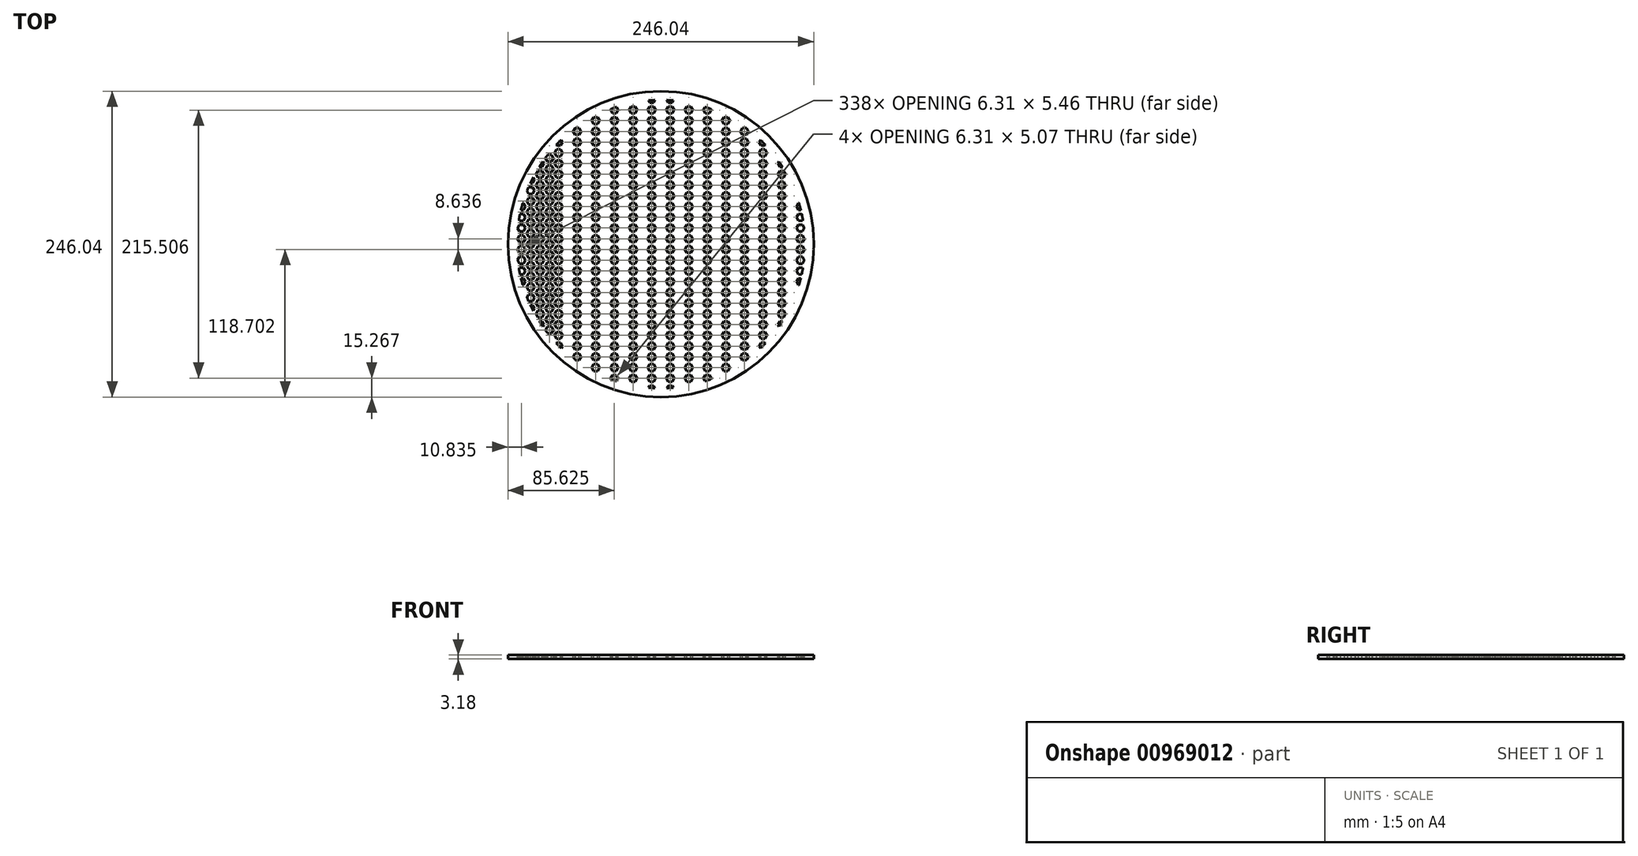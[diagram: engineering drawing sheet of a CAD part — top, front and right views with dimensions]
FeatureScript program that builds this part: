
annotation { "Feature Type Name" : "Feature", "Feature Type Description" : "" }
export const myFeature = defineFeature(function(context is Context, id is Id, definition is map)
    precondition{}
    {
        {
            var Q0;
            Q0=qCreatedBy(makeId("Top.planeOp"),FACE);
            var sketch = newSketch(context, id + "F0", { "sketchPlane" : qUnion([Q0])});
            skCircle(sketch, "E0", {"center": v(0, 0) * mm, "radius": 123.02 * mm});
            skSolve(sketch);
        }
        {
            var Q0;
            Q0=qSketchRegion(id+"F0",true);
            extrude(context, id + "F1", {"entities" : qUnion([Q0]), "depth" : 3.17 * mm, "offsetDistance" : 25.4 * mm});
        }
        {
            var Q0;
            Q0=makeQuery(id+"F1.opExtrude","CAP_FACE",FACE,{"disambiguationData":[OSD([sQuery(id+"F0.wireOp",EDGE,"E0")])],"isStart":false});
            var sketch = newSketch(context, id + "F2", { "sketchPlane" : qUnion([Q0])});
            skPoint(sketch, "E1.0.midPoint", {"position": v(-127.14, -131.13) * mm});
            skCircle(sketch, "E2.cCircle", {"center": v(-119.66, -129.54) * mm, "radius": 2.73 * mm, "construction": true});
            skLineSegment(sketch, "E2.0", {"start": v(-121.24, -126.8) * mm, "end": v(-118.09, -126.8) * mm});
            skLineSegment(sketch, "E2.1", {"start": v(-118.09, -126.8) * mm, "end": v(-116.51, -129.54) * mm});
            skLineSegment(sketch, "E2.2", {"start": v(-116.51, -129.54) * mm, "end": v(-118.09, -132.27) * mm});
            skLineSegment(sketch, "E2.3", {"start": v(-118.09, -132.27) * mm, "end": v(-121.24, -132.27) * mm});
            skLineSegment(sketch, "E2.4", {"start": v(-121.24, -132.27) * mm, "end": v(-122.82, -129.54) * mm});
            skLineSegment(sketch, "E2.5", {"start": v(-122.82, -129.54) * mm, "end": v(-121.24, -126.8) * mm});
            skPoint(sketch, "E2.0.midPoint", {"position": v(-119.66, -126.8) * mm});
            skLineSegment(sketch, "E3.0.2.0", {"start": v(-128.72, -113.86) * mm, "end": v(-125.57, -113.86) * mm});
            skLineSegment(sketch, "E3.0.2.1", {"start": v(-125.57, -113.86) * mm, "end": v(-124, -116.59) * mm});
            skLineSegment(sketch, "E3.0.2.2", {"start": v(-124, -116.59) * mm, "end": v(-125.57, -119.32) * mm});
            skCircle(sketch, "E3.0.2.3", {"center": v(-127.14, -116.59) * mm, "radius": 2.73 * mm, "construction": true});
            skLineSegment(sketch, "E3.0.2.4", {"start": v(-125.57, -119.32) * mm, "end": v(-128.72, -119.32) * mm});
            skLineSegment(sketch, "E3.0.2.5", {"start": v(-128.72, -119.32) * mm, "end": v(-130.3, -116.59) * mm});
            skLineSegment(sketch, "E3.0.2.6", {"start": v(-130.3, -116.59) * mm, "end": v(-128.72, -113.86) * mm});
            skLineSegment(sketch, "E3.1.0.0", {"start": v(-113.76, -131.13) * mm, "end": v(-110.6, -131.13) * mm});
            skLineSegment(sketch, "E3.1.0.1", {"start": v(-110.6, -131.13) * mm, "end": v(-109.03, -133.86) * mm});
            skLineSegment(sketch, "E3.1.0.2", {"start": v(-109.03, -133.86) * mm, "end": v(-110.6, -136.59) * mm});
            skCircle(sketch, "E3.1.0.3", {"center": v(-112.19, -133.86) * mm, "radius": 2.73 * mm, "construction": true});
            skLineSegment(sketch, "E3.1.0.4", {"start": v(-110.6, -136.59) * mm, "end": v(-113.76, -136.59) * mm});
            skLineSegment(sketch, "E3.1.0.5", {"start": v(-113.76, -136.59) * mm, "end": v(-115.34, -133.86) * mm});
            skLineSegment(sketch, "E3.1.0.6", {"start": v(-115.34, -133.86) * mm, "end": v(-113.76, -131.13) * mm});
            skLineSegment(sketch, "E3.1.1.0", {"start": v(-113.76, -122.5) * mm, "end": v(-110.6, -122.5) * mm});
            skLineSegment(sketch, "E3.1.1.1", {"start": v(-110.6, -122.5) * mm, "end": v(-109.03, -125.22) * mm});
            skLineSegment(sketch, "E3.1.1.2", {"start": v(-109.03, -125.22) * mm, "end": v(-110.6, -127.95) * mm});
            skCircle(sketch, "E3.1.1.3", {"center": v(-112.19, -125.22) * mm, "radius": 2.73 * mm, "construction": true});
            skLineSegment(sketch, "E3.1.1.4", {"start": v(-110.6, -127.95) * mm, "end": v(-113.76, -127.95) * mm});
            skLineSegment(sketch, "E3.1.1.5", {"start": v(-113.76, -127.95) * mm, "end": v(-115.34, -125.22) * mm});
            skLineSegment(sketch, "E3.1.1.6", {"start": v(-115.34, -125.22) * mm, "end": v(-113.76, -122.5) * mm});
            skLineSegment(sketch, "E3.1.2.0", {"start": v(-113.76, -113.86) * mm, "end": v(-110.6, -113.86) * mm});
            skLineSegment(sketch, "E3.1.2.1", {"start": v(-110.6, -113.86) * mm, "end": v(-109.03, -116.59) * mm});
            skLineSegment(sketch, "E3.1.2.2", {"start": v(-109.03, -116.59) * mm, "end": v(-110.6, -119.32) * mm});
            skCircle(sketch, "E3.1.2.3", {"center": v(-112.19, -116.59) * mm, "radius": 2.73 * mm, "construction": true});
            skLineSegment(sketch, "E3.1.2.4", {"start": v(-110.6, -119.32) * mm, "end": v(-113.76, -119.32) * mm});
            skLineSegment(sketch, "E3.1.2.5", {"start": v(-113.76, -119.32) * mm, "end": v(-115.34, -116.59) * mm});
            skLineSegment(sketch, "E3.1.2.6", {"start": v(-115.34, -116.59) * mm, "end": v(-113.76, -113.86) * mm});
            skLineSegment(sketch, "E3.2.0.0", {"start": v(-98.8, -131.13) * mm, "end": v(-95.65, -131.13) * mm});
            skLineSegment(sketch, "E3.2.0.1", {"start": v(-95.65, -131.13) * mm, "end": v(-94.07, -133.86) * mm});
            skLineSegment(sketch, "E3.2.0.2", {"start": v(-94.07, -133.86) * mm, "end": v(-95.65, -136.59) * mm});
            skCircle(sketch, "E3.2.0.3", {"center": v(-97.23, -133.86) * mm, "radius": 2.73 * mm, "construction": true});
            skLineSegment(sketch, "E3.2.0.4", {"start": v(-95.65, -136.59) * mm, "end": v(-98.8, -136.59) * mm});
            skLineSegment(sketch, "E3.2.0.5", {"start": v(-98.8, -136.59) * mm, "end": v(-100.38, -133.86) * mm});
            skLineSegment(sketch, "E3.2.0.6", {"start": v(-100.38, -133.86) * mm, "end": v(-98.8, -131.13) * mm});
            skLineSegment(sketch, "E3.2.1.0", {"start": v(-98.8, -122.5) * mm, "end": v(-95.65, -122.5) * mm});
            skLineSegment(sketch, "E3.2.1.1", {"start": v(-95.65, -122.5) * mm, "end": v(-94.07, -125.22) * mm});
            skLineSegment(sketch, "E3.2.1.2", {"start": v(-94.07, -125.22) * mm, "end": v(-95.65, -127.95) * mm});
            skCircle(sketch, "E3.2.1.3", {"center": v(-97.23, -125.22) * mm, "radius": 2.73 * mm, "construction": true});
            skLineSegment(sketch, "E3.2.1.4", {"start": v(-95.65, -127.95) * mm, "end": v(-98.8, -127.95) * mm});
            skLineSegment(sketch, "E3.2.1.5", {"start": v(-98.8, -127.95) * mm, "end": v(-100.38, -125.22) * mm});
            skLineSegment(sketch, "E3.2.1.6", {"start": v(-100.38, -125.22) * mm, "end": v(-98.8, -122.5) * mm});
            skLineSegment(sketch, "E3.2.2.0", {"start": v(-98.8, -113.86) * mm, "end": v(-95.65, -113.86) * mm});
            skLineSegment(sketch, "E3.2.2.1", {"start": v(-95.65, -113.86) * mm, "end": v(-94.07, -116.59) * mm});
            skLineSegment(sketch, "E3.2.2.2", {"start": v(-94.07, -116.59) * mm, "end": v(-95.65, -119.32) * mm});
            skCircle(sketch, "E3.2.2.3", {"center": v(-97.23, -116.59) * mm, "radius": 2.73 * mm, "construction": true});
            skLineSegment(sketch, "E3.2.2.4", {"start": v(-95.65, -119.32) * mm, "end": v(-98.8, -119.32) * mm});
            skLineSegment(sketch, "E3.2.2.5", {"start": v(-98.8, -119.32) * mm, "end": v(-100.38, -116.59) * mm});
            skLineSegment(sketch, "E3.2.2.6", {"start": v(-100.38, -116.59) * mm, "end": v(-98.8, -113.86) * mm});
            skLineSegment(sketch, "E4.0.0.3", {"start": v(-128.72, -105.22) * mm, "end": v(-125.57, -105.22) * mm});
            skLineSegment(sketch, "E4.3.0.3", {"start": v(-125.57, -105.22) * mm, "end": v(-124, -107.95) * mm});
            skLineSegment(sketch, "E4.6.0.3", {"start": v(-124, -107.95) * mm, "end": v(-125.57, -110.68) * mm});
            skCircle(sketch, "E4.9.0.3", {"center": v(-127.14, -107.95) * mm, "radius": 2.73 * mm, "construction": true});
            skLineSegment(sketch, "E4.11.0.3", {"start": v(-125.57, -110.68) * mm, "end": v(-128.72, -110.68) * mm});
            skLineSegment(sketch, "E4.14.0.3", {"start": v(-128.72, -110.68) * mm, "end": v(-130.3, -107.95) * mm});
            skLineSegment(sketch, "E4.17.0.3", {"start": v(-130.3, -107.95) * mm, "end": v(-128.72, -105.22) * mm});
            skLineSegment(sketch, "E4.0.1.3", {"start": v(-113.76, -105.22) * mm, "end": v(-110.6, -105.22) * mm});
            skLineSegment(sketch, "E4.3.1.3", {"start": v(-110.6, -105.22) * mm, "end": v(-109.03, -107.95) * mm});
            skLineSegment(sketch, "E4.6.1.3", {"start": v(-109.03, -107.95) * mm, "end": v(-110.6, -110.68) * mm});
            skCircle(sketch, "E4.9.1.3", {"center": v(-112.19, -107.95) * mm, "radius": 2.73 * mm, "construction": true});
            skLineSegment(sketch, "E4.11.1.3", {"start": v(-110.6, -110.68) * mm, "end": v(-113.76, -110.68) * mm});
            skLineSegment(sketch, "E4.14.1.3", {"start": v(-113.76, -110.68) * mm, "end": v(-115.34, -107.95) * mm});
            skLineSegment(sketch, "E4.17.1.3", {"start": v(-115.34, -107.95) * mm, "end": v(-113.76, -105.22) * mm});
            skLineSegment(sketch, "E4.0.2.3", {"start": v(-98.8, -105.22) * mm, "end": v(-95.65, -105.22) * mm});
            skLineSegment(sketch, "E4.3.2.3", {"start": v(-95.65, -105.22) * mm, "end": v(-94.07, -107.95) * mm});
            skLineSegment(sketch, "E4.6.2.3", {"start": v(-94.07, -107.95) * mm, "end": v(-95.65, -110.68) * mm});
            skCircle(sketch, "E4.9.2.3", {"center": v(-97.23, -107.95) * mm, "radius": 2.73 * mm, "construction": true});
            skLineSegment(sketch, "E4.11.2.3", {"start": v(-95.65, -110.68) * mm, "end": v(-98.8, -110.68) * mm});
            skLineSegment(sketch, "E4.14.2.3", {"start": v(-98.8, -110.68) * mm, "end": v(-100.38, -107.95) * mm});
            skLineSegment(sketch, "E4.17.2.3", {"start": v(-100.38, -107.95) * mm, "end": v(-98.8, -105.22) * mm});
            skCircle(sketch, "E5.0.1.0", {"center": v(-119.66, -120.9) * mm, "radius": 2.73 * mm, "construction": true});
            skLineSegment(sketch, "E5.0.1.1", {"start": v(-122.82, -120.9) * mm, "end": v(-121.24, -118.17) * mm});
            skLineSegment(sketch, "E5.0.1.2", {"start": v(-121.24, -118.17) * mm, "end": v(-118.09, -118.17) * mm});
            skLineSegment(sketch, "E5.0.1.3", {"start": v(-118.09, -118.17) * mm, "end": v(-116.51, -120.9) * mm});
            skLineSegment(sketch, "E5.0.1.4", {"start": v(-116.51, -120.9) * mm, "end": v(-118.09, -123.63) * mm});
            skLineSegment(sketch, "E5.0.1.5", {"start": v(-118.09, -123.63) * mm, "end": v(-121.24, -123.63) * mm});
            skLineSegment(sketch, "E5.0.1.6", {"start": v(-121.24, -123.63) * mm, "end": v(-122.82, -120.9) * mm});
            skCircle(sketch, "E5.0.2.0", {"center": v(-119.66, -112.27) * mm, "radius": 2.73 * mm, "construction": true});
            skLineSegment(sketch, "E5.0.2.1", {"start": v(-122.82, -112.27) * mm, "end": v(-121.24, -109.54) * mm});
            skLineSegment(sketch, "E5.0.2.2", {"start": v(-121.24, -109.54) * mm, "end": v(-118.09, -109.54) * mm});
            skLineSegment(sketch, "E5.0.2.3", {"start": v(-118.09, -109.54) * mm, "end": v(-116.51, -112.27) * mm});
            skLineSegment(sketch, "E5.0.2.4", {"start": v(-116.51, -112.27) * mm, "end": v(-118.09, -115) * mm});
            skLineSegment(sketch, "E5.0.2.5", {"start": v(-118.09, -115) * mm, "end": v(-121.24, -115) * mm});
            skLineSegment(sketch, "E5.0.2.6", {"start": v(-121.24, -115) * mm, "end": v(-122.82, -112.27) * mm});
            skCircle(sketch, "E5.0.3.0", {"center": v(-119.66, -103.63) * mm, "radius": 2.73 * mm, "construction": true});
            skLineSegment(sketch, "E5.0.3.1", {"start": v(-122.82, -103.63) * mm, "end": v(-121.24, -100.9) * mm});
            skLineSegment(sketch, "E5.0.3.2", {"start": v(-121.24, -100.9) * mm, "end": v(-118.09, -100.9) * mm});
            skLineSegment(sketch, "E5.0.3.3", {"start": v(-118.09, -100.9) * mm, "end": v(-116.51, -103.63) * mm});
            skLineSegment(sketch, "E5.0.3.4", {"start": v(-116.51, -103.63) * mm, "end": v(-118.09, -106.36) * mm});
            skLineSegment(sketch, "E5.0.3.5", {"start": v(-118.09, -106.36) * mm, "end": v(-121.24, -106.36) * mm});
            skLineSegment(sketch, "E5.0.3.6", {"start": v(-121.24, -106.36) * mm, "end": v(-122.82, -103.63) * mm});
            skCircle(sketch, "E5.1.0.0", {"center": v(-104.7, -129.54) * mm, "radius": 2.73 * mm, "construction": true});
            skLineSegment(sketch, "E5.1.0.1", {"start": v(-107.86, -129.54) * mm, "end": v(-106.28, -126.8) * mm});
            skLineSegment(sketch, "E5.1.0.2", {"start": v(-106.28, -126.8) * mm, "end": v(-103.13, -126.8) * mm});
            skLineSegment(sketch, "E5.1.0.3", {"start": v(-103.13, -126.8) * mm, "end": v(-101.55, -129.54) * mm});
            skLineSegment(sketch, "E5.1.0.4", {"start": v(-101.55, -129.54) * mm, "end": v(-103.13, -132.27) * mm});
            skLineSegment(sketch, "E5.1.0.5", {"start": v(-103.13, -132.27) * mm, "end": v(-106.28, -132.27) * mm});
            skLineSegment(sketch, "E5.1.0.6", {"start": v(-106.28, -132.27) * mm, "end": v(-107.86, -129.54) * mm});
            skCircle(sketch, "E5.1.1.0", {"center": v(-104.7, -120.9) * mm, "radius": 2.73 * mm, "construction": true});
            skLineSegment(sketch, "E5.1.1.1", {"start": v(-107.86, -120.9) * mm, "end": v(-106.28, -118.17) * mm});
            skLineSegment(sketch, "E5.1.1.2", {"start": v(-106.28, -118.17) * mm, "end": v(-103.13, -118.17) * mm});
            skLineSegment(sketch, "E5.1.1.3", {"start": v(-103.13, -118.17) * mm, "end": v(-101.55, -120.9) * mm});
            skLineSegment(sketch, "E5.1.1.4", {"start": v(-101.55, -120.9) * mm, "end": v(-103.13, -123.63) * mm});
            skLineSegment(sketch, "E5.1.1.5", {"start": v(-103.13, -123.63) * mm, "end": v(-106.28, -123.63) * mm});
            skLineSegment(sketch, "E5.1.1.6", {"start": v(-106.28, -123.63) * mm, "end": v(-107.86, -120.9) * mm});
            skCircle(sketch, "E5.1.2.0", {"center": v(-104.7, -112.27) * mm, "radius": 2.73 * mm, "construction": true});
            skLineSegment(sketch, "E5.1.2.1", {"start": v(-107.86, -112.27) * mm, "end": v(-106.28, -109.54) * mm});
            skLineSegment(sketch, "E5.1.2.2", {"start": v(-106.28, -109.54) * mm, "end": v(-103.13, -109.54) * mm});
            skLineSegment(sketch, "E5.1.2.3", {"start": v(-103.13, -109.54) * mm, "end": v(-101.55, -112.27) * mm});
            skLineSegment(sketch, "E5.1.2.4", {"start": v(-101.55, -112.27) * mm, "end": v(-103.13, -115) * mm});
            skLineSegment(sketch, "E5.1.2.5", {"start": v(-103.13, -115) * mm, "end": v(-106.28, -115) * mm});
            skLineSegment(sketch, "E5.1.2.6", {"start": v(-106.28, -115) * mm, "end": v(-107.86, -112.27) * mm});
            skCircle(sketch, "E5.1.3.0", {"center": v(-104.7, -103.63) * mm, "radius": 2.73 * mm, "construction": true});
            skLineSegment(sketch, "E5.1.3.1", {"start": v(-107.86, -103.63) * mm, "end": v(-106.28, -100.9) * mm});
            skLineSegment(sketch, "E5.1.3.2", {"start": v(-106.28, -100.9) * mm, "end": v(-103.13, -100.9) * mm});
            skLineSegment(sketch, "E5.1.3.3", {"start": v(-103.13, -100.9) * mm, "end": v(-101.55, -103.63) * mm});
            skLineSegment(sketch, "E5.1.3.4", {"start": v(-101.55, -103.63) * mm, "end": v(-103.13, -106.36) * mm});
            skLineSegment(sketch, "E5.1.3.5", {"start": v(-103.13, -106.36) * mm, "end": v(-106.28, -106.36) * mm});
            skLineSegment(sketch, "E5.1.3.6", {"start": v(-106.28, -106.36) * mm, "end": v(-107.86, -103.63) * mm});
            skLineSegment(sketch, "E5.direction1", {"start": v(-121.24, -132.27) * mm, "end": v(-106.28, -132.27) * mm, "construction": true});
            skLineSegment(sketch, "E5.direction2", {"start": v(-121.24, -132.27) * mm, "end": v(-121.24, -123.63) * mm, "construction": true});
            skLineSegment(sketch, "E6.0.3.0", {"start": v(-83.85, -131.13) * mm, "end": v(-80.7, -131.13) * mm});
            skLineSegment(sketch, "E6.3.3.0", {"start": v(-80.7, -131.13) * mm, "end": v(-79.12, -133.86) * mm});
            skLineSegment(sketch, "E6.6.3.0", {"start": v(-79.12, -133.86) * mm, "end": v(-80.7, -136.59) * mm});
            skCircle(sketch, "E6.9.3.0", {"center": v(-82.27, -133.86) * mm, "radius": 2.73 * mm, "construction": true});
            skLineSegment(sketch, "E6.11.3.0", {"start": v(-80.7, -136.59) * mm, "end": v(-83.85, -136.59) * mm});
            skLineSegment(sketch, "E6.14.3.0", {"start": v(-83.85, -136.59) * mm, "end": v(-85.42, -133.86) * mm});
            skLineSegment(sketch, "E6.17.3.0", {"start": v(-85.42, -133.86) * mm, "end": v(-83.85, -131.13) * mm});
            skLineSegment(sketch, "E6.0.3.1", {"start": v(-83.85, -122.5) * mm, "end": v(-80.7, -122.5) * mm});
            skLineSegment(sketch, "E6.3.3.1", {"start": v(-80.7, -122.5) * mm, "end": v(-79.12, -125.22) * mm});
            skLineSegment(sketch, "E6.6.3.1", {"start": v(-79.12, -125.22) * mm, "end": v(-80.7, -127.95) * mm});
            skCircle(sketch, "E6.9.3.1", {"center": v(-82.27, -125.22) * mm, "radius": 2.73 * mm, "construction": true});
            skLineSegment(sketch, "E6.11.3.1", {"start": v(-80.7, -127.95) * mm, "end": v(-83.85, -127.95) * mm});
            skLineSegment(sketch, "E6.14.3.1", {"start": v(-83.85, -127.95) * mm, "end": v(-85.42, -125.22) * mm});
            skLineSegment(sketch, "E6.17.3.1", {"start": v(-85.42, -125.22) * mm, "end": v(-83.85, -122.5) * mm});
            skLineSegment(sketch, "E6.0.3.2", {"start": v(-83.85, -113.86) * mm, "end": v(-80.7, -113.86) * mm});
            skLineSegment(sketch, "E6.3.3.2", {"start": v(-80.7, -113.86) * mm, "end": v(-79.12, -116.59) * mm});
            skLineSegment(sketch, "E6.6.3.2", {"start": v(-79.12, -116.59) * mm, "end": v(-80.7, -119.32) * mm});
            skCircle(sketch, "E6.9.3.2", {"center": v(-82.27, -116.59) * mm, "radius": 2.73 * mm, "construction": true});
            skLineSegment(sketch, "E6.11.3.2", {"start": v(-80.7, -119.32) * mm, "end": v(-83.85, -119.32) * mm});
            skLineSegment(sketch, "E6.14.3.2", {"start": v(-83.85, -119.32) * mm, "end": v(-85.42, -116.59) * mm});
            skLineSegment(sketch, "E6.17.3.2", {"start": v(-85.42, -116.59) * mm, "end": v(-83.85, -113.86) * mm});
            skLineSegment(sketch, "E6.0.3.3", {"start": v(-83.85, -105.22) * mm, "end": v(-80.7, -105.22) * mm});
            skLineSegment(sketch, "E6.3.3.3", {"start": v(-80.7, -105.22) * mm, "end": v(-79.12, -107.95) * mm});
            skLineSegment(sketch, "E6.6.3.3", {"start": v(-79.12, -107.95) * mm, "end": v(-80.7, -110.68) * mm});
            skCircle(sketch, "E6.9.3.3", {"center": v(-82.27, -107.95) * mm, "radius": 2.73 * mm, "construction": true});
            skLineSegment(sketch, "E6.11.3.3", {"start": v(-80.7, -110.68) * mm, "end": v(-83.85, -110.68) * mm});
            skLineSegment(sketch, "E6.14.3.3", {"start": v(-83.85, -110.68) * mm, "end": v(-85.42, -107.95) * mm});
            skLineSegment(sketch, "E6.17.3.3", {"start": v(-85.42, -107.95) * mm, "end": v(-83.85, -105.22) * mm});
            skLineSegment(sketch, "E6.0.4.0", {"start": v(-68.89, -131.13) * mm, "end": v(-65.73, -131.13) * mm});
            skLineSegment(sketch, "E6.3.4.0", {"start": v(-65.73, -131.13) * mm, "end": v(-64.16, -133.86) * mm});
            skLineSegment(sketch, "E6.6.4.0", {"start": v(-64.16, -133.86) * mm, "end": v(-65.73, -136.59) * mm});
            skCircle(sketch, "E6.9.4.0", {"center": v(-67.31, -133.86) * mm, "radius": 2.73 * mm, "construction": true});
            skLineSegment(sketch, "E6.11.4.0", {"start": v(-65.73, -136.59) * mm, "end": v(-68.89, -136.59) * mm});
            skLineSegment(sketch, "E6.14.4.0", {"start": v(-68.89, -136.59) * mm, "end": v(-70.46, -133.86) * mm});
            skLineSegment(sketch, "E6.17.4.0", {"start": v(-70.46, -133.86) * mm, "end": v(-68.89, -131.13) * mm});
            skLineSegment(sketch, "E6.0.4.1", {"start": v(-68.89, -122.5) * mm, "end": v(-65.73, -122.5) * mm});
            skLineSegment(sketch, "E6.3.4.1", {"start": v(-65.73, -122.5) * mm, "end": v(-64.16, -125.22) * mm});
            skLineSegment(sketch, "E6.6.4.1", {"start": v(-64.16, -125.22) * mm, "end": v(-65.73, -127.95) * mm});
            skCircle(sketch, "E6.9.4.1", {"center": v(-67.31, -125.22) * mm, "radius": 2.73 * mm, "construction": true});
            skLineSegment(sketch, "E6.11.4.1", {"start": v(-65.73, -127.95) * mm, "end": v(-68.89, -127.95) * mm});
            skLineSegment(sketch, "E6.14.4.1", {"start": v(-68.89, -127.95) * mm, "end": v(-70.46, -125.22) * mm});
            skLineSegment(sketch, "E6.17.4.1", {"start": v(-70.46, -125.22) * mm, "end": v(-68.89, -122.5) * mm});
            skLineSegment(sketch, "E6.0.4.2", {"start": v(-68.89, -113.86) * mm, "end": v(-65.73, -113.86) * mm});
            skLineSegment(sketch, "E6.3.4.2", {"start": v(-65.73, -113.86) * mm, "end": v(-64.16, -116.59) * mm});
            skLineSegment(sketch, "E6.6.4.2", {"start": v(-64.16, -116.59) * mm, "end": v(-65.73, -119.32) * mm});
            skCircle(sketch, "E6.9.4.2", {"center": v(-67.31, -116.59) * mm, "radius": 2.73 * mm, "construction": true});
            skLineSegment(sketch, "E6.11.4.2", {"start": v(-65.73, -119.32) * mm, "end": v(-68.89, -119.32) * mm});
            skLineSegment(sketch, "E6.14.4.2", {"start": v(-68.89, -119.32) * mm, "end": v(-70.46, -116.59) * mm});
            skLineSegment(sketch, "E6.17.4.2", {"start": v(-70.46, -116.59) * mm, "end": v(-68.89, -113.86) * mm});
            skLineSegment(sketch, "E6.0.4.3", {"start": v(-68.89, -105.22) * mm, "end": v(-65.73, -105.22) * mm});
            skLineSegment(sketch, "E6.3.4.3", {"start": v(-65.73, -105.22) * mm, "end": v(-64.16, -107.95) * mm});
            skLineSegment(sketch, "E6.6.4.3", {"start": v(-64.16, -107.95) * mm, "end": v(-65.73, -110.68) * mm});
            skCircle(sketch, "E6.9.4.3", {"center": v(-67.31, -107.95) * mm, "radius": 2.73 * mm, "construction": true});
            skLineSegment(sketch, "E6.11.4.3", {"start": v(-65.73, -110.68) * mm, "end": v(-68.89, -110.68) * mm});
            skLineSegment(sketch, "E6.14.4.3", {"start": v(-68.89, -110.68) * mm, "end": v(-70.46, -107.95) * mm});
            skLineSegment(sketch, "E6.17.4.3", {"start": v(-70.46, -107.95) * mm, "end": v(-68.89, -105.22) * mm});
            skLineSegment(sketch, "E6.0.5.0", {"start": v(-53.93, -131.13) * mm, "end": v(-50.78, -131.13) * mm});
            skLineSegment(sketch, "E6.3.5.0", {"start": v(-50.78, -131.13) * mm, "end": v(-49.2, -133.86) * mm});
            skLineSegment(sketch, "E6.6.5.0", {"start": v(-49.2, -133.86) * mm, "end": v(-50.78, -136.59) * mm});
            skCircle(sketch, "E6.9.5.0", {"center": v(-52.35, -133.86) * mm, "radius": 2.73 * mm, "construction": true});
            skLineSegment(sketch, "E6.11.5.0", {"start": v(-50.78, -136.59) * mm, "end": v(-53.93, -136.59) * mm});
            skLineSegment(sketch, "E6.14.5.0", {"start": v(-53.93, -136.59) * mm, "end": v(-55.5, -133.86) * mm});
            skLineSegment(sketch, "E6.17.5.0", {"start": v(-55.5, -133.86) * mm, "end": v(-53.93, -131.13) * mm});
            skLineSegment(sketch, "E6.0.5.1", {"start": v(-53.93, -122.5) * mm, "end": v(-50.78, -122.5) * mm});
            skLineSegment(sketch, "E6.3.5.1", {"start": v(-50.78, -122.5) * mm, "end": v(-49.2, -125.22) * mm});
            skLineSegment(sketch, "E6.6.5.1", {"start": v(-49.2, -125.22) * mm, "end": v(-50.78, -127.95) * mm});
            skCircle(sketch, "E6.9.5.1", {"center": v(-52.35, -125.22) * mm, "radius": 2.73 * mm, "construction": true});
            skLineSegment(sketch, "E6.11.5.1", {"start": v(-50.78, -127.95) * mm, "end": v(-53.93, -127.95) * mm});
            skLineSegment(sketch, "E6.14.5.1", {"start": v(-53.93, -127.95) * mm, "end": v(-55.5, -125.22) * mm});
            skLineSegment(sketch, "E6.17.5.1", {"start": v(-55.5, -125.22) * mm, "end": v(-53.93, -122.5) * mm});
            skLineSegment(sketch, "E6.0.5.2", {"start": v(-53.93, -113.86) * mm, "end": v(-50.78, -113.86) * mm});
            skLineSegment(sketch, "E6.3.5.2", {"start": v(-50.78, -113.86) * mm, "end": v(-49.2, -116.59) * mm});
            skLineSegment(sketch, "E6.6.5.2", {"start": v(-49.2, -116.59) * mm, "end": v(-50.78, -119.32) * mm});
            skCircle(sketch, "E6.9.5.2", {"center": v(-52.35, -116.59) * mm, "radius": 2.73 * mm, "construction": true});
            skLineSegment(sketch, "E6.11.5.2", {"start": v(-50.78, -119.32) * mm, "end": v(-53.93, -119.32) * mm});
            skLineSegment(sketch, "E6.14.5.2", {"start": v(-53.93, -119.32) * mm, "end": v(-55.5, -116.59) * mm});
            skLineSegment(sketch, "E6.17.5.2", {"start": v(-55.5, -116.59) * mm, "end": v(-53.93, -113.86) * mm});
            skLineSegment(sketch, "E6.0.5.3", {"start": v(-53.93, -105.22) * mm, "end": v(-50.78, -105.22) * mm});
            skLineSegment(sketch, "E6.3.5.3", {"start": v(-50.78, -105.22) * mm, "end": v(-49.2, -107.95) * mm});
            skLineSegment(sketch, "E6.6.5.3", {"start": v(-49.2, -107.95) * mm, "end": v(-50.78, -110.68) * mm});
            skCircle(sketch, "E6.9.5.3", {"center": v(-52.35, -107.95) * mm, "radius": 2.73 * mm, "construction": true});
            skLineSegment(sketch, "E6.11.5.3", {"start": v(-50.78, -110.68) * mm, "end": v(-53.93, -110.68) * mm});
            skLineSegment(sketch, "E6.14.5.3", {"start": v(-53.93, -110.68) * mm, "end": v(-55.5, -107.95) * mm});
            skLineSegment(sketch, "E6.17.5.3", {"start": v(-55.5, -107.95) * mm, "end": v(-53.93, -105.22) * mm});
            skCircle(sketch, "E7.0.2.0", {"center": v(-89.75, -129.54) * mm, "radius": 2.73 * mm, "construction": true});
            skLineSegment(sketch, "E7.2.2.0", {"start": v(-92.9, -129.54) * mm, "end": v(-91.32, -126.8) * mm});
            skLineSegment(sketch, "E7.5.2.0", {"start": v(-91.32, -126.8) * mm, "end": v(-88.17, -126.8) * mm});
            skLineSegment(sketch, "E7.8.2.0", {"start": v(-88.17, -126.8) * mm, "end": v(-86.6, -129.54) * mm});
            skLineSegment(sketch, "E7.11.2.0", {"start": v(-86.6, -129.54) * mm, "end": v(-88.17, -132.27) * mm});
            skLineSegment(sketch, "E7.14.2.0", {"start": v(-88.17, -132.27) * mm, "end": v(-91.32, -132.27) * mm});
            skLineSegment(sketch, "E7.17.2.0", {"start": v(-91.32, -132.27) * mm, "end": v(-92.9, -129.54) * mm});
            skCircle(sketch, "E7.0.2.1", {"center": v(-89.75, -120.9) * mm, "radius": 2.73 * mm, "construction": true});
            skLineSegment(sketch, "E7.2.2.1", {"start": v(-92.9, -120.9) * mm, "end": v(-91.32, -118.17) * mm});
            skLineSegment(sketch, "E7.5.2.1", {"start": v(-91.32, -118.17) * mm, "end": v(-88.17, -118.17) * mm});
            skLineSegment(sketch, "E7.8.2.1", {"start": v(-88.17, -118.17) * mm, "end": v(-86.6, -120.9) * mm});
            skLineSegment(sketch, "E7.11.2.1", {"start": v(-86.6, -120.9) * mm, "end": v(-88.17, -123.63) * mm});
            skLineSegment(sketch, "E7.14.2.1", {"start": v(-88.17, -123.63) * mm, "end": v(-91.32, -123.63) * mm});
            skLineSegment(sketch, "E7.17.2.1", {"start": v(-91.32, -123.63) * mm, "end": v(-92.9, -120.9) * mm});
            skCircle(sketch, "E7.0.2.2", {"center": v(-89.75, -112.27) * mm, "radius": 2.73 * mm, "construction": true});
            skLineSegment(sketch, "E7.2.2.2", {"start": v(-92.9, -112.27) * mm, "end": v(-91.32, -109.54) * mm});
            skLineSegment(sketch, "E7.5.2.2", {"start": v(-91.32, -109.54) * mm, "end": v(-88.17, -109.54) * mm});
            skLineSegment(sketch, "E7.8.2.2", {"start": v(-88.17, -109.54) * mm, "end": v(-86.6, -112.27) * mm});
            skLineSegment(sketch, "E7.11.2.2", {"start": v(-86.6, -112.27) * mm, "end": v(-88.17, -115) * mm});
            skLineSegment(sketch, "E7.14.2.2", {"start": v(-88.17, -115) * mm, "end": v(-91.32, -115) * mm});
            skLineSegment(sketch, "E7.17.2.2", {"start": v(-91.32, -115) * mm, "end": v(-92.9, -112.27) * mm});
            skCircle(sketch, "E7.0.2.3", {"center": v(-89.75, -103.63) * mm, "radius": 2.73 * mm, "construction": true});
            skLineSegment(sketch, "E7.2.2.3", {"start": v(-92.9, -103.63) * mm, "end": v(-91.32, -100.9) * mm});
            skLineSegment(sketch, "E7.5.2.3", {"start": v(-91.32, -100.9) * mm, "end": v(-88.17, -100.9) * mm});
            skLineSegment(sketch, "E7.8.2.3", {"start": v(-88.17, -100.9) * mm, "end": v(-86.6, -103.63) * mm});
            skLineSegment(sketch, "E7.11.2.3", {"start": v(-86.6, -103.63) * mm, "end": v(-88.17, -106.36) * mm});
            skLineSegment(sketch, "E7.14.2.3", {"start": v(-88.17, -106.36) * mm, "end": v(-91.32, -106.36) * mm});
            skLineSegment(sketch, "E7.17.2.3", {"start": v(-91.32, -106.36) * mm, "end": v(-92.9, -103.63) * mm});
            skLineSegment(sketch, "E8.0.0.4", {"start": v(-128.72, -96.58) * mm, "end": v(-125.57, -96.58) * mm});
            skLineSegment(sketch, "E8.3.0.4", {"start": v(-125.57, -96.58) * mm, "end": v(-124, -99.31) * mm});
            skLineSegment(sketch, "E8.6.0.4", {"start": v(-124, -99.31) * mm, "end": v(-125.57, -102.04) * mm});
            skCircle(sketch, "E8.9.0.4", {"center": v(-127.14, -99.31) * mm, "radius": 2.73 * mm, "construction": true});
            skLineSegment(sketch, "E8.11.0.4", {"start": v(-125.57, -102.04) * mm, "end": v(-128.72, -102.04) * mm});
            skLineSegment(sketch, "E8.14.0.4", {"start": v(-128.72, -102.04) * mm, "end": v(-130.3, -99.31) * mm});
            skLineSegment(sketch, "E8.17.0.4", {"start": v(-130.3, -99.31) * mm, "end": v(-128.72, -96.58) * mm});
            skLineSegment(sketch, "E8.0.0.5", {"start": v(-128.72, -87.95) * mm, "end": v(-125.57, -87.95) * mm});
            skLineSegment(sketch, "E8.3.0.5", {"start": v(-125.57, -87.95) * mm, "end": v(-124, -90.68) * mm});
            skLineSegment(sketch, "E8.6.0.5", {"start": v(-124, -90.68) * mm, "end": v(-125.57, -93.4) * mm});
            skCircle(sketch, "E8.9.0.5", {"center": v(-127.14, -90.68) * mm, "radius": 2.73 * mm, "construction": true});
            skLineSegment(sketch, "E8.11.0.5", {"start": v(-125.57, -93.4) * mm, "end": v(-128.72, -93.4) * mm});
            skLineSegment(sketch, "E8.14.0.5", {"start": v(-128.72, -93.4) * mm, "end": v(-130.3, -90.68) * mm});
            skLineSegment(sketch, "E8.17.0.5", {"start": v(-130.3, -90.68) * mm, "end": v(-128.72, -87.95) * mm});
            skLineSegment(sketch, "E8.0.0.6", {"start": v(-128.72, -79.31) * mm, "end": v(-125.57, -79.31) * mm});
            skLineSegment(sketch, "E8.3.0.6", {"start": v(-125.57, -79.31) * mm, "end": v(-124, -82.04) * mm});
            skLineSegment(sketch, "E8.6.0.6", {"start": v(-124, -82.04) * mm, "end": v(-125.57, -84.77) * mm});
            skCircle(sketch, "E8.9.0.6", {"center": v(-127.14, -82.04) * mm, "radius": 2.73 * mm, "construction": true});
            skLineSegment(sketch, "E8.11.0.6", {"start": v(-125.57, -84.77) * mm, "end": v(-128.72, -84.77) * mm});
            skLineSegment(sketch, "E8.14.0.6", {"start": v(-128.72, -84.77) * mm, "end": v(-130.3, -82.04) * mm});
            skLineSegment(sketch, "E8.17.0.6", {"start": v(-130.3, -82.04) * mm, "end": v(-128.72, -79.31) * mm});
            skLineSegment(sketch, "E8.0.0.7", {"start": v(-128.72, -70.68) * mm, "end": v(-125.57, -70.68) * mm});
            skLineSegment(sketch, "E8.3.0.7", {"start": v(-125.57, -70.68) * mm, "end": v(-124, -73.4) * mm});
            skLineSegment(sketch, "E8.6.0.7", {"start": v(-124, -73.4) * mm, "end": v(-125.57, -76.14) * mm});
            skCircle(sketch, "E8.9.0.7", {"center": v(-127.14, -73.4) * mm, "radius": 2.73 * mm, "construction": true});
            skLineSegment(sketch, "E8.11.0.7", {"start": v(-125.57, -76.14) * mm, "end": v(-128.72, -76.14) * mm});
            skLineSegment(sketch, "E8.14.0.7", {"start": v(-128.72, -76.14) * mm, "end": v(-130.3, -73.4) * mm});
            skLineSegment(sketch, "E8.17.0.7", {"start": v(-130.3, -73.4) * mm, "end": v(-128.72, -70.68) * mm});
            skLineSegment(sketch, "E8.0.1.4", {"start": v(-113.76, -96.58) * mm, "end": v(-110.6, -96.58) * mm});
            skLineSegment(sketch, "E8.3.1.4", {"start": v(-110.6, -96.58) * mm, "end": v(-109.03, -99.31) * mm});
            skLineSegment(sketch, "E8.6.1.4", {"start": v(-109.03, -99.31) * mm, "end": v(-110.6, -102.04) * mm});
            skCircle(sketch, "E8.9.1.4", {"center": v(-112.19, -99.31) * mm, "radius": 2.73 * mm, "construction": true});
            skLineSegment(sketch, "E8.11.1.4", {"start": v(-110.6, -102.04) * mm, "end": v(-113.76, -102.04) * mm});
            skLineSegment(sketch, "E8.14.1.4", {"start": v(-113.76, -102.04) * mm, "end": v(-115.34, -99.31) * mm});
            skLineSegment(sketch, "E8.17.1.4", {"start": v(-115.34, -99.31) * mm, "end": v(-113.76, -96.58) * mm});
            skLineSegment(sketch, "E8.0.1.5", {"start": v(-113.76, -87.95) * mm, "end": v(-110.6, -87.95) * mm});
            skLineSegment(sketch, "E8.3.1.5", {"start": v(-110.6, -87.95) * mm, "end": v(-109.03, -90.68) * mm});
            skLineSegment(sketch, "E8.6.1.5", {"start": v(-109.03, -90.68) * mm, "end": v(-110.6, -93.4) * mm});
            skCircle(sketch, "E8.9.1.5", {"center": v(-112.19, -90.68) * mm, "radius": 2.73 * mm, "construction": true});
            skLineSegment(sketch, "E8.11.1.5", {"start": v(-110.6, -93.4) * mm, "end": v(-113.76, -93.4) * mm});
            skLineSegment(sketch, "E8.14.1.5", {"start": v(-113.76, -93.4) * mm, "end": v(-115.34, -90.68) * mm});
            skLineSegment(sketch, "E8.17.1.5", {"start": v(-115.34, -90.68) * mm, "end": v(-113.76, -87.95) * mm});
            skLineSegment(sketch, "E8.0.1.6", {"start": v(-113.76, -79.31) * mm, "end": v(-110.6, -79.31) * mm});
            skLineSegment(sketch, "E8.3.1.6", {"start": v(-110.6, -79.31) * mm, "end": v(-109.03, -82.04) * mm});
            skLineSegment(sketch, "E8.6.1.6", {"start": v(-109.03, -82.04) * mm, "end": v(-110.6, -84.77) * mm});
            skCircle(sketch, "E8.9.1.6", {"center": v(-112.19, -82.04) * mm, "radius": 2.73 * mm, "construction": true});
            skLineSegment(sketch, "E8.11.1.6", {"start": v(-110.6, -84.77) * mm, "end": v(-113.76, -84.77) * mm});
            skLineSegment(sketch, "E8.14.1.6", {"start": v(-113.76, -84.77) * mm, "end": v(-115.34, -82.04) * mm});
            skLineSegment(sketch, "E8.17.1.6", {"start": v(-115.34, -82.04) * mm, "end": v(-113.76, -79.31) * mm});
            skLineSegment(sketch, "E8.0.1.7", {"start": v(-113.76, -70.68) * mm, "end": v(-110.6, -70.68) * mm});
            skLineSegment(sketch, "E8.3.1.7", {"start": v(-110.6, -70.68) * mm, "end": v(-109.03, -73.4) * mm});
            skLineSegment(sketch, "E8.6.1.7", {"start": v(-109.03, -73.4) * mm, "end": v(-110.6, -76.14) * mm});
            skCircle(sketch, "E8.9.1.7", {"center": v(-112.19, -73.4) * mm, "radius": 2.73 * mm, "construction": true});
            skLineSegment(sketch, "E8.11.1.7", {"start": v(-110.6, -76.14) * mm, "end": v(-113.76, -76.14) * mm});
            skLineSegment(sketch, "E8.14.1.7", {"start": v(-113.76, -76.14) * mm, "end": v(-115.34, -73.4) * mm});
            skLineSegment(sketch, "E8.17.1.7", {"start": v(-115.34, -73.4) * mm, "end": v(-113.76, -70.68) * mm});
            skLineSegment(sketch, "E8.0.2.4", {"start": v(-98.8, -96.58) * mm, "end": v(-95.65, -96.58) * mm});
            skLineSegment(sketch, "E8.3.2.4", {"start": v(-95.65, -96.58) * mm, "end": v(-94.07, -99.31) * mm});
            skLineSegment(sketch, "E8.6.2.4", {"start": v(-94.07, -99.31) * mm, "end": v(-95.65, -102.04) * mm});
            skCircle(sketch, "E8.9.2.4", {"center": v(-97.23, -99.31) * mm, "radius": 2.73 * mm, "construction": true});
            skLineSegment(sketch, "E8.11.2.4", {"start": v(-95.65, -102.04) * mm, "end": v(-98.8, -102.04) * mm});
            skLineSegment(sketch, "E8.14.2.4", {"start": v(-98.8, -102.04) * mm, "end": v(-100.38, -99.31) * mm});
            skLineSegment(sketch, "E8.17.2.4", {"start": v(-100.38, -99.31) * mm, "end": v(-98.8, -96.58) * mm});
            skLineSegment(sketch, "E8.0.2.5", {"start": v(-98.8, -87.95) * mm, "end": v(-95.65, -87.95) * mm});
            skLineSegment(sketch, "E8.3.2.5", {"start": v(-95.65, -87.95) * mm, "end": v(-94.07, -90.68) * mm});
            skLineSegment(sketch, "E8.6.2.5", {"start": v(-94.07, -90.68) * mm, "end": v(-95.65, -93.4) * mm});
            skCircle(sketch, "E8.9.2.5", {"center": v(-97.23, -90.68) * mm, "radius": 2.73 * mm, "construction": true});
            skLineSegment(sketch, "E8.11.2.5", {"start": v(-95.65, -93.4) * mm, "end": v(-98.8, -93.4) * mm});
            skLineSegment(sketch, "E8.14.2.5", {"start": v(-98.8, -93.4) * mm, "end": v(-100.38, -90.68) * mm});
            skLineSegment(sketch, "E8.17.2.5", {"start": v(-100.38, -90.68) * mm, "end": v(-98.8, -87.95) * mm});
            skLineSegment(sketch, "E8.0.2.6", {"start": v(-98.8, -79.31) * mm, "end": v(-95.65, -79.31) * mm});
            skLineSegment(sketch, "E8.3.2.6", {"start": v(-95.65, -79.31) * mm, "end": v(-94.07, -82.04) * mm});
            skLineSegment(sketch, "E8.6.2.6", {"start": v(-94.07, -82.04) * mm, "end": v(-95.65, -84.77) * mm});
            skCircle(sketch, "E8.9.2.6", {"center": v(-97.23, -82.04) * mm, "radius": 2.73 * mm, "construction": true});
            skLineSegment(sketch, "E8.11.2.6", {"start": v(-95.65, -84.77) * mm, "end": v(-98.8, -84.77) * mm});
            skLineSegment(sketch, "E8.14.2.6", {"start": v(-98.8, -84.77) * mm, "end": v(-100.38, -82.04) * mm});
            skLineSegment(sketch, "E8.17.2.6", {"start": v(-100.38, -82.04) * mm, "end": v(-98.8, -79.31) * mm});
            skLineSegment(sketch, "E8.0.2.7", {"start": v(-98.8, -70.68) * mm, "end": v(-95.65, -70.68) * mm});
            skLineSegment(sketch, "E8.3.2.7", {"start": v(-95.65, -70.68) * mm, "end": v(-94.07, -73.4) * mm});
            skLineSegment(sketch, "E8.6.2.7", {"start": v(-94.07, -73.4) * mm, "end": v(-95.65, -76.14) * mm});
            skCircle(sketch, "E8.9.2.7", {"center": v(-97.23, -73.4) * mm, "radius": 2.73 * mm, "construction": true});
            skLineSegment(sketch, "E8.11.2.7", {"start": v(-95.65, -76.14) * mm, "end": v(-98.8, -76.14) * mm});
            skLineSegment(sketch, "E8.14.2.7", {"start": v(-98.8, -76.14) * mm, "end": v(-100.38, -73.4) * mm});
            skLineSegment(sketch, "E8.17.2.7", {"start": v(-100.38, -73.4) * mm, "end": v(-98.8, -70.68) * mm});
            skLineSegment(sketch, "E8.0.3.4", {"start": v(-83.85, -96.58) * mm, "end": v(-80.7, -96.58) * mm});
            skLineSegment(sketch, "E8.3.3.4", {"start": v(-80.7, -96.58) * mm, "end": v(-79.12, -99.31) * mm});
            skLineSegment(sketch, "E8.6.3.4", {"start": v(-79.12, -99.31) * mm, "end": v(-80.7, -102.04) * mm});
            skCircle(sketch, "E8.9.3.4", {"center": v(-82.27, -99.31) * mm, "radius": 2.73 * mm, "construction": true});
            skLineSegment(sketch, "E8.11.3.4", {"start": v(-80.7, -102.04) * mm, "end": v(-83.85, -102.04) * mm});
            skLineSegment(sketch, "E8.14.3.4", {"start": v(-83.85, -102.04) * mm, "end": v(-85.42, -99.31) * mm});
            skLineSegment(sketch, "E8.17.3.4", {"start": v(-85.42, -99.31) * mm, "end": v(-83.85, -96.58) * mm});
            skLineSegment(sketch, "E8.0.3.5", {"start": v(-83.85, -87.95) * mm, "end": v(-80.7, -87.95) * mm});
            skLineSegment(sketch, "E8.3.3.5", {"start": v(-80.7, -87.95) * mm, "end": v(-79.12, -90.68) * mm});
            skLineSegment(sketch, "E8.6.3.5", {"start": v(-79.12, -90.68) * mm, "end": v(-80.7, -93.4) * mm});
            skCircle(sketch, "E8.9.3.5", {"center": v(-82.27, -90.68) * mm, "radius": 2.73 * mm, "construction": true});
            skLineSegment(sketch, "E8.11.3.5", {"start": v(-80.7, -93.4) * mm, "end": v(-83.85, -93.4) * mm});
            skLineSegment(sketch, "E8.14.3.5", {"start": v(-83.85, -93.4) * mm, "end": v(-85.42, -90.68) * mm});
            skLineSegment(sketch, "E8.17.3.5", {"start": v(-85.42, -90.68) * mm, "end": v(-83.85, -87.95) * mm});
            skLineSegment(sketch, "E8.0.3.6", {"start": v(-83.85, -79.31) * mm, "end": v(-80.7, -79.31) * mm});
            skLineSegment(sketch, "E8.3.3.6", {"start": v(-80.7, -79.31) * mm, "end": v(-79.12, -82.04) * mm});
            skLineSegment(sketch, "E8.6.3.6", {"start": v(-79.12, -82.04) * mm, "end": v(-80.7, -84.77) * mm});
            skCircle(sketch, "E8.9.3.6", {"center": v(-82.27, -82.04) * mm, "radius": 2.73 * mm, "construction": true});
            skLineSegment(sketch, "E8.11.3.6", {"start": v(-80.7, -84.77) * mm, "end": v(-83.85, -84.77) * mm});
            skLineSegment(sketch, "E8.14.3.6", {"start": v(-83.85, -84.77) * mm, "end": v(-85.42, -82.04) * mm});
            skLineSegment(sketch, "E8.17.3.6", {"start": v(-85.42, -82.04) * mm, "end": v(-83.85, -79.31) * mm});
            skLineSegment(sketch, "E8.0.3.7", {"start": v(-83.85, -70.68) * mm, "end": v(-80.7, -70.68) * mm});
            skLineSegment(sketch, "E8.3.3.7", {"start": v(-80.7, -70.68) * mm, "end": v(-79.12, -73.4) * mm});
            skLineSegment(sketch, "E8.6.3.7", {"start": v(-79.12, -73.4) * mm, "end": v(-80.7, -76.14) * mm});
            skCircle(sketch, "E8.9.3.7", {"center": v(-82.27, -73.4) * mm, "radius": 2.73 * mm, "construction": true});
            skLineSegment(sketch, "E8.11.3.7", {"start": v(-80.7, -76.14) * mm, "end": v(-83.85, -76.14) * mm});
            skLineSegment(sketch, "E8.14.3.7", {"start": v(-83.85, -76.14) * mm, "end": v(-85.42, -73.4) * mm});
            skLineSegment(sketch, "E8.17.3.7", {"start": v(-85.42, -73.4) * mm, "end": v(-83.85, -70.68) * mm});
            skLineSegment(sketch, "E8.0.4.4", {"start": v(-68.89, -96.58) * mm, "end": v(-65.73, -96.58) * mm});
            skLineSegment(sketch, "E8.3.4.4", {"start": v(-65.73, -96.58) * mm, "end": v(-64.16, -99.31) * mm});
            skLineSegment(sketch, "E8.6.4.4", {"start": v(-64.16, -99.31) * mm, "end": v(-65.73, -102.04) * mm});
            skCircle(sketch, "E8.9.4.4", {"center": v(-67.31, -99.31) * mm, "radius": 2.73 * mm, "construction": true});
            skLineSegment(sketch, "E8.11.4.4", {"start": v(-65.73, -102.04) * mm, "end": v(-68.89, -102.04) * mm});
            skLineSegment(sketch, "E8.14.4.4", {"start": v(-68.89, -102.04) * mm, "end": v(-70.46, -99.31) * mm});
            skLineSegment(sketch, "E8.17.4.4", {"start": v(-70.46, -99.31) * mm, "end": v(-68.89, -96.58) * mm});
            skLineSegment(sketch, "E8.0.4.5", {"start": v(-68.89, -87.95) * mm, "end": v(-65.73, -87.95) * mm});
            skLineSegment(sketch, "E8.3.4.5", {"start": v(-65.73, -87.95) * mm, "end": v(-64.16, -90.68) * mm});
            skLineSegment(sketch, "E8.6.4.5", {"start": v(-64.16, -90.68) * mm, "end": v(-65.73, -93.4) * mm});
            skCircle(sketch, "E8.9.4.5", {"center": v(-67.31, -90.68) * mm, "radius": 2.73 * mm, "construction": true});
            skLineSegment(sketch, "E8.11.4.5", {"start": v(-65.73, -93.4) * mm, "end": v(-68.89, -93.4) * mm});
            skLineSegment(sketch, "E8.14.4.5", {"start": v(-68.89, -93.4) * mm, "end": v(-70.46, -90.68) * mm});
            skLineSegment(sketch, "E8.17.4.5", {"start": v(-70.46, -90.68) * mm, "end": v(-68.89, -87.95) * mm});
            skLineSegment(sketch, "E8.0.4.6", {"start": v(-68.89, -79.31) * mm, "end": v(-65.73, -79.31) * mm});
            skLineSegment(sketch, "E8.3.4.6", {"start": v(-65.73, -79.31) * mm, "end": v(-64.16, -82.04) * mm});
            skLineSegment(sketch, "E8.6.4.6", {"start": v(-64.16, -82.04) * mm, "end": v(-65.73, -84.77) * mm});
            skCircle(sketch, "E8.9.4.6", {"center": v(-67.31, -82.04) * mm, "radius": 2.73 * mm, "construction": true});
            skLineSegment(sketch, "E8.11.4.6", {"start": v(-65.73, -84.77) * mm, "end": v(-68.89, -84.77) * mm});
            skLineSegment(sketch, "E8.14.4.6", {"start": v(-68.89, -84.77) * mm, "end": v(-70.46, -82.04) * mm});
            skLineSegment(sketch, "E8.17.4.6", {"start": v(-70.46, -82.04) * mm, "end": v(-68.89, -79.31) * mm});
            skLineSegment(sketch, "E8.0.4.7", {"start": v(-68.89, -70.68) * mm, "end": v(-65.73, -70.68) * mm});
            skLineSegment(sketch, "E8.3.4.7", {"start": v(-65.73, -70.68) * mm, "end": v(-64.16, -73.4) * mm});
            skLineSegment(sketch, "E8.6.4.7", {"start": v(-64.16, -73.4) * mm, "end": v(-65.73, -76.14) * mm});
            skCircle(sketch, "E8.9.4.7", {"center": v(-67.31, -73.4) * mm, "radius": 2.73 * mm, "construction": true});
            skLineSegment(sketch, "E8.11.4.7", {"start": v(-65.73, -76.14) * mm, "end": v(-68.89, -76.14) * mm});
            skLineSegment(sketch, "E8.14.4.7", {"start": v(-68.89, -76.14) * mm, "end": v(-70.46, -73.4) * mm});
            skLineSegment(sketch, "E8.17.4.7", {"start": v(-70.46, -73.4) * mm, "end": v(-68.89, -70.68) * mm});
            skLineSegment(sketch, "E8.0.5.4", {"start": v(-53.93, -96.58) * mm, "end": v(-50.78, -96.58) * mm});
            skLineSegment(sketch, "E8.3.5.4", {"start": v(-50.78, -96.58) * mm, "end": v(-49.2, -99.31) * mm});
            skLineSegment(sketch, "E8.6.5.4", {"start": v(-49.2, -99.31) * mm, "end": v(-50.78, -102.04) * mm});
            skCircle(sketch, "E8.9.5.4", {"center": v(-52.35, -99.31) * mm, "radius": 2.73 * mm, "construction": true});
            skLineSegment(sketch, "E8.11.5.4", {"start": v(-50.78, -102.04) * mm, "end": v(-53.93, -102.04) * mm});
            skLineSegment(sketch, "E8.14.5.4", {"start": v(-53.93, -102.04) * mm, "end": v(-55.5, -99.31) * mm});
            skLineSegment(sketch, "E8.17.5.4", {"start": v(-55.5, -99.31) * mm, "end": v(-53.93, -96.58) * mm});
            skLineSegment(sketch, "E8.0.5.5", {"start": v(-53.93, -87.95) * mm, "end": v(-50.78, -87.95) * mm});
            skLineSegment(sketch, "E8.3.5.5", {"start": v(-50.78, -87.95) * mm, "end": v(-49.2, -90.68) * mm});
            skLineSegment(sketch, "E8.6.5.5", {"start": v(-49.2, -90.68) * mm, "end": v(-50.78, -93.4) * mm});
            skCircle(sketch, "E8.9.5.5", {"center": v(-52.35, -90.68) * mm, "radius": 2.73 * mm, "construction": true});
            skLineSegment(sketch, "E8.11.5.5", {"start": v(-50.78, -93.4) * mm, "end": v(-53.93, -93.4) * mm});
            skLineSegment(sketch, "E8.14.5.5", {"start": v(-53.93, -93.4) * mm, "end": v(-55.5, -90.68) * mm});
            skLineSegment(sketch, "E8.17.5.5", {"start": v(-55.5, -90.68) * mm, "end": v(-53.93, -87.95) * mm});
            skLineSegment(sketch, "E8.0.5.6", {"start": v(-53.93, -79.31) * mm, "end": v(-50.78, -79.31) * mm});
            skLineSegment(sketch, "E8.3.5.6", {"start": v(-50.78, -79.31) * mm, "end": v(-49.2, -82.04) * mm});
            skLineSegment(sketch, "E8.6.5.6", {"start": v(-49.2, -82.04) * mm, "end": v(-50.78, -84.77) * mm});
            skCircle(sketch, "E8.9.5.6", {"center": v(-52.35, -82.04) * mm, "radius": 2.73 * mm, "construction": true});
            skLineSegment(sketch, "E8.11.5.6", {"start": v(-50.78, -84.77) * mm, "end": v(-53.93, -84.77) * mm});
            skLineSegment(sketch, "E8.14.5.6", {"start": v(-53.93, -84.77) * mm, "end": v(-55.5, -82.04) * mm});
            skLineSegment(sketch, "E8.17.5.6", {"start": v(-55.5, -82.04) * mm, "end": v(-53.93, -79.31) * mm});
            skLineSegment(sketch, "E8.0.5.7", {"start": v(-53.93, -70.68) * mm, "end": v(-50.78, -70.68) * mm});
            skLineSegment(sketch, "E8.3.5.7", {"start": v(-50.78, -70.68) * mm, "end": v(-49.2, -73.4) * mm});
            skLineSegment(sketch, "E8.6.5.7", {"start": v(-49.2, -73.4) * mm, "end": v(-50.78, -76.14) * mm});
            skCircle(sketch, "E8.9.5.7", {"center": v(-52.35, -73.4) * mm, "radius": 2.73 * mm, "construction": true});
            skLineSegment(sketch, "E8.11.5.7", {"start": v(-50.78, -76.14) * mm, "end": v(-53.93, -76.14) * mm});
            skLineSegment(sketch, "E8.14.5.7", {"start": v(-53.93, -76.14) * mm, "end": v(-55.5, -73.4) * mm});
            skLineSegment(sketch, "E8.17.5.7", {"start": v(-55.5, -73.4) * mm, "end": v(-53.93, -70.68) * mm});
            skCircle(sketch, "E9.0.0.4", {"center": v(-119.66, -95) * mm, "radius": 2.73 * mm, "construction": true});
            skLineSegment(sketch, "E9.2.0.4", {"start": v(-122.82, -95) * mm, "end": v(-121.24, -92.27) * mm});
            skLineSegment(sketch, "E9.5.0.4", {"start": v(-121.24, -92.27) * mm, "end": v(-118.09, -92.27) * mm});
            skLineSegment(sketch, "E9.8.0.4", {"start": v(-118.09, -92.27) * mm, "end": v(-116.51, -95) * mm});
            skLineSegment(sketch, "E9.11.0.4", {"start": v(-116.51, -95) * mm, "end": v(-118.09, -97.73) * mm});
            skLineSegment(sketch, "E9.14.0.4", {"start": v(-118.09, -97.73) * mm, "end": v(-121.24, -97.73) * mm});
            skLineSegment(sketch, "E9.17.0.4", {"start": v(-121.24, -97.73) * mm, "end": v(-122.82, -95) * mm});
            skCircle(sketch, "E9.0.0.5", {"center": v(-119.66, -86.36) * mm, "radius": 2.73 * mm, "construction": true});
            skLineSegment(sketch, "E9.2.0.5", {"start": v(-122.82, -86.36) * mm, "end": v(-121.24, -83.63) * mm});
            skLineSegment(sketch, "E9.5.0.5", {"start": v(-121.24, -83.63) * mm, "end": v(-118.09, -83.63) * mm});
            skLineSegment(sketch, "E9.8.0.5", {"start": v(-118.09, -83.63) * mm, "end": v(-116.51, -86.36) * mm});
            skLineSegment(sketch, "E9.11.0.5", {"start": v(-116.51, -86.36) * mm, "end": v(-118.09, -89.1) * mm});
            skLineSegment(sketch, "E9.14.0.5", {"start": v(-118.09, -89.1) * mm, "end": v(-121.24, -89.1) * mm});
            skLineSegment(sketch, "E9.17.0.5", {"start": v(-121.24, -89.1) * mm, "end": v(-122.82, -86.36) * mm});
            skCircle(sketch, "E9.0.0.6", {"center": v(-119.66, -77.72) * mm, "radius": 2.73 * mm, "construction": true});
            skLineSegment(sketch, "E9.2.0.6", {"start": v(-122.82, -77.72) * mm, "end": v(-121.24, -75) * mm});
            skLineSegment(sketch, "E9.5.0.6", {"start": v(-121.24, -75) * mm, "end": v(-118.09, -75) * mm});
            skLineSegment(sketch, "E9.8.0.6", {"start": v(-118.09, -75) * mm, "end": v(-116.51, -77.72) * mm});
            skLineSegment(sketch, "E9.11.0.6", {"start": v(-116.51, -77.72) * mm, "end": v(-118.09, -80.45) * mm});
            skLineSegment(sketch, "E9.14.0.6", {"start": v(-118.09, -80.45) * mm, "end": v(-121.24, -80.45) * mm});
            skLineSegment(sketch, "E9.17.0.6", {"start": v(-121.24, -80.45) * mm, "end": v(-122.82, -77.72) * mm});
            skCircle(sketch, "E9.0.1.4", {"center": v(-104.7, -95) * mm, "radius": 2.73 * mm, "construction": true});
            skLineSegment(sketch, "E9.2.1.4", {"start": v(-107.86, -95) * mm, "end": v(-106.28, -92.27) * mm});
            skLineSegment(sketch, "E9.5.1.4", {"start": v(-106.28, -92.27) * mm, "end": v(-103.13, -92.27) * mm});
            skLineSegment(sketch, "E9.8.1.4", {"start": v(-103.13, -92.27) * mm, "end": v(-101.55, -95) * mm});
            skLineSegment(sketch, "E9.11.1.4", {"start": v(-101.55, -95) * mm, "end": v(-103.13, -97.73) * mm});
            skLineSegment(sketch, "E9.14.1.4", {"start": v(-103.13, -97.73) * mm, "end": v(-106.28, -97.73) * mm});
            skLineSegment(sketch, "E9.17.1.4", {"start": v(-106.28, -97.73) * mm, "end": v(-107.86, -95) * mm});
            skCircle(sketch, "E9.0.1.5", {"center": v(-104.7, -86.36) * mm, "radius": 2.73 * mm, "construction": true});
            skLineSegment(sketch, "E9.2.1.5", {"start": v(-107.86, -86.36) * mm, "end": v(-106.28, -83.63) * mm});
            skLineSegment(sketch, "E9.5.1.5", {"start": v(-106.28, -83.63) * mm, "end": v(-103.13, -83.63) * mm});
            skLineSegment(sketch, "E9.8.1.5", {"start": v(-103.13, -83.63) * mm, "end": v(-101.55, -86.36) * mm});
            skLineSegment(sketch, "E9.11.1.5", {"start": v(-101.55, -86.36) * mm, "end": v(-103.13, -89.1) * mm});
            skLineSegment(sketch, "E9.14.1.5", {"start": v(-103.13, -89.1) * mm, "end": v(-106.28, -89.1) * mm});
            skLineSegment(sketch, "E9.17.1.5", {"start": v(-106.28, -89.1) * mm, "end": v(-107.86, -86.36) * mm});
            skCircle(sketch, "E9.0.1.6", {"center": v(-104.7, -77.72) * mm, "radius": 2.73 * mm, "construction": true});
            skLineSegment(sketch, "E9.2.1.6", {"start": v(-107.86, -77.72) * mm, "end": v(-106.28, -75) * mm});
            skLineSegment(sketch, "E9.5.1.6", {"start": v(-106.28, -75) * mm, "end": v(-103.13, -75) * mm});
            skLineSegment(sketch, "E9.8.1.6", {"start": v(-103.13, -75) * mm, "end": v(-101.55, -77.72) * mm});
            skLineSegment(sketch, "E9.11.1.6", {"start": v(-101.55, -77.72) * mm, "end": v(-103.13, -80.45) * mm});
            skLineSegment(sketch, "E9.14.1.6", {"start": v(-103.13, -80.45) * mm, "end": v(-106.28, -80.45) * mm});
            skLineSegment(sketch, "E9.17.1.6", {"start": v(-106.28, -80.45) * mm, "end": v(-107.86, -77.72) * mm});
            skCircle(sketch, "E9.0.2.4", {"center": v(-89.75, -95) * mm, "radius": 2.73 * mm, "construction": true});
            skLineSegment(sketch, "E9.2.2.4", {"start": v(-92.9, -95) * mm, "end": v(-91.32, -92.27) * mm});
            skLineSegment(sketch, "E9.5.2.4", {"start": v(-91.32, -92.27) * mm, "end": v(-88.17, -92.27) * mm});
            skLineSegment(sketch, "E9.8.2.4", {"start": v(-88.17, -92.27) * mm, "end": v(-86.6, -95) * mm});
            skLineSegment(sketch, "E9.11.2.4", {"start": v(-86.6, -95) * mm, "end": v(-88.17, -97.73) * mm});
            skLineSegment(sketch, "E9.14.2.4", {"start": v(-88.17, -97.73) * mm, "end": v(-91.32, -97.73) * mm});
            skLineSegment(sketch, "E9.17.2.4", {"start": v(-91.32, -97.73) * mm, "end": v(-92.9, -95) * mm});
            skCircle(sketch, "E9.0.2.5", {"center": v(-89.75, -86.36) * mm, "radius": 2.73 * mm, "construction": true});
            skLineSegment(sketch, "E9.2.2.5", {"start": v(-92.9, -86.36) * mm, "end": v(-91.32, -83.63) * mm});
            skLineSegment(sketch, "E9.5.2.5", {"start": v(-91.32, -83.63) * mm, "end": v(-88.17, -83.63) * mm});
            skLineSegment(sketch, "E9.8.2.5", {"start": v(-88.17, -83.63) * mm, "end": v(-86.6, -86.36) * mm});
            skLineSegment(sketch, "E9.11.2.5", {"start": v(-86.6, -86.36) * mm, "end": v(-88.17, -89.1) * mm});
            skLineSegment(sketch, "E9.14.2.5", {"start": v(-88.17, -89.1) * mm, "end": v(-91.32, -89.1) * mm});
            skLineSegment(sketch, "E9.17.2.5", {"start": v(-91.32, -89.1) * mm, "end": v(-92.9, -86.36) * mm});
            skCircle(sketch, "E9.0.2.6", {"center": v(-89.75, -77.72) * mm, "radius": 2.73 * mm, "construction": true});
            skLineSegment(sketch, "E9.2.2.6", {"start": v(-92.9, -77.72) * mm, "end": v(-91.32, -75) * mm});
            skLineSegment(sketch, "E9.5.2.6", {"start": v(-91.32, -75) * mm, "end": v(-88.17, -75) * mm});
            skLineSegment(sketch, "E9.8.2.6", {"start": v(-88.17, -75) * mm, "end": v(-86.6, -77.72) * mm});
            skLineSegment(sketch, "E9.11.2.6", {"start": v(-86.6, -77.72) * mm, "end": v(-88.17, -80.45) * mm});
            skLineSegment(sketch, "E9.14.2.6", {"start": v(-88.17, -80.45) * mm, "end": v(-91.32, -80.45) * mm});
            skLineSegment(sketch, "E9.17.2.6", {"start": v(-91.32, -80.45) * mm, "end": v(-92.9, -77.72) * mm});
            skCircle(sketch, "E10.0.0.7", {"center": v(-119.66, -69.09) * mm, "radius": 2.73 * mm, "construction": true});
            skLineSegment(sketch, "E10.2.0.7", {"start": v(-122.82, -69.09) * mm, "end": v(-121.24, -66.36) * mm});
            skLineSegment(sketch, "E10.5.0.7", {"start": v(-121.24, -66.36) * mm, "end": v(-118.09, -66.36) * mm});
            skLineSegment(sketch, "E10.8.0.7", {"start": v(-118.09, -66.36) * mm, "end": v(-116.51, -69.09) * mm});
            skLineSegment(sketch, "E10.11.0.7", {"start": v(-116.51, -69.09) * mm, "end": v(-118.09, -71.82) * mm});
            skLineSegment(sketch, "E10.14.0.7", {"start": v(-118.09, -71.82) * mm, "end": v(-121.24, -71.82) * mm});
            skLineSegment(sketch, "E10.17.0.7", {"start": v(-121.24, -71.82) * mm, "end": v(-122.82, -69.09) * mm});
            skCircle(sketch, "E10.0.1.7", {"center": v(-104.7, -69.09) * mm, "radius": 2.73 * mm, "construction": true});
            skLineSegment(sketch, "E10.2.1.7", {"start": v(-107.86, -69.09) * mm, "end": v(-106.28, -66.36) * mm});
            skLineSegment(sketch, "E10.5.1.7", {"start": v(-106.28, -66.36) * mm, "end": v(-103.13, -66.36) * mm});
            skLineSegment(sketch, "E10.8.1.7", {"start": v(-103.13, -66.36) * mm, "end": v(-101.55, -69.09) * mm});
            skLineSegment(sketch, "E10.11.1.7", {"start": v(-101.55, -69.09) * mm, "end": v(-103.13, -71.82) * mm});
            skLineSegment(sketch, "E10.14.1.7", {"start": v(-103.13, -71.82) * mm, "end": v(-106.28, -71.82) * mm});
            skLineSegment(sketch, "E10.17.1.7", {"start": v(-106.28, -71.82) * mm, "end": v(-107.86, -69.09) * mm});
            skCircle(sketch, "E10.0.2.7", {"center": v(-89.75, -69.09) * mm, "radius": 2.73 * mm, "construction": true});
            skLineSegment(sketch, "E10.2.2.7", {"start": v(-92.9, -69.09) * mm, "end": v(-91.32, -66.36) * mm});
            skLineSegment(sketch, "E10.5.2.7", {"start": v(-91.32, -66.36) * mm, "end": v(-88.17, -66.36) * mm});
            skLineSegment(sketch, "E10.8.2.7", {"start": v(-88.17, -66.36) * mm, "end": v(-86.6, -69.09) * mm});
            skLineSegment(sketch, "E10.11.2.7", {"start": v(-86.6, -69.09) * mm, "end": v(-88.17, -71.82) * mm});
            skLineSegment(sketch, "E10.14.2.7", {"start": v(-88.17, -71.82) * mm, "end": v(-91.32, -71.82) * mm});
            skLineSegment(sketch, "E10.17.2.7", {"start": v(-91.32, -71.82) * mm, "end": v(-92.9, -69.09) * mm});
            skLineSegment(sketch, "E11.0.0.8", {"start": v(-128.72, -62.04) * mm, "end": v(-125.57, -62.04) * mm});
            skLineSegment(sketch, "E11.3.0.8", {"start": v(-125.57, -62.04) * mm, "end": v(-124, -64.77) * mm});
            skLineSegment(sketch, "E11.6.0.8", {"start": v(-124, -64.77) * mm, "end": v(-125.57, -67.5) * mm});
            skCircle(sketch, "E11.9.0.8", {"center": v(-127.14, -64.77) * mm, "radius": 2.73 * mm, "construction": true});
            skLineSegment(sketch, "E11.11.0.8", {"start": v(-125.57, -67.5) * mm, "end": v(-128.72, -67.5) * mm});
            skLineSegment(sketch, "E11.14.0.8", {"start": v(-128.72, -67.5) * mm, "end": v(-130.3, -64.77) * mm});
            skLineSegment(sketch, "E11.17.0.8", {"start": v(-130.3, -64.77) * mm, "end": v(-128.72, -62.04) * mm});
            skLineSegment(sketch, "E11.0.1.8", {"start": v(-113.76, -62.04) * mm, "end": v(-110.6, -62.04) * mm});
            skLineSegment(sketch, "E11.3.1.8", {"start": v(-110.6, -62.04) * mm, "end": v(-109.03, -64.77) * mm});
            skLineSegment(sketch, "E11.6.1.8", {"start": v(-109.03, -64.77) * mm, "end": v(-110.6, -67.5) * mm});
            skCircle(sketch, "E11.9.1.8", {"center": v(-112.19, -64.77) * mm, "radius": 2.73 * mm, "construction": true});
            skLineSegment(sketch, "E11.11.1.8", {"start": v(-110.6, -67.5) * mm, "end": v(-113.76, -67.5) * mm});
            skLineSegment(sketch, "E11.14.1.8", {"start": v(-113.76, -67.5) * mm, "end": v(-115.34, -64.77) * mm});
            skLineSegment(sketch, "E11.17.1.8", {"start": v(-115.34, -64.77) * mm, "end": v(-113.76, -62.04) * mm});
            skLineSegment(sketch, "E11.0.2.8", {"start": v(-98.8, -62.04) * mm, "end": v(-95.65, -62.04) * mm});
            skLineSegment(sketch, "E11.3.2.8", {"start": v(-95.65, -62.04) * mm, "end": v(-94.07, -64.77) * mm});
            skLineSegment(sketch, "E11.6.2.8", {"start": v(-94.07, -64.77) * mm, "end": v(-95.65, -67.5) * mm});
            skCircle(sketch, "E11.9.2.8", {"center": v(-97.23, -64.77) * mm, "radius": 2.73 * mm, "construction": true});
            skLineSegment(sketch, "E11.11.2.8", {"start": v(-95.65, -67.5) * mm, "end": v(-98.8, -67.5) * mm});
            skLineSegment(sketch, "E11.14.2.8", {"start": v(-98.8, -67.5) * mm, "end": v(-100.38, -64.77) * mm});
            skLineSegment(sketch, "E11.17.2.8", {"start": v(-100.38, -64.77) * mm, "end": v(-98.8, -62.04) * mm});
            skLineSegment(sketch, "E11.0.3.8", {"start": v(-83.85, -62.04) * mm, "end": v(-80.7, -62.04) * mm});
            skLineSegment(sketch, "E11.3.3.8", {"start": v(-80.7, -62.04) * mm, "end": v(-79.12, -64.77) * mm});
            skLineSegment(sketch, "E11.6.3.8", {"start": v(-79.12, -64.77) * mm, "end": v(-80.7, -67.5) * mm});
            skCircle(sketch, "E11.9.3.8", {"center": v(-82.27, -64.77) * mm, "radius": 2.73 * mm, "construction": true});
            skLineSegment(sketch, "E11.11.3.8", {"start": v(-80.7, -67.5) * mm, "end": v(-83.85, -67.5) * mm});
            skLineSegment(sketch, "E11.14.3.8", {"start": v(-83.85, -67.5) * mm, "end": v(-85.42, -64.77) * mm});
            skLineSegment(sketch, "E11.17.3.8", {"start": v(-85.42, -64.77) * mm, "end": v(-83.85, -62.04) * mm});
            skLineSegment(sketch, "E11.0.4.8", {"start": v(-68.89, -62.04) * mm, "end": v(-65.73, -62.04) * mm});
            skLineSegment(sketch, "E11.3.4.8", {"start": v(-65.73, -62.04) * mm, "end": v(-64.16, -64.77) * mm});
            skLineSegment(sketch, "E11.6.4.8", {"start": v(-64.16, -64.77) * mm, "end": v(-65.73, -67.5) * mm});
            skCircle(sketch, "E11.9.4.8", {"center": v(-67.31, -64.77) * mm, "radius": 2.73 * mm, "construction": true});
            skLineSegment(sketch, "E11.11.4.8", {"start": v(-65.73, -67.5) * mm, "end": v(-68.89, -67.5) * mm});
            skLineSegment(sketch, "E11.14.4.8", {"start": v(-68.89, -67.5) * mm, "end": v(-70.46, -64.77) * mm});
            skLineSegment(sketch, "E11.17.4.8", {"start": v(-70.46, -64.77) * mm, "end": v(-68.89, -62.04) * mm});
            skLineSegment(sketch, "E11.0.5.8", {"start": v(-53.93, -62.04) * mm, "end": v(-50.78, -62.04) * mm});
            skLineSegment(sketch, "E11.3.5.8", {"start": v(-50.78, -62.04) * mm, "end": v(-49.2, -64.77) * mm});
            skLineSegment(sketch, "E11.6.5.8", {"start": v(-49.2, -64.77) * mm, "end": v(-50.78, -67.5) * mm});
            skCircle(sketch, "E11.9.5.8", {"center": v(-52.35, -64.77) * mm, "radius": 2.73 * mm, "construction": true});
            skLineSegment(sketch, "E11.11.5.8", {"start": v(-50.78, -67.5) * mm, "end": v(-53.93, -67.5) * mm});
            skLineSegment(sketch, "E11.14.5.8", {"start": v(-53.93, -67.5) * mm, "end": v(-55.5, -64.77) * mm});
            skLineSegment(sketch, "E11.17.5.8", {"start": v(-55.5, -64.77) * mm, "end": v(-53.93, -62.04) * mm});
            skLineSegment(sketch, "E12.0.0.9", {"start": v(-128.72, -53.4) * mm, "end": v(-125.57, -53.4) * mm});
            skLineSegment(sketch, "E12.3.0.9", {"start": v(-125.57, -53.4) * mm, "end": v(-124, -56.13) * mm});
            skLineSegment(sketch, "E12.6.0.9", {"start": v(-124, -56.13) * mm, "end": v(-125.57, -58.86) * mm});
            skCircle(sketch, "E12.9.0.9", {"center": v(-127.14, -56.13) * mm, "radius": 2.73 * mm, "construction": true});
            skLineSegment(sketch, "E12.11.0.9", {"start": v(-125.57, -58.86) * mm, "end": v(-128.72, -58.86) * mm});
            skLineSegment(sketch, "E12.14.0.9", {"start": v(-128.72, -58.86) * mm, "end": v(-130.3, -56.13) * mm});
            skLineSegment(sketch, "E12.17.0.9", {"start": v(-130.3, -56.13) * mm, "end": v(-128.72, -53.4) * mm});
            skLineSegment(sketch, "E12.0.0.10", {"start": v(-128.72, -44.77) * mm, "end": v(-125.57, -44.77) * mm});
            skLineSegment(sketch, "E12.3.0.10", {"start": v(-125.57, -44.77) * mm, "end": v(-124, -47.5) * mm});
            skLineSegment(sketch, "E12.6.0.10", {"start": v(-124, -47.5) * mm, "end": v(-125.57, -50.23) * mm});
            skCircle(sketch, "E12.9.0.10", {"center": v(-127.14, -47.5) * mm, "radius": 2.73 * mm, "construction": true});
            skLineSegment(sketch, "E12.11.0.10", {"start": v(-125.57, -50.23) * mm, "end": v(-128.72, -50.23) * mm});
            skLineSegment(sketch, "E12.14.0.10", {"start": v(-128.72, -50.23) * mm, "end": v(-130.3, -47.5) * mm});
            skLineSegment(sketch, "E12.17.0.10", {"start": v(-130.3, -47.5) * mm, "end": v(-128.72, -44.77) * mm});
            skLineSegment(sketch, "E12.0.0.11", {"start": v(-128.72, -36.13) * mm, "end": v(-125.57, -36.13) * mm});
            skLineSegment(sketch, "E12.3.0.11", {"start": v(-125.57, -36.13) * mm, "end": v(-124, -38.86) * mm});
            skLineSegment(sketch, "E12.6.0.11", {"start": v(-124, -38.86) * mm, "end": v(-125.57, -41.6) * mm});
            skCircle(sketch, "E12.9.0.11", {"center": v(-127.14, -38.86) * mm, "radius": 2.73 * mm, "construction": true});
            skLineSegment(sketch, "E12.11.0.11", {"start": v(-125.57, -41.6) * mm, "end": v(-128.72, -41.6) * mm});
            skLineSegment(sketch, "E12.14.0.11", {"start": v(-128.72, -41.6) * mm, "end": v(-130.3, -38.86) * mm});
            skLineSegment(sketch, "E12.17.0.11", {"start": v(-130.3, -38.86) * mm, "end": v(-128.72, -36.13) * mm});
            skLineSegment(sketch, "E12.0.0.12", {"start": v(-128.72, -27.5) * mm, "end": v(-125.57, -27.5) * mm});
            skLineSegment(sketch, "E12.3.0.12", {"start": v(-125.57, -27.5) * mm, "end": v(-124, -30.23) * mm});
            skLineSegment(sketch, "E12.6.0.12", {"start": v(-124, -30.23) * mm, "end": v(-125.57, -32.96) * mm});
            skCircle(sketch, "E12.9.0.12", {"center": v(-127.14, -30.23) * mm, "radius": 2.73 * mm, "construction": true});
            skLineSegment(sketch, "E12.11.0.12", {"start": v(-125.57, -32.96) * mm, "end": v(-128.72, -32.96) * mm});
            skLineSegment(sketch, "E12.14.0.12", {"start": v(-128.72, -32.96) * mm, "end": v(-130.3, -30.23) * mm});
            skLineSegment(sketch, "E12.17.0.12", {"start": v(-130.3, -30.23) * mm, "end": v(-128.72, -27.5) * mm});
            skLineSegment(sketch, "E12.0.0.13", {"start": v(-128.72, -18.86) * mm, "end": v(-125.57, -18.86) * mm});
            skLineSegment(sketch, "E12.3.0.13", {"start": v(-125.57, -18.86) * mm, "end": v(-124, -21.6) * mm});
            skLineSegment(sketch, "E12.6.0.13", {"start": v(-124, -21.6) * mm, "end": v(-125.57, -24.32) * mm});
            skCircle(sketch, "E12.9.0.13", {"center": v(-127.14, -21.6) * mm, "radius": 2.73 * mm, "construction": true});
            skLineSegment(sketch, "E12.11.0.13", {"start": v(-125.57, -24.32) * mm, "end": v(-128.72, -24.32) * mm});
            skLineSegment(sketch, "E12.14.0.13", {"start": v(-128.72, -24.32) * mm, "end": v(-130.3, -21.6) * mm});
            skLineSegment(sketch, "E12.17.0.13", {"start": v(-130.3, -21.59) * mm, "end": v(-128.72, -18.86) * mm});
            skLineSegment(sketch, "E12.0.0.14", {"start": v(-128.72, -10.22) * mm, "end": v(-125.57, -10.22) * mm});
            skLineSegment(sketch, "E12.3.0.14", {"start": v(-125.57, -10.22) * mm, "end": v(-124, -12.95) * mm});
            skLineSegment(sketch, "E12.6.0.14", {"start": v(-124, -12.95) * mm, "end": v(-125.57, -15.68) * mm});
            skCircle(sketch, "E12.9.0.14", {"center": v(-127.14, -12.95) * mm, "radius": 2.73 * mm, "construction": true});
            skLineSegment(sketch, "E12.11.0.14", {"start": v(-125.57, -15.68) * mm, "end": v(-128.72, -15.68) * mm});
            skLineSegment(sketch, "E12.14.0.14", {"start": v(-128.72, -15.68) * mm, "end": v(-130.3, -12.95) * mm});
            skLineSegment(sketch, "E12.17.0.14", {"start": v(-130.3, -12.95) * mm, "end": v(-128.72, -10.22) * mm});
            skLineSegment(sketch, "E12.0.0.15", {"start": v(-128.72, -1.59) * mm, "end": v(-125.57, -1.59) * mm});
            skLineSegment(sketch, "E12.3.0.15", {"start": v(-125.57, -1.59) * mm, "end": v(-124, -4.32) * mm});
            skLineSegment(sketch, "E12.6.0.15", {"start": v(-124, -4.32) * mm, "end": v(-125.57, -7.05) * mm});
            skCircle(sketch, "E12.9.0.15", {"center": v(-127.14, -4.32) * mm, "radius": 2.73 * mm, "construction": true});
            skLineSegment(sketch, "E12.11.0.15", {"start": v(-125.57, -7.05) * mm, "end": v(-128.72, -7.05) * mm});
            skLineSegment(sketch, "E12.14.0.15", {"start": v(-128.72, -7.05) * mm, "end": v(-130.3, -4.32) * mm});
            skLineSegment(sketch, "E12.17.0.15", {"start": v(-130.3, -4.32) * mm, "end": v(-128.72, -1.59) * mm});
            skLineSegment(sketch, "E12.0.0.16", {"start": v(-128.72, 7.05) * mm, "end": v(-125.57, 7.05) * mm});
            skLineSegment(sketch, "E12.3.0.16", {"start": v(-125.57, 7.05) * mm, "end": v(-124, 4.32) * mm});
            skLineSegment(sketch, "E12.6.0.16", {"start": v(-124, 4.32) * mm, "end": v(-125.57, 1.59) * mm});
            skCircle(sketch, "E12.9.0.16", {"center": v(-127.14, 4.32) * mm, "radius": 2.73 * mm, "construction": true});
            skLineSegment(sketch, "E12.11.0.16", {"start": v(-125.57, 1.59) * mm, "end": v(-128.72, 1.59) * mm});
            skLineSegment(sketch, "E12.14.0.16", {"start": v(-128.72, 1.59) * mm, "end": v(-130.3, 4.32) * mm});
            skLineSegment(sketch, "E12.17.0.16", {"start": v(-130.3, 4.32) * mm, "end": v(-128.72, 7.05) * mm});
            skLineSegment(sketch, "E12.0.0.17", {"start": v(-128.72, 15.68) * mm, "end": v(-125.57, 15.68) * mm});
            skLineSegment(sketch, "E12.3.0.17", {"start": v(-125.57, 15.68) * mm, "end": v(-124, 12.95) * mm});
            skLineSegment(sketch, "E12.6.0.17", {"start": v(-124, 12.95) * mm, "end": v(-125.57, 10.22) * mm});
            skCircle(sketch, "E12.9.0.17", {"center": v(-127.14, 12.95) * mm, "radius": 2.73 * mm, "construction": true});
            skLineSegment(sketch, "E12.11.0.17", {"start": v(-125.57, 10.22) * mm, "end": v(-128.72, 10.22) * mm});
            skLineSegment(sketch, "E12.14.0.17", {"start": v(-128.72, 10.22) * mm, "end": v(-130.3, 12.95) * mm});
            skLineSegment(sketch, "E12.17.0.17", {"start": v(-130.3, 12.95) * mm, "end": v(-128.72, 15.68) * mm});
            skLineSegment(sketch, "E12.0.0.18", {"start": v(-128.72, 24.32) * mm, "end": v(-125.57, 24.32) * mm});
            skLineSegment(sketch, "E12.3.0.18", {"start": v(-125.57, 24.32) * mm, "end": v(-124, 21.59) * mm});
            skLineSegment(sketch, "E12.6.0.18", {"start": v(-124, 21.59) * mm, "end": v(-125.57, 18.86) * mm});
            skCircle(sketch, "E12.9.0.18", {"center": v(-127.14, 21.59) * mm, "radius": 2.73 * mm, "construction": true});
            skLineSegment(sketch, "E12.11.0.18", {"start": v(-125.57, 18.86) * mm, "end": v(-128.72, 18.86) * mm});
            skLineSegment(sketch, "E12.14.0.18", {"start": v(-128.72, 18.86) * mm, "end": v(-130.3, 21.59) * mm});
            skLineSegment(sketch, "E12.17.0.18", {"start": v(-130.3, 21.6) * mm, "end": v(-128.72, 24.32) * mm});
            skLineSegment(sketch, "E12.0.0.19", {"start": v(-128.72, 32.96) * mm, "end": v(-125.57, 32.96) * mm});
            skLineSegment(sketch, "E12.3.0.19", {"start": v(-125.57, 32.96) * mm, "end": v(-124, 30.23) * mm});
            skLineSegment(sketch, "E12.6.0.19", {"start": v(-124, 30.23) * mm, "end": v(-125.57, 27.5) * mm});
            skCircle(sketch, "E12.9.0.19", {"center": v(-127.14, 30.23) * mm, "radius": 2.73 * mm, "construction": true});
            skLineSegment(sketch, "E12.11.0.19", {"start": v(-125.57, 27.5) * mm, "end": v(-128.72, 27.5) * mm});
            skLineSegment(sketch, "E12.14.0.19", {"start": v(-128.72, 27.5) * mm, "end": v(-130.3, 30.23) * mm});
            skLineSegment(sketch, "E12.17.0.19", {"start": v(-130.3, 30.23) * mm, "end": v(-128.72, 32.96) * mm});
            skLineSegment(sketch, "E12.0.1.9", {"start": v(-113.76, -53.4) * mm, "end": v(-110.6, -53.4) * mm});
            skLineSegment(sketch, "E12.3.1.9", {"start": v(-110.6, -53.4) * mm, "end": v(-109.03, -56.13) * mm});
            skLineSegment(sketch, "E12.6.1.9", {"start": v(-109.03, -56.13) * mm, "end": v(-110.6, -58.86) * mm});
            skCircle(sketch, "E12.9.1.9", {"center": v(-112.19, -56.13) * mm, "radius": 2.73 * mm, "construction": true});
            skLineSegment(sketch, "E12.11.1.9", {"start": v(-110.6, -58.86) * mm, "end": v(-113.76, -58.86) * mm});
            skLineSegment(sketch, "E12.14.1.9", {"start": v(-113.76, -58.86) * mm, "end": v(-115.34, -56.13) * mm});
            skLineSegment(sketch, "E12.17.1.9", {"start": v(-115.34, -56.13) * mm, "end": v(-113.76, -53.4) * mm});
            skLineSegment(sketch, "E12.0.1.10", {"start": v(-113.76, -44.77) * mm, "end": v(-110.6, -44.77) * mm});
            skLineSegment(sketch, "E12.3.1.10", {"start": v(-110.6, -44.77) * mm, "end": v(-109.03, -47.5) * mm});
            skLineSegment(sketch, "E12.6.1.10", {"start": v(-109.03, -47.5) * mm, "end": v(-110.6, -50.23) * mm});
            skCircle(sketch, "E12.9.1.10", {"center": v(-112.19, -47.5) * mm, "radius": 2.73 * mm, "construction": true});
            skLineSegment(sketch, "E12.11.1.10", {"start": v(-110.6, -50.23) * mm, "end": v(-113.76, -50.23) * mm});
            skLineSegment(sketch, "E12.14.1.10", {"start": v(-113.76, -50.23) * mm, "end": v(-115.34, -47.5) * mm});
            skLineSegment(sketch, "E12.17.1.10", {"start": v(-115.34, -47.5) * mm, "end": v(-113.76, -44.77) * mm});
            skLineSegment(sketch, "E12.0.1.11", {"start": v(-113.76, -36.13) * mm, "end": v(-110.6, -36.13) * mm});
            skLineSegment(sketch, "E12.3.1.11", {"start": v(-110.6, -36.13) * mm, "end": v(-109.03, -38.86) * mm});
            skLineSegment(sketch, "E12.6.1.11", {"start": v(-109.03, -38.86) * mm, "end": v(-110.6, -41.6) * mm});
            skCircle(sketch, "E12.9.1.11", {"center": v(-112.19, -38.86) * mm, "radius": 2.73 * mm, "construction": true});
            skLineSegment(sketch, "E12.11.1.11", {"start": v(-110.6, -41.6) * mm, "end": v(-113.76, -41.6) * mm});
            skLineSegment(sketch, "E12.14.1.11", {"start": v(-113.76, -41.6) * mm, "end": v(-115.34, -38.86) * mm});
            skLineSegment(sketch, "E12.17.1.11", {"start": v(-115.34, -38.86) * mm, "end": v(-113.76, -36.13) * mm});
            skLineSegment(sketch, "E12.0.1.12", {"start": v(-113.76, -27.5) * mm, "end": v(-110.6, -27.5) * mm});
            skLineSegment(sketch, "E12.3.1.12", {"start": v(-110.6, -27.5) * mm, "end": v(-109.03, -30.23) * mm});
            skLineSegment(sketch, "E12.6.1.12", {"start": v(-109.03, -30.23) * mm, "end": v(-110.6, -32.96) * mm});
            skCircle(sketch, "E12.9.1.12", {"center": v(-112.19, -30.23) * mm, "radius": 2.73 * mm, "construction": true});
            skLineSegment(sketch, "E12.11.1.12", {"start": v(-110.6, -32.96) * mm, "end": v(-113.76, -32.96) * mm});
            skLineSegment(sketch, "E12.14.1.12", {"start": v(-113.76, -32.96) * mm, "end": v(-115.34, -30.23) * mm});
            skLineSegment(sketch, "E12.17.1.12", {"start": v(-115.34, -30.23) * mm, "end": v(-113.76, -27.5) * mm});
            skLineSegment(sketch, "E12.0.1.13", {"start": v(-113.76, -18.86) * mm, "end": v(-110.6, -18.86) * mm});
            skLineSegment(sketch, "E12.3.1.13", {"start": v(-110.6, -18.86) * mm, "end": v(-109.03, -21.6) * mm});
            skLineSegment(sketch, "E12.6.1.13", {"start": v(-109.03, -21.6) * mm, "end": v(-110.6, -24.32) * mm});
            skCircle(sketch, "E12.9.1.13", {"center": v(-112.19, -21.6) * mm, "radius": 2.73 * mm, "construction": true});
            skLineSegment(sketch, "E12.11.1.13", {"start": v(-110.6, -24.32) * mm, "end": v(-113.76, -24.32) * mm});
            skLineSegment(sketch, "E12.14.1.13", {"start": v(-113.76, -24.32) * mm, "end": v(-115.34, -21.6) * mm});
            skLineSegment(sketch, "E12.17.1.13", {"start": v(-115.34, -21.59) * mm, "end": v(-113.76, -18.86) * mm});
            skLineSegment(sketch, "E12.0.1.14", {"start": v(-113.76, -10.22) * mm, "end": v(-110.6, -10.22) * mm});
            skLineSegment(sketch, "E12.3.1.14", {"start": v(-110.6, -10.22) * mm, "end": v(-109.03, -12.95) * mm});
            skLineSegment(sketch, "E12.6.1.14", {"start": v(-109.03, -12.95) * mm, "end": v(-110.6, -15.68) * mm});
            skCircle(sketch, "E12.9.1.14", {"center": v(-112.19, -12.95) * mm, "radius": 2.73 * mm, "construction": true});
            skLineSegment(sketch, "E12.11.1.14", {"start": v(-110.6, -15.68) * mm, "end": v(-113.76, -15.68) * mm});
            skLineSegment(sketch, "E12.14.1.14", {"start": v(-113.76, -15.68) * mm, "end": v(-115.34, -12.95) * mm});
            skLineSegment(sketch, "E12.17.1.14", {"start": v(-115.34, -12.95) * mm, "end": v(-113.76, -10.22) * mm});
            skLineSegment(sketch, "E12.0.1.15", {"start": v(-113.76, -1.59) * mm, "end": v(-110.6, -1.59) * mm});
            skLineSegment(sketch, "E12.3.1.15", {"start": v(-110.6, -1.59) * mm, "end": v(-109.03, -4.32) * mm});
            skLineSegment(sketch, "E12.6.1.15", {"start": v(-109.03, -4.32) * mm, "end": v(-110.6, -7.05) * mm});
            skCircle(sketch, "E12.9.1.15", {"center": v(-112.19, -4.32) * mm, "radius": 2.73 * mm, "construction": true});
            skLineSegment(sketch, "E12.11.1.15", {"start": v(-110.6, -7.05) * mm, "end": v(-113.76, -7.05) * mm});
            skLineSegment(sketch, "E12.14.1.15", {"start": v(-113.76, -7.05) * mm, "end": v(-115.34, -4.32) * mm});
            skLineSegment(sketch, "E12.17.1.15", {"start": v(-115.34, -4.32) * mm, "end": v(-113.76, -1.59) * mm});
            skLineSegment(sketch, "E12.0.1.16", {"start": v(-113.76, 7.05) * mm, "end": v(-110.6, 7.05) * mm});
            skLineSegment(sketch, "E12.3.1.16", {"start": v(-110.6, 7.05) * mm, "end": v(-109.03, 4.32) * mm});
            skLineSegment(sketch, "E12.6.1.16", {"start": v(-109.03, 4.32) * mm, "end": v(-110.6, 1.59) * mm});
            skCircle(sketch, "E12.9.1.16", {"center": v(-112.19, 4.32) * mm, "radius": 2.73 * mm, "construction": true});
            skLineSegment(sketch, "E12.11.1.16", {"start": v(-110.6, 1.59) * mm, "end": v(-113.76, 1.59) * mm});
            skLineSegment(sketch, "E12.14.1.16", {"start": v(-113.76, 1.59) * mm, "end": v(-115.34, 4.32) * mm});
            skLineSegment(sketch, "E12.17.1.16", {"start": v(-115.34, 4.32) * mm, "end": v(-113.76, 7.05) * mm});
            skLineSegment(sketch, "E12.0.1.17", {"start": v(-113.76, 15.68) * mm, "end": v(-110.6, 15.68) * mm});
            skLineSegment(sketch, "E12.3.1.17", {"start": v(-110.6, 15.68) * mm, "end": v(-109.03, 12.95) * mm});
            skLineSegment(sketch, "E12.6.1.17", {"start": v(-109.03, 12.95) * mm, "end": v(-110.6, 10.22) * mm});
            skCircle(sketch, "E12.9.1.17", {"center": v(-112.19, 12.95) * mm, "radius": 2.73 * mm, "construction": true});
            skLineSegment(sketch, "E12.11.1.17", {"start": v(-110.6, 10.22) * mm, "end": v(-113.76, 10.22) * mm});
            skLineSegment(sketch, "E12.14.1.17", {"start": v(-113.76, 10.22) * mm, "end": v(-115.34, 12.95) * mm});
            skLineSegment(sketch, "E12.17.1.17", {"start": v(-115.34, 12.95) * mm, "end": v(-113.76, 15.68) * mm});
            skLineSegment(sketch, "E12.0.1.18", {"start": v(-113.76, 24.32) * mm, "end": v(-110.6, 24.32) * mm});
            skLineSegment(sketch, "E12.3.1.18", {"start": v(-110.6, 24.32) * mm, "end": v(-109.03, 21.59) * mm});
            skLineSegment(sketch, "E12.6.1.18", {"start": v(-109.03, 21.59) * mm, "end": v(-110.6, 18.86) * mm});
            skCircle(sketch, "E12.9.1.18", {"center": v(-112.19, 21.59) * mm, "radius": 2.73 * mm, "construction": true});
            skLineSegment(sketch, "E12.11.1.18", {"start": v(-110.6, 18.86) * mm, "end": v(-113.76, 18.86) * mm});
            skLineSegment(sketch, "E12.14.1.18", {"start": v(-113.76, 18.86) * mm, "end": v(-115.34, 21.59) * mm});
            skLineSegment(sketch, "E12.17.1.18", {"start": v(-115.34, 21.59) * mm, "end": v(-113.76, 24.32) * mm});
            skLineSegment(sketch, "E12.0.1.19", {"start": v(-113.76, 32.96) * mm, "end": v(-110.6, 32.96) * mm});
            skLineSegment(sketch, "E12.3.1.19", {"start": v(-110.6, 32.96) * mm, "end": v(-109.03, 30.23) * mm});
            skLineSegment(sketch, "E12.6.1.19", {"start": v(-109.03, 30.23) * mm, "end": v(-110.6, 27.5) * mm});
            skCircle(sketch, "E12.9.1.19", {"center": v(-112.19, 30.23) * mm, "radius": 2.73 * mm, "construction": true});
            skLineSegment(sketch, "E12.11.1.19", {"start": v(-110.6, 27.5) * mm, "end": v(-113.76, 27.5) * mm});
            skLineSegment(sketch, "E12.14.1.19", {"start": v(-113.76, 27.5) * mm, "end": v(-115.34, 30.23) * mm});
            skLineSegment(sketch, "E12.17.1.19", {"start": v(-115.34, 30.23) * mm, "end": v(-113.76, 32.96) * mm});
            skLineSegment(sketch, "E12.0.2.9", {"start": v(-98.8, -53.4) * mm, "end": v(-95.65, -53.4) * mm});
            skLineSegment(sketch, "E12.3.2.9", {"start": v(-95.65, -53.4) * mm, "end": v(-94.07, -56.13) * mm});
            skLineSegment(sketch, "E12.6.2.9", {"start": v(-94.07, -56.13) * mm, "end": v(-95.65, -58.86) * mm});
            skCircle(sketch, "E12.9.2.9", {"center": v(-97.23, -56.13) * mm, "radius": 2.73 * mm, "construction": true});
            skLineSegment(sketch, "E12.11.2.9", {"start": v(-95.65, -58.86) * mm, "end": v(-98.8, -58.86) * mm});
            skLineSegment(sketch, "E12.14.2.9", {"start": v(-98.8, -58.86) * mm, "end": v(-100.38, -56.13) * mm});
            skLineSegment(sketch, "E12.17.2.9", {"start": v(-100.38, -56.13) * mm, "end": v(-98.8, -53.4) * mm});
            skLineSegment(sketch, "E12.0.2.10", {"start": v(-98.8, -44.77) * mm, "end": v(-95.65, -44.77) * mm});
            skLineSegment(sketch, "E12.3.2.10", {"start": v(-95.65, -44.77) * mm, "end": v(-94.07, -47.5) * mm});
            skLineSegment(sketch, "E12.6.2.10", {"start": v(-94.07, -47.5) * mm, "end": v(-95.65, -50.23) * mm});
            skCircle(sketch, "E12.9.2.10", {"center": v(-97.23, -47.5) * mm, "radius": 2.73 * mm, "construction": true});
            skLineSegment(sketch, "E12.11.2.10", {"start": v(-95.65, -50.23) * mm, "end": v(-98.8, -50.23) * mm});
            skLineSegment(sketch, "E12.14.2.10", {"start": v(-98.8, -50.23) * mm, "end": v(-100.38, -47.5) * mm});
            skLineSegment(sketch, "E12.17.2.10", {"start": v(-100.38, -47.5) * mm, "end": v(-98.8, -44.77) * mm});
            skLineSegment(sketch, "E12.0.2.11", {"start": v(-98.8, -36.13) * mm, "end": v(-95.65, -36.13) * mm});
            skLineSegment(sketch, "E12.3.2.11", {"start": v(-95.65, -36.13) * mm, "end": v(-94.07, -38.86) * mm});
            skLineSegment(sketch, "E12.6.2.11", {"start": v(-94.07, -38.86) * mm, "end": v(-95.65, -41.6) * mm});
            skCircle(sketch, "E12.9.2.11", {"center": v(-97.23, -38.86) * mm, "radius": 2.73 * mm, "construction": true});
            skLineSegment(sketch, "E12.11.2.11", {"start": v(-95.65, -41.6) * mm, "end": v(-98.8, -41.6) * mm});
            skLineSegment(sketch, "E12.14.2.11", {"start": v(-98.8, -41.6) * mm, "end": v(-100.38, -38.86) * mm});
            skLineSegment(sketch, "E12.17.2.11", {"start": v(-100.38, -38.86) * mm, "end": v(-98.8, -36.13) * mm});
            skLineSegment(sketch, "E12.0.2.12", {"start": v(-98.8, -27.5) * mm, "end": v(-95.65, -27.5) * mm});
            skLineSegment(sketch, "E12.3.2.12", {"start": v(-95.65, -27.5) * mm, "end": v(-94.07, -30.23) * mm});
            skLineSegment(sketch, "E12.6.2.12", {"start": v(-94.07, -30.23) * mm, "end": v(-95.65, -32.96) * mm});
            skCircle(sketch, "E12.9.2.12", {"center": v(-97.23, -30.23) * mm, "radius": 2.73 * mm, "construction": true});
            skLineSegment(sketch, "E12.11.2.12", {"start": v(-95.65, -32.96) * mm, "end": v(-98.8, -32.96) * mm});
            skLineSegment(sketch, "E12.14.2.12", {"start": v(-98.8, -32.96) * mm, "end": v(-100.38, -30.23) * mm});
            skLineSegment(sketch, "E12.17.2.12", {"start": v(-100.38, -30.23) * mm, "end": v(-98.8, -27.5) * mm});
            skLineSegment(sketch, "E12.0.2.13", {"start": v(-98.8, -18.86) * mm, "end": v(-95.65, -18.86) * mm});
            skLineSegment(sketch, "E12.3.2.13", {"start": v(-95.65, -18.86) * mm, "end": v(-94.07, -21.6) * mm});
            skLineSegment(sketch, "E12.6.2.13", {"start": v(-94.07, -21.6) * mm, "end": v(-95.65, -24.32) * mm});
            skCircle(sketch, "E12.9.2.13", {"center": v(-97.23, -21.6) * mm, "radius": 2.73 * mm, "construction": true});
            skLineSegment(sketch, "E12.11.2.13", {"start": v(-95.65, -24.32) * mm, "end": v(-98.8, -24.32) * mm});
            skLineSegment(sketch, "E12.14.2.13", {"start": v(-98.8, -24.32) * mm, "end": v(-100.38, -21.6) * mm});
            skLineSegment(sketch, "E12.17.2.13", {"start": v(-100.38, -21.59) * mm, "end": v(-98.8, -18.86) * mm});
            skLineSegment(sketch, "E12.0.2.14", {"start": v(-98.8, -10.22) * mm, "end": v(-95.65, -10.22) * mm});
            skLineSegment(sketch, "E12.3.2.14", {"start": v(-95.65, -10.22) * mm, "end": v(-94.07, -12.95) * mm});
            skLineSegment(sketch, "E12.6.2.14", {"start": v(-94.07, -12.95) * mm, "end": v(-95.65, -15.68) * mm});
            skCircle(sketch, "E12.9.2.14", {"center": v(-97.23, -12.95) * mm, "radius": 2.73 * mm, "construction": true});
            skLineSegment(sketch, "E12.11.2.14", {"start": v(-95.65, -15.68) * mm, "end": v(-98.8, -15.68) * mm});
            skLineSegment(sketch, "E12.14.2.14", {"start": v(-98.8, -15.68) * mm, "end": v(-100.38, -12.95) * mm});
            skLineSegment(sketch, "E12.17.2.14", {"start": v(-100.38, -12.95) * mm, "end": v(-98.8, -10.22) * mm});
            skLineSegment(sketch, "E12.0.2.15", {"start": v(-98.8, -1.59) * mm, "end": v(-95.65, -1.59) * mm});
            skLineSegment(sketch, "E12.3.2.15", {"start": v(-95.65, -1.59) * mm, "end": v(-94.07, -4.32) * mm});
            skLineSegment(sketch, "E12.6.2.15", {"start": v(-94.07, -4.32) * mm, "end": v(-95.65, -7.05) * mm});
            skCircle(sketch, "E12.9.2.15", {"center": v(-97.23, -4.32) * mm, "radius": 2.73 * mm, "construction": true});
            skLineSegment(sketch, "E12.11.2.15", {"start": v(-95.65, -7.05) * mm, "end": v(-98.8, -7.05) * mm});
            skLineSegment(sketch, "E12.14.2.15", {"start": v(-98.8, -7.05) * mm, "end": v(-100.38, -4.32) * mm});
            skLineSegment(sketch, "E12.17.2.15", {"start": v(-100.38, -4.32) * mm, "end": v(-98.8, -1.59) * mm});
            skLineSegment(sketch, "E12.0.2.16", {"start": v(-98.8, 7.05) * mm, "end": v(-95.65, 7.05) * mm});
            skLineSegment(sketch, "E12.3.2.16", {"start": v(-95.65, 7.05) * mm, "end": v(-94.07, 4.32) * mm});
            skLineSegment(sketch, "E12.6.2.16", {"start": v(-94.07, 4.32) * mm, "end": v(-95.65, 1.59) * mm});
            skCircle(sketch, "E12.9.2.16", {"center": v(-97.23, 4.32) * mm, "radius": 2.73 * mm, "construction": true});
            skLineSegment(sketch, "E12.11.2.16", {"start": v(-95.65, 1.59) * mm, "end": v(-98.8, 1.59) * mm});
            skLineSegment(sketch, "E12.14.2.16", {"start": v(-98.8, 1.59) * mm, "end": v(-100.38, 4.32) * mm});
            skLineSegment(sketch, "E12.17.2.16", {"start": v(-100.38, 4.32) * mm, "end": v(-98.8, 7.05) * mm});
            skLineSegment(sketch, "E12.0.2.17", {"start": v(-98.8, 15.68) * mm, "end": v(-95.65, 15.68) * mm});
            skLineSegment(sketch, "E12.3.2.17", {"start": v(-95.65, 15.68) * mm, "end": v(-94.07, 12.95) * mm});
            skLineSegment(sketch, "E12.6.2.17", {"start": v(-94.07, 12.95) * mm, "end": v(-95.65, 10.22) * mm});
            skCircle(sketch, "E12.9.2.17", {"center": v(-97.23, 12.95) * mm, "radius": 2.73 * mm, "construction": true});
            skLineSegment(sketch, "E12.11.2.17", {"start": v(-95.65, 10.22) * mm, "end": v(-98.8, 10.22) * mm});
            skLineSegment(sketch, "E12.14.2.17", {"start": v(-98.8, 10.22) * mm, "end": v(-100.38, 12.95) * mm});
            skLineSegment(sketch, "E12.17.2.17", {"start": v(-100.38, 12.95) * mm, "end": v(-98.8, 15.68) * mm});
            skLineSegment(sketch, "E12.0.2.18", {"start": v(-98.8, 24.32) * mm, "end": v(-95.65, 24.32) * mm});
            skLineSegment(sketch, "E12.3.2.18", {"start": v(-95.65, 24.32) * mm, "end": v(-94.07, 21.59) * mm});
            skLineSegment(sketch, "E12.6.2.18", {"start": v(-94.07, 21.59) * mm, "end": v(-95.65, 18.86) * mm});
            skCircle(sketch, "E12.9.2.18", {"center": v(-97.23, 21.59) * mm, "radius": 2.73 * mm, "construction": true});
            skLineSegment(sketch, "E12.11.2.18", {"start": v(-95.65, 18.86) * mm, "end": v(-98.8, 18.86) * mm});
            skLineSegment(sketch, "E12.14.2.18", {"start": v(-98.8, 18.86) * mm, "end": v(-100.38, 21.59) * mm});
            skLineSegment(sketch, "E12.17.2.18", {"start": v(-100.38, 21.59) * mm, "end": v(-98.8, 24.32) * mm});
            skLineSegment(sketch, "E12.0.2.19", {"start": v(-98.8, 32.96) * mm, "end": v(-95.65, 32.96) * mm});
            skLineSegment(sketch, "E12.3.2.19", {"start": v(-95.65, 32.96) * mm, "end": v(-94.07, 30.23) * mm});
            skLineSegment(sketch, "E12.6.2.19", {"start": v(-94.07, 30.23) * mm, "end": v(-95.65, 27.5) * mm});
            skCircle(sketch, "E12.9.2.19", {"center": v(-97.23, 30.23) * mm, "radius": 2.73 * mm, "construction": true});
            skLineSegment(sketch, "E12.11.2.19", {"start": v(-95.65, 27.5) * mm, "end": v(-98.8, 27.5) * mm});
            skLineSegment(sketch, "E12.14.2.19", {"start": v(-98.8, 27.5) * mm, "end": v(-100.38, 30.23) * mm});
            skLineSegment(sketch, "E12.17.2.19", {"start": v(-100.38, 30.23) * mm, "end": v(-98.8, 32.96) * mm});
            skLineSegment(sketch, "E12.0.3.9", {"start": v(-83.85, -53.4) * mm, "end": v(-80.7, -53.4) * mm});
            skLineSegment(sketch, "E12.3.3.9", {"start": v(-80.7, -53.4) * mm, "end": v(-79.12, -56.13) * mm});
            skLineSegment(sketch, "E12.6.3.9", {"start": v(-79.12, -56.13) * mm, "end": v(-80.7, -58.86) * mm});
            skCircle(sketch, "E12.9.3.9", {"center": v(-82.27, -56.13) * mm, "radius": 2.73 * mm, "construction": true});
            skLineSegment(sketch, "E12.11.3.9", {"start": v(-80.7, -58.86) * mm, "end": v(-83.85, -58.86) * mm});
            skLineSegment(sketch, "E12.14.3.9", {"start": v(-83.85, -58.86) * mm, "end": v(-85.42, -56.13) * mm});
            skLineSegment(sketch, "E12.17.3.9", {"start": v(-85.42, -56.13) * mm, "end": v(-83.85, -53.4) * mm});
            skLineSegment(sketch, "E12.0.3.10", {"start": v(-83.85, -44.77) * mm, "end": v(-80.7, -44.77) * mm});
            skLineSegment(sketch, "E12.3.3.10", {"start": v(-80.7, -44.77) * mm, "end": v(-79.12, -47.5) * mm});
            skLineSegment(sketch, "E12.6.3.10", {"start": v(-79.12, -47.5) * mm, "end": v(-80.7, -50.23) * mm});
            skCircle(sketch, "E12.9.3.10", {"center": v(-82.27, -47.5) * mm, "radius": 2.73 * mm, "construction": true});
            skLineSegment(sketch, "E12.11.3.10", {"start": v(-80.7, -50.23) * mm, "end": v(-83.85, -50.23) * mm});
            skLineSegment(sketch, "E12.14.3.10", {"start": v(-83.85, -50.23) * mm, "end": v(-85.42, -47.5) * mm});
            skLineSegment(sketch, "E12.17.3.10", {"start": v(-85.42, -47.5) * mm, "end": v(-83.85, -44.77) * mm});
            skLineSegment(sketch, "E12.0.3.11", {"start": v(-83.85, -36.13) * mm, "end": v(-80.7, -36.13) * mm});
            skLineSegment(sketch, "E12.3.3.11", {"start": v(-80.7, -36.13) * mm, "end": v(-79.12, -38.86) * mm});
            skLineSegment(sketch, "E12.6.3.11", {"start": v(-79.12, -38.86) * mm, "end": v(-80.7, -41.6) * mm});
            skCircle(sketch, "E12.9.3.11", {"center": v(-82.27, -38.86) * mm, "radius": 2.73 * mm, "construction": true});
            skLineSegment(sketch, "E12.11.3.11", {"start": v(-80.7, -41.6) * mm, "end": v(-83.85, -41.6) * mm});
            skLineSegment(sketch, "E12.14.3.11", {"start": v(-83.85, -41.6) * mm, "end": v(-85.42, -38.86) * mm});
            skLineSegment(sketch, "E12.17.3.11", {"start": v(-85.42, -38.86) * mm, "end": v(-83.85, -36.13) * mm});
            skLineSegment(sketch, "E12.0.3.12", {"start": v(-83.85, -27.5) * mm, "end": v(-80.7, -27.5) * mm});
            skLineSegment(sketch, "E12.3.3.12", {"start": v(-80.7, -27.5) * mm, "end": v(-79.12, -30.23) * mm});
            skLineSegment(sketch, "E12.6.3.12", {"start": v(-79.12, -30.23) * mm, "end": v(-80.7, -32.96) * mm});
            skCircle(sketch, "E12.9.3.12", {"center": v(-82.27, -30.23) * mm, "radius": 2.73 * mm, "construction": true});
            skLineSegment(sketch, "E12.11.3.12", {"start": v(-80.7, -32.96) * mm, "end": v(-83.85, -32.96) * mm});
            skLineSegment(sketch, "E12.14.3.12", {"start": v(-83.85, -32.96) * mm, "end": v(-85.42, -30.23) * mm});
            skLineSegment(sketch, "E12.17.3.12", {"start": v(-85.42, -30.23) * mm, "end": v(-83.85, -27.5) * mm});
            skLineSegment(sketch, "E12.0.3.13", {"start": v(-83.85, -18.86) * mm, "end": v(-80.7, -18.86) * mm});
            skLineSegment(sketch, "E12.3.3.13", {"start": v(-80.7, -18.86) * mm, "end": v(-79.12, -21.6) * mm});
            skLineSegment(sketch, "E12.6.3.13", {"start": v(-79.12, -21.6) * mm, "end": v(-80.7, -24.32) * mm});
            skCircle(sketch, "E12.9.3.13", {"center": v(-82.27, -21.6) * mm, "radius": 2.73 * mm, "construction": true});
            skLineSegment(sketch, "E12.11.3.13", {"start": v(-80.7, -24.32) * mm, "end": v(-83.85, -24.32) * mm});
            skLineSegment(sketch, "E12.14.3.13", {"start": v(-83.85, -24.32) * mm, "end": v(-85.42, -21.6) * mm});
            skLineSegment(sketch, "E12.17.3.13", {"start": v(-85.42, -21.59) * mm, "end": v(-83.85, -18.86) * mm});
            skLineSegment(sketch, "E12.0.3.14", {"start": v(-83.85, -10.22) * mm, "end": v(-80.7, -10.22) * mm});
            skLineSegment(sketch, "E12.3.3.14", {"start": v(-80.7, -10.22) * mm, "end": v(-79.12, -12.95) * mm});
            skLineSegment(sketch, "E12.6.3.14", {"start": v(-79.12, -12.95) * mm, "end": v(-80.7, -15.68) * mm});
            skCircle(sketch, "E12.9.3.14", {"center": v(-82.27, -12.95) * mm, "radius": 2.73 * mm, "construction": true});
            skLineSegment(sketch, "E12.11.3.14", {"start": v(-80.7, -15.68) * mm, "end": v(-83.85, -15.68) * mm});
            skLineSegment(sketch, "E12.14.3.14", {"start": v(-83.85, -15.68) * mm, "end": v(-85.42, -12.95) * mm});
            skLineSegment(sketch, "E12.17.3.14", {"start": v(-85.42, -12.95) * mm, "end": v(-83.85, -10.22) * mm});
            skLineSegment(sketch, "E12.0.3.15", {"start": v(-83.85, -1.59) * mm, "end": v(-80.7, -1.59) * mm});
            skLineSegment(sketch, "E12.3.3.15", {"start": v(-80.7, -1.59) * mm, "end": v(-79.12, -4.32) * mm});
            skLineSegment(sketch, "E12.6.3.15", {"start": v(-79.12, -4.32) * mm, "end": v(-80.7, -7.05) * mm});
            skCircle(sketch, "E12.9.3.15", {"center": v(-82.27, -4.32) * mm, "radius": 2.73 * mm, "construction": true});
            skLineSegment(sketch, "E12.11.3.15", {"start": v(-80.7, -7.05) * mm, "end": v(-83.85, -7.05) * mm});
            skLineSegment(sketch, "E12.14.3.15", {"start": v(-83.85, -7.05) * mm, "end": v(-85.42, -4.32) * mm});
            skLineSegment(sketch, "E12.17.3.15", {"start": v(-85.42, -4.32) * mm, "end": v(-83.85, -1.59) * mm});
            skLineSegment(sketch, "E12.0.3.16", {"start": v(-83.85, 7.05) * mm, "end": v(-80.7, 7.05) * mm});
            skLineSegment(sketch, "E12.3.3.16", {"start": v(-80.7, 7.05) * mm, "end": v(-79.12, 4.32) * mm});
            skLineSegment(sketch, "E12.6.3.16", {"start": v(-79.12, 4.32) * mm, "end": v(-80.7, 1.59) * mm});
            skCircle(sketch, "E12.9.3.16", {"center": v(-82.27, 4.32) * mm, "radius": 2.73 * mm, "construction": true});
            skLineSegment(sketch, "E12.11.3.16", {"start": v(-80.7, 1.59) * mm, "end": v(-83.85, 1.59) * mm});
            skLineSegment(sketch, "E12.14.3.16", {"start": v(-83.85, 1.59) * mm, "end": v(-85.42, 4.32) * mm});
            skLineSegment(sketch, "E12.17.3.16", {"start": v(-85.42, 4.32) * mm, "end": v(-83.85, 7.05) * mm});
            skLineSegment(sketch, "E12.0.3.17", {"start": v(-83.85, 15.68) * mm, "end": v(-80.7, 15.68) * mm});
            skLineSegment(sketch, "E12.3.3.17", {"start": v(-80.7, 15.68) * mm, "end": v(-79.12, 12.95) * mm});
            skLineSegment(sketch, "E12.6.3.17", {"start": v(-79.12, 12.95) * mm, "end": v(-80.7, 10.22) * mm});
            skCircle(sketch, "E12.9.3.17", {"center": v(-82.27, 12.95) * mm, "radius": 2.73 * mm, "construction": true});
            skLineSegment(sketch, "E12.11.3.17", {"start": v(-80.7, 10.22) * mm, "end": v(-83.85, 10.22) * mm});
            skLineSegment(sketch, "E12.14.3.17", {"start": v(-83.85, 10.22) * mm, "end": v(-85.42, 12.95) * mm});
            skLineSegment(sketch, "E12.17.3.17", {"start": v(-85.42, 12.95) * mm, "end": v(-83.85, 15.68) * mm});
            skLineSegment(sketch, "E12.0.3.18", {"start": v(-83.85, 24.32) * mm, "end": v(-80.7, 24.32) * mm});
            skLineSegment(sketch, "E12.3.3.18", {"start": v(-80.7, 24.32) * mm, "end": v(-79.12, 21.59) * mm});
            skLineSegment(sketch, "E12.6.3.18", {"start": v(-79.12, 21.59) * mm, "end": v(-80.7, 18.86) * mm});
            skCircle(sketch, "E12.9.3.18", {"center": v(-82.27, 21.59) * mm, "radius": 2.73 * mm, "construction": true});
            skLineSegment(sketch, "E12.11.3.18", {"start": v(-80.7, 18.86) * mm, "end": v(-83.85, 18.86) * mm});
            skLineSegment(sketch, "E12.14.3.18", {"start": v(-83.85, 18.86) * mm, "end": v(-85.42, 21.59) * mm});
            skLineSegment(sketch, "E12.17.3.18", {"start": v(-85.42, 21.6) * mm, "end": v(-83.85, 24.32) * mm});
            skLineSegment(sketch, "E12.0.3.19", {"start": v(-83.85, 32.96) * mm, "end": v(-80.7, 32.96) * mm});
            skLineSegment(sketch, "E12.3.3.19", {"start": v(-80.7, 32.96) * mm, "end": v(-79.12, 30.23) * mm});
            skLineSegment(sketch, "E12.6.3.19", {"start": v(-79.12, 30.23) * mm, "end": v(-80.7, 27.5) * mm});
            skCircle(sketch, "E12.9.3.19", {"center": v(-82.27, 30.23) * mm, "radius": 2.73 * mm, "construction": true});
            skLineSegment(sketch, "E12.11.3.19", {"start": v(-80.7, 27.5) * mm, "end": v(-83.85, 27.5) * mm});
            skLineSegment(sketch, "E12.14.3.19", {"start": v(-83.85, 27.5) * mm, "end": v(-85.42, 30.23) * mm});
            skLineSegment(sketch, "E12.17.3.19", {"start": v(-85.42, 30.23) * mm, "end": v(-83.85, 32.96) * mm});
            skLineSegment(sketch, "E12.0.4.9", {"start": v(-68.89, -53.4) * mm, "end": v(-65.73, -53.4) * mm});
            skLineSegment(sketch, "E12.3.4.9", {"start": v(-65.73, -53.4) * mm, "end": v(-64.16, -56.13) * mm});
            skLineSegment(sketch, "E12.6.4.9", {"start": v(-64.16, -56.13) * mm, "end": v(-65.73, -58.86) * mm});
            skCircle(sketch, "E12.9.4.9", {"center": v(-67.31, -56.13) * mm, "radius": 2.73 * mm, "construction": true});
            skLineSegment(sketch, "E12.11.4.9", {"start": v(-65.73, -58.86) * mm, "end": v(-68.89, -58.86) * mm});
            skLineSegment(sketch, "E12.14.4.9", {"start": v(-68.89, -58.86) * mm, "end": v(-70.46, -56.13) * mm});
            skLineSegment(sketch, "E12.17.4.9", {"start": v(-70.46, -56.13) * mm, "end": v(-68.89, -53.4) * mm});
            skLineSegment(sketch, "E12.0.4.10", {"start": v(-68.89, -44.77) * mm, "end": v(-65.73, -44.77) * mm});
            skLineSegment(sketch, "E12.3.4.10", {"start": v(-65.73, -44.77) * mm, "end": v(-64.16, -47.5) * mm});
            skLineSegment(sketch, "E12.6.4.10", {"start": v(-64.16, -47.5) * mm, "end": v(-65.73, -50.23) * mm});
            skCircle(sketch, "E12.9.4.10", {"center": v(-67.31, -47.5) * mm, "radius": 2.73 * mm, "construction": true});
            skLineSegment(sketch, "E12.11.4.10", {"start": v(-65.73, -50.23) * mm, "end": v(-68.89, -50.23) * mm});
            skLineSegment(sketch, "E12.14.4.10", {"start": v(-68.89, -50.23) * mm, "end": v(-70.46, -47.5) * mm});
            skLineSegment(sketch, "E12.17.4.10", {"start": v(-70.46, -47.5) * mm, "end": v(-68.89, -44.77) * mm});
            skLineSegment(sketch, "E12.0.4.11", {"start": v(-68.89, -36.13) * mm, "end": v(-65.73, -36.13) * mm});
            skLineSegment(sketch, "E12.3.4.11", {"start": v(-65.73, -36.13) * mm, "end": v(-64.16, -38.86) * mm});
            skLineSegment(sketch, "E12.6.4.11", {"start": v(-64.16, -38.86) * mm, "end": v(-65.73, -41.6) * mm});
            skCircle(sketch, "E12.9.4.11", {"center": v(-67.31, -38.86) * mm, "radius": 2.73 * mm, "construction": true});
            skLineSegment(sketch, "E12.11.4.11", {"start": v(-65.73, -41.6) * mm, "end": v(-68.89, -41.6) * mm});
            skLineSegment(sketch, "E12.14.4.11", {"start": v(-68.89, -41.6) * mm, "end": v(-70.46, -38.86) * mm});
            skLineSegment(sketch, "E12.17.4.11", {"start": v(-70.46, -38.86) * mm, "end": v(-68.89, -36.13) * mm});
            skLineSegment(sketch, "E12.0.4.12", {"start": v(-68.89, -27.5) * mm, "end": v(-65.73, -27.5) * mm});
            skLineSegment(sketch, "E12.3.4.12", {"start": v(-65.73, -27.5) * mm, "end": v(-64.16, -30.23) * mm});
            skLineSegment(sketch, "E12.6.4.12", {"start": v(-64.16, -30.23) * mm, "end": v(-65.73, -32.96) * mm});
            skCircle(sketch, "E12.9.4.12", {"center": v(-67.31, -30.23) * mm, "radius": 2.73 * mm, "construction": true});
            skLineSegment(sketch, "E12.11.4.12", {"start": v(-65.73, -32.96) * mm, "end": v(-68.89, -32.96) * mm});
            skLineSegment(sketch, "E12.14.4.12", {"start": v(-68.89, -32.96) * mm, "end": v(-70.46, -30.23) * mm});
            skLineSegment(sketch, "E12.17.4.12", {"start": v(-70.46, -30.23) * mm, "end": v(-68.89, -27.5) * mm});
            skLineSegment(sketch, "E12.0.4.13", {"start": v(-68.89, -18.86) * mm, "end": v(-65.73, -18.86) * mm});
            skLineSegment(sketch, "E12.3.4.13", {"start": v(-65.73, -18.86) * mm, "end": v(-64.16, -21.6) * mm});
            skLineSegment(sketch, "E12.6.4.13", {"start": v(-64.16, -21.6) * mm, "end": v(-65.73, -24.32) * mm});
            skCircle(sketch, "E12.9.4.13", {"center": v(-67.31, -21.6) * mm, "radius": 2.73 * mm, "construction": true});
            skLineSegment(sketch, "E12.11.4.13", {"start": v(-65.73, -24.32) * mm, "end": v(-68.89, -24.32) * mm});
            skLineSegment(sketch, "E12.14.4.13", {"start": v(-68.89, -24.32) * mm, "end": v(-70.46, -21.6) * mm});
            skLineSegment(sketch, "E12.17.4.13", {"start": v(-70.46, -21.59) * mm, "end": v(-68.89, -18.86) * mm});
            skLineSegment(sketch, "E12.0.4.14", {"start": v(-68.89, -10.22) * mm, "end": v(-65.73, -10.22) * mm});
            skLineSegment(sketch, "E12.3.4.14", {"start": v(-65.73, -10.22) * mm, "end": v(-64.16, -12.95) * mm});
            skLineSegment(sketch, "E12.6.4.14", {"start": v(-64.16, -12.95) * mm, "end": v(-65.73, -15.68) * mm});
            skCircle(sketch, "E12.9.4.14", {"center": v(-67.31, -12.95) * mm, "radius": 2.73 * mm, "construction": true});
            skLineSegment(sketch, "E12.11.4.14", {"start": v(-65.73, -15.68) * mm, "end": v(-68.89, -15.68) * mm});
            skLineSegment(sketch, "E12.14.4.14", {"start": v(-68.89, -15.68) * mm, "end": v(-70.46, -12.95) * mm});
            skLineSegment(sketch, "E12.17.4.14", {"start": v(-70.46, -12.95) * mm, "end": v(-68.89, -10.22) * mm});
            skLineSegment(sketch, "E12.0.4.15", {"start": v(-68.89, -1.59) * mm, "end": v(-65.73, -1.59) * mm});
            skLineSegment(sketch, "E12.3.4.15", {"start": v(-65.73, -1.59) * mm, "end": v(-64.16, -4.32) * mm});
            skLineSegment(sketch, "E12.6.4.15", {"start": v(-64.16, -4.32) * mm, "end": v(-65.73, -7.05) * mm});
            skCircle(sketch, "E12.9.4.15", {"center": v(-67.31, -4.32) * mm, "radius": 2.73 * mm, "construction": true});
            skLineSegment(sketch, "E12.11.4.15", {"start": v(-65.73, -7.05) * mm, "end": v(-68.89, -7.05) * mm});
            skLineSegment(sketch, "E12.14.4.15", {"start": v(-68.89, -7.05) * mm, "end": v(-70.46, -4.32) * mm});
            skLineSegment(sketch, "E12.17.4.15", {"start": v(-70.46, -4.32) * mm, "end": v(-68.89, -1.59) * mm});
            skLineSegment(sketch, "E12.0.4.16", {"start": v(-68.89, 7.05) * mm, "end": v(-65.73, 7.05) * mm});
            skLineSegment(sketch, "E12.3.4.16", {"start": v(-65.73, 7.05) * mm, "end": v(-64.16, 4.32) * mm});
            skLineSegment(sketch, "E12.6.4.16", {"start": v(-64.16, 4.32) * mm, "end": v(-65.73, 1.59) * mm});
            skCircle(sketch, "E12.9.4.16", {"center": v(-67.31, 4.32) * mm, "radius": 2.73 * mm, "construction": true});
            skLineSegment(sketch, "E12.11.4.16", {"start": v(-65.73, 1.59) * mm, "end": v(-68.89, 1.59) * mm});
            skLineSegment(sketch, "E12.14.4.16", {"start": v(-68.89, 1.59) * mm, "end": v(-70.46, 4.32) * mm});
            skLineSegment(sketch, "E12.17.4.16", {"start": v(-70.46, 4.32) * mm, "end": v(-68.89, 7.05) * mm});
            skLineSegment(sketch, "E12.0.4.17", {"start": v(-68.89, 15.68) * mm, "end": v(-65.73, 15.68) * mm});
            skLineSegment(sketch, "E12.3.4.17", {"start": v(-65.73, 15.68) * mm, "end": v(-64.16, 12.95) * mm});
            skLineSegment(sketch, "E12.6.4.17", {"start": v(-64.16, 12.95) * mm, "end": v(-65.73, 10.22) * mm});
            skCircle(sketch, "E12.9.4.17", {"center": v(-67.31, 12.95) * mm, "radius": 2.73 * mm, "construction": true});
            skLineSegment(sketch, "E12.11.4.17", {"start": v(-65.73, 10.22) * mm, "end": v(-68.89, 10.22) * mm});
            skLineSegment(sketch, "E12.14.4.17", {"start": v(-68.89, 10.22) * mm, "end": v(-70.46, 12.95) * mm});
            skLineSegment(sketch, "E12.17.4.17", {"start": v(-70.46, 12.95) * mm, "end": v(-68.89, 15.68) * mm});
            skLineSegment(sketch, "E12.0.4.18", {"start": v(-68.89, 24.32) * mm, "end": v(-65.73, 24.32) * mm});
            skLineSegment(sketch, "E12.3.4.18", {"start": v(-65.73, 24.32) * mm, "end": v(-64.16, 21.59) * mm});
            skLineSegment(sketch, "E12.6.4.18", {"start": v(-64.16, 21.59) * mm, "end": v(-65.73, 18.86) * mm});
            skCircle(sketch, "E12.9.4.18", {"center": v(-67.31, 21.59) * mm, "radius": 2.73 * mm, "construction": true});
            skLineSegment(sketch, "E12.11.4.18", {"start": v(-65.73, 18.86) * mm, "end": v(-68.89, 18.86) * mm});
            skLineSegment(sketch, "E12.14.4.18", {"start": v(-68.89, 18.86) * mm, "end": v(-70.46, 21.59) * mm});
            skLineSegment(sketch, "E12.17.4.18", {"start": v(-70.46, 21.6) * mm, "end": v(-68.89, 24.32) * mm});
            skLineSegment(sketch, "E12.0.4.19", {"start": v(-68.89, 32.96) * mm, "end": v(-65.73, 32.96) * mm});
            skLineSegment(sketch, "E12.3.4.19", {"start": v(-65.73, 32.96) * mm, "end": v(-64.16, 30.23) * mm});
            skLineSegment(sketch, "E12.6.4.19", {"start": v(-64.16, 30.23) * mm, "end": v(-65.73, 27.5) * mm});
            skCircle(sketch, "E12.9.4.19", {"center": v(-67.31, 30.23) * mm, "radius": 2.73 * mm, "construction": true});
            skLineSegment(sketch, "E12.11.4.19", {"start": v(-65.73, 27.5) * mm, "end": v(-68.89, 27.5) * mm});
            skLineSegment(sketch, "E12.14.4.19", {"start": v(-68.89, 27.5) * mm, "end": v(-70.46, 30.23) * mm});
            skLineSegment(sketch, "E12.17.4.19", {"start": v(-70.46, 30.23) * mm, "end": v(-68.89, 32.96) * mm});
            skLineSegment(sketch, "E12.0.5.9", {"start": v(-53.93, -53.4) * mm, "end": v(-50.78, -53.4) * mm});
            skLineSegment(sketch, "E12.3.5.9", {"start": v(-50.78, -53.4) * mm, "end": v(-49.2, -56.13) * mm});
            skLineSegment(sketch, "E12.6.5.9", {"start": v(-49.2, -56.13) * mm, "end": v(-50.78, -58.86) * mm});
            skCircle(sketch, "E12.9.5.9", {"center": v(-52.35, -56.13) * mm, "radius": 2.73 * mm, "construction": true});
            skLineSegment(sketch, "E12.11.5.9", {"start": v(-50.78, -58.86) * mm, "end": v(-53.93, -58.86) * mm});
            skLineSegment(sketch, "E12.14.5.9", {"start": v(-53.93, -58.86) * mm, "end": v(-55.5, -56.13) * mm});
            skLineSegment(sketch, "E12.17.5.9", {"start": v(-55.5, -56.13) * mm, "end": v(-53.93, -53.4) * mm});
            skLineSegment(sketch, "E12.0.5.10", {"start": v(-53.93, -44.77) * mm, "end": v(-50.78, -44.77) * mm});
            skLineSegment(sketch, "E12.3.5.10", {"start": v(-50.78, -44.77) * mm, "end": v(-49.2, -47.5) * mm});
            skLineSegment(sketch, "E12.6.5.10", {"start": v(-49.2, -47.5) * mm, "end": v(-50.78, -50.23) * mm});
            skCircle(sketch, "E12.9.5.10", {"center": v(-52.35, -47.5) * mm, "radius": 2.73 * mm, "construction": true});
            skLineSegment(sketch, "E12.11.5.10", {"start": v(-50.78, -50.23) * mm, "end": v(-53.93, -50.23) * mm});
            skLineSegment(sketch, "E12.14.5.10", {"start": v(-53.93, -50.23) * mm, "end": v(-55.5, -47.5) * mm});
            skLineSegment(sketch, "E12.17.5.10", {"start": v(-55.5, -47.5) * mm, "end": v(-53.93, -44.77) * mm});
            skLineSegment(sketch, "E12.0.5.11", {"start": v(-53.93, -36.13) * mm, "end": v(-50.78, -36.13) * mm});
            skLineSegment(sketch, "E12.3.5.11", {"start": v(-50.78, -36.13) * mm, "end": v(-49.2, -38.86) * mm});
            skLineSegment(sketch, "E12.6.5.11", {"start": v(-49.2, -38.86) * mm, "end": v(-50.78, -41.6) * mm});
            skCircle(sketch, "E12.9.5.11", {"center": v(-52.35, -38.86) * mm, "radius": 2.73 * mm, "construction": true});
            skLineSegment(sketch, "E12.11.5.11", {"start": v(-50.78, -41.6) * mm, "end": v(-53.93, -41.6) * mm});
            skLineSegment(sketch, "E12.14.5.11", {"start": v(-53.93, -41.6) * mm, "end": v(-55.5, -38.86) * mm});
            skLineSegment(sketch, "E12.17.5.11", {"start": v(-55.5, -38.86) * mm, "end": v(-53.93, -36.13) * mm});
            skLineSegment(sketch, "E12.0.5.12", {"start": v(-53.93, -27.5) * mm, "end": v(-50.78, -27.5) * mm});
            skLineSegment(sketch, "E12.3.5.12", {"start": v(-50.78, -27.5) * mm, "end": v(-49.2, -30.23) * mm});
            skLineSegment(sketch, "E12.6.5.12", {"start": v(-49.2, -30.23) * mm, "end": v(-50.78, -32.96) * mm});
            skCircle(sketch, "E12.9.5.12", {"center": v(-52.35, -30.23) * mm, "radius": 2.73 * mm, "construction": true});
            skLineSegment(sketch, "E12.11.5.12", {"start": v(-50.78, -32.96) * mm, "end": v(-53.93, -32.96) * mm});
            skLineSegment(sketch, "E12.14.5.12", {"start": v(-53.93, -32.96) * mm, "end": v(-55.5, -30.23) * mm});
            skLineSegment(sketch, "E12.17.5.12", {"start": v(-55.5, -30.23) * mm, "end": v(-53.93, -27.5) * mm});
            skLineSegment(sketch, "E12.0.5.13", {"start": v(-53.93, -18.86) * mm, "end": v(-50.78, -18.86) * mm});
            skLineSegment(sketch, "E12.3.5.13", {"start": v(-50.78, -18.86) * mm, "end": v(-49.2, -21.6) * mm});
            skLineSegment(sketch, "E12.6.5.13", {"start": v(-49.2, -21.6) * mm, "end": v(-50.78, -24.32) * mm});
            skCircle(sketch, "E12.9.5.13", {"center": v(-52.35, -21.6) * mm, "radius": 2.73 * mm, "construction": true});
            skLineSegment(sketch, "E12.11.5.13", {"start": v(-50.78, -24.32) * mm, "end": v(-53.93, -24.32) * mm});
            skLineSegment(sketch, "E12.14.5.13", {"start": v(-53.93, -24.32) * mm, "end": v(-55.5, -21.6) * mm});
            skLineSegment(sketch, "E12.17.5.13", {"start": v(-55.5, -21.59) * mm, "end": v(-53.93, -18.86) * mm});
            skLineSegment(sketch, "E12.0.5.14", {"start": v(-53.93, -10.22) * mm, "end": v(-50.78, -10.22) * mm});
            skLineSegment(sketch, "E12.3.5.14", {"start": v(-50.78, -10.22) * mm, "end": v(-49.2, -12.95) * mm});
            skLineSegment(sketch, "E12.6.5.14", {"start": v(-49.2, -12.95) * mm, "end": v(-50.78, -15.68) * mm});
            skCircle(sketch, "E12.9.5.14", {"center": v(-52.35, -12.95) * mm, "radius": 2.73 * mm, "construction": true});
            skLineSegment(sketch, "E12.11.5.14", {"start": v(-50.78, -15.68) * mm, "end": v(-53.93, -15.68) * mm});
            skLineSegment(sketch, "E12.14.5.14", {"start": v(-53.93, -15.68) * mm, "end": v(-55.5, -12.95) * mm});
            skLineSegment(sketch, "E12.17.5.14", {"start": v(-55.5, -12.95) * mm, "end": v(-53.93, -10.22) * mm});
            skLineSegment(sketch, "E12.0.5.15", {"start": v(-53.93, -1.59) * mm, "end": v(-50.78, -1.59) * mm});
            skLineSegment(sketch, "E12.3.5.15", {"start": v(-50.78, -1.59) * mm, "end": v(-49.2, -4.32) * mm});
            skLineSegment(sketch, "E12.6.5.15", {"start": v(-49.2, -4.32) * mm, "end": v(-50.78, -7.05) * mm});
            skCircle(sketch, "E12.9.5.15", {"center": v(-52.35, -4.32) * mm, "radius": 2.73 * mm, "construction": true});
            skLineSegment(sketch, "E12.11.5.15", {"start": v(-50.78, -7.05) * mm, "end": v(-53.93, -7.05) * mm});
            skLineSegment(sketch, "E12.14.5.15", {"start": v(-53.93, -7.05) * mm, "end": v(-55.5, -4.32) * mm});
            skLineSegment(sketch, "E12.17.5.15", {"start": v(-55.5, -4.32) * mm, "end": v(-53.93, -1.59) * mm});
            skLineSegment(sketch, "E12.0.5.16", {"start": v(-53.93, 7.05) * mm, "end": v(-50.78, 7.05) * mm});
            skLineSegment(sketch, "E12.3.5.16", {"start": v(-50.78, 7.05) * mm, "end": v(-49.2, 4.32) * mm});
            skLineSegment(sketch, "E12.6.5.16", {"start": v(-49.2, 4.32) * mm, "end": v(-50.78, 1.59) * mm});
            skCircle(sketch, "E12.9.5.16", {"center": v(-52.35, 4.32) * mm, "radius": 2.73 * mm, "construction": true});
            skLineSegment(sketch, "E12.11.5.16", {"start": v(-50.78, 1.59) * mm, "end": v(-53.93, 1.59) * mm});
            skLineSegment(sketch, "E12.14.5.16", {"start": v(-53.93, 1.59) * mm, "end": v(-55.5, 4.32) * mm});
            skLineSegment(sketch, "E12.17.5.16", {"start": v(-55.5, 4.32) * mm, "end": v(-53.93, 7.05) * mm});
            skLineSegment(sketch, "E12.0.5.17", {"start": v(-53.93, 15.68) * mm, "end": v(-50.78, 15.68) * mm});
            skLineSegment(sketch, "E12.3.5.17", {"start": v(-50.78, 15.68) * mm, "end": v(-49.2, 12.95) * mm});
            skLineSegment(sketch, "E12.6.5.17", {"start": v(-49.2, 12.95) * mm, "end": v(-50.78, 10.22) * mm});
            skCircle(sketch, "E12.9.5.17", {"center": v(-52.35, 12.95) * mm, "radius": 2.73 * mm, "construction": true});
            skLineSegment(sketch, "E12.11.5.17", {"start": v(-50.78, 10.22) * mm, "end": v(-53.93, 10.22) * mm});
            skLineSegment(sketch, "E12.14.5.17", {"start": v(-53.93, 10.22) * mm, "end": v(-55.5, 12.95) * mm});
            skLineSegment(sketch, "E12.17.5.17", {"start": v(-55.5, 12.95) * mm, "end": v(-53.93, 15.68) * mm});
            skLineSegment(sketch, "E12.0.5.18", {"start": v(-53.93, 24.32) * mm, "end": v(-50.78, 24.32) * mm});
            skLineSegment(sketch, "E12.3.5.18", {"start": v(-50.78, 24.32) * mm, "end": v(-49.2, 21.59) * mm});
            skLineSegment(sketch, "E12.6.5.18", {"start": v(-49.2, 21.59) * mm, "end": v(-50.78, 18.86) * mm});
            skCircle(sketch, "E12.9.5.18", {"center": v(-52.35, 21.59) * mm, "radius": 2.73 * mm, "construction": true});
            skLineSegment(sketch, "E12.11.5.18", {"start": v(-50.78, 18.86) * mm, "end": v(-53.93, 18.86) * mm});
            skLineSegment(sketch, "E12.14.5.18", {"start": v(-53.93, 18.86) * mm, "end": v(-55.5, 21.59) * mm});
            skLineSegment(sketch, "E12.17.5.18", {"start": v(-55.5, 21.59) * mm, "end": v(-53.93, 24.32) * mm});
            skLineSegment(sketch, "E12.0.5.19", {"start": v(-53.93, 32.96) * mm, "end": v(-50.78, 32.96) * mm});
            skLineSegment(sketch, "E12.3.5.19", {"start": v(-50.78, 32.96) * mm, "end": v(-49.2, 30.23) * mm});
            skLineSegment(sketch, "E12.6.5.19", {"start": v(-49.2, 30.23) * mm, "end": v(-50.78, 27.5) * mm});
            skCircle(sketch, "E12.9.5.19", {"center": v(-52.35, 30.23) * mm, "radius": 2.73 * mm, "construction": true});
            skLineSegment(sketch, "E12.11.5.19", {"start": v(-50.78, 27.5) * mm, "end": v(-53.93, 27.5) * mm});
            skLineSegment(sketch, "E12.14.5.19", {"start": v(-53.93, 27.5) * mm, "end": v(-55.5, 30.23) * mm});
            skLineSegment(sketch, "E12.17.5.19", {"start": v(-55.5, 30.23) * mm, "end": v(-53.93, 32.96) * mm});
            skCircle(sketch, "E13.0.0.8", {"center": v(-119.66, -60.45) * mm, "radius": 2.73 * mm, "construction": true});
            skLineSegment(sketch, "E13.2.0.8", {"start": v(-122.82, -60.45) * mm, "end": v(-121.24, -57.72) * mm});
            skLineSegment(sketch, "E13.5.0.8", {"start": v(-121.24, -57.72) * mm, "end": v(-118.09, -57.72) * mm});
            skLineSegment(sketch, "E13.8.0.8", {"start": v(-118.09, -57.72) * mm, "end": v(-116.51, -60.45) * mm});
            skLineSegment(sketch, "E13.11.0.8", {"start": v(-116.51, -60.45) * mm, "end": v(-118.09, -63.18) * mm});
            skLineSegment(sketch, "E13.14.0.8", {"start": v(-118.09, -63.18) * mm, "end": v(-121.24, -63.18) * mm});
            skLineSegment(sketch, "E13.17.0.8", {"start": v(-121.24, -63.18) * mm, "end": v(-122.82, -60.45) * mm});
            skCircle(sketch, "E13.0.0.9", {"center": v(-119.66, -51.82) * mm, "radius": 2.73 * mm, "construction": true});
            skLineSegment(sketch, "E13.2.0.9", {"start": v(-122.82, -51.82) * mm, "end": v(-121.24, -49.09) * mm});
            skLineSegment(sketch, "E13.5.0.9", {"start": v(-121.24, -49.09) * mm, "end": v(-118.09, -49.09) * mm});
            skLineSegment(sketch, "E13.8.0.9", {"start": v(-118.09, -49.09) * mm, "end": v(-116.51, -51.82) * mm});
            skLineSegment(sketch, "E13.11.0.9", {"start": v(-116.51, -51.82) * mm, "end": v(-118.09, -54.55) * mm});
            skLineSegment(sketch, "E13.14.0.9", {"start": v(-118.09, -54.55) * mm, "end": v(-121.24, -54.55) * mm});
            skLineSegment(sketch, "E13.17.0.9", {"start": v(-121.24, -54.55) * mm, "end": v(-122.82, -51.82) * mm});
            skCircle(sketch, "E13.0.0.10", {"center": v(-119.66, -43.18) * mm, "radius": 2.73 * mm, "construction": true});
            skLineSegment(sketch, "E13.2.0.10", {"start": v(-122.82, -43.18) * mm, "end": v(-121.24, -40.45) * mm});
            skLineSegment(sketch, "E13.5.0.10", {"start": v(-121.24, -40.45) * mm, "end": v(-118.09, -40.45) * mm});
            skLineSegment(sketch, "E13.8.0.10", {"start": v(-118.09, -40.45) * mm, "end": v(-116.51, -43.18) * mm});
            skLineSegment(sketch, "E13.11.0.10", {"start": v(-116.51, -43.18) * mm, "end": v(-118.09, -45.91) * mm});
            skLineSegment(sketch, "E13.14.0.10", {"start": v(-118.09, -45.91) * mm, "end": v(-121.24, -45.91) * mm});
            skLineSegment(sketch, "E13.17.0.10", {"start": v(-121.24, -45.91) * mm, "end": v(-122.82, -43.18) * mm});
            skCircle(sketch, "E13.0.0.11", {"center": v(-119.66, -34.54) * mm, "radius": 2.73 * mm, "construction": true});
            skLineSegment(sketch, "E13.2.0.11", {"start": v(-122.82, -34.54) * mm, "end": v(-121.24, -31.81) * mm});
            skLineSegment(sketch, "E13.5.0.11", {"start": v(-121.24, -31.81) * mm, "end": v(-118.09, -31.81) * mm});
            skLineSegment(sketch, "E13.8.0.11", {"start": v(-118.09, -31.81) * mm, "end": v(-116.51, -34.54) * mm});
            skLineSegment(sketch, "E13.11.0.11", {"start": v(-116.51, -34.54) * mm, "end": v(-118.09, -37.27) * mm});
            skLineSegment(sketch, "E13.14.0.11", {"start": v(-118.09, -37.27) * mm, "end": v(-121.24, -37.27) * mm});
            skLineSegment(sketch, "E13.17.0.11", {"start": v(-121.24, -37.27) * mm, "end": v(-122.82, -34.54) * mm});
            skCircle(sketch, "E13.0.0.12", {"center": v(-119.66, -25.9) * mm, "radius": 2.73 * mm, "construction": true});
            skLineSegment(sketch, "E13.2.0.12", {"start": v(-122.82, -25.9) * mm, "end": v(-121.24, -23.18) * mm});
            skLineSegment(sketch, "E13.5.0.12", {"start": v(-121.24, -23.18) * mm, "end": v(-118.09, -23.18) * mm});
            skLineSegment(sketch, "E13.8.0.12", {"start": v(-118.09, -23.18) * mm, "end": v(-116.51, -25.9) * mm});
            skLineSegment(sketch, "E13.11.0.12", {"start": v(-116.51, -25.9) * mm, "end": v(-118.09, -28.64) * mm});
            skLineSegment(sketch, "E13.14.0.12", {"start": v(-118.09, -28.64) * mm, "end": v(-121.24, -28.64) * mm});
            skLineSegment(sketch, "E13.17.0.12", {"start": v(-121.24, -28.64) * mm, "end": v(-122.82, -25.9) * mm});
            skCircle(sketch, "E13.0.0.13", {"center": v(-119.66, -17.27) * mm, "radius": 2.73 * mm, "construction": true});
            skLineSegment(sketch, "E13.2.0.13", {"start": v(-122.82, -17.27) * mm, "end": v(-121.24, -14.54) * mm});
            skLineSegment(sketch, "E13.5.0.13", {"start": v(-121.24, -14.54) * mm, "end": v(-118.09, -14.54) * mm});
            skLineSegment(sketch, "E13.8.0.13", {"start": v(-118.09, -14.54) * mm, "end": v(-116.51, -17.27) * mm});
            skLineSegment(sketch, "E13.11.0.13", {"start": v(-116.51, -17.27) * mm, "end": v(-118.09, -20) * mm});
            skLineSegment(sketch, "E13.14.0.13", {"start": v(-118.09, -20) * mm, "end": v(-121.24, -20) * mm});
            skLineSegment(sketch, "E13.17.0.13", {"start": v(-121.24, -20) * mm, "end": v(-122.82, -17.27) * mm});
            skCircle(sketch, "E13.0.0.14", {"center": v(-119.66, -8.64) * mm, "radius": 2.73 * mm, "construction": true});
            skLineSegment(sketch, "E13.2.0.14", {"start": v(-122.82, -8.64) * mm, "end": v(-121.24, -5.9) * mm});
            skLineSegment(sketch, "E13.5.0.14", {"start": v(-121.24, -5.9) * mm, "end": v(-118.09, -5.9) * mm});
            skLineSegment(sketch, "E13.8.0.14", {"start": v(-118.09, -5.9) * mm, "end": v(-116.51, -8.64) * mm});
            skLineSegment(sketch, "E13.11.0.14", {"start": v(-116.51, -8.64) * mm, "end": v(-118.09, -11.37) * mm});
            skLineSegment(sketch, "E13.14.0.14", {"start": v(-118.09, -11.37) * mm, "end": v(-121.24, -11.37) * mm});
            skLineSegment(sketch, "E13.17.0.14", {"start": v(-121.24, -11.37) * mm, "end": v(-122.82, -8.64) * mm});
            skCircle(sketch, "E13.0.0.15", {"center": v(-119.66, 0) * mm, "radius": 2.73 * mm, "construction": true});
            skLineSegment(sketch, "E13.2.0.15", {"start": v(-122.82, 0) * mm, "end": v(-121.24, 2.73) * mm});
            skLineSegment(sketch, "E13.5.0.15", {"start": v(-121.24, 2.73) * mm, "end": v(-118.09, 2.73) * mm});
            skLineSegment(sketch, "E13.8.0.15", {"start": v(-118.09, 2.73) * mm, "end": v(-116.51, 0) * mm});
            skLineSegment(sketch, "E13.11.0.15", {"start": v(-116.51, 0) * mm, "end": v(-118.09, -2.73) * mm});
            skLineSegment(sketch, "E13.14.0.15", {"start": v(-118.09, -2.73) * mm, "end": v(-121.24, -2.73) * mm});
            skLineSegment(sketch, "E13.17.0.15", {"start": v(-121.24, -2.73) * mm, "end": v(-122.82, 0) * mm});
            skCircle(sketch, "E13.0.0.16", {"center": v(-119.66, 8.64) * mm, "radius": 2.73 * mm, "construction": true});
            skLineSegment(sketch, "E13.2.0.16", {"start": v(-122.82, 8.64) * mm, "end": v(-121.24, 11.37) * mm});
            skLineSegment(sketch, "E13.5.0.16", {"start": v(-121.24, 11.37) * mm, "end": v(-118.09, 11.37) * mm});
            skLineSegment(sketch, "E13.8.0.16", {"start": v(-118.09, 11.37) * mm, "end": v(-116.51, 8.64) * mm});
            skLineSegment(sketch, "E13.11.0.16", {"start": v(-116.51, 8.64) * mm, "end": v(-118.09, 5.9) * mm});
            skLineSegment(sketch, "E13.14.0.16", {"start": v(-118.09, 5.9) * mm, "end": v(-121.24, 5.9) * mm});
            skLineSegment(sketch, "E13.17.0.16", {"start": v(-121.24, 5.9) * mm, "end": v(-122.82, 8.64) * mm});
            skCircle(sketch, "E13.0.0.17", {"center": v(-119.66, 17.27) * mm, "radius": 2.73 * mm, "construction": true});
            skLineSegment(sketch, "E13.2.0.17", {"start": v(-122.82, 17.27) * mm, "end": v(-121.24, 20) * mm});
            skLineSegment(sketch, "E13.5.0.17", {"start": v(-121.24, 20) * mm, "end": v(-118.09, 20) * mm});
            skLineSegment(sketch, "E13.8.0.17", {"start": v(-118.09, 20) * mm, "end": v(-116.51, 17.27) * mm});
            skLineSegment(sketch, "E13.11.0.17", {"start": v(-116.51, 17.27) * mm, "end": v(-118.09, 14.54) * mm});
            skLineSegment(sketch, "E13.14.0.17", {"start": v(-118.09, 14.54) * mm, "end": v(-121.24, 14.54) * mm});
            skLineSegment(sketch, "E13.17.0.17", {"start": v(-121.24, 14.54) * mm, "end": v(-122.82, 17.27) * mm});
            skCircle(sketch, "E13.0.0.18", {"center": v(-119.66, 25.9) * mm, "radius": 2.73 * mm, "construction": true});
            skLineSegment(sketch, "E13.2.0.18", {"start": v(-122.82, 25.9) * mm, "end": v(-121.24, 28.64) * mm});
            skLineSegment(sketch, "E13.5.0.18", {"start": v(-121.24, 28.64) * mm, "end": v(-118.09, 28.64) * mm});
            skLineSegment(sketch, "E13.8.0.18", {"start": v(-118.09, 28.64) * mm, "end": v(-116.51, 25.9) * mm});
            skLineSegment(sketch, "E13.11.0.18", {"start": v(-116.51, 25.9) * mm, "end": v(-118.09, 23.18) * mm});
            skLineSegment(sketch, "E13.14.0.18", {"start": v(-118.09, 23.18) * mm, "end": v(-121.24, 23.18) * mm});
            skLineSegment(sketch, "E13.17.0.18", {"start": v(-121.24, 23.18) * mm, "end": v(-122.82, 25.9) * mm});
            skCircle(sketch, "E13.0.0.19", {"center": v(-119.66, 34.54) * mm, "radius": 2.73 * mm, "construction": true});
            skLineSegment(sketch, "E13.2.0.19", {"start": v(-122.82, 34.54) * mm, "end": v(-121.24, 37.27) * mm});
            skLineSegment(sketch, "E13.5.0.19", {"start": v(-121.24, 37.27) * mm, "end": v(-118.09, 37.27) * mm});
            skLineSegment(sketch, "E13.8.0.19", {"start": v(-118.09, 37.27) * mm, "end": v(-116.51, 34.54) * mm});
            skLineSegment(sketch, "E13.11.0.19", {"start": v(-116.51, 34.54) * mm, "end": v(-118.09, 31.81) * mm});
            skLineSegment(sketch, "E13.14.0.19", {"start": v(-118.09, 31.81) * mm, "end": v(-121.24, 31.81) * mm});
            skLineSegment(sketch, "E13.17.0.19", {"start": v(-121.24, 31.81) * mm, "end": v(-122.82, 34.54) * mm});
            skCircle(sketch, "E13.0.1.8", {"center": v(-104.7, -60.45) * mm, "radius": 2.73 * mm, "construction": true});
            skLineSegment(sketch, "E13.2.1.8", {"start": v(-107.86, -60.45) * mm, "end": v(-106.28, -57.72) * mm});
            skLineSegment(sketch, "E13.5.1.8", {"start": v(-106.28, -57.72) * mm, "end": v(-103.13, -57.72) * mm});
            skLineSegment(sketch, "E13.8.1.8", {"start": v(-103.13, -57.72) * mm, "end": v(-101.55, -60.45) * mm});
            skLineSegment(sketch, "E13.11.1.8", {"start": v(-101.55, -60.45) * mm, "end": v(-103.13, -63.18) * mm});
            skLineSegment(sketch, "E13.14.1.8", {"start": v(-103.13, -63.18) * mm, "end": v(-106.28, -63.18) * mm});
            skLineSegment(sketch, "E13.17.1.8", {"start": v(-106.28, -63.18) * mm, "end": v(-107.86, -60.45) * mm});
            skCircle(sketch, "E13.0.1.9", {"center": v(-104.7, -51.82) * mm, "radius": 2.73 * mm, "construction": true});
            skLineSegment(sketch, "E13.2.1.9", {"start": v(-107.86, -51.82) * mm, "end": v(-106.28, -49.09) * mm});
            skLineSegment(sketch, "E13.5.1.9", {"start": v(-106.28, -49.09) * mm, "end": v(-103.13, -49.09) * mm});
            skLineSegment(sketch, "E13.8.1.9", {"start": v(-103.13, -49.09) * mm, "end": v(-101.55, -51.82) * mm});
            skLineSegment(sketch, "E13.11.1.9", {"start": v(-101.55, -51.82) * mm, "end": v(-103.13, -54.55) * mm});
            skLineSegment(sketch, "E13.14.1.9", {"start": v(-103.13, -54.55) * mm, "end": v(-106.28, -54.55) * mm});
            skLineSegment(sketch, "E13.17.1.9", {"start": v(-106.28, -54.55) * mm, "end": v(-107.86, -51.82) * mm});
            skCircle(sketch, "E13.0.1.10", {"center": v(-104.7, -43.18) * mm, "radius": 2.73 * mm, "construction": true});
            skLineSegment(sketch, "E13.2.1.10", {"start": v(-107.86, -43.18) * mm, "end": v(-106.28, -40.45) * mm});
            skLineSegment(sketch, "E13.5.1.10", {"start": v(-106.28, -40.45) * mm, "end": v(-103.13, -40.45) * mm});
            skLineSegment(sketch, "E13.8.1.10", {"start": v(-103.13, -40.45) * mm, "end": v(-101.55, -43.18) * mm});
            skLineSegment(sketch, "E13.11.1.10", {"start": v(-101.55, -43.18) * mm, "end": v(-103.13, -45.91) * mm});
            skLineSegment(sketch, "E13.14.1.10", {"start": v(-103.13, -45.91) * mm, "end": v(-106.28, -45.91) * mm});
            skLineSegment(sketch, "E13.17.1.10", {"start": v(-106.28, -45.91) * mm, "end": v(-107.86, -43.18) * mm});
            skCircle(sketch, "E13.0.1.11", {"center": v(-104.7, -34.54) * mm, "radius": 2.73 * mm, "construction": true});
            skLineSegment(sketch, "E13.2.1.11", {"start": v(-107.86, -34.54) * mm, "end": v(-106.28, -31.81) * mm});
            skLineSegment(sketch, "E13.5.1.11", {"start": v(-106.28, -31.81) * mm, "end": v(-103.13, -31.81) * mm});
            skLineSegment(sketch, "E13.8.1.11", {"start": v(-103.13, -31.81) * mm, "end": v(-101.55, -34.54) * mm});
            skLineSegment(sketch, "E13.11.1.11", {"start": v(-101.55, -34.54) * mm, "end": v(-103.13, -37.27) * mm});
            skLineSegment(sketch, "E13.14.1.11", {"start": v(-103.13, -37.27) * mm, "end": v(-106.28, -37.27) * mm});
            skLineSegment(sketch, "E13.17.1.11", {"start": v(-106.28, -37.27) * mm, "end": v(-107.86, -34.54) * mm});
            skCircle(sketch, "E13.0.1.12", {"center": v(-104.7, -25.9) * mm, "radius": 2.73 * mm, "construction": true});
            skLineSegment(sketch, "E13.2.1.12", {"start": v(-107.86, -25.9) * mm, "end": v(-106.28, -23.18) * mm});
            skLineSegment(sketch, "E13.5.1.12", {"start": v(-106.28, -23.18) * mm, "end": v(-103.13, -23.18) * mm});
            skLineSegment(sketch, "E13.8.1.12", {"start": v(-103.13, -23.18) * mm, "end": v(-101.55, -25.9) * mm});
            skLineSegment(sketch, "E13.11.1.12", {"start": v(-101.55, -25.9) * mm, "end": v(-103.13, -28.64) * mm});
            skLineSegment(sketch, "E13.14.1.12", {"start": v(-103.13, -28.64) * mm, "end": v(-106.28, -28.64) * mm});
            skLineSegment(sketch, "E13.17.1.12", {"start": v(-106.28, -28.64) * mm, "end": v(-107.86, -25.9) * mm});
            skCircle(sketch, "E13.0.1.13", {"center": v(-104.7, -17.27) * mm, "radius": 2.73 * mm, "construction": true});
            skLineSegment(sketch, "E13.2.1.13", {"start": v(-107.86, -17.27) * mm, "end": v(-106.28, -14.54) * mm});
            skLineSegment(sketch, "E13.5.1.13", {"start": v(-106.28, -14.54) * mm, "end": v(-103.13, -14.54) * mm});
            skLineSegment(sketch, "E13.8.1.13", {"start": v(-103.13, -14.54) * mm, "end": v(-101.55, -17.27) * mm});
            skLineSegment(sketch, "E13.11.1.13", {"start": v(-101.55, -17.27) * mm, "end": v(-103.13, -20) * mm});
            skLineSegment(sketch, "E13.14.1.13", {"start": v(-103.13, -20) * mm, "end": v(-106.28, -20) * mm});
            skLineSegment(sketch, "E13.17.1.13", {"start": v(-106.28, -20) * mm, "end": v(-107.86, -17.27) * mm});
            skCircle(sketch, "E13.0.1.14", {"center": v(-104.7, -8.64) * mm, "radius": 2.73 * mm, "construction": true});
            skLineSegment(sketch, "E13.2.1.14", {"start": v(-107.86, -8.64) * mm, "end": v(-106.28, -5.9) * mm});
            skLineSegment(sketch, "E13.5.1.14", {"start": v(-106.28, -5.9) * mm, "end": v(-103.13, -5.9) * mm});
            skLineSegment(sketch, "E13.8.1.14", {"start": v(-103.13, -5.9) * mm, "end": v(-101.55, -8.64) * mm});
            skLineSegment(sketch, "E13.11.1.14", {"start": v(-101.55, -8.64) * mm, "end": v(-103.13, -11.37) * mm});
            skLineSegment(sketch, "E13.14.1.14", {"start": v(-103.13, -11.37) * mm, "end": v(-106.28, -11.37) * mm});
            skLineSegment(sketch, "E13.17.1.14", {"start": v(-106.28, -11.37) * mm, "end": v(-107.86, -8.64) * mm});
            skCircle(sketch, "E13.0.1.15", {"center": v(-104.7, 0) * mm, "radius": 2.73 * mm, "construction": true});
            skLineSegment(sketch, "E13.2.1.15", {"start": v(-107.86, 0) * mm, "end": v(-106.28, 2.73) * mm});
            skLineSegment(sketch, "E13.5.1.15", {"start": v(-106.28, 2.73) * mm, "end": v(-103.13, 2.73) * mm});
            skLineSegment(sketch, "E13.8.1.15", {"start": v(-103.13, 2.73) * mm, "end": v(-101.55, 0) * mm});
            skLineSegment(sketch, "E13.11.1.15", {"start": v(-101.55, 0) * mm, "end": v(-103.13, -2.73) * mm});
            skLineSegment(sketch, "E13.14.1.15", {"start": v(-103.13, -2.73) * mm, "end": v(-106.28, -2.73) * mm});
            skLineSegment(sketch, "E13.17.1.15", {"start": v(-106.28, -2.73) * mm, "end": v(-107.86, 0) * mm});
            skCircle(sketch, "E13.0.1.16", {"center": v(-104.7, 8.64) * mm, "radius": 2.73 * mm, "construction": true});
            skLineSegment(sketch, "E13.2.1.16", {"start": v(-107.86, 8.64) * mm, "end": v(-106.28, 11.37) * mm});
            skLineSegment(sketch, "E13.5.1.16", {"start": v(-106.28, 11.37) * mm, "end": v(-103.13, 11.37) * mm});
            skLineSegment(sketch, "E13.8.1.16", {"start": v(-103.13, 11.37) * mm, "end": v(-101.55, 8.64) * mm});
            skLineSegment(sketch, "E13.11.1.16", {"start": v(-101.55, 8.64) * mm, "end": v(-103.13, 5.9) * mm});
            skLineSegment(sketch, "E13.14.1.16", {"start": v(-103.13, 5.9) * mm, "end": v(-106.28, 5.9) * mm});
            skLineSegment(sketch, "E13.17.1.16", {"start": v(-106.28, 5.9) * mm, "end": v(-107.86, 8.64) * mm});
            skCircle(sketch, "E13.0.1.17", {"center": v(-104.7, 17.27) * mm, "radius": 2.73 * mm, "construction": true});
            skLineSegment(sketch, "E13.2.1.17", {"start": v(-107.86, 17.27) * mm, "end": v(-106.28, 20) * mm});
            skLineSegment(sketch, "E13.5.1.17", {"start": v(-106.28, 20) * mm, "end": v(-103.13, 20) * mm});
            skLineSegment(sketch, "E13.8.1.17", {"start": v(-103.13, 20) * mm, "end": v(-101.55, 17.27) * mm});
            skLineSegment(sketch, "E13.11.1.17", {"start": v(-101.55, 17.27) * mm, "end": v(-103.13, 14.54) * mm});
            skLineSegment(sketch, "E13.14.1.17", {"start": v(-103.13, 14.54) * mm, "end": v(-106.28, 14.54) * mm});
            skLineSegment(sketch, "E13.17.1.17", {"start": v(-106.28, 14.54) * mm, "end": v(-107.86, 17.27) * mm});
            skCircle(sketch, "E13.0.1.18", {"center": v(-104.7, 25.9) * mm, "radius": 2.73 * mm, "construction": true});
            skLineSegment(sketch, "E13.2.1.18", {"start": v(-107.86, 25.9) * mm, "end": v(-106.28, 28.64) * mm});
            skLineSegment(sketch, "E13.5.1.18", {"start": v(-106.28, 28.64) * mm, "end": v(-103.13, 28.64) * mm});
            skLineSegment(sketch, "E13.8.1.18", {"start": v(-103.13, 28.64) * mm, "end": v(-101.55, 25.9) * mm});
            skLineSegment(sketch, "E13.11.1.18", {"start": v(-101.55, 25.9) * mm, "end": v(-103.13, 23.18) * mm});
            skLineSegment(sketch, "E13.14.1.18", {"start": v(-103.13, 23.18) * mm, "end": v(-106.28, 23.18) * mm});
            skLineSegment(sketch, "E13.17.1.18", {"start": v(-106.28, 23.18) * mm, "end": v(-107.86, 25.9) * mm});
            skCircle(sketch, "E13.0.1.19", {"center": v(-104.7, 34.54) * mm, "radius": 2.73 * mm, "construction": true});
            skLineSegment(sketch, "E13.2.1.19", {"start": v(-107.86, 34.54) * mm, "end": v(-106.28, 37.27) * mm});
            skLineSegment(sketch, "E13.5.1.19", {"start": v(-106.28, 37.27) * mm, "end": v(-103.13, 37.27) * mm});
            skLineSegment(sketch, "E13.8.1.19", {"start": v(-103.13, 37.27) * mm, "end": v(-101.55, 34.54) * mm});
            skLineSegment(sketch, "E13.11.1.19", {"start": v(-101.55, 34.54) * mm, "end": v(-103.13, 31.81) * mm});
            skLineSegment(sketch, "E13.14.1.19", {"start": v(-103.13, 31.81) * mm, "end": v(-106.28, 31.81) * mm});
            skLineSegment(sketch, "E13.17.1.19", {"start": v(-106.28, 31.81) * mm, "end": v(-107.86, 34.54) * mm});
            skCircle(sketch, "E13.0.2.8", {"center": v(-89.75, -60.45) * mm, "radius": 2.73 * mm, "construction": true});
            skLineSegment(sketch, "E13.2.2.8", {"start": v(-92.9, -60.45) * mm, "end": v(-91.32, -57.72) * mm});
            skLineSegment(sketch, "E13.5.2.8", {"start": v(-91.32, -57.72) * mm, "end": v(-88.17, -57.72) * mm});
            skLineSegment(sketch, "E13.8.2.8", {"start": v(-88.17, -57.72) * mm, "end": v(-86.6, -60.45) * mm});
            skLineSegment(sketch, "E13.11.2.8", {"start": v(-86.6, -60.45) * mm, "end": v(-88.17, -63.18) * mm});
            skLineSegment(sketch, "E13.14.2.8", {"start": v(-88.17, -63.18) * mm, "end": v(-91.32, -63.18) * mm});
            skLineSegment(sketch, "E13.17.2.8", {"start": v(-91.32, -63.18) * mm, "end": v(-92.9, -60.45) * mm});
            skCircle(sketch, "E13.0.2.9", {"center": v(-89.75, -51.82) * mm, "radius": 2.73 * mm, "construction": true});
            skLineSegment(sketch, "E13.2.2.9", {"start": v(-92.9, -51.82) * mm, "end": v(-91.32, -49.09) * mm});
            skLineSegment(sketch, "E13.5.2.9", {"start": v(-91.32, -49.09) * mm, "end": v(-88.17, -49.09) * mm});
            skLineSegment(sketch, "E13.8.2.9", {"start": v(-88.17, -49.09) * mm, "end": v(-86.6, -51.82) * mm});
            skLineSegment(sketch, "E13.11.2.9", {"start": v(-86.6, -51.82) * mm, "end": v(-88.17, -54.55) * mm});
            skLineSegment(sketch, "E13.14.2.9", {"start": v(-88.17, -54.55) * mm, "end": v(-91.32, -54.55) * mm});
            skLineSegment(sketch, "E13.17.2.9", {"start": v(-91.32, -54.55) * mm, "end": v(-92.9, -51.82) * mm});
            skCircle(sketch, "E13.0.2.10", {"center": v(-89.75, -43.18) * mm, "radius": 2.73 * mm, "construction": true});
            skLineSegment(sketch, "E13.2.2.10", {"start": v(-92.9, -43.18) * mm, "end": v(-91.32, -40.45) * mm});
            skLineSegment(sketch, "E13.5.2.10", {"start": v(-91.32, -40.45) * mm, "end": v(-88.17, -40.45) * mm});
            skLineSegment(sketch, "E13.8.2.10", {"start": v(-88.17, -40.45) * mm, "end": v(-86.6, -43.18) * mm});
            skLineSegment(sketch, "E13.11.2.10", {"start": v(-86.6, -43.18) * mm, "end": v(-88.17, -45.91) * mm});
            skLineSegment(sketch, "E13.14.2.10", {"start": v(-88.17, -45.91) * mm, "end": v(-91.32, -45.91) * mm});
            skLineSegment(sketch, "E13.17.2.10", {"start": v(-91.32, -45.91) * mm, "end": v(-92.9, -43.18) * mm});
            skCircle(sketch, "E13.0.2.11", {"center": v(-89.75, -34.54) * mm, "radius": 2.73 * mm, "construction": true});
            skLineSegment(sketch, "E13.2.2.11", {"start": v(-92.9, -34.54) * mm, "end": v(-91.32, -31.81) * mm});
            skLineSegment(sketch, "E13.5.2.11", {"start": v(-91.32, -31.81) * mm, "end": v(-88.17, -31.81) * mm});
            skLineSegment(sketch, "E13.8.2.11", {"start": v(-88.17, -31.81) * mm, "end": v(-86.6, -34.54) * mm});
            skLineSegment(sketch, "E13.11.2.11", {"start": v(-86.6, -34.54) * mm, "end": v(-88.17, -37.27) * mm});
            skLineSegment(sketch, "E13.14.2.11", {"start": v(-88.17, -37.27) * mm, "end": v(-91.32, -37.27) * mm});
            skLineSegment(sketch, "E13.17.2.11", {"start": v(-91.32, -37.27) * mm, "end": v(-92.9, -34.54) * mm});
            skCircle(sketch, "E13.0.2.12", {"center": v(-89.75, -25.9) * mm, "radius": 2.73 * mm, "construction": true});
            skLineSegment(sketch, "E13.2.2.12", {"start": v(-92.9, -25.9) * mm, "end": v(-91.32, -23.18) * mm});
            skLineSegment(sketch, "E13.5.2.12", {"start": v(-91.32, -23.18) * mm, "end": v(-88.17, -23.18) * mm});
            skLineSegment(sketch, "E13.8.2.12", {"start": v(-88.17, -23.18) * mm, "end": v(-86.6, -25.9) * mm});
            skLineSegment(sketch, "E13.11.2.12", {"start": v(-86.6, -25.9) * mm, "end": v(-88.17, -28.64) * mm});
            skLineSegment(sketch, "E13.14.2.12", {"start": v(-88.17, -28.64) * mm, "end": v(-91.32, -28.64) * mm});
            skLineSegment(sketch, "E13.17.2.12", {"start": v(-91.32, -28.64) * mm, "end": v(-92.9, -25.9) * mm});
            skCircle(sketch, "E13.0.2.13", {"center": v(-89.75, -17.27) * mm, "radius": 2.73 * mm, "construction": true});
            skLineSegment(sketch, "E13.2.2.13", {"start": v(-92.9, -17.27) * mm, "end": v(-91.32, -14.54) * mm});
            skLineSegment(sketch, "E13.5.2.13", {"start": v(-91.32, -14.54) * mm, "end": v(-88.17, -14.54) * mm});
            skLineSegment(sketch, "E13.8.2.13", {"start": v(-88.17, -14.54) * mm, "end": v(-86.6, -17.27) * mm});
            skLineSegment(sketch, "E13.11.2.13", {"start": v(-86.6, -17.27) * mm, "end": v(-88.17, -20) * mm});
            skLineSegment(sketch, "E13.14.2.13", {"start": v(-88.17, -20) * mm, "end": v(-91.32, -20) * mm});
            skLineSegment(sketch, "E13.17.2.13", {"start": v(-91.32, -20) * mm, "end": v(-92.9, -17.27) * mm});
            skCircle(sketch, "E13.0.2.14", {"center": v(-89.75, -8.64) * mm, "radius": 2.73 * mm, "construction": true});
            skLineSegment(sketch, "E13.2.2.14", {"start": v(-92.9, -8.64) * mm, "end": v(-91.32, -5.9) * mm});
            skLineSegment(sketch, "E13.5.2.14", {"start": v(-91.32, -5.9) * mm, "end": v(-88.17, -5.9) * mm});
            skLineSegment(sketch, "E13.8.2.14", {"start": v(-88.17, -5.9) * mm, "end": v(-86.6, -8.64) * mm});
            skLineSegment(sketch, "E13.11.2.14", {"start": v(-86.6, -8.64) * mm, "end": v(-88.17, -11.37) * mm});
            skLineSegment(sketch, "E13.14.2.14", {"start": v(-88.17, -11.37) * mm, "end": v(-91.32, -11.37) * mm});
            skLineSegment(sketch, "E13.17.2.14", {"start": v(-91.32, -11.37) * mm, "end": v(-92.9, -8.64) * mm});
            skCircle(sketch, "E13.0.2.15", {"center": v(-89.75, 0) * mm, "radius": 2.73 * mm, "construction": true});
            skLineSegment(sketch, "E13.2.2.15", {"start": v(-92.9, 0) * mm, "end": v(-91.32, 2.73) * mm});
            skLineSegment(sketch, "E13.5.2.15", {"start": v(-91.32, 2.73) * mm, "end": v(-88.17, 2.73) * mm});
            skLineSegment(sketch, "E13.8.2.15", {"start": v(-88.17, 2.73) * mm, "end": v(-86.6, 0) * mm});
            skLineSegment(sketch, "E13.11.2.15", {"start": v(-86.6, 0) * mm, "end": v(-88.17, -2.73) * mm});
            skLineSegment(sketch, "E13.14.2.15", {"start": v(-88.17, -2.73) * mm, "end": v(-91.32, -2.73) * mm});
            skLineSegment(sketch, "E13.17.2.15", {"start": v(-91.32, -2.73) * mm, "end": v(-92.9, 0) * mm});
            skCircle(sketch, "E13.0.2.16", {"center": v(-89.75, 8.64) * mm, "radius": 2.73 * mm, "construction": true});
            skLineSegment(sketch, "E13.2.2.16", {"start": v(-92.9, 8.64) * mm, "end": v(-91.32, 11.37) * mm});
            skLineSegment(sketch, "E13.5.2.16", {"start": v(-91.32, 11.37) * mm, "end": v(-88.17, 11.37) * mm});
            skLineSegment(sketch, "E13.8.2.16", {"start": v(-88.17, 11.37) * mm, "end": v(-86.6, 8.64) * mm});
            skLineSegment(sketch, "E13.11.2.16", {"start": v(-86.6, 8.64) * mm, "end": v(-88.17, 5.9) * mm});
            skLineSegment(sketch, "E13.14.2.16", {"start": v(-88.17, 5.9) * mm, "end": v(-91.32, 5.9) * mm});
            skLineSegment(sketch, "E13.17.2.16", {"start": v(-91.32, 5.9) * mm, "end": v(-92.9, 8.64) * mm});
            skCircle(sketch, "E13.0.2.17", {"center": v(-89.75, 17.27) * mm, "radius": 2.73 * mm, "construction": true});
            skLineSegment(sketch, "E13.2.2.17", {"start": v(-92.9, 17.27) * mm, "end": v(-91.32, 20) * mm});
            skLineSegment(sketch, "E13.5.2.17", {"start": v(-91.32, 20) * mm, "end": v(-88.17, 20) * mm});
            skLineSegment(sketch, "E13.8.2.17", {"start": v(-88.17, 20) * mm, "end": v(-86.6, 17.27) * mm});
            skLineSegment(sketch, "E13.11.2.17", {"start": v(-86.6, 17.27) * mm, "end": v(-88.17, 14.54) * mm});
            skLineSegment(sketch, "E13.14.2.17", {"start": v(-88.17, 14.54) * mm, "end": v(-91.32, 14.54) * mm});
            skLineSegment(sketch, "E13.17.2.17", {"start": v(-91.32, 14.54) * mm, "end": v(-92.9, 17.27) * mm});
            skCircle(sketch, "E13.0.2.18", {"center": v(-89.75, 25.9) * mm, "radius": 2.73 * mm, "construction": true});
            skLineSegment(sketch, "E13.2.2.18", {"start": v(-92.9, 25.9) * mm, "end": v(-91.32, 28.64) * mm});
            skLineSegment(sketch, "E13.5.2.18", {"start": v(-91.32, 28.64) * mm, "end": v(-88.17, 28.64) * mm});
            skLineSegment(sketch, "E13.8.2.18", {"start": v(-88.17, 28.64) * mm, "end": v(-86.6, 25.9) * mm});
            skLineSegment(sketch, "E13.11.2.18", {"start": v(-86.6, 25.9) * mm, "end": v(-88.17, 23.18) * mm});
            skLineSegment(sketch, "E13.14.2.18", {"start": v(-88.17, 23.18) * mm, "end": v(-91.32, 23.18) * mm});
            skLineSegment(sketch, "E13.17.2.18", {"start": v(-91.32, 23.18) * mm, "end": v(-92.9, 25.9) * mm});
            skCircle(sketch, "E13.0.2.19", {"center": v(-89.75, 34.54) * mm, "radius": 2.73 * mm, "construction": true});
            skLineSegment(sketch, "E13.2.2.19", {"start": v(-92.9, 34.54) * mm, "end": v(-91.32, 37.27) * mm});
            skLineSegment(sketch, "E13.5.2.19", {"start": v(-91.32, 37.27) * mm, "end": v(-88.17, 37.27) * mm});
            skLineSegment(sketch, "E13.8.2.19", {"start": v(-88.17, 37.27) * mm, "end": v(-86.6, 34.54) * mm});
            skLineSegment(sketch, "E13.11.2.19", {"start": v(-86.6, 34.54) * mm, "end": v(-88.17, 31.81) * mm});
            skLineSegment(sketch, "E13.14.2.19", {"start": v(-88.17, 31.81) * mm, "end": v(-91.32, 31.81) * mm});
            skLineSegment(sketch, "E13.17.2.19", {"start": v(-91.32, 31.81) * mm, "end": v(-92.9, 34.54) * mm});
            skLineSegment(sketch, "E14.0.6.0", {"start": v(-38.97, -131.13) * mm, "end": v(-35.82, -131.13) * mm});
            skLineSegment(sketch, "E14.3.6.0", {"start": v(-35.82, -131.13) * mm, "end": v(-34.24, -133.86) * mm});
            skLineSegment(sketch, "E14.6.6.0", {"start": v(-34.24, -133.86) * mm, "end": v(-35.82, -136.59) * mm});
            skCircle(sketch, "E14.9.6.0", {"center": v(-37.4, -133.86) * mm, "radius": 2.73 * mm, "construction": true});
            skLineSegment(sketch, "E14.11.6.0", {"start": v(-35.82, -136.59) * mm, "end": v(-38.97, -136.59) * mm});
            skLineSegment(sketch, "E14.14.6.0", {"start": v(-38.97, -136.59) * mm, "end": v(-40.55, -133.86) * mm});
            skLineSegment(sketch, "E14.17.6.0", {"start": v(-40.55, -133.86) * mm, "end": v(-38.97, -131.13) * mm});
            skLineSegment(sketch, "E14.0.6.1", {"start": v(-38.97, -122.5) * mm, "end": v(-35.82, -122.5) * mm});
            skLineSegment(sketch, "E14.3.6.1", {"start": v(-35.82, -122.5) * mm, "end": v(-34.24, -125.22) * mm});
            skLineSegment(sketch, "E14.6.6.1", {"start": v(-34.24, -125.22) * mm, "end": v(-35.82, -127.95) * mm});
            skCircle(sketch, "E14.9.6.1", {"center": v(-37.4, -125.22) * mm, "radius": 2.73 * mm, "construction": true});
            skLineSegment(sketch, "E14.11.6.1", {"start": v(-35.82, -127.95) * mm, "end": v(-38.97, -127.95) * mm});
            skLineSegment(sketch, "E14.14.6.1", {"start": v(-38.97, -127.95) * mm, "end": v(-40.55, -125.22) * mm});
            skLineSegment(sketch, "E14.17.6.1", {"start": v(-40.55, -125.22) * mm, "end": v(-38.97, -122.5) * mm});
            skLineSegment(sketch, "E14.0.6.2", {"start": v(-38.97, -113.86) * mm, "end": v(-35.82, -113.86) * mm});
            skLineSegment(sketch, "E14.3.6.2", {"start": v(-35.82, -113.86) * mm, "end": v(-34.24, -116.59) * mm});
            skLineSegment(sketch, "E14.6.6.2", {"start": v(-34.24, -116.59) * mm, "end": v(-35.82, -119.32) * mm});
            skCircle(sketch, "E14.9.6.2", {"center": v(-37.4, -116.59) * mm, "radius": 2.73 * mm, "construction": true});
            skLineSegment(sketch, "E14.11.6.2", {"start": v(-35.82, -119.32) * mm, "end": v(-38.97, -119.32) * mm});
            skLineSegment(sketch, "E14.14.6.2", {"start": v(-38.97, -119.32) * mm, "end": v(-40.55, -116.59) * mm});
            skLineSegment(sketch, "E14.17.6.2", {"start": v(-40.55, -116.59) * mm, "end": v(-38.97, -113.86) * mm});
            skLineSegment(sketch, "E14.0.6.3", {"start": v(-38.97, -105.22) * mm, "end": v(-35.82, -105.22) * mm});
            skLineSegment(sketch, "E14.3.6.3", {"start": v(-35.82, -105.22) * mm, "end": v(-34.24, -107.95) * mm});
            skLineSegment(sketch, "E14.6.6.3", {"start": v(-34.24, -107.95) * mm, "end": v(-35.82, -110.68) * mm});
            skCircle(sketch, "E14.9.6.3", {"center": v(-37.4, -107.95) * mm, "radius": 2.73 * mm, "construction": true});
            skLineSegment(sketch, "E14.11.6.3", {"start": v(-35.82, -110.68) * mm, "end": v(-38.97, -110.68) * mm});
            skLineSegment(sketch, "E14.14.6.3", {"start": v(-38.97, -110.68) * mm, "end": v(-40.55, -107.95) * mm});
            skLineSegment(sketch, "E14.17.6.3", {"start": v(-40.55, -107.95) * mm, "end": v(-38.97, -105.22) * mm});
            skLineSegment(sketch, "E14.0.6.4", {"start": v(-38.97, -96.58) * mm, "end": v(-35.82, -96.58) * mm});
            skLineSegment(sketch, "E14.3.6.4", {"start": v(-35.82, -96.58) * mm, "end": v(-34.24, -99.31) * mm});
            skLineSegment(sketch, "E14.6.6.4", {"start": v(-34.24, -99.31) * mm, "end": v(-35.82, -102.04) * mm});
            skCircle(sketch, "E14.9.6.4", {"center": v(-37.4, -99.31) * mm, "radius": 2.73 * mm, "construction": true});
            skLineSegment(sketch, "E14.11.6.4", {"start": v(-35.82, -102.04) * mm, "end": v(-38.97, -102.04) * mm});
            skLineSegment(sketch, "E14.14.6.4", {"start": v(-38.97, -102.04) * mm, "end": v(-40.55, -99.31) * mm});
            skLineSegment(sketch, "E14.17.6.4", {"start": v(-40.55, -99.31) * mm, "end": v(-38.97, -96.58) * mm});
            skLineSegment(sketch, "E14.0.6.5", {"start": v(-38.97, -87.95) * mm, "end": v(-35.82, -87.95) * mm});
            skLineSegment(sketch, "E14.3.6.5", {"start": v(-35.82, -87.95) * mm, "end": v(-34.24, -90.68) * mm});
            skLineSegment(sketch, "E14.6.6.5", {"start": v(-34.24, -90.68) * mm, "end": v(-35.82, -93.4) * mm});
            skCircle(sketch, "E14.9.6.5", {"center": v(-37.4, -90.68) * mm, "radius": 2.73 * mm, "construction": true});
            skLineSegment(sketch, "E14.11.6.5", {"start": v(-35.82, -93.4) * mm, "end": v(-38.97, -93.4) * mm});
            skLineSegment(sketch, "E14.14.6.5", {"start": v(-38.97, -93.4) * mm, "end": v(-40.55, -90.68) * mm});
            skLineSegment(sketch, "E14.17.6.5", {"start": v(-40.55, -90.68) * mm, "end": v(-38.97, -87.95) * mm});
            skLineSegment(sketch, "E14.0.6.6", {"start": v(-38.97, -79.31) * mm, "end": v(-35.82, -79.31) * mm});
            skLineSegment(sketch, "E14.3.6.6", {"start": v(-35.82, -79.31) * mm, "end": v(-34.24, -82.04) * mm});
            skLineSegment(sketch, "E14.6.6.6", {"start": v(-34.24, -82.04) * mm, "end": v(-35.82, -84.77) * mm});
            skCircle(sketch, "E14.9.6.6", {"center": v(-37.4, -82.04) * mm, "radius": 2.73 * mm, "construction": true});
            skLineSegment(sketch, "E14.11.6.6", {"start": v(-35.82, -84.77) * mm, "end": v(-38.97, -84.77) * mm});
            skLineSegment(sketch, "E14.14.6.6", {"start": v(-38.97, -84.77) * mm, "end": v(-40.55, -82.04) * mm});
            skLineSegment(sketch, "E14.17.6.6", {"start": v(-40.55, -82.04) * mm, "end": v(-38.97, -79.31) * mm});
            skLineSegment(sketch, "E14.0.6.7", {"start": v(-38.97, -70.68) * mm, "end": v(-35.82, -70.68) * mm});
            skLineSegment(sketch, "E14.3.6.7", {"start": v(-35.82, -70.68) * mm, "end": v(-34.24, -73.4) * mm});
            skLineSegment(sketch, "E14.6.6.7", {"start": v(-34.24, -73.4) * mm, "end": v(-35.82, -76.14) * mm});
            skCircle(sketch, "E14.9.6.7", {"center": v(-37.4, -73.4) * mm, "radius": 2.73 * mm, "construction": true});
            skLineSegment(sketch, "E14.11.6.7", {"start": v(-35.82, -76.14) * mm, "end": v(-38.97, -76.14) * mm});
            skLineSegment(sketch, "E14.14.6.7", {"start": v(-38.97, -76.14) * mm, "end": v(-40.55, -73.4) * mm});
            skLineSegment(sketch, "E14.17.6.7", {"start": v(-40.55, -73.4) * mm, "end": v(-38.97, -70.68) * mm});
            skLineSegment(sketch, "E14.0.6.8", {"start": v(-38.97, -62.04) * mm, "end": v(-35.82, -62.04) * mm});
            skLineSegment(sketch, "E14.3.6.8", {"start": v(-35.82, -62.04) * mm, "end": v(-34.24, -64.77) * mm});
            skLineSegment(sketch, "E14.6.6.8", {"start": v(-34.24, -64.77) * mm, "end": v(-35.82, -67.5) * mm});
            skCircle(sketch, "E14.9.6.8", {"center": v(-37.4, -64.77) * mm, "radius": 2.73 * mm, "construction": true});
            skLineSegment(sketch, "E14.11.6.8", {"start": v(-35.82, -67.5) * mm, "end": v(-38.97, -67.5) * mm});
            skLineSegment(sketch, "E14.14.6.8", {"start": v(-38.97, -67.5) * mm, "end": v(-40.55, -64.77) * mm});
            skLineSegment(sketch, "E14.17.6.8", {"start": v(-40.55, -64.77) * mm, "end": v(-38.97, -62.04) * mm});
            skLineSegment(sketch, "E14.0.6.9", {"start": v(-38.97, -53.4) * mm, "end": v(-35.82, -53.4) * mm});
            skLineSegment(sketch, "E14.3.6.9", {"start": v(-35.82, -53.4) * mm, "end": v(-34.24, -56.13) * mm});
            skLineSegment(sketch, "E14.6.6.9", {"start": v(-34.24, -56.13) * mm, "end": v(-35.82, -58.86) * mm});
            skCircle(sketch, "E14.9.6.9", {"center": v(-37.4, -56.13) * mm, "radius": 2.73 * mm, "construction": true});
            skLineSegment(sketch, "E14.11.6.9", {"start": v(-35.82, -58.86) * mm, "end": v(-38.97, -58.86) * mm});
            skLineSegment(sketch, "E14.14.6.9", {"start": v(-38.97, -58.86) * mm, "end": v(-40.55, -56.13) * mm});
            skLineSegment(sketch, "E14.17.6.9", {"start": v(-40.55, -56.13) * mm, "end": v(-38.97, -53.4) * mm});
            skLineSegment(sketch, "E14.0.6.10", {"start": v(-38.97, -44.77) * mm, "end": v(-35.82, -44.77) * mm});
            skLineSegment(sketch, "E14.3.6.10", {"start": v(-35.82, -44.77) * mm, "end": v(-34.24, -47.5) * mm});
            skLineSegment(sketch, "E14.6.6.10", {"start": v(-34.24, -47.5) * mm, "end": v(-35.82, -50.23) * mm});
            skCircle(sketch, "E14.9.6.10", {"center": v(-37.4, -47.5) * mm, "radius": 2.73 * mm, "construction": true});
            skLineSegment(sketch, "E14.11.6.10", {"start": v(-35.82, -50.23) * mm, "end": v(-38.97, -50.23) * mm});
            skLineSegment(sketch, "E14.14.6.10", {"start": v(-38.97, -50.23) * mm, "end": v(-40.55, -47.5) * mm});
            skLineSegment(sketch, "E14.17.6.10", {"start": v(-40.55, -47.5) * mm, "end": v(-38.97, -44.77) * mm});
            skLineSegment(sketch, "E14.0.6.11", {"start": v(-38.97, -36.13) * mm, "end": v(-35.82, -36.13) * mm});
            skLineSegment(sketch, "E14.3.6.11", {"start": v(-35.82, -36.13) * mm, "end": v(-34.24, -38.86) * mm});
            skLineSegment(sketch, "E14.6.6.11", {"start": v(-34.24, -38.86) * mm, "end": v(-35.82, -41.6) * mm});
            skCircle(sketch, "E14.9.6.11", {"center": v(-37.4, -38.86) * mm, "radius": 2.73 * mm, "construction": true});
            skLineSegment(sketch, "E14.11.6.11", {"start": v(-35.82, -41.6) * mm, "end": v(-38.97, -41.6) * mm});
            skLineSegment(sketch, "E14.14.6.11", {"start": v(-38.97, -41.6) * mm, "end": v(-40.55, -38.86) * mm});
            skLineSegment(sketch, "E14.17.6.11", {"start": v(-40.55, -38.86) * mm, "end": v(-38.97, -36.13) * mm});
            skLineSegment(sketch, "E14.0.6.12", {"start": v(-38.97, -27.5) * mm, "end": v(-35.82, -27.5) * mm});
            skLineSegment(sketch, "E14.3.6.12", {"start": v(-35.82, -27.5) * mm, "end": v(-34.24, -30.23) * mm});
            skLineSegment(sketch, "E14.6.6.12", {"start": v(-34.24, -30.23) * mm, "end": v(-35.82, -32.96) * mm});
            skCircle(sketch, "E14.9.6.12", {"center": v(-37.4, -30.23) * mm, "radius": 2.73 * mm, "construction": true});
            skLineSegment(sketch, "E14.11.6.12", {"start": v(-35.82, -32.96) * mm, "end": v(-38.97, -32.96) * mm});
            skLineSegment(sketch, "E14.14.6.12", {"start": v(-38.97, -32.96) * mm, "end": v(-40.55, -30.23) * mm});
            skLineSegment(sketch, "E14.17.6.12", {"start": v(-40.55, -30.23) * mm, "end": v(-38.97, -27.5) * mm});
            skLineSegment(sketch, "E14.0.6.13", {"start": v(-38.97, -18.86) * mm, "end": v(-35.82, -18.86) * mm});
            skLineSegment(sketch, "E14.3.6.13", {"start": v(-35.82, -18.86) * mm, "end": v(-34.24, -21.6) * mm});
            skLineSegment(sketch, "E14.6.6.13", {"start": v(-34.24, -21.6) * mm, "end": v(-35.82, -24.32) * mm});
            skCircle(sketch, "E14.9.6.13", {"center": v(-37.4, -21.6) * mm, "radius": 2.73 * mm, "construction": true});
            skLineSegment(sketch, "E14.11.6.13", {"start": v(-35.82, -24.32) * mm, "end": v(-38.97, -24.32) * mm});
            skLineSegment(sketch, "E14.14.6.13", {"start": v(-38.97, -24.32) * mm, "end": v(-40.55, -21.6) * mm});
            skLineSegment(sketch, "E14.17.6.13", {"start": v(-40.55, -21.59) * mm, "end": v(-38.97, -18.86) * mm});
            skLineSegment(sketch, "E14.0.6.14", {"start": v(-38.97, -10.22) * mm, "end": v(-35.82, -10.22) * mm});
            skLineSegment(sketch, "E14.3.6.14", {"start": v(-35.82, -10.22) * mm, "end": v(-34.24, -12.95) * mm});
            skLineSegment(sketch, "E14.6.6.14", {"start": v(-34.24, -12.95) * mm, "end": v(-35.82, -15.68) * mm});
            skCircle(sketch, "E14.9.6.14", {"center": v(-37.4, -12.95) * mm, "radius": 2.73 * mm, "construction": true});
            skLineSegment(sketch, "E14.11.6.14", {"start": v(-35.82, -15.68) * mm, "end": v(-38.97, -15.68) * mm});
            skLineSegment(sketch, "E14.14.6.14", {"start": v(-38.97, -15.68) * mm, "end": v(-40.55, -12.95) * mm});
            skLineSegment(sketch, "E14.17.6.14", {"start": v(-40.55, -12.95) * mm, "end": v(-38.97, -10.22) * mm});
            skLineSegment(sketch, "E14.0.6.15", {"start": v(-38.97, -1.59) * mm, "end": v(-35.82, -1.59) * mm});
            skLineSegment(sketch, "E14.3.6.15", {"start": v(-35.82, -1.59) * mm, "end": v(-34.24, -4.32) * mm});
            skLineSegment(sketch, "E14.6.6.15", {"start": v(-34.24, -4.32) * mm, "end": v(-35.82, -7.05) * mm});
            skCircle(sketch, "E14.9.6.15", {"center": v(-37.4, -4.32) * mm, "radius": 2.73 * mm, "construction": true});
            skLineSegment(sketch, "E14.11.6.15", {"start": v(-35.82, -7.05) * mm, "end": v(-38.97, -7.05) * mm});
            skLineSegment(sketch, "E14.14.6.15", {"start": v(-38.97, -7.05) * mm, "end": v(-40.55, -4.32) * mm});
            skLineSegment(sketch, "E14.17.6.15", {"start": v(-40.55, -4.32) * mm, "end": v(-38.97, -1.59) * mm});
            skLineSegment(sketch, "E14.0.6.16", {"start": v(-38.97, 7.05) * mm, "end": v(-35.82, 7.05) * mm});
            skLineSegment(sketch, "E14.3.6.16", {"start": v(-35.82, 7.05) * mm, "end": v(-34.24, 4.32) * mm});
            skLineSegment(sketch, "E14.6.6.16", {"start": v(-34.24, 4.32) * mm, "end": v(-35.82, 1.59) * mm});
            skCircle(sketch, "E14.9.6.16", {"center": v(-37.4, 4.32) * mm, "radius": 2.73 * mm, "construction": true});
            skLineSegment(sketch, "E14.11.6.16", {"start": v(-35.82, 1.59) * mm, "end": v(-38.97, 1.59) * mm});
            skLineSegment(sketch, "E14.14.6.16", {"start": v(-38.97, 1.59) * mm, "end": v(-40.55, 4.32) * mm});
            skLineSegment(sketch, "E14.17.6.16", {"start": v(-40.55, 4.32) * mm, "end": v(-38.97, 7.05) * mm});
            skLineSegment(sketch, "E14.0.6.17", {"start": v(-38.97, 15.68) * mm, "end": v(-35.82, 15.68) * mm});
            skLineSegment(sketch, "E14.3.6.17", {"start": v(-35.82, 15.68) * mm, "end": v(-34.24, 12.95) * mm});
            skLineSegment(sketch, "E14.6.6.17", {"start": v(-34.24, 12.95) * mm, "end": v(-35.82, 10.22) * mm});
            skCircle(sketch, "E14.9.6.17", {"center": v(-37.4, 12.95) * mm, "radius": 2.73 * mm, "construction": true});
            skLineSegment(sketch, "E14.11.6.17", {"start": v(-35.82, 10.22) * mm, "end": v(-38.97, 10.22) * mm});
            skLineSegment(sketch, "E14.14.6.17", {"start": v(-38.97, 10.22) * mm, "end": v(-40.55, 12.95) * mm});
            skLineSegment(sketch, "E14.17.6.17", {"start": v(-40.55, 12.95) * mm, "end": v(-38.97, 15.68) * mm});
            skLineSegment(sketch, "E14.0.6.18", {"start": v(-38.97, 24.32) * mm, "end": v(-35.82, 24.32) * mm});
            skLineSegment(sketch, "E14.3.6.18", {"start": v(-35.82, 24.32) * mm, "end": v(-34.24, 21.59) * mm});
            skLineSegment(sketch, "E14.6.6.18", {"start": v(-34.24, 21.59) * mm, "end": v(-35.82, 18.86) * mm});
            skCircle(sketch, "E14.9.6.18", {"center": v(-37.4, 21.59) * mm, "radius": 2.73 * mm, "construction": true});
            skLineSegment(sketch, "E14.11.6.18", {"start": v(-35.82, 18.86) * mm, "end": v(-38.97, 18.86) * mm});
            skLineSegment(sketch, "E14.14.6.18", {"start": v(-38.97, 18.86) * mm, "end": v(-40.55, 21.59) * mm});
            skLineSegment(sketch, "E14.17.6.18", {"start": v(-40.55, 21.6) * mm, "end": v(-38.97, 24.32) * mm});
            skLineSegment(sketch, "E14.0.6.19", {"start": v(-38.97, 32.96) * mm, "end": v(-35.82, 32.96) * mm});
            skLineSegment(sketch, "E14.3.6.19", {"start": v(-35.82, 32.96) * mm, "end": v(-34.24, 30.23) * mm});
            skLineSegment(sketch, "E14.6.6.19", {"start": v(-34.24, 30.23) * mm, "end": v(-35.82, 27.5) * mm});
            skCircle(sketch, "E14.9.6.19", {"center": v(-37.4, 30.23) * mm, "radius": 2.73 * mm, "construction": true});
            skLineSegment(sketch, "E14.11.6.19", {"start": v(-35.82, 27.5) * mm, "end": v(-38.97, 27.5) * mm});
            skLineSegment(sketch, "E14.14.6.19", {"start": v(-38.97, 27.5) * mm, "end": v(-40.55, 30.23) * mm});
            skLineSegment(sketch, "E14.17.6.19", {"start": v(-40.55, 30.23) * mm, "end": v(-38.97, 32.96) * mm});
            skLineSegment(sketch, "E14.0.7.0", {"start": v(-24.01, -131.13) * mm, "end": v(-20.86, -131.13) * mm});
            skLineSegment(sketch, "E14.3.7.0", {"start": v(-20.86, -131.13) * mm, "end": v(-19.28, -133.86) * mm});
            skLineSegment(sketch, "E14.6.7.0", {"start": v(-19.28, -133.86) * mm, "end": v(-20.86, -136.59) * mm});
            skCircle(sketch, "E14.9.7.0", {"center": v(-22.44, -133.86) * mm, "radius": 2.73 * mm, "construction": true});
            skLineSegment(sketch, "E14.11.7.0", {"start": v(-20.86, -136.59) * mm, "end": v(-24.01, -136.59) * mm});
            skLineSegment(sketch, "E14.14.7.0", {"start": v(-24.01, -136.59) * mm, "end": v(-25.59, -133.86) * mm});
            skLineSegment(sketch, "E14.17.7.0", {"start": v(-25.59, -133.86) * mm, "end": v(-24.01, -131.13) * mm});
            skLineSegment(sketch, "E14.0.7.1", {"start": v(-24.01, -122.5) * mm, "end": v(-20.86, -122.5) * mm});
            skLineSegment(sketch, "E14.3.7.1", {"start": v(-20.86, -122.5) * mm, "end": v(-19.28, -125.22) * mm});
            skLineSegment(sketch, "E14.6.7.1", {"start": v(-19.28, -125.22) * mm, "end": v(-20.86, -127.95) * mm});
            skCircle(sketch, "E14.9.7.1", {"center": v(-22.44, -125.22) * mm, "radius": 2.73 * mm, "construction": true});
            skLineSegment(sketch, "E14.11.7.1", {"start": v(-20.86, -127.95) * mm, "end": v(-24.01, -127.95) * mm});
            skLineSegment(sketch, "E14.14.7.1", {"start": v(-24.01, -127.95) * mm, "end": v(-25.59, -125.22) * mm});
            skLineSegment(sketch, "E14.17.7.1", {"start": v(-25.59, -125.22) * mm, "end": v(-24.01, -122.5) * mm});
            skLineSegment(sketch, "E14.0.7.2", {"start": v(-24.01, -113.86) * mm, "end": v(-20.86, -113.86) * mm});
            skLineSegment(sketch, "E14.3.7.2", {"start": v(-20.86, -113.86) * mm, "end": v(-19.28, -116.59) * mm});
            skLineSegment(sketch, "E14.6.7.2", {"start": v(-19.28, -116.59) * mm, "end": v(-20.86, -119.32) * mm});
            skCircle(sketch, "E14.9.7.2", {"center": v(-22.44, -116.59) * mm, "radius": 2.73 * mm, "construction": true});
            skLineSegment(sketch, "E14.11.7.2", {"start": v(-20.86, -119.32) * mm, "end": v(-24.01, -119.32) * mm});
            skLineSegment(sketch, "E14.14.7.2", {"start": v(-24.01, -119.32) * mm, "end": v(-25.59, -116.59) * mm});
            skLineSegment(sketch, "E14.17.7.2", {"start": v(-25.59, -116.59) * mm, "end": v(-24.01, -113.86) * mm});
            skLineSegment(sketch, "E14.0.7.3", {"start": v(-24.01, -105.22) * mm, "end": v(-20.86, -105.22) * mm});
            skLineSegment(sketch, "E14.3.7.3", {"start": v(-20.86, -105.22) * mm, "end": v(-19.28, -107.95) * mm});
            skLineSegment(sketch, "E14.6.7.3", {"start": v(-19.28, -107.95) * mm, "end": v(-20.86, -110.68) * mm});
            skCircle(sketch, "E14.9.7.3", {"center": v(-22.44, -107.95) * mm, "radius": 2.73 * mm, "construction": true});
            skLineSegment(sketch, "E14.11.7.3", {"start": v(-20.86, -110.68) * mm, "end": v(-24.01, -110.68) * mm});
            skLineSegment(sketch, "E14.14.7.3", {"start": v(-24.01, -110.68) * mm, "end": v(-25.59, -107.95) * mm});
            skLineSegment(sketch, "E14.17.7.3", {"start": v(-25.59, -107.95) * mm, "end": v(-24.01, -105.22) * mm});
            skLineSegment(sketch, "E14.0.7.4", {"start": v(-24.01, -96.58) * mm, "end": v(-20.86, -96.58) * mm});
            skLineSegment(sketch, "E14.3.7.4", {"start": v(-20.86, -96.58) * mm, "end": v(-19.28, -99.31) * mm});
            skLineSegment(sketch, "E14.6.7.4", {"start": v(-19.28, -99.31) * mm, "end": v(-20.86, -102.04) * mm});
            skCircle(sketch, "E14.9.7.4", {"center": v(-22.44, -99.31) * mm, "radius": 2.73 * mm, "construction": true});
            skLineSegment(sketch, "E14.11.7.4", {"start": v(-20.86, -102.04) * mm, "end": v(-24.01, -102.04) * mm});
            skLineSegment(sketch, "E14.14.7.4", {"start": v(-24.01, -102.04) * mm, "end": v(-25.59, -99.31) * mm});
            skLineSegment(sketch, "E14.17.7.4", {"start": v(-25.59, -99.31) * mm, "end": v(-24.01, -96.58) * mm});
            skLineSegment(sketch, "E14.0.7.5", {"start": v(-24.01, -87.95) * mm, "end": v(-20.86, -87.95) * mm});
            skLineSegment(sketch, "E14.3.7.5", {"start": v(-20.86, -87.95) * mm, "end": v(-19.28, -90.68) * mm});
            skLineSegment(sketch, "E14.6.7.5", {"start": v(-19.28, -90.68) * mm, "end": v(-20.86, -93.4) * mm});
            skCircle(sketch, "E14.9.7.5", {"center": v(-22.44, -90.68) * mm, "radius": 2.73 * mm, "construction": true});
            skLineSegment(sketch, "E14.11.7.5", {"start": v(-20.86, -93.4) * mm, "end": v(-24.01, -93.4) * mm});
            skLineSegment(sketch, "E14.14.7.5", {"start": v(-24.01, -93.4) * mm, "end": v(-25.59, -90.68) * mm});
            skLineSegment(sketch, "E14.17.7.5", {"start": v(-25.59, -90.68) * mm, "end": v(-24.01, -87.95) * mm});
            skLineSegment(sketch, "E14.0.7.6", {"start": v(-24.01, -79.31) * mm, "end": v(-20.86, -79.31) * mm});
            skLineSegment(sketch, "E14.3.7.6", {"start": v(-20.86, -79.31) * mm, "end": v(-19.28, -82.04) * mm});
            skLineSegment(sketch, "E14.6.7.6", {"start": v(-19.28, -82.04) * mm, "end": v(-20.86, -84.77) * mm});
            skCircle(sketch, "E14.9.7.6", {"center": v(-22.44, -82.04) * mm, "radius": 2.73 * mm, "construction": true});
            skLineSegment(sketch, "E14.11.7.6", {"start": v(-20.86, -84.77) * mm, "end": v(-24.01, -84.77) * mm});
            skLineSegment(sketch, "E14.14.7.6", {"start": v(-24.01, -84.77) * mm, "end": v(-25.59, -82.04) * mm});
            skLineSegment(sketch, "E14.17.7.6", {"start": v(-25.59, -82.04) * mm, "end": v(-24.01, -79.31) * mm});
            skLineSegment(sketch, "E14.0.7.7", {"start": v(-24.01, -70.68) * mm, "end": v(-20.86, -70.68) * mm});
            skLineSegment(sketch, "E14.3.7.7", {"start": v(-20.86, -70.68) * mm, "end": v(-19.28, -73.4) * mm});
            skLineSegment(sketch, "E14.6.7.7", {"start": v(-19.28, -73.4) * mm, "end": v(-20.86, -76.14) * mm});
            skCircle(sketch, "E14.9.7.7", {"center": v(-22.44, -73.4) * mm, "radius": 2.73 * mm, "construction": true});
            skLineSegment(sketch, "E14.11.7.7", {"start": v(-20.86, -76.14) * mm, "end": v(-24.01, -76.14) * mm});
            skLineSegment(sketch, "E14.14.7.7", {"start": v(-24.01, -76.14) * mm, "end": v(-25.59, -73.4) * mm});
            skLineSegment(sketch, "E14.17.7.7", {"start": v(-25.59, -73.4) * mm, "end": v(-24.01, -70.68) * mm});
            skLineSegment(sketch, "E14.0.7.8", {"start": v(-24.01, -62.04) * mm, "end": v(-20.86, -62.04) * mm});
            skLineSegment(sketch, "E14.3.7.8", {"start": v(-20.86, -62.04) * mm, "end": v(-19.28, -64.77) * mm});
            skLineSegment(sketch, "E14.6.7.8", {"start": v(-19.28, -64.77) * mm, "end": v(-20.86, -67.5) * mm});
            skCircle(sketch, "E14.9.7.8", {"center": v(-22.44, -64.77) * mm, "radius": 2.73 * mm, "construction": true});
            skLineSegment(sketch, "E14.11.7.8", {"start": v(-20.86, -67.5) * mm, "end": v(-24.01, -67.5) * mm});
            skLineSegment(sketch, "E14.14.7.8", {"start": v(-24.01, -67.5) * mm, "end": v(-25.59, -64.77) * mm});
            skLineSegment(sketch, "E14.17.7.8", {"start": v(-25.59, -64.77) * mm, "end": v(-24.01, -62.04) * mm});
            skLineSegment(sketch, "E14.0.7.9", {"start": v(-24.01, -53.4) * mm, "end": v(-20.86, -53.4) * mm});
            skLineSegment(sketch, "E14.3.7.9", {"start": v(-20.86, -53.4) * mm, "end": v(-19.28, -56.13) * mm});
            skLineSegment(sketch, "E14.6.7.9", {"start": v(-19.28, -56.13) * mm, "end": v(-20.86, -58.86) * mm});
            skCircle(sketch, "E14.9.7.9", {"center": v(-22.44, -56.13) * mm, "radius": 2.73 * mm, "construction": true});
            skLineSegment(sketch, "E14.11.7.9", {"start": v(-20.86, -58.86) * mm, "end": v(-24.01, -58.86) * mm});
            skLineSegment(sketch, "E14.14.7.9", {"start": v(-24.01, -58.86) * mm, "end": v(-25.59, -56.13) * mm});
            skLineSegment(sketch, "E14.17.7.9", {"start": v(-25.59, -56.13) * mm, "end": v(-24.01, -53.4) * mm});
            skLineSegment(sketch, "E14.0.7.10", {"start": v(-24.01, -44.77) * mm, "end": v(-20.86, -44.77) * mm});
            skLineSegment(sketch, "E14.3.7.10", {"start": v(-20.86, -44.77) * mm, "end": v(-19.28, -47.5) * mm});
            skLineSegment(sketch, "E14.6.7.10", {"start": v(-19.28, -47.5) * mm, "end": v(-20.86, -50.23) * mm});
            skCircle(sketch, "E14.9.7.10", {"center": v(-22.44, -47.5) * mm, "radius": 2.73 * mm, "construction": true});
            skLineSegment(sketch, "E14.11.7.10", {"start": v(-20.86, -50.23) * mm, "end": v(-24.01, -50.23) * mm});
            skLineSegment(sketch, "E14.14.7.10", {"start": v(-24.01, -50.23) * mm, "end": v(-25.59, -47.5) * mm});
            skLineSegment(sketch, "E14.17.7.10", {"start": v(-25.59, -47.5) * mm, "end": v(-24.01, -44.77) * mm});
            skLineSegment(sketch, "E14.0.7.11", {"start": v(-24.01, -36.13) * mm, "end": v(-20.86, -36.13) * mm});
            skLineSegment(sketch, "E14.3.7.11", {"start": v(-20.86, -36.13) * mm, "end": v(-19.28, -38.86) * mm});
            skLineSegment(sketch, "E14.6.7.11", {"start": v(-19.28, -38.86) * mm, "end": v(-20.86, -41.6) * mm});
            skCircle(sketch, "E14.9.7.11", {"center": v(-22.44, -38.86) * mm, "radius": 2.73 * mm, "construction": true});
            skLineSegment(sketch, "E14.11.7.11", {"start": v(-20.86, -41.6) * mm, "end": v(-24.01, -41.6) * mm});
            skLineSegment(sketch, "E14.14.7.11", {"start": v(-24.01, -41.6) * mm, "end": v(-25.59, -38.86) * mm});
            skLineSegment(sketch, "E14.17.7.11", {"start": v(-25.59, -38.86) * mm, "end": v(-24.01, -36.13) * mm});
            skLineSegment(sketch, "E14.0.7.12", {"start": v(-24.01, -27.5) * mm, "end": v(-20.86, -27.5) * mm});
            skLineSegment(sketch, "E14.3.7.12", {"start": v(-20.86, -27.5) * mm, "end": v(-19.28, -30.23) * mm});
            skLineSegment(sketch, "E14.6.7.12", {"start": v(-19.28, -30.23) * mm, "end": v(-20.86, -32.96) * mm});
            skCircle(sketch, "E14.9.7.12", {"center": v(-22.44, -30.23) * mm, "radius": 2.73 * mm, "construction": true});
            skLineSegment(sketch, "E14.11.7.12", {"start": v(-20.86, -32.96) * mm, "end": v(-24.01, -32.96) * mm});
            skLineSegment(sketch, "E14.14.7.12", {"start": v(-24.01, -32.96) * mm, "end": v(-25.59, -30.23) * mm});
            skLineSegment(sketch, "E14.17.7.12", {"start": v(-25.59, -30.23) * mm, "end": v(-24.01, -27.5) * mm});
            skLineSegment(sketch, "E14.0.7.13", {"start": v(-24.01, -18.86) * mm, "end": v(-20.86, -18.86) * mm});
            skLineSegment(sketch, "E14.3.7.13", {"start": v(-20.86, -18.86) * mm, "end": v(-19.28, -21.6) * mm});
            skLineSegment(sketch, "E14.6.7.13", {"start": v(-19.28, -21.6) * mm, "end": v(-20.86, -24.32) * mm});
            skCircle(sketch, "E14.9.7.13", {"center": v(-22.44, -21.6) * mm, "radius": 2.73 * mm, "construction": true});
            skLineSegment(sketch, "E14.11.7.13", {"start": v(-20.86, -24.32) * mm, "end": v(-24.01, -24.32) * mm});
            skLineSegment(sketch, "E14.14.7.13", {"start": v(-24.01, -24.32) * mm, "end": v(-25.59, -21.6) * mm});
            skLineSegment(sketch, "E14.17.7.13", {"start": v(-25.59, -21.59) * mm, "end": v(-24.01, -18.86) * mm});
            skLineSegment(sketch, "E14.0.7.14", {"start": v(-24.01, -10.22) * mm, "end": v(-20.86, -10.22) * mm});
            skLineSegment(sketch, "E14.3.7.14", {"start": v(-20.86, -10.22) * mm, "end": v(-19.28, -12.95) * mm});
            skLineSegment(sketch, "E14.6.7.14", {"start": v(-19.28, -12.95) * mm, "end": v(-20.86, -15.68) * mm});
            skCircle(sketch, "E14.9.7.14", {"center": v(-22.44, -12.95) * mm, "radius": 2.73 * mm, "construction": true});
            skLineSegment(sketch, "E14.11.7.14", {"start": v(-20.86, -15.68) * mm, "end": v(-24.01, -15.68) * mm});
            skLineSegment(sketch, "E14.14.7.14", {"start": v(-24.01, -15.68) * mm, "end": v(-25.59, -12.95) * mm});
            skLineSegment(sketch, "E14.17.7.14", {"start": v(-25.59, -12.95) * mm, "end": v(-24.01, -10.22) * mm});
            skLineSegment(sketch, "E14.0.7.15", {"start": v(-24.01, -1.59) * mm, "end": v(-20.86, -1.59) * mm});
            skLineSegment(sketch, "E14.3.7.15", {"start": v(-20.86, -1.59) * mm, "end": v(-19.28, -4.32) * mm});
            skLineSegment(sketch, "E14.6.7.15", {"start": v(-19.28, -4.32) * mm, "end": v(-20.86, -7.05) * mm});
            skCircle(sketch, "E14.9.7.15", {"center": v(-22.44, -4.32) * mm, "radius": 2.73 * mm, "construction": true});
            skLineSegment(sketch, "E14.11.7.15", {"start": v(-20.86, -7.05) * mm, "end": v(-24.01, -7.05) * mm});
            skLineSegment(sketch, "E14.14.7.15", {"start": v(-24.01, -7.05) * mm, "end": v(-25.59, -4.32) * mm});
            skLineSegment(sketch, "E14.17.7.15", {"start": v(-25.59, -4.32) * mm, "end": v(-24.01, -1.59) * mm});
            skLineSegment(sketch, "E14.0.7.16", {"start": v(-24.01, 7.05) * mm, "end": v(-20.86, 7.05) * mm});
            skLineSegment(sketch, "E14.3.7.16", {"start": v(-20.86, 7.05) * mm, "end": v(-19.28, 4.32) * mm});
            skLineSegment(sketch, "E14.6.7.16", {"start": v(-19.28, 4.32) * mm, "end": v(-20.86, 1.59) * mm});
            skCircle(sketch, "E14.9.7.16", {"center": v(-22.44, 4.32) * mm, "radius": 2.73 * mm, "construction": true});
            skLineSegment(sketch, "E14.11.7.16", {"start": v(-20.86, 1.59) * mm, "end": v(-24.01, 1.59) * mm});
            skLineSegment(sketch, "E14.14.7.16", {"start": v(-24.01, 1.59) * mm, "end": v(-25.59, 4.32) * mm});
            skLineSegment(sketch, "E14.17.7.16", {"start": v(-25.59, 4.32) * mm, "end": v(-24.01, 7.05) * mm});
            skLineSegment(sketch, "E14.0.7.17", {"start": v(-24.01, 15.68) * mm, "end": v(-20.86, 15.68) * mm});
            skLineSegment(sketch, "E14.3.7.17", {"start": v(-20.86, 15.68) * mm, "end": v(-19.28, 12.95) * mm});
            skLineSegment(sketch, "E14.6.7.17", {"start": v(-19.28, 12.95) * mm, "end": v(-20.86, 10.22) * mm});
            skCircle(sketch, "E14.9.7.17", {"center": v(-22.44, 12.95) * mm, "radius": 2.73 * mm, "construction": true});
            skLineSegment(sketch, "E14.11.7.17", {"start": v(-20.86, 10.22) * mm, "end": v(-24.01, 10.22) * mm});
            skLineSegment(sketch, "E14.14.7.17", {"start": v(-24.01, 10.22) * mm, "end": v(-25.59, 12.95) * mm});
            skLineSegment(sketch, "E14.17.7.17", {"start": v(-25.59, 12.95) * mm, "end": v(-24.01, 15.68) * mm});
            skLineSegment(sketch, "E14.0.7.18", {"start": v(-24.01, 24.32) * mm, "end": v(-20.86, 24.32) * mm});
            skLineSegment(sketch, "E14.3.7.18", {"start": v(-20.86, 24.32) * mm, "end": v(-19.28, 21.59) * mm});
            skLineSegment(sketch, "E14.6.7.18", {"start": v(-19.28, 21.59) * mm, "end": v(-20.86, 18.86) * mm});
            skCircle(sketch, "E14.9.7.18", {"center": v(-22.44, 21.59) * mm, "radius": 2.73 * mm, "construction": true});
            skLineSegment(sketch, "E14.11.7.18", {"start": v(-20.86, 18.86) * mm, "end": v(-24.01, 18.86) * mm});
            skLineSegment(sketch, "E14.14.7.18", {"start": v(-24.01, 18.86) * mm, "end": v(-25.59, 21.59) * mm});
            skLineSegment(sketch, "E14.17.7.18", {"start": v(-25.59, 21.6) * mm, "end": v(-24.01, 24.32) * mm});
            skLineSegment(sketch, "E14.0.7.19", {"start": v(-24.01, 32.96) * mm, "end": v(-20.86, 32.96) * mm});
            skLineSegment(sketch, "E14.3.7.19", {"start": v(-20.86, 32.96) * mm, "end": v(-19.28, 30.23) * mm});
            skLineSegment(sketch, "E14.6.7.19", {"start": v(-19.28, 30.23) * mm, "end": v(-20.86, 27.5) * mm});
            skCircle(sketch, "E14.9.7.19", {"center": v(-22.44, 30.23) * mm, "radius": 2.73 * mm, "construction": true});
            skLineSegment(sketch, "E14.11.7.19", {"start": v(-20.86, 27.5) * mm, "end": v(-24.01, 27.5) * mm});
            skLineSegment(sketch, "E14.14.7.19", {"start": v(-24.01, 27.5) * mm, "end": v(-25.59, 30.23) * mm});
            skLineSegment(sketch, "E14.17.7.19", {"start": v(-25.59, 30.23) * mm, "end": v(-24.01, 32.96) * mm});
            skLineSegment(sketch, "E14.0.8.0", {"start": v(-9.06, -131.13) * mm, "end": v(-5.9, -131.13) * mm});
            skLineSegment(sketch, "E14.3.8.0", {"start": v(-5.9, -131.13) * mm, "end": v(-4.33, -133.86) * mm});
            skLineSegment(sketch, "E14.6.8.0", {"start": v(-4.33, -133.86) * mm, "end": v(-5.9, -136.59) * mm});
            skCircle(sketch, "E14.9.8.0", {"center": v(-7.48, -133.86) * mm, "radius": 2.73 * mm, "construction": true});
            skLineSegment(sketch, "E14.11.8.0", {"start": v(-5.9, -136.59) * mm, "end": v(-9.06, -136.59) * mm});
            skLineSegment(sketch, "E14.14.8.0", {"start": v(-9.06, -136.59) * mm, "end": v(-10.63, -133.86) * mm});
            skLineSegment(sketch, "E14.17.8.0", {"start": v(-10.63, -133.86) * mm, "end": v(-9.06, -131.13) * mm});
            skLineSegment(sketch, "E14.0.8.1", {"start": v(-9.06, -122.5) * mm, "end": v(-5.9, -122.5) * mm});
            skLineSegment(sketch, "E14.3.8.1", {"start": v(-5.9, -122.5) * mm, "end": v(-4.33, -125.22) * mm});
            skLineSegment(sketch, "E14.6.8.1", {"start": v(-4.33, -125.22) * mm, "end": v(-5.9, -127.95) * mm});
            skCircle(sketch, "E14.9.8.1", {"center": v(-7.48, -125.22) * mm, "radius": 2.73 * mm, "construction": true});
            skLineSegment(sketch, "E14.11.8.1", {"start": v(-5.9, -127.95) * mm, "end": v(-9.06, -127.95) * mm});
            skLineSegment(sketch, "E14.14.8.1", {"start": v(-9.06, -127.95) * mm, "end": v(-10.63, -125.22) * mm});
            skLineSegment(sketch, "E14.17.8.1", {"start": v(-10.63, -125.22) * mm, "end": v(-9.06, -122.5) * mm});
            skLineSegment(sketch, "E14.0.8.2", {"start": v(-9.06, -113.86) * mm, "end": v(-5.9, -113.86) * mm});
            skLineSegment(sketch, "E14.3.8.2", {"start": v(-5.9, -113.86) * mm, "end": v(-4.33, -116.59) * mm});
            skLineSegment(sketch, "E14.6.8.2", {"start": v(-4.33, -116.59) * mm, "end": v(-5.9, -119.32) * mm});
            skCircle(sketch, "E14.9.8.2", {"center": v(-7.48, -116.59) * mm, "radius": 2.73 * mm, "construction": true});
            skLineSegment(sketch, "E14.11.8.2", {"start": v(-5.9, -119.32) * mm, "end": v(-9.06, -119.32) * mm});
            skLineSegment(sketch, "E14.14.8.2", {"start": v(-9.06, -119.32) * mm, "end": v(-10.63, -116.59) * mm});
            skLineSegment(sketch, "E14.17.8.2", {"start": v(-10.63, -116.59) * mm, "end": v(-9.06, -113.86) * mm});
            skLineSegment(sketch, "E14.0.8.3", {"start": v(-9.06, -105.22) * mm, "end": v(-5.9, -105.22) * mm});
            skLineSegment(sketch, "E14.3.8.3", {"start": v(-5.9, -105.22) * mm, "end": v(-4.33, -107.95) * mm});
            skLineSegment(sketch, "E14.6.8.3", {"start": v(-4.33, -107.95) * mm, "end": v(-5.9, -110.68) * mm});
            skCircle(sketch, "E14.9.8.3", {"center": v(-7.48, -107.95) * mm, "radius": 2.73 * mm, "construction": true});
            skLineSegment(sketch, "E14.11.8.3", {"start": v(-5.9, -110.68) * mm, "end": v(-9.06, -110.68) * mm});
            skLineSegment(sketch, "E14.14.8.3", {"start": v(-9.06, -110.68) * mm, "end": v(-10.63, -107.95) * mm});
            skLineSegment(sketch, "E14.17.8.3", {"start": v(-10.63, -107.95) * mm, "end": v(-9.06, -105.22) * mm});
            skLineSegment(sketch, "E14.0.8.4", {"start": v(-9.06, -96.58) * mm, "end": v(-5.9, -96.58) * mm});
            skLineSegment(sketch, "E14.3.8.4", {"start": v(-5.9, -96.58) * mm, "end": v(-4.33, -99.31) * mm});
            skLineSegment(sketch, "E14.6.8.4", {"start": v(-4.33, -99.31) * mm, "end": v(-5.9, -102.04) * mm});
            skCircle(sketch, "E14.9.8.4", {"center": v(-7.48, -99.31) * mm, "radius": 2.73 * mm, "construction": true});
            skLineSegment(sketch, "E14.11.8.4", {"start": v(-5.9, -102.04) * mm, "end": v(-9.06, -102.04) * mm});
            skLineSegment(sketch, "E14.14.8.4", {"start": v(-9.06, -102.04) * mm, "end": v(-10.63, -99.31) * mm});
            skLineSegment(sketch, "E14.17.8.4", {"start": v(-10.63, -99.31) * mm, "end": v(-9.06, -96.58) * mm});
            skLineSegment(sketch, "E14.0.8.5", {"start": v(-9.06, -87.95) * mm, "end": v(-5.9, -87.95) * mm});
            skLineSegment(sketch, "E14.3.8.5", {"start": v(-5.9, -87.95) * mm, "end": v(-4.33, -90.68) * mm});
            skLineSegment(sketch, "E14.6.8.5", {"start": v(-4.33, -90.68) * mm, "end": v(-5.9, -93.4) * mm});
            skCircle(sketch, "E14.9.8.5", {"center": v(-7.48, -90.68) * mm, "radius": 2.73 * mm, "construction": true});
            skLineSegment(sketch, "E14.11.8.5", {"start": v(-5.9, -93.4) * mm, "end": v(-9.06, -93.4) * mm});
            skLineSegment(sketch, "E14.14.8.5", {"start": v(-9.06, -93.4) * mm, "end": v(-10.63, -90.68) * mm});
            skLineSegment(sketch, "E14.17.8.5", {"start": v(-10.63, -90.68) * mm, "end": v(-9.06, -87.95) * mm});
            skLineSegment(sketch, "E14.0.8.6", {"start": v(-9.06, -79.31) * mm, "end": v(-5.9, -79.31) * mm});
            skLineSegment(sketch, "E14.3.8.6", {"start": v(-5.9, -79.31) * mm, "end": v(-4.33, -82.04) * mm});
            skLineSegment(sketch, "E14.6.8.6", {"start": v(-4.33, -82.04) * mm, "end": v(-5.9, -84.77) * mm});
            skCircle(sketch, "E14.9.8.6", {"center": v(-7.48, -82.04) * mm, "radius": 2.73 * mm, "construction": true});
            skLineSegment(sketch, "E14.11.8.6", {"start": v(-5.9, -84.77) * mm, "end": v(-9.06, -84.77) * mm});
            skLineSegment(sketch, "E14.14.8.6", {"start": v(-9.06, -84.77) * mm, "end": v(-10.63, -82.04) * mm});
            skLineSegment(sketch, "E14.17.8.6", {"start": v(-10.63, -82.04) * mm, "end": v(-9.06, -79.31) * mm});
            skLineSegment(sketch, "E14.0.8.7", {"start": v(-9.06, -70.68) * mm, "end": v(-5.9, -70.68) * mm});
            skLineSegment(sketch, "E14.3.8.7", {"start": v(-5.9, -70.68) * mm, "end": v(-4.33, -73.4) * mm});
            skLineSegment(sketch, "E14.6.8.7", {"start": v(-4.33, -73.4) * mm, "end": v(-5.9, -76.14) * mm});
            skCircle(sketch, "E14.9.8.7", {"center": v(-7.48, -73.4) * mm, "radius": 2.73 * mm, "construction": true});
            skLineSegment(sketch, "E14.11.8.7", {"start": v(-5.9, -76.14) * mm, "end": v(-9.06, -76.14) * mm});
            skLineSegment(sketch, "E14.14.8.7", {"start": v(-9.06, -76.14) * mm, "end": v(-10.63, -73.4) * mm});
            skLineSegment(sketch, "E14.17.8.7", {"start": v(-10.63, -73.4) * mm, "end": v(-9.06, -70.68) * mm});
            skLineSegment(sketch, "E14.0.8.8", {"start": v(-9.06, -62.04) * mm, "end": v(-5.9, -62.04) * mm});
            skLineSegment(sketch, "E14.3.8.8", {"start": v(-5.9, -62.04) * mm, "end": v(-4.33, -64.77) * mm});
            skLineSegment(sketch, "E14.6.8.8", {"start": v(-4.33, -64.77) * mm, "end": v(-5.9, -67.5) * mm});
            skCircle(sketch, "E14.9.8.8", {"center": v(-7.48, -64.77) * mm, "radius": 2.73 * mm, "construction": true});
            skLineSegment(sketch, "E14.11.8.8", {"start": v(-5.9, -67.5) * mm, "end": v(-9.06, -67.5) * mm});
            skLineSegment(sketch, "E14.14.8.8", {"start": v(-9.06, -67.5) * mm, "end": v(-10.63, -64.77) * mm});
            skLineSegment(sketch, "E14.17.8.8", {"start": v(-10.63, -64.77) * mm, "end": v(-9.06, -62.04) * mm});
            skLineSegment(sketch, "E14.0.8.9", {"start": v(-9.06, -53.4) * mm, "end": v(-5.9, -53.4) * mm});
            skLineSegment(sketch, "E14.3.8.9", {"start": v(-5.9, -53.4) * mm, "end": v(-4.33, -56.13) * mm});
            skLineSegment(sketch, "E14.6.8.9", {"start": v(-4.33, -56.13) * mm, "end": v(-5.9, -58.86) * mm});
            skCircle(sketch, "E14.9.8.9", {"center": v(-7.48, -56.13) * mm, "radius": 2.73 * mm, "construction": true});
            skLineSegment(sketch, "E14.11.8.9", {"start": v(-5.9, -58.86) * mm, "end": v(-9.06, -58.86) * mm});
            skLineSegment(sketch, "E14.14.8.9", {"start": v(-9.06, -58.86) * mm, "end": v(-10.63, -56.13) * mm});
            skLineSegment(sketch, "E14.17.8.9", {"start": v(-10.63, -56.13) * mm, "end": v(-9.06, -53.4) * mm});
            skLineSegment(sketch, "E14.0.8.10", {"start": v(-9.06, -44.77) * mm, "end": v(-5.9, -44.77) * mm});
            skLineSegment(sketch, "E14.3.8.10", {"start": v(-5.9, -44.77) * mm, "end": v(-4.33, -47.5) * mm});
            skLineSegment(sketch, "E14.6.8.10", {"start": v(-4.33, -47.5) * mm, "end": v(-5.9, -50.23) * mm});
            skCircle(sketch, "E14.9.8.10", {"center": v(-7.48, -47.5) * mm, "radius": 2.73 * mm, "construction": true});
            skLineSegment(sketch, "E14.11.8.10", {"start": v(-5.9, -50.23) * mm, "end": v(-9.06, -50.23) * mm});
            skLineSegment(sketch, "E14.14.8.10", {"start": v(-9.06, -50.23) * mm, "end": v(-10.63, -47.5) * mm});
            skLineSegment(sketch, "E14.17.8.10", {"start": v(-10.63, -47.5) * mm, "end": v(-9.06, -44.77) * mm});
            skLineSegment(sketch, "E14.0.8.11", {"start": v(-9.06, -36.13) * mm, "end": v(-5.9, -36.13) * mm});
            skLineSegment(sketch, "E14.3.8.11", {"start": v(-5.9, -36.13) * mm, "end": v(-4.33, -38.86) * mm});
            skLineSegment(sketch, "E14.6.8.11", {"start": v(-4.33, -38.86) * mm, "end": v(-5.9, -41.6) * mm});
            skCircle(sketch, "E14.9.8.11", {"center": v(-7.48, -38.86) * mm, "radius": 2.73 * mm, "construction": true});
            skLineSegment(sketch, "E14.11.8.11", {"start": v(-5.9, -41.6) * mm, "end": v(-9.06, -41.6) * mm});
            skLineSegment(sketch, "E14.14.8.11", {"start": v(-9.06, -41.6) * mm, "end": v(-10.63, -38.86) * mm});
            skLineSegment(sketch, "E14.17.8.11", {"start": v(-10.63, -38.86) * mm, "end": v(-9.06, -36.13) * mm});
            skLineSegment(sketch, "E14.0.8.12", {"start": v(-9.06, -27.5) * mm, "end": v(-5.9, -27.5) * mm});
            skLineSegment(sketch, "E14.3.8.12", {"start": v(-5.9, -27.5) * mm, "end": v(-4.33, -30.23) * mm});
            skLineSegment(sketch, "E14.6.8.12", {"start": v(-4.33, -30.23) * mm, "end": v(-5.9, -32.96) * mm});
            skCircle(sketch, "E14.9.8.12", {"center": v(-7.48, -30.23) * mm, "radius": 2.73 * mm, "construction": true});
            skLineSegment(sketch, "E14.11.8.12", {"start": v(-5.9, -32.96) * mm, "end": v(-9.06, -32.96) * mm});
            skLineSegment(sketch, "E14.14.8.12", {"start": v(-9.06, -32.96) * mm, "end": v(-10.63, -30.23) * mm});
            skLineSegment(sketch, "E14.17.8.12", {"start": v(-10.63, -30.23) * mm, "end": v(-9.06, -27.5) * mm});
            skLineSegment(sketch, "E14.0.8.13", {"start": v(-9.06, -18.86) * mm, "end": v(-5.9, -18.86) * mm});
            skLineSegment(sketch, "E14.3.8.13", {"start": v(-5.9, -18.86) * mm, "end": v(-4.33, -21.6) * mm});
            skLineSegment(sketch, "E14.6.8.13", {"start": v(-4.33, -21.6) * mm, "end": v(-5.9, -24.32) * mm});
            skCircle(sketch, "E14.9.8.13", {"center": v(-7.48, -21.6) * mm, "radius": 2.73 * mm, "construction": true});
            skLineSegment(sketch, "E14.11.8.13", {"start": v(-5.9, -24.32) * mm, "end": v(-9.06, -24.32) * mm});
            skLineSegment(sketch, "E14.14.8.13", {"start": v(-9.06, -24.32) * mm, "end": v(-10.63, -21.6) * mm});
            skLineSegment(sketch, "E14.17.8.13", {"start": v(-10.63, -21.59) * mm, "end": v(-9.06, -18.86) * mm});
            skLineSegment(sketch, "E14.0.8.14", {"start": v(-9.06, -10.22) * mm, "end": v(-5.9, -10.22) * mm});
            skLineSegment(sketch, "E14.3.8.14", {"start": v(-5.9, -10.22) * mm, "end": v(-4.33, -12.95) * mm});
            skLineSegment(sketch, "E14.6.8.14", {"start": v(-4.33, -12.95) * mm, "end": v(-5.9, -15.68) * mm});
            skCircle(sketch, "E14.9.8.14", {"center": v(-7.48, -12.95) * mm, "radius": 2.73 * mm, "construction": true});
            skLineSegment(sketch, "E14.11.8.14", {"start": v(-5.9, -15.68) * mm, "end": v(-9.06, -15.68) * mm});
            skLineSegment(sketch, "E14.14.8.14", {"start": v(-9.06, -15.68) * mm, "end": v(-10.63, -12.95) * mm});
            skLineSegment(sketch, "E14.17.8.14", {"start": v(-10.63, -12.95) * mm, "end": v(-9.06, -10.22) * mm});
            skLineSegment(sketch, "E14.0.8.15", {"start": v(-9.06, -1.59) * mm, "end": v(-5.9, -1.59) * mm});
            skLineSegment(sketch, "E14.3.8.15", {"start": v(-5.9, -1.59) * mm, "end": v(-4.33, -4.32) * mm});
            skLineSegment(sketch, "E14.6.8.15", {"start": v(-4.33, -4.32) * mm, "end": v(-5.9, -7.05) * mm});
            skCircle(sketch, "E14.9.8.15", {"center": v(-7.48, -4.32) * mm, "radius": 2.73 * mm, "construction": true});
            skLineSegment(sketch, "E14.11.8.15", {"start": v(-5.9, -7.05) * mm, "end": v(-9.06, -7.05) * mm});
            skLineSegment(sketch, "E14.14.8.15", {"start": v(-9.06, -7.05) * mm, "end": v(-10.63, -4.32) * mm});
            skLineSegment(sketch, "E14.17.8.15", {"start": v(-10.63, -4.32) * mm, "end": v(-9.06, -1.59) * mm});
            skLineSegment(sketch, "E14.0.8.16", {"start": v(-9.06, 7.05) * mm, "end": v(-5.9, 7.05) * mm});
            skLineSegment(sketch, "E14.3.8.16", {"start": v(-5.9, 7.05) * mm, "end": v(-4.33, 4.32) * mm});
            skLineSegment(sketch, "E14.6.8.16", {"start": v(-4.33, 4.32) * mm, "end": v(-5.9, 1.59) * mm});
            skCircle(sketch, "E14.9.8.16", {"center": v(-7.48, 4.32) * mm, "radius": 2.73 * mm, "construction": true});
            skLineSegment(sketch, "E14.11.8.16", {"start": v(-5.9, 1.59) * mm, "end": v(-9.06, 1.59) * mm});
            skLineSegment(sketch, "E14.14.8.16", {"start": v(-9.06, 1.59) * mm, "end": v(-10.63, 4.32) * mm});
            skLineSegment(sketch, "E14.17.8.16", {"start": v(-10.63, 4.32) * mm, "end": v(-9.06, 7.05) * mm});
            skLineSegment(sketch, "E14.0.8.17", {"start": v(-9.06, 15.68) * mm, "end": v(-5.9, 15.68) * mm});
            skLineSegment(sketch, "E14.3.8.17", {"start": v(-5.9, 15.68) * mm, "end": v(-4.33, 12.95) * mm});
            skLineSegment(sketch, "E14.6.8.17", {"start": v(-4.33, 12.95) * mm, "end": v(-5.9, 10.22) * mm});
            skCircle(sketch, "E14.9.8.17", {"center": v(-7.48, 12.95) * mm, "radius": 2.73 * mm, "construction": true});
            skLineSegment(sketch, "E14.11.8.17", {"start": v(-5.9, 10.22) * mm, "end": v(-9.06, 10.22) * mm});
            skLineSegment(sketch, "E14.14.8.17", {"start": v(-9.06, 10.22) * mm, "end": v(-10.63, 12.95) * mm});
            skLineSegment(sketch, "E14.17.8.17", {"start": v(-10.63, 12.95) * mm, "end": v(-9.06, 15.68) * mm});
            skLineSegment(sketch, "E14.0.8.18", {"start": v(-9.06, 24.32) * mm, "end": v(-5.9, 24.32) * mm});
            skLineSegment(sketch, "E14.3.8.18", {"start": v(-5.9, 24.32) * mm, "end": v(-4.33, 21.59) * mm});
            skLineSegment(sketch, "E14.6.8.18", {"start": v(-4.33, 21.59) * mm, "end": v(-5.9, 18.86) * mm});
            skCircle(sketch, "E14.9.8.18", {"center": v(-7.48, 21.59) * mm, "radius": 2.73 * mm, "construction": true});
            skLineSegment(sketch, "E14.11.8.18", {"start": v(-5.9, 18.86) * mm, "end": v(-9.06, 18.86) * mm});
            skLineSegment(sketch, "E14.14.8.18", {"start": v(-9.06, 18.86) * mm, "end": v(-10.63, 21.59) * mm});
            skLineSegment(sketch, "E14.17.8.18", {"start": v(-10.63, 21.6) * mm, "end": v(-9.06, 24.32) * mm});
            skLineSegment(sketch, "E14.0.8.19", {"start": v(-9.06, 32.96) * mm, "end": v(-5.9, 32.96) * mm});
            skLineSegment(sketch, "E14.3.8.19", {"start": v(-5.9, 32.96) * mm, "end": v(-4.33, 30.23) * mm});
            skLineSegment(sketch, "E14.6.8.19", {"start": v(-4.33, 30.23) * mm, "end": v(-5.9, 27.5) * mm});
            skCircle(sketch, "E14.9.8.19", {"center": v(-7.48, 30.23) * mm, "radius": 2.73 * mm, "construction": true});
            skLineSegment(sketch, "E14.11.8.19", {"start": v(-5.9, 27.5) * mm, "end": v(-9.06, 27.5) * mm});
            skLineSegment(sketch, "E14.14.8.19", {"start": v(-9.06, 27.5) * mm, "end": v(-10.63, 30.23) * mm});
            skLineSegment(sketch, "E14.17.8.19", {"start": v(-10.63, 30.23) * mm, "end": v(-9.06, 32.96) * mm});
            skLineSegment(sketch, "E14.0.9.0", {"start": v(5.9, -131.13) * mm, "end": v(9.06, -131.13) * mm});
            skLineSegment(sketch, "E14.3.9.0", {"start": v(9.06, -131.13) * mm, "end": v(10.63, -133.86) * mm});
            skLineSegment(sketch, "E14.6.9.0", {"start": v(10.63, -133.86) * mm, "end": v(9.06, -136.59) * mm});
            skCircle(sketch, "E14.9.9.0", {"center": v(7.48, -133.86) * mm, "radius": 2.73 * mm, "construction": true});
            skLineSegment(sketch, "E14.11.9.0", {"start": v(9.06, -136.59) * mm, "end": v(5.9, -136.59) * mm});
            skLineSegment(sketch, "E14.14.9.0", {"start": v(5.9, -136.59) * mm, "end": v(4.33, -133.86) * mm});
            skLineSegment(sketch, "E14.17.9.0", {"start": v(4.33, -133.86) * mm, "end": v(5.9, -131.13) * mm});
            skLineSegment(sketch, "E14.0.9.1", {"start": v(5.9, -122.5) * mm, "end": v(9.06, -122.5) * mm});
            skLineSegment(sketch, "E14.3.9.1", {"start": v(9.06, -122.5) * mm, "end": v(10.63, -125.22) * mm});
            skLineSegment(sketch, "E14.6.9.1", {"start": v(10.63, -125.22) * mm, "end": v(9.06, -127.95) * mm});
            skCircle(sketch, "E14.9.9.1", {"center": v(7.48, -125.22) * mm, "radius": 2.73 * mm, "construction": true});
            skLineSegment(sketch, "E14.11.9.1", {"start": v(9.06, -127.95) * mm, "end": v(5.9, -127.95) * mm});
            skLineSegment(sketch, "E14.14.9.1", {"start": v(5.9, -127.95) * mm, "end": v(4.33, -125.22) * mm});
            skLineSegment(sketch, "E14.17.9.1", {"start": v(4.33, -125.22) * mm, "end": v(5.9, -122.5) * mm});
            skLineSegment(sketch, "E14.0.9.2", {"start": v(5.9, -113.86) * mm, "end": v(9.06, -113.86) * mm});
            skLineSegment(sketch, "E14.3.9.2", {"start": v(9.06, -113.86) * mm, "end": v(10.63, -116.59) * mm});
            skLineSegment(sketch, "E14.6.9.2", {"start": v(10.63, -116.59) * mm, "end": v(9.06, -119.32) * mm});
            skCircle(sketch, "E14.9.9.2", {"center": v(7.48, -116.59) * mm, "radius": 2.73 * mm, "construction": true});
            skLineSegment(sketch, "E14.11.9.2", {"start": v(9.06, -119.32) * mm, "end": v(5.9, -119.32) * mm});
            skLineSegment(sketch, "E14.14.9.2", {"start": v(5.9, -119.32) * mm, "end": v(4.33, -116.59) * mm});
            skLineSegment(sketch, "E14.17.9.2", {"start": v(4.33, -116.59) * mm, "end": v(5.9, -113.86) * mm});
            skLineSegment(sketch, "E14.0.9.3", {"start": v(5.9, -105.22) * mm, "end": v(9.06, -105.22) * mm});
            skLineSegment(sketch, "E14.3.9.3", {"start": v(9.06, -105.22) * mm, "end": v(10.63, -107.95) * mm});
            skLineSegment(sketch, "E14.6.9.3", {"start": v(10.63, -107.95) * mm, "end": v(9.06, -110.68) * mm});
            skCircle(sketch, "E14.9.9.3", {"center": v(7.48, -107.95) * mm, "radius": 2.73 * mm, "construction": true});
            skLineSegment(sketch, "E14.11.9.3", {"start": v(9.06, -110.68) * mm, "end": v(5.9, -110.68) * mm});
            skLineSegment(sketch, "E14.14.9.3", {"start": v(5.9, -110.68) * mm, "end": v(4.33, -107.95) * mm});
            skLineSegment(sketch, "E14.17.9.3", {"start": v(4.33, -107.95) * mm, "end": v(5.9, -105.22) * mm});
            skLineSegment(sketch, "E14.0.9.4", {"start": v(5.9, -96.58) * mm, "end": v(9.06, -96.58) * mm});
            skLineSegment(sketch, "E14.3.9.4", {"start": v(9.06, -96.58) * mm, "end": v(10.63, -99.31) * mm});
            skLineSegment(sketch, "E14.6.9.4", {"start": v(10.63, -99.31) * mm, "end": v(9.06, -102.04) * mm});
            skCircle(sketch, "E14.9.9.4", {"center": v(7.48, -99.31) * mm, "radius": 2.73 * mm, "construction": true});
            skLineSegment(sketch, "E14.11.9.4", {"start": v(9.06, -102.04) * mm, "end": v(5.9, -102.04) * mm});
            skLineSegment(sketch, "E14.14.9.4", {"start": v(5.9, -102.04) * mm, "end": v(4.33, -99.31) * mm});
            skLineSegment(sketch, "E14.17.9.4", {"start": v(4.33, -99.31) * mm, "end": v(5.9, -96.58) * mm});
            skLineSegment(sketch, "E14.0.9.5", {"start": v(5.9, -87.95) * mm, "end": v(9.06, -87.95) * mm});
            skLineSegment(sketch, "E14.3.9.5", {"start": v(9.06, -87.95) * mm, "end": v(10.63, -90.68) * mm});
            skLineSegment(sketch, "E14.6.9.5", {"start": v(10.63, -90.68) * mm, "end": v(9.06, -93.4) * mm});
            skCircle(sketch, "E14.9.9.5", {"center": v(7.48, -90.68) * mm, "radius": 2.73 * mm, "construction": true});
            skLineSegment(sketch, "E14.11.9.5", {"start": v(9.06, -93.4) * mm, "end": v(5.9, -93.4) * mm});
            skLineSegment(sketch, "E14.14.9.5", {"start": v(5.9, -93.4) * mm, "end": v(4.33, -90.68) * mm});
            skLineSegment(sketch, "E14.17.9.5", {"start": v(4.33, -90.68) * mm, "end": v(5.9, -87.95) * mm});
            skLineSegment(sketch, "E14.0.9.6", {"start": v(5.9, -79.31) * mm, "end": v(9.06, -79.31) * mm});
            skLineSegment(sketch, "E14.3.9.6", {"start": v(9.06, -79.31) * mm, "end": v(10.63, -82.04) * mm});
            skLineSegment(sketch, "E14.6.9.6", {"start": v(10.63, -82.04) * mm, "end": v(9.06, -84.77) * mm});
            skCircle(sketch, "E14.9.9.6", {"center": v(7.48, -82.04) * mm, "radius": 2.73 * mm, "construction": true});
            skLineSegment(sketch, "E14.11.9.6", {"start": v(9.06, -84.77) * mm, "end": v(5.9, -84.77) * mm});
            skLineSegment(sketch, "E14.14.9.6", {"start": v(5.9, -84.77) * mm, "end": v(4.33, -82.04) * mm});
            skLineSegment(sketch, "E14.17.9.6", {"start": v(4.33, -82.04) * mm, "end": v(5.9, -79.31) * mm});
            skLineSegment(sketch, "E14.0.9.7", {"start": v(5.9, -70.68) * mm, "end": v(9.06, -70.68) * mm});
            skLineSegment(sketch, "E14.3.9.7", {"start": v(9.06, -70.68) * mm, "end": v(10.63, -73.4) * mm});
            skLineSegment(sketch, "E14.6.9.7", {"start": v(10.63, -73.4) * mm, "end": v(9.06, -76.14) * mm});
            skCircle(sketch, "E14.9.9.7", {"center": v(7.48, -73.4) * mm, "radius": 2.73 * mm, "construction": true});
            skLineSegment(sketch, "E14.11.9.7", {"start": v(9.06, -76.14) * mm, "end": v(5.9, -76.14) * mm});
            skLineSegment(sketch, "E14.14.9.7", {"start": v(5.9, -76.14) * mm, "end": v(4.33, -73.4) * mm});
            skLineSegment(sketch, "E14.17.9.7", {"start": v(4.33, -73.4) * mm, "end": v(5.9, -70.68) * mm});
            skLineSegment(sketch, "E14.0.9.8", {"start": v(5.9, -62.04) * mm, "end": v(9.06, -62.04) * mm});
            skLineSegment(sketch, "E14.3.9.8", {"start": v(9.06, -62.04) * mm, "end": v(10.63, -64.77) * mm});
            skLineSegment(sketch, "E14.6.9.8", {"start": v(10.63, -64.77) * mm, "end": v(9.06, -67.5) * mm});
            skCircle(sketch, "E14.9.9.8", {"center": v(7.48, -64.77) * mm, "radius": 2.73 * mm, "construction": true});
            skLineSegment(sketch, "E14.11.9.8", {"start": v(9.06, -67.5) * mm, "end": v(5.9, -67.5) * mm});
            skLineSegment(sketch, "E14.14.9.8", {"start": v(5.9, -67.5) * mm, "end": v(4.33, -64.77) * mm});
            skLineSegment(sketch, "E14.17.9.8", {"start": v(4.33, -64.77) * mm, "end": v(5.9, -62.04) * mm});
            skLineSegment(sketch, "E14.0.9.9", {"start": v(5.9, -53.4) * mm, "end": v(9.06, -53.4) * mm});
            skLineSegment(sketch, "E14.3.9.9", {"start": v(9.06, -53.4) * mm, "end": v(10.63, -56.13) * mm});
            skLineSegment(sketch, "E14.6.9.9", {"start": v(10.63, -56.13) * mm, "end": v(9.06, -58.86) * mm});
            skCircle(sketch, "E14.9.9.9", {"center": v(7.48, -56.13) * mm, "radius": 2.73 * mm, "construction": true});
            skLineSegment(sketch, "E14.11.9.9", {"start": v(9.06, -58.86) * mm, "end": v(5.9, -58.86) * mm});
            skLineSegment(sketch, "E14.14.9.9", {"start": v(5.9, -58.86) * mm, "end": v(4.33, -56.13) * mm});
            skLineSegment(sketch, "E14.17.9.9", {"start": v(4.33, -56.13) * mm, "end": v(5.9, -53.4) * mm});
            skLineSegment(sketch, "E14.0.9.10", {"start": v(5.9, -44.77) * mm, "end": v(9.06, -44.77) * mm});
            skLineSegment(sketch, "E14.3.9.10", {"start": v(9.06, -44.77) * mm, "end": v(10.63, -47.5) * mm});
            skLineSegment(sketch, "E14.6.9.10", {"start": v(10.63, -47.5) * mm, "end": v(9.06, -50.23) * mm});
            skCircle(sketch, "E14.9.9.10", {"center": v(7.48, -47.5) * mm, "radius": 2.73 * mm, "construction": true});
            skLineSegment(sketch, "E14.11.9.10", {"start": v(9.06, -50.23) * mm, "end": v(5.9, -50.23) * mm});
            skLineSegment(sketch, "E14.14.9.10", {"start": v(5.9, -50.23) * mm, "end": v(4.33, -47.5) * mm});
            skLineSegment(sketch, "E14.17.9.10", {"start": v(4.33, -47.5) * mm, "end": v(5.9, -44.77) * mm});
            skLineSegment(sketch, "E14.0.9.11", {"start": v(5.9, -36.13) * mm, "end": v(9.06, -36.13) * mm});
            skLineSegment(sketch, "E14.3.9.11", {"start": v(9.06, -36.13) * mm, "end": v(10.63, -38.86) * mm});
            skLineSegment(sketch, "E14.6.9.11", {"start": v(10.63, -38.86) * mm, "end": v(9.06, -41.6) * mm});
            skCircle(sketch, "E14.9.9.11", {"center": v(7.48, -38.86) * mm, "radius": 2.73 * mm, "construction": true});
            skLineSegment(sketch, "E14.11.9.11", {"start": v(9.06, -41.6) * mm, "end": v(5.9, -41.6) * mm});
            skLineSegment(sketch, "E14.14.9.11", {"start": v(5.9, -41.6) * mm, "end": v(4.33, -38.86) * mm});
            skLineSegment(sketch, "E14.17.9.11", {"start": v(4.33, -38.86) * mm, "end": v(5.9, -36.13) * mm});
            skLineSegment(sketch, "E14.0.9.12", {"start": v(5.9, -27.5) * mm, "end": v(9.06, -27.5) * mm});
            skLineSegment(sketch, "E14.3.9.12", {"start": v(9.06, -27.5) * mm, "end": v(10.63, -30.23) * mm});
            skLineSegment(sketch, "E14.6.9.12", {"start": v(10.63, -30.23) * mm, "end": v(9.06, -32.96) * mm});
            skCircle(sketch, "E14.9.9.12", {"center": v(7.48, -30.23) * mm, "radius": 2.73 * mm, "construction": true});
            skLineSegment(sketch, "E14.11.9.12", {"start": v(9.06, -32.96) * mm, "end": v(5.9, -32.96) * mm});
            skLineSegment(sketch, "E14.14.9.12", {"start": v(5.9, -32.96) * mm, "end": v(4.33, -30.23) * mm});
            skLineSegment(sketch, "E14.17.9.12", {"start": v(4.33, -30.23) * mm, "end": v(5.9, -27.5) * mm});
            skLineSegment(sketch, "E14.0.9.13", {"start": v(5.9, -18.86) * mm, "end": v(9.06, -18.86) * mm});
            skLineSegment(sketch, "E14.3.9.13", {"start": v(9.06, -18.86) * mm, "end": v(10.63, -21.6) * mm});
            skLineSegment(sketch, "E14.6.9.13", {"start": v(10.63, -21.6) * mm, "end": v(9.06, -24.32) * mm});
            skCircle(sketch, "E14.9.9.13", {"center": v(7.48, -21.6) * mm, "radius": 2.73 * mm, "construction": true});
            skLineSegment(sketch, "E14.11.9.13", {"start": v(9.06, -24.32) * mm, "end": v(5.9, -24.32) * mm});
            skLineSegment(sketch, "E14.14.9.13", {"start": v(5.9, -24.32) * mm, "end": v(4.33, -21.6) * mm});
            skLineSegment(sketch, "E14.17.9.13", {"start": v(4.33, -21.59) * mm, "end": v(5.9, -18.86) * mm});
            skLineSegment(sketch, "E14.0.9.14", {"start": v(5.9, -10.22) * mm, "end": v(9.06, -10.22) * mm});
            skLineSegment(sketch, "E14.3.9.14", {"start": v(9.06, -10.22) * mm, "end": v(10.63, -12.95) * mm});
            skLineSegment(sketch, "E14.6.9.14", {"start": v(10.63, -12.95) * mm, "end": v(9.06, -15.68) * mm});
            skCircle(sketch, "E14.9.9.14", {"center": v(7.48, -12.95) * mm, "radius": 2.73 * mm, "construction": true});
            skLineSegment(sketch, "E14.11.9.14", {"start": v(9.06, -15.68) * mm, "end": v(5.9, -15.68) * mm});
            skLineSegment(sketch, "E14.14.9.14", {"start": v(5.9, -15.68) * mm, "end": v(4.33, -12.95) * mm});
            skLineSegment(sketch, "E14.17.9.14", {"start": v(4.33, -12.95) * mm, "end": v(5.9, -10.22) * mm});
            skLineSegment(sketch, "E14.0.9.15", {"start": v(5.9, -1.59) * mm, "end": v(9.06, -1.59) * mm});
            skLineSegment(sketch, "E14.3.9.15", {"start": v(9.06, -1.59) * mm, "end": v(10.63, -4.32) * mm});
            skLineSegment(sketch, "E14.6.9.15", {"start": v(10.63, -4.32) * mm, "end": v(9.06, -7.05) * mm});
            skCircle(sketch, "E14.9.9.15", {"center": v(7.48, -4.32) * mm, "radius": 2.73 * mm, "construction": true});
            skLineSegment(sketch, "E14.11.9.15", {"start": v(9.06, -7.05) * mm, "end": v(5.9, -7.05) * mm});
            skLineSegment(sketch, "E14.14.9.15", {"start": v(5.9, -7.05) * mm, "end": v(4.33, -4.32) * mm});
            skLineSegment(sketch, "E14.17.9.15", {"start": v(4.33, -4.32) * mm, "end": v(5.9, -1.59) * mm});
            skLineSegment(sketch, "E14.0.9.16", {"start": v(5.9, 7.05) * mm, "end": v(9.06, 7.05) * mm});
            skLineSegment(sketch, "E14.3.9.16", {"start": v(9.06, 7.05) * mm, "end": v(10.63, 4.32) * mm});
            skLineSegment(sketch, "E14.6.9.16", {"start": v(10.63, 4.32) * mm, "end": v(9.06, 1.59) * mm});
            skCircle(sketch, "E14.9.9.16", {"center": v(7.48, 4.32) * mm, "radius": 2.73 * mm, "construction": true});
            skLineSegment(sketch, "E14.11.9.16", {"start": v(9.06, 1.59) * mm, "end": v(5.9, 1.59) * mm});
            skLineSegment(sketch, "E14.14.9.16", {"start": v(5.9, 1.59) * mm, "end": v(4.33, 4.32) * mm});
            skLineSegment(sketch, "E14.17.9.16", {"start": v(4.33, 4.32) * mm, "end": v(5.9, 7.05) * mm});
            skLineSegment(sketch, "E14.0.9.17", {"start": v(5.9, 15.68) * mm, "end": v(9.06, 15.68) * mm});
            skLineSegment(sketch, "E14.3.9.17", {"start": v(9.06, 15.68) * mm, "end": v(10.63, 12.95) * mm});
            skLineSegment(sketch, "E14.6.9.17", {"start": v(10.63, 12.95) * mm, "end": v(9.06, 10.22) * mm});
            skCircle(sketch, "E14.9.9.17", {"center": v(7.48, 12.95) * mm, "radius": 2.73 * mm, "construction": true});
            skLineSegment(sketch, "E14.11.9.17", {"start": v(9.06, 10.22) * mm, "end": v(5.9, 10.22) * mm});
            skLineSegment(sketch, "E14.14.9.17", {"start": v(5.9, 10.22) * mm, "end": v(4.33, 12.95) * mm});
            skLineSegment(sketch, "E14.17.9.17", {"start": v(4.33, 12.95) * mm, "end": v(5.9, 15.68) * mm});
            skLineSegment(sketch, "E14.0.9.18", {"start": v(5.9, 24.32) * mm, "end": v(9.06, 24.32) * mm});
            skLineSegment(sketch, "E14.3.9.18", {"start": v(9.06, 24.32) * mm, "end": v(10.63, 21.59) * mm});
            skLineSegment(sketch, "E14.6.9.18", {"start": v(10.63, 21.59) * mm, "end": v(9.06, 18.86) * mm});
            skCircle(sketch, "E14.9.9.18", {"center": v(7.48, 21.59) * mm, "radius": 2.73 * mm, "construction": true});
            skLineSegment(sketch, "E14.11.9.18", {"start": v(9.06, 18.86) * mm, "end": v(5.9, 18.86) * mm});
            skLineSegment(sketch, "E14.14.9.18", {"start": v(5.9, 18.86) * mm, "end": v(4.33, 21.59) * mm});
            skLineSegment(sketch, "E14.17.9.18", {"start": v(4.33, 21.6) * mm, "end": v(5.9, 24.32) * mm});
            skLineSegment(sketch, "E14.0.9.19", {"start": v(5.9, 32.96) * mm, "end": v(9.06, 32.96) * mm});
            skLineSegment(sketch, "E14.3.9.19", {"start": v(9.06, 32.96) * mm, "end": v(10.63, 30.23) * mm});
            skLineSegment(sketch, "E14.6.9.19", {"start": v(10.63, 30.23) * mm, "end": v(9.06, 27.5) * mm});
            skCircle(sketch, "E14.9.9.19", {"center": v(7.48, 30.23) * mm, "radius": 2.73 * mm, "construction": true});
            skLineSegment(sketch, "E14.11.9.19", {"start": v(9.06, 27.5) * mm, "end": v(5.9, 27.5) * mm});
            skLineSegment(sketch, "E14.14.9.19", {"start": v(5.9, 27.5) * mm, "end": v(4.33, 30.23) * mm});
            skLineSegment(sketch, "E14.17.9.19", {"start": v(4.33, 30.23) * mm, "end": v(5.9, 32.96) * mm});
            skLineSegment(sketch, "E14.0.10.0", {"start": v(20.86, -131.13) * mm, "end": v(24.01, -131.13) * mm});
            skLineSegment(sketch, "E14.3.10.0", {"start": v(24.01, -131.13) * mm, "end": v(25.6, -133.86) * mm});
            skLineSegment(sketch, "E14.6.10.0", {"start": v(25.6, -133.86) * mm, "end": v(24.01, -136.59) * mm});
            skCircle(sketch, "E14.9.10.0", {"center": v(22.44, -133.86) * mm, "radius": 2.73 * mm, "construction": true});
            skLineSegment(sketch, "E14.11.10.0", {"start": v(24.01, -136.59) * mm, "end": v(20.86, -136.59) * mm});
            skLineSegment(sketch, "E14.14.10.0", {"start": v(20.86, -136.59) * mm, "end": v(19.28, -133.86) * mm});
            skLineSegment(sketch, "E14.17.10.0", {"start": v(19.28, -133.86) * mm, "end": v(20.86, -131.13) * mm});
            skLineSegment(sketch, "E14.0.10.1", {"start": v(20.86, -122.5) * mm, "end": v(24.01, -122.5) * mm});
            skLineSegment(sketch, "E14.3.10.1", {"start": v(24.01, -122.5) * mm, "end": v(25.6, -125.22) * mm});
            skLineSegment(sketch, "E14.6.10.1", {"start": v(25.6, -125.22) * mm, "end": v(24.01, -127.95) * mm});
            skCircle(sketch, "E14.9.10.1", {"center": v(22.44, -125.22) * mm, "radius": 2.73 * mm, "construction": true});
            skLineSegment(sketch, "E14.11.10.1", {"start": v(24.01, -127.95) * mm, "end": v(20.86, -127.95) * mm});
            skLineSegment(sketch, "E14.14.10.1", {"start": v(20.86, -127.95) * mm, "end": v(19.28, -125.22) * mm});
            skLineSegment(sketch, "E14.17.10.1", {"start": v(19.28, -125.22) * mm, "end": v(20.86, -122.5) * mm});
            skLineSegment(sketch, "E14.0.10.2", {"start": v(20.86, -113.86) * mm, "end": v(24.01, -113.86) * mm});
            skLineSegment(sketch, "E14.3.10.2", {"start": v(24.01, -113.86) * mm, "end": v(25.6, -116.59) * mm});
            skLineSegment(sketch, "E14.6.10.2", {"start": v(25.6, -116.59) * mm, "end": v(24.01, -119.32) * mm});
            skCircle(sketch, "E14.9.10.2", {"center": v(22.44, -116.59) * mm, "radius": 2.73 * mm, "construction": true});
            skLineSegment(sketch, "E14.11.10.2", {"start": v(24.01, -119.32) * mm, "end": v(20.86, -119.32) * mm});
            skLineSegment(sketch, "E14.14.10.2", {"start": v(20.86, -119.32) * mm, "end": v(19.28, -116.59) * mm});
            skLineSegment(sketch, "E14.17.10.2", {"start": v(19.28, -116.59) * mm, "end": v(20.86, -113.86) * mm});
            skLineSegment(sketch, "E14.0.10.3", {"start": v(20.86, -105.22) * mm, "end": v(24.01, -105.22) * mm});
            skLineSegment(sketch, "E14.3.10.3", {"start": v(24.01, -105.22) * mm, "end": v(25.6, -107.95) * mm});
            skLineSegment(sketch, "E14.6.10.3", {"start": v(25.6, -107.95) * mm, "end": v(24.01, -110.68) * mm});
            skCircle(sketch, "E14.9.10.3", {"center": v(22.44, -107.95) * mm, "radius": 2.73 * mm, "construction": true});
            skLineSegment(sketch, "E14.11.10.3", {"start": v(24.01, -110.68) * mm, "end": v(20.86, -110.68) * mm});
            skLineSegment(sketch, "E14.14.10.3", {"start": v(20.86, -110.68) * mm, "end": v(19.28, -107.95) * mm});
            skLineSegment(sketch, "E14.17.10.3", {"start": v(19.28, -107.95) * mm, "end": v(20.86, -105.22) * mm});
            skLineSegment(sketch, "E14.0.10.4", {"start": v(20.86, -96.58) * mm, "end": v(24.01, -96.58) * mm});
            skLineSegment(sketch, "E14.3.10.4", {"start": v(24.01, -96.58) * mm, "end": v(25.6, -99.31) * mm});
            skLineSegment(sketch, "E14.6.10.4", {"start": v(25.6, -99.31) * mm, "end": v(24.01, -102.04) * mm});
            skCircle(sketch, "E14.9.10.4", {"center": v(22.44, -99.31) * mm, "radius": 2.73 * mm, "construction": true});
            skLineSegment(sketch, "E14.11.10.4", {"start": v(24.01, -102.04) * mm, "end": v(20.86, -102.04) * mm});
            skLineSegment(sketch, "E14.14.10.4", {"start": v(20.86, -102.04) * mm, "end": v(19.28, -99.31) * mm});
            skLineSegment(sketch, "E14.17.10.4", {"start": v(19.28, -99.31) * mm, "end": v(20.86, -96.58) * mm});
            skLineSegment(sketch, "E14.0.10.5", {"start": v(20.86, -87.95) * mm, "end": v(24.01, -87.95) * mm});
            skLineSegment(sketch, "E14.3.10.5", {"start": v(24.01, -87.95) * mm, "end": v(25.6, -90.68) * mm});
            skLineSegment(sketch, "E14.6.10.5", {"start": v(25.6, -90.68) * mm, "end": v(24.01, -93.4) * mm});
            skCircle(sketch, "E14.9.10.5", {"center": v(22.44, -90.68) * mm, "radius": 2.73 * mm, "construction": true});
            skLineSegment(sketch, "E14.11.10.5", {"start": v(24.01, -93.4) * mm, "end": v(20.86, -93.4) * mm});
            skLineSegment(sketch, "E14.14.10.5", {"start": v(20.86, -93.4) * mm, "end": v(19.28, -90.68) * mm});
            skLineSegment(sketch, "E14.17.10.5", {"start": v(19.28, -90.68) * mm, "end": v(20.86, -87.95) * mm});
            skLineSegment(sketch, "E14.0.10.6", {"start": v(20.86, -79.31) * mm, "end": v(24.01, -79.31) * mm});
            skLineSegment(sketch, "E14.3.10.6", {"start": v(24.01, -79.31) * mm, "end": v(25.6, -82.04) * mm});
            skLineSegment(sketch, "E14.6.10.6", {"start": v(25.6, -82.04) * mm, "end": v(24.01, -84.77) * mm});
            skCircle(sketch, "E14.9.10.6", {"center": v(22.44, -82.04) * mm, "radius": 2.73 * mm, "construction": true});
            skLineSegment(sketch, "E14.11.10.6", {"start": v(24.01, -84.77) * mm, "end": v(20.86, -84.77) * mm});
            skLineSegment(sketch, "E14.14.10.6", {"start": v(20.86, -84.77) * mm, "end": v(19.28, -82.04) * mm});
            skLineSegment(sketch, "E14.17.10.6", {"start": v(19.28, -82.04) * mm, "end": v(20.86, -79.31) * mm});
            skLineSegment(sketch, "E14.0.10.7", {"start": v(20.86, -70.68) * mm, "end": v(24.01, -70.68) * mm});
            skLineSegment(sketch, "E14.3.10.7", {"start": v(24.01, -70.68) * mm, "end": v(25.6, -73.4) * mm});
            skLineSegment(sketch, "E14.6.10.7", {"start": v(25.6, -73.4) * mm, "end": v(24.01, -76.14) * mm});
            skCircle(sketch, "E14.9.10.7", {"center": v(22.44, -73.4) * mm, "radius": 2.73 * mm, "construction": true});
            skLineSegment(sketch, "E14.11.10.7", {"start": v(24.01, -76.14) * mm, "end": v(20.86, -76.14) * mm});
            skLineSegment(sketch, "E14.14.10.7", {"start": v(20.86, -76.14) * mm, "end": v(19.28, -73.4) * mm});
            skLineSegment(sketch, "E14.17.10.7", {"start": v(19.28, -73.4) * mm, "end": v(20.86, -70.68) * mm});
            skLineSegment(sketch, "E14.0.10.8", {"start": v(20.86, -62.04) * mm, "end": v(24.01, -62.04) * mm});
            skLineSegment(sketch, "E14.3.10.8", {"start": v(24.01, -62.04) * mm, "end": v(25.6, -64.77) * mm});
            skLineSegment(sketch, "E14.6.10.8", {"start": v(25.6, -64.77) * mm, "end": v(24.01, -67.5) * mm});
            skCircle(sketch, "E14.9.10.8", {"center": v(22.44, -64.77) * mm, "radius": 2.73 * mm, "construction": true});
            skLineSegment(sketch, "E14.11.10.8", {"start": v(24.01, -67.5) * mm, "end": v(20.86, -67.5) * mm});
            skLineSegment(sketch, "E14.14.10.8", {"start": v(20.86, -67.5) * mm, "end": v(19.28, -64.77) * mm});
            skLineSegment(sketch, "E14.17.10.8", {"start": v(19.28, -64.77) * mm, "end": v(20.86, -62.04) * mm});
            skLineSegment(sketch, "E14.0.10.9", {"start": v(20.86, -53.4) * mm, "end": v(24.01, -53.4) * mm});
            skLineSegment(sketch, "E14.3.10.9", {"start": v(24.01, -53.4) * mm, "end": v(25.6, -56.13) * mm});
            skLineSegment(sketch, "E14.6.10.9", {"start": v(25.6, -56.13) * mm, "end": v(24.01, -58.86) * mm});
            skCircle(sketch, "E14.9.10.9", {"center": v(22.44, -56.13) * mm, "radius": 2.73 * mm, "construction": true});
            skLineSegment(sketch, "E14.11.10.9", {"start": v(24.01, -58.86) * mm, "end": v(20.86, -58.86) * mm});
            skLineSegment(sketch, "E14.14.10.9", {"start": v(20.86, -58.86) * mm, "end": v(19.28, -56.13) * mm});
            skLineSegment(sketch, "E14.17.10.9", {"start": v(19.28, -56.13) * mm, "end": v(20.86, -53.4) * mm});
            skLineSegment(sketch, "E14.0.10.10", {"start": v(20.86, -44.77) * mm, "end": v(24.01, -44.77) * mm});
            skLineSegment(sketch, "E14.3.10.10", {"start": v(24.01, -44.77) * mm, "end": v(25.6, -47.5) * mm});
            skLineSegment(sketch, "E14.6.10.10", {"start": v(25.6, -47.5) * mm, "end": v(24.01, -50.23) * mm});
            skCircle(sketch, "E14.9.10.10", {"center": v(22.44, -47.5) * mm, "radius": 2.73 * mm, "construction": true});
            skLineSegment(sketch, "E14.11.10.10", {"start": v(24.01, -50.23) * mm, "end": v(20.86, -50.23) * mm});
            skLineSegment(sketch, "E14.14.10.10", {"start": v(20.86, -50.23) * mm, "end": v(19.28, -47.5) * mm});
            skLineSegment(sketch, "E14.17.10.10", {"start": v(19.28, -47.5) * mm, "end": v(20.86, -44.77) * mm});
            skLineSegment(sketch, "E14.0.10.11", {"start": v(20.86, -36.13) * mm, "end": v(24.01, -36.13) * mm});
            skLineSegment(sketch, "E14.3.10.11", {"start": v(24.01, -36.13) * mm, "end": v(25.6, -38.86) * mm});
            skLineSegment(sketch, "E14.6.10.11", {"start": v(25.6, -38.86) * mm, "end": v(24.01, -41.6) * mm});
            skCircle(sketch, "E14.9.10.11", {"center": v(22.44, -38.86) * mm, "radius": 2.73 * mm, "construction": true});
            skLineSegment(sketch, "E14.11.10.11", {"start": v(24.01, -41.6) * mm, "end": v(20.86, -41.6) * mm});
            skLineSegment(sketch, "E14.14.10.11", {"start": v(20.86, -41.6) * mm, "end": v(19.28, -38.86) * mm});
            skLineSegment(sketch, "E14.17.10.11", {"start": v(19.28, -38.86) * mm, "end": v(20.86, -36.13) * mm});
            skLineSegment(sketch, "E14.0.10.12", {"start": v(20.86, -27.5) * mm, "end": v(24.01, -27.5) * mm});
            skLineSegment(sketch, "E14.3.10.12", {"start": v(24.01, -27.5) * mm, "end": v(25.6, -30.23) * mm});
            skLineSegment(sketch, "E14.6.10.12", {"start": v(25.6, -30.23) * mm, "end": v(24.01, -32.96) * mm});
            skCircle(sketch, "E14.9.10.12", {"center": v(22.44, -30.23) * mm, "radius": 2.73 * mm, "construction": true});
            skLineSegment(sketch, "E14.11.10.12", {"start": v(24.01, -32.96) * mm, "end": v(20.86, -32.96) * mm});
            skLineSegment(sketch, "E14.14.10.12", {"start": v(20.86, -32.96) * mm, "end": v(19.28, -30.23) * mm});
            skLineSegment(sketch, "E14.17.10.12", {"start": v(19.28, -30.23) * mm, "end": v(20.86, -27.5) * mm});
            skLineSegment(sketch, "E14.0.10.13", {"start": v(20.86, -18.86) * mm, "end": v(24.01, -18.86) * mm});
            skLineSegment(sketch, "E14.3.10.13", {"start": v(24.01, -18.86) * mm, "end": v(25.6, -21.6) * mm});
            skLineSegment(sketch, "E14.6.10.13", {"start": v(25.6, -21.6) * mm, "end": v(24.01, -24.32) * mm});
            skCircle(sketch, "E14.9.10.13", {"center": v(22.44, -21.6) * mm, "radius": 2.73 * mm, "construction": true});
            skLineSegment(sketch, "E14.11.10.13", {"start": v(24.01, -24.32) * mm, "end": v(20.86, -24.32) * mm});
            skLineSegment(sketch, "E14.14.10.13", {"start": v(20.86, -24.32) * mm, "end": v(19.28, -21.6) * mm});
            skLineSegment(sketch, "E14.17.10.13", {"start": v(19.28, -21.59) * mm, "end": v(20.86, -18.86) * mm});
            skLineSegment(sketch, "E14.0.10.14", {"start": v(20.86, -10.22) * mm, "end": v(24.01, -10.22) * mm});
            skLineSegment(sketch, "E14.3.10.14", {"start": v(24.01, -10.22) * mm, "end": v(25.6, -12.95) * mm});
            skLineSegment(sketch, "E14.6.10.14", {"start": v(25.6, -12.95) * mm, "end": v(24.01, -15.68) * mm});
            skCircle(sketch, "E14.9.10.14", {"center": v(22.44, -12.95) * mm, "radius": 2.73 * mm, "construction": true});
            skLineSegment(sketch, "E14.11.10.14", {"start": v(24.01, -15.68) * mm, "end": v(20.86, -15.68) * mm});
            skLineSegment(sketch, "E14.14.10.14", {"start": v(20.86, -15.68) * mm, "end": v(19.28, -12.95) * mm});
            skLineSegment(sketch, "E14.17.10.14", {"start": v(19.28, -12.95) * mm, "end": v(20.86, -10.22) * mm});
            skLineSegment(sketch, "E14.0.10.15", {"start": v(20.86, -1.59) * mm, "end": v(24.01, -1.59) * mm});
            skLineSegment(sketch, "E14.3.10.15", {"start": v(24.01, -1.59) * mm, "end": v(25.6, -4.32) * mm});
            skLineSegment(sketch, "E14.6.10.15", {"start": v(25.6, -4.32) * mm, "end": v(24.01, -7.05) * mm});
            skCircle(sketch, "E14.9.10.15", {"center": v(22.44, -4.32) * mm, "radius": 2.73 * mm, "construction": true});
            skLineSegment(sketch, "E14.11.10.15", {"start": v(24.01, -7.05) * mm, "end": v(20.86, -7.05) * mm});
            skLineSegment(sketch, "E14.14.10.15", {"start": v(20.86, -7.05) * mm, "end": v(19.28, -4.32) * mm});
            skLineSegment(sketch, "E14.17.10.15", {"start": v(19.28, -4.32) * mm, "end": v(20.86, -1.59) * mm});
            skLineSegment(sketch, "E14.0.10.16", {"start": v(20.86, 7.05) * mm, "end": v(24.01, 7.05) * mm});
            skLineSegment(sketch, "E14.3.10.16", {"start": v(24.01, 7.05) * mm, "end": v(25.6, 4.32) * mm});
            skLineSegment(sketch, "E14.6.10.16", {"start": v(25.6, 4.32) * mm, "end": v(24.01, 1.59) * mm});
            skCircle(sketch, "E14.9.10.16", {"center": v(22.44, 4.32) * mm, "radius": 2.73 * mm, "construction": true});
            skLineSegment(sketch, "E14.11.10.16", {"start": v(24.01, 1.59) * mm, "end": v(20.86, 1.59) * mm});
            skLineSegment(sketch, "E14.14.10.16", {"start": v(20.86, 1.59) * mm, "end": v(19.28, 4.32) * mm});
            skLineSegment(sketch, "E14.17.10.16", {"start": v(19.28, 4.32) * mm, "end": v(20.86, 7.05) * mm});
            skLineSegment(sketch, "E14.0.10.17", {"start": v(20.86, 15.68) * mm, "end": v(24.01, 15.68) * mm});
            skLineSegment(sketch, "E14.3.10.17", {"start": v(24.01, 15.68) * mm, "end": v(25.6, 12.95) * mm});
            skLineSegment(sketch, "E14.6.10.17", {"start": v(25.6, 12.95) * mm, "end": v(24.01, 10.22) * mm});
            skCircle(sketch, "E14.9.10.17", {"center": v(22.44, 12.95) * mm, "radius": 2.73 * mm, "construction": true});
            skLineSegment(sketch, "E14.11.10.17", {"start": v(24.01, 10.22) * mm, "end": v(20.86, 10.22) * mm});
            skLineSegment(sketch, "E14.14.10.17", {"start": v(20.86, 10.22) * mm, "end": v(19.28, 12.95) * mm});
            skLineSegment(sketch, "E14.17.10.17", {"start": v(19.28, 12.95) * mm, "end": v(20.86, 15.68) * mm});
            skLineSegment(sketch, "E14.0.10.18", {"start": v(20.86, 24.32) * mm, "end": v(24.01, 24.32) * mm});
            skLineSegment(sketch, "E14.3.10.18", {"start": v(24.01, 24.32) * mm, "end": v(25.6, 21.59) * mm});
            skLineSegment(sketch, "E14.6.10.18", {"start": v(25.6, 21.59) * mm, "end": v(24.01, 18.86) * mm});
            skCircle(sketch, "E14.9.10.18", {"center": v(22.44, 21.59) * mm, "radius": 2.73 * mm, "construction": true});
            skLineSegment(sketch, "E14.11.10.18", {"start": v(24.01, 18.86) * mm, "end": v(20.86, 18.86) * mm});
            skLineSegment(sketch, "E14.14.10.18", {"start": v(20.86, 18.86) * mm, "end": v(19.28, 21.59) * mm});
            skLineSegment(sketch, "E14.17.10.18", {"start": v(19.28, 21.6) * mm, "end": v(20.86, 24.32) * mm});
            skLineSegment(sketch, "E14.0.10.19", {"start": v(20.86, 32.96) * mm, "end": v(24.01, 32.96) * mm});
            skLineSegment(sketch, "E14.3.10.19", {"start": v(24.01, 32.96) * mm, "end": v(25.6, 30.23) * mm});
            skLineSegment(sketch, "E14.6.10.19", {"start": v(25.6, 30.23) * mm, "end": v(24.01, 27.5) * mm});
            skCircle(sketch, "E14.9.10.19", {"center": v(22.44, 30.23) * mm, "radius": 2.73 * mm, "construction": true});
            skLineSegment(sketch, "E14.11.10.19", {"start": v(24.01, 27.5) * mm, "end": v(20.86, 27.5) * mm});
            skLineSegment(sketch, "E14.14.10.19", {"start": v(20.86, 27.5) * mm, "end": v(19.28, 30.23) * mm});
            skLineSegment(sketch, "E14.17.10.19", {"start": v(19.28, 30.23) * mm, "end": v(20.86, 32.96) * mm});
            skLineSegment(sketch, "E14.0.11.0", {"start": v(35.82, -131.13) * mm, "end": v(38.97, -131.13) * mm});
            skLineSegment(sketch, "E14.3.11.0", {"start": v(38.97, -131.13) * mm, "end": v(40.55, -133.86) * mm});
            skLineSegment(sketch, "E14.6.11.0", {"start": v(40.55, -133.86) * mm, "end": v(38.97, -136.59) * mm});
            skCircle(sketch, "E14.9.11.0", {"center": v(37.4, -133.86) * mm, "radius": 2.73 * mm, "construction": true});
            skLineSegment(sketch, "E14.11.11.0", {"start": v(38.97, -136.59) * mm, "end": v(35.82, -136.59) * mm});
            skLineSegment(sketch, "E14.14.11.0", {"start": v(35.82, -136.59) * mm, "end": v(34.24, -133.86) * mm});
            skLineSegment(sketch, "E14.17.11.0", {"start": v(34.24, -133.86) * mm, "end": v(35.82, -131.13) * mm});
            skLineSegment(sketch, "E14.0.11.1", {"start": v(35.82, -122.5) * mm, "end": v(38.97, -122.5) * mm});
            skLineSegment(sketch, "E14.3.11.1", {"start": v(38.97, -122.5) * mm, "end": v(40.55, -125.22) * mm});
            skLineSegment(sketch, "E14.6.11.1", {"start": v(40.55, -125.22) * mm, "end": v(38.97, -127.95) * mm});
            skCircle(sketch, "E14.9.11.1", {"center": v(37.4, -125.22) * mm, "radius": 2.73 * mm, "construction": true});
            skLineSegment(sketch, "E14.11.11.1", {"start": v(38.97, -127.95) * mm, "end": v(35.82, -127.95) * mm});
            skLineSegment(sketch, "E14.14.11.1", {"start": v(35.82, -127.95) * mm, "end": v(34.24, -125.22) * mm});
            skLineSegment(sketch, "E14.17.11.1", {"start": v(34.24, -125.22) * mm, "end": v(35.82, -122.5) * mm});
            skLineSegment(sketch, "E14.0.11.2", {"start": v(35.82, -113.86) * mm, "end": v(38.97, -113.86) * mm});
            skLineSegment(sketch, "E14.3.11.2", {"start": v(38.97, -113.86) * mm, "end": v(40.55, -116.59) * mm});
            skLineSegment(sketch, "E14.6.11.2", {"start": v(40.55, -116.59) * mm, "end": v(38.97, -119.32) * mm});
            skCircle(sketch, "E14.9.11.2", {"center": v(37.4, -116.59) * mm, "radius": 2.73 * mm, "construction": true});
            skLineSegment(sketch, "E14.11.11.2", {"start": v(38.97, -119.32) * mm, "end": v(35.82, -119.32) * mm});
            skLineSegment(sketch, "E14.14.11.2", {"start": v(35.82, -119.32) * mm, "end": v(34.24, -116.59) * mm});
            skLineSegment(sketch, "E14.17.11.2", {"start": v(34.24, -116.59) * mm, "end": v(35.82, -113.86) * mm});
            skLineSegment(sketch, "E14.0.11.3", {"start": v(35.82, -105.22) * mm, "end": v(38.97, -105.22) * mm});
            skLineSegment(sketch, "E14.3.11.3", {"start": v(38.97, -105.22) * mm, "end": v(40.55, -107.95) * mm});
            skLineSegment(sketch, "E14.6.11.3", {"start": v(40.55, -107.95) * mm, "end": v(38.97, -110.68) * mm});
            skCircle(sketch, "E14.9.11.3", {"center": v(37.4, -107.95) * mm, "radius": 2.73 * mm, "construction": true});
            skLineSegment(sketch, "E14.11.11.3", {"start": v(38.97, -110.68) * mm, "end": v(35.82, -110.68) * mm});
            skLineSegment(sketch, "E14.14.11.3", {"start": v(35.82, -110.68) * mm, "end": v(34.24, -107.95) * mm});
            skLineSegment(sketch, "E14.17.11.3", {"start": v(34.24, -107.95) * mm, "end": v(35.82, -105.22) * mm});
            skLineSegment(sketch, "E14.0.11.4", {"start": v(35.82, -96.58) * mm, "end": v(38.97, -96.58) * mm});
            skLineSegment(sketch, "E14.3.11.4", {"start": v(38.97, -96.58) * mm, "end": v(40.55, -99.31) * mm});
            skLineSegment(sketch, "E14.6.11.4", {"start": v(40.55, -99.31) * mm, "end": v(38.97, -102.04) * mm});
            skCircle(sketch, "E14.9.11.4", {"center": v(37.4, -99.31) * mm, "radius": 2.73 * mm, "construction": true});
            skLineSegment(sketch, "E14.11.11.4", {"start": v(38.97, -102.04) * mm, "end": v(35.82, -102.04) * mm});
            skLineSegment(sketch, "E14.14.11.4", {"start": v(35.82, -102.04) * mm, "end": v(34.24, -99.31) * mm});
            skLineSegment(sketch, "E14.17.11.4", {"start": v(34.24, -99.31) * mm, "end": v(35.82, -96.58) * mm});
            skLineSegment(sketch, "E14.0.11.5", {"start": v(35.82, -87.95) * mm, "end": v(38.97, -87.95) * mm});
            skLineSegment(sketch, "E14.3.11.5", {"start": v(38.97, -87.95) * mm, "end": v(40.55, -90.68) * mm});
            skLineSegment(sketch, "E14.6.11.5", {"start": v(40.55, -90.68) * mm, "end": v(38.97, -93.4) * mm});
            skCircle(sketch, "E14.9.11.5", {"center": v(37.4, -90.68) * mm, "radius": 2.73 * mm, "construction": true});
            skLineSegment(sketch, "E14.11.11.5", {"start": v(38.97, -93.4) * mm, "end": v(35.82, -93.4) * mm});
            skLineSegment(sketch, "E14.14.11.5", {"start": v(35.82, -93.4) * mm, "end": v(34.24, -90.68) * mm});
            skLineSegment(sketch, "E14.17.11.5", {"start": v(34.24, -90.68) * mm, "end": v(35.82, -87.95) * mm});
            skLineSegment(sketch, "E14.0.11.6", {"start": v(35.82, -79.31) * mm, "end": v(38.97, -79.31) * mm});
            skLineSegment(sketch, "E14.3.11.6", {"start": v(38.97, -79.31) * mm, "end": v(40.55, -82.04) * mm});
            skLineSegment(sketch, "E14.6.11.6", {"start": v(40.55, -82.04) * mm, "end": v(38.97, -84.77) * mm});
            skCircle(sketch, "E14.9.11.6", {"center": v(37.4, -82.04) * mm, "radius": 2.73 * mm, "construction": true});
            skLineSegment(sketch, "E14.11.11.6", {"start": v(38.97, -84.77) * mm, "end": v(35.82, -84.77) * mm});
            skLineSegment(sketch, "E14.14.11.6", {"start": v(35.82, -84.77) * mm, "end": v(34.24, -82.04) * mm});
            skLineSegment(sketch, "E14.17.11.6", {"start": v(34.24, -82.04) * mm, "end": v(35.82, -79.31) * mm});
            skLineSegment(sketch, "E14.0.11.7", {"start": v(35.82, -70.68) * mm, "end": v(38.97, -70.68) * mm});
            skLineSegment(sketch, "E14.3.11.7", {"start": v(38.97, -70.68) * mm, "end": v(40.55, -73.4) * mm});
            skLineSegment(sketch, "E14.6.11.7", {"start": v(40.55, -73.4) * mm, "end": v(38.97, -76.14) * mm});
            skCircle(sketch, "E14.9.11.7", {"center": v(37.4, -73.4) * mm, "radius": 2.73 * mm, "construction": true});
            skLineSegment(sketch, "E14.11.11.7", {"start": v(38.97, -76.14) * mm, "end": v(35.82, -76.14) * mm});
            skLineSegment(sketch, "E14.14.11.7", {"start": v(35.82, -76.14) * mm, "end": v(34.24, -73.4) * mm});
            skLineSegment(sketch, "E14.17.11.7", {"start": v(34.24, -73.4) * mm, "end": v(35.82, -70.68) * mm});
            skLineSegment(sketch, "E14.0.11.8", {"start": v(35.82, -62.04) * mm, "end": v(38.97, -62.04) * mm});
            skLineSegment(sketch, "E14.3.11.8", {"start": v(38.97, -62.04) * mm, "end": v(40.55, -64.77) * mm});
            skLineSegment(sketch, "E14.6.11.8", {"start": v(40.55, -64.77) * mm, "end": v(38.97, -67.5) * mm});
            skCircle(sketch, "E14.9.11.8", {"center": v(37.4, -64.77) * mm, "radius": 2.73 * mm, "construction": true});
            skLineSegment(sketch, "E14.11.11.8", {"start": v(38.97, -67.5) * mm, "end": v(35.82, -67.5) * mm});
            skLineSegment(sketch, "E14.14.11.8", {"start": v(35.82, -67.5) * mm, "end": v(34.24, -64.77) * mm});
            skLineSegment(sketch, "E14.17.11.8", {"start": v(34.24, -64.77) * mm, "end": v(35.82, -62.04) * mm});
            skLineSegment(sketch, "E14.0.11.9", {"start": v(35.82, -53.4) * mm, "end": v(38.97, -53.4) * mm});
            skLineSegment(sketch, "E14.3.11.9", {"start": v(38.97, -53.4) * mm, "end": v(40.55, -56.13) * mm});
            skLineSegment(sketch, "E14.6.11.9", {"start": v(40.55, -56.13) * mm, "end": v(38.97, -58.86) * mm});
            skCircle(sketch, "E14.9.11.9", {"center": v(37.4, -56.13) * mm, "radius": 2.73 * mm, "construction": true});
            skLineSegment(sketch, "E14.11.11.9", {"start": v(38.97, -58.86) * mm, "end": v(35.82, -58.86) * mm});
            skLineSegment(sketch, "E14.14.11.9", {"start": v(35.82, -58.86) * mm, "end": v(34.24, -56.13) * mm});
            skLineSegment(sketch, "E14.17.11.9", {"start": v(34.24, -56.13) * mm, "end": v(35.82, -53.4) * mm});
            skLineSegment(sketch, "E14.0.11.10", {"start": v(35.82, -44.77) * mm, "end": v(38.97, -44.77) * mm});
            skLineSegment(sketch, "E14.3.11.10", {"start": v(38.97, -44.77) * mm, "end": v(40.55, -47.5) * mm});
            skLineSegment(sketch, "E14.6.11.10", {"start": v(40.55, -47.5) * mm, "end": v(38.97, -50.23) * mm});
            skCircle(sketch, "E14.9.11.10", {"center": v(37.4, -47.5) * mm, "radius": 2.73 * mm, "construction": true});
            skLineSegment(sketch, "E14.11.11.10", {"start": v(38.97, -50.23) * mm, "end": v(35.82, -50.23) * mm});
            skLineSegment(sketch, "E14.14.11.10", {"start": v(35.82, -50.23) * mm, "end": v(34.24, -47.5) * mm});
            skLineSegment(sketch, "E14.17.11.10", {"start": v(34.24, -47.5) * mm, "end": v(35.82, -44.77) * mm});
            skLineSegment(sketch, "E14.0.11.11", {"start": v(35.82, -36.13) * mm, "end": v(38.97, -36.13) * mm});
            skLineSegment(sketch, "E14.3.11.11", {"start": v(38.97, -36.13) * mm, "end": v(40.55, -38.86) * mm});
            skLineSegment(sketch, "E14.6.11.11", {"start": v(40.55, -38.86) * mm, "end": v(38.97, -41.6) * mm});
            skCircle(sketch, "E14.9.11.11", {"center": v(37.4, -38.86) * mm, "radius": 2.73 * mm, "construction": true});
            skLineSegment(sketch, "E14.11.11.11", {"start": v(38.97, -41.6) * mm, "end": v(35.82, -41.6) * mm});
            skLineSegment(sketch, "E14.14.11.11", {"start": v(35.82, -41.6) * mm, "end": v(34.24, -38.86) * mm});
            skLineSegment(sketch, "E14.17.11.11", {"start": v(34.24, -38.86) * mm, "end": v(35.82, -36.13) * mm});
            skLineSegment(sketch, "E14.0.11.12", {"start": v(35.82, -27.5) * mm, "end": v(38.97, -27.5) * mm});
            skLineSegment(sketch, "E14.3.11.12", {"start": v(38.97, -27.5) * mm, "end": v(40.55, -30.23) * mm});
            skLineSegment(sketch, "E14.6.11.12", {"start": v(40.55, -30.23) * mm, "end": v(38.97, -32.96) * mm});
            skCircle(sketch, "E14.9.11.12", {"center": v(37.4, -30.23) * mm, "radius": 2.73 * mm, "construction": true});
            skLineSegment(sketch, "E14.11.11.12", {"start": v(38.97, -32.96) * mm, "end": v(35.82, -32.96) * mm});
            skLineSegment(sketch, "E14.14.11.12", {"start": v(35.82, -32.96) * mm, "end": v(34.24, -30.23) * mm});
            skLineSegment(sketch, "E14.17.11.12", {"start": v(34.24, -30.23) * mm, "end": v(35.82, -27.5) * mm});
            skLineSegment(sketch, "E14.0.11.13", {"start": v(35.82, -18.86) * mm, "end": v(38.97, -18.86) * mm});
            skLineSegment(sketch, "E14.3.11.13", {"start": v(38.97, -18.86) * mm, "end": v(40.55, -21.6) * mm});
            skLineSegment(sketch, "E14.6.11.13", {"start": v(40.55, -21.6) * mm, "end": v(38.97, -24.32) * mm});
            skCircle(sketch, "E14.9.11.13", {"center": v(37.4, -21.6) * mm, "radius": 2.73 * mm, "construction": true});
            skLineSegment(sketch, "E14.11.11.13", {"start": v(38.97, -24.32) * mm, "end": v(35.82, -24.32) * mm});
            skLineSegment(sketch, "E14.14.11.13", {"start": v(35.82, -24.32) * mm, "end": v(34.24, -21.6) * mm});
            skLineSegment(sketch, "E14.17.11.13", {"start": v(34.24, -21.6) * mm, "end": v(35.82, -18.86) * mm});
            skLineSegment(sketch, "E14.0.11.14", {"start": v(35.82, -10.22) * mm, "end": v(38.97, -10.22) * mm});
            skLineSegment(sketch, "E14.3.11.14", {"start": v(38.97, -10.22) * mm, "end": v(40.55, -12.95) * mm});
            skLineSegment(sketch, "E14.6.11.14", {"start": v(40.55, -12.95) * mm, "end": v(38.97, -15.68) * mm});
            skCircle(sketch, "E14.9.11.14", {"center": v(37.4, -12.95) * mm, "radius": 2.73 * mm, "construction": true});
            skLineSegment(sketch, "E14.11.11.14", {"start": v(38.97, -15.68) * mm, "end": v(35.82, -15.68) * mm});
            skLineSegment(sketch, "E14.14.11.14", {"start": v(35.82, -15.68) * mm, "end": v(34.24, -12.95) * mm});
            skLineSegment(sketch, "E14.17.11.14", {"start": v(34.24, -12.95) * mm, "end": v(35.82, -10.22) * mm});
            skLineSegment(sketch, "E14.0.11.15", {"start": v(35.82, -1.59) * mm, "end": v(38.97, -1.59) * mm});
            skLineSegment(sketch, "E14.3.11.15", {"start": v(38.97, -1.59) * mm, "end": v(40.55, -4.32) * mm});
            skLineSegment(sketch, "E14.6.11.15", {"start": v(40.55, -4.32) * mm, "end": v(38.97, -7.05) * mm});
            skCircle(sketch, "E14.9.11.15", {"center": v(37.4, -4.32) * mm, "radius": 2.73 * mm, "construction": true});
            skLineSegment(sketch, "E14.11.11.15", {"start": v(38.97, -7.05) * mm, "end": v(35.82, -7.05) * mm});
            skLineSegment(sketch, "E14.14.11.15", {"start": v(35.82, -7.05) * mm, "end": v(34.24, -4.32) * mm});
            skLineSegment(sketch, "E14.17.11.15", {"start": v(34.24, -4.32) * mm, "end": v(35.82, -1.59) * mm});
            skLineSegment(sketch, "E14.0.11.16", {"start": v(35.82, 7.05) * mm, "end": v(38.97, 7.05) * mm});
            skLineSegment(sketch, "E14.3.11.16", {"start": v(38.97, 7.05) * mm, "end": v(40.55, 4.32) * mm});
            skLineSegment(sketch, "E14.6.11.16", {"start": v(40.55, 4.32) * mm, "end": v(38.97, 1.59) * mm});
            skCircle(sketch, "E14.9.11.16", {"center": v(37.4, 4.32) * mm, "radius": 2.73 * mm, "construction": true});
            skLineSegment(sketch, "E14.11.11.16", {"start": v(38.97, 1.59) * mm, "end": v(35.82, 1.59) * mm});
            skLineSegment(sketch, "E14.14.11.16", {"start": v(35.82, 1.59) * mm, "end": v(34.24, 4.32) * mm});
            skLineSegment(sketch, "E14.17.11.16", {"start": v(34.24, 4.32) * mm, "end": v(35.82, 7.05) * mm});
            skLineSegment(sketch, "E14.0.11.17", {"start": v(35.82, 15.68) * mm, "end": v(38.97, 15.68) * mm});
            skLineSegment(sketch, "E14.3.11.17", {"start": v(38.97, 15.68) * mm, "end": v(40.55, 12.95) * mm});
            skLineSegment(sketch, "E14.6.11.17", {"start": v(40.55, 12.95) * mm, "end": v(38.97, 10.22) * mm});
            skCircle(sketch, "E14.9.11.17", {"center": v(37.4, 12.95) * mm, "radius": 2.73 * mm, "construction": true});
            skLineSegment(sketch, "E14.11.11.17", {"start": v(38.97, 10.22) * mm, "end": v(35.82, 10.22) * mm});
            skLineSegment(sketch, "E14.14.11.17", {"start": v(35.82, 10.22) * mm, "end": v(34.24, 12.95) * mm});
            skLineSegment(sketch, "E14.17.11.17", {"start": v(34.24, 12.95) * mm, "end": v(35.82, 15.68) * mm});
            skLineSegment(sketch, "E14.0.11.18", {"start": v(35.82, 24.32) * mm, "end": v(38.97, 24.32) * mm});
            skLineSegment(sketch, "E14.3.11.18", {"start": v(38.97, 24.32) * mm, "end": v(40.55, 21.59) * mm});
            skLineSegment(sketch, "E14.6.11.18", {"start": v(40.55, 21.59) * mm, "end": v(38.97, 18.86) * mm});
            skCircle(sketch, "E14.9.11.18", {"center": v(37.4, 21.59) * mm, "radius": 2.73 * mm, "construction": true});
            skLineSegment(sketch, "E14.11.11.18", {"start": v(38.97, 18.86) * mm, "end": v(35.82, 18.86) * mm});
            skLineSegment(sketch, "E14.14.11.18", {"start": v(35.82, 18.86) * mm, "end": v(34.24, 21.59) * mm});
            skLineSegment(sketch, "E14.17.11.18", {"start": v(34.24, 21.59) * mm, "end": v(35.82, 24.32) * mm});
            skLineSegment(sketch, "E14.0.11.19", {"start": v(35.82, 32.96) * mm, "end": v(38.97, 32.96) * mm});
            skLineSegment(sketch, "E14.3.11.19", {"start": v(38.97, 32.96) * mm, "end": v(40.55, 30.23) * mm});
            skLineSegment(sketch, "E14.6.11.19", {"start": v(40.55, 30.23) * mm, "end": v(38.97, 27.5) * mm});
            skCircle(sketch, "E14.9.11.19", {"center": v(37.4, 30.23) * mm, "radius": 2.73 * mm, "construction": true});
            skLineSegment(sketch, "E14.11.11.19", {"start": v(38.97, 27.5) * mm, "end": v(35.82, 27.5) * mm});
            skLineSegment(sketch, "E14.14.11.19", {"start": v(35.82, 27.5) * mm, "end": v(34.24, 30.23) * mm});
            skLineSegment(sketch, "E14.17.11.19", {"start": v(34.24, 30.23) * mm, "end": v(35.82, 32.96) * mm});
            skLineSegment(sketch, "E14.0.12.0", {"start": v(50.78, -131.13) * mm, "end": v(53.93, -131.13) * mm});
            skLineSegment(sketch, "E14.3.12.0", {"start": v(53.93, -131.13) * mm, "end": v(55.5, -133.86) * mm});
            skLineSegment(sketch, "E14.6.12.0", {"start": v(55.5, -133.86) * mm, "end": v(53.93, -136.59) * mm});
            skCircle(sketch, "E14.9.12.0", {"center": v(52.35, -133.86) * mm, "radius": 2.73 * mm, "construction": true});
            skLineSegment(sketch, "E14.11.12.0", {"start": v(53.93, -136.59) * mm, "end": v(50.78, -136.59) * mm});
            skLineSegment(sketch, "E14.14.12.0", {"start": v(50.78, -136.59) * mm, "end": v(49.2, -133.86) * mm});
            skLineSegment(sketch, "E14.17.12.0", {"start": v(49.2, -133.86) * mm, "end": v(50.78, -131.13) * mm});
            skLineSegment(sketch, "E14.0.12.1", {"start": v(50.78, -122.5) * mm, "end": v(53.93, -122.5) * mm});
            skLineSegment(sketch, "E14.3.12.1", {"start": v(53.93, -122.5) * mm, "end": v(55.5, -125.22) * mm});
            skLineSegment(sketch, "E14.6.12.1", {"start": v(55.5, -125.22) * mm, "end": v(53.93, -127.95) * mm});
            skCircle(sketch, "E14.9.12.1", {"center": v(52.35, -125.22) * mm, "radius": 2.73 * mm, "construction": true});
            skLineSegment(sketch, "E14.11.12.1", {"start": v(53.93, -127.95) * mm, "end": v(50.78, -127.95) * mm});
            skLineSegment(sketch, "E14.14.12.1", {"start": v(50.78, -127.95) * mm, "end": v(49.2, -125.22) * mm});
            skLineSegment(sketch, "E14.17.12.1", {"start": v(49.2, -125.22) * mm, "end": v(50.78, -122.5) * mm});
            skLineSegment(sketch, "E14.0.12.2", {"start": v(50.78, -113.86) * mm, "end": v(53.93, -113.86) * mm});
            skLineSegment(sketch, "E14.3.12.2", {"start": v(53.93, -113.86) * mm, "end": v(55.5, -116.59) * mm});
            skLineSegment(sketch, "E14.6.12.2", {"start": v(55.5, -116.59) * mm, "end": v(53.93, -119.32) * mm});
            skCircle(sketch, "E14.9.12.2", {"center": v(52.35, -116.59) * mm, "radius": 2.73 * mm, "construction": true});
            skLineSegment(sketch, "E14.11.12.2", {"start": v(53.93, -119.32) * mm, "end": v(50.78, -119.32) * mm});
            skLineSegment(sketch, "E14.14.12.2", {"start": v(50.78, -119.32) * mm, "end": v(49.2, -116.59) * mm});
            skLineSegment(sketch, "E14.17.12.2", {"start": v(49.2, -116.59) * mm, "end": v(50.78, -113.86) * mm});
            skLineSegment(sketch, "E14.0.12.3", {"start": v(50.78, -105.22) * mm, "end": v(53.93, -105.22) * mm});
            skLineSegment(sketch, "E14.3.12.3", {"start": v(53.93, -105.22) * mm, "end": v(55.5, -107.95) * mm});
            skLineSegment(sketch, "E14.6.12.3", {"start": v(55.5, -107.95) * mm, "end": v(53.93, -110.68) * mm});
            skCircle(sketch, "E14.9.12.3", {"center": v(52.35, -107.95) * mm, "radius": 2.73 * mm, "construction": true});
            skLineSegment(sketch, "E14.11.12.3", {"start": v(53.93, -110.68) * mm, "end": v(50.78, -110.68) * mm});
            skLineSegment(sketch, "E14.14.12.3", {"start": v(50.78, -110.68) * mm, "end": v(49.2, -107.95) * mm});
            skLineSegment(sketch, "E14.17.12.3", {"start": v(49.2, -107.95) * mm, "end": v(50.78, -105.22) * mm});
            skLineSegment(sketch, "E14.0.12.4", {"start": v(50.78, -96.58) * mm, "end": v(53.93, -96.58) * mm});
            skLineSegment(sketch, "E14.3.12.4", {"start": v(53.93, -96.58) * mm, "end": v(55.5, -99.31) * mm});
            skLineSegment(sketch, "E14.6.12.4", {"start": v(55.5, -99.31) * mm, "end": v(53.93, -102.04) * mm});
            skCircle(sketch, "E14.9.12.4", {"center": v(52.35, -99.31) * mm, "radius": 2.73 * mm, "construction": true});
            skLineSegment(sketch, "E14.11.12.4", {"start": v(53.93, -102.04) * mm, "end": v(50.78, -102.04) * mm});
            skLineSegment(sketch, "E14.14.12.4", {"start": v(50.78, -102.04) * mm, "end": v(49.2, -99.31) * mm});
            skLineSegment(sketch, "E14.17.12.4", {"start": v(49.2, -99.31) * mm, "end": v(50.78, -96.58) * mm});
            skLineSegment(sketch, "E14.0.12.5", {"start": v(50.78, -87.95) * mm, "end": v(53.93, -87.95) * mm});
            skLineSegment(sketch, "E14.3.12.5", {"start": v(53.93, -87.95) * mm, "end": v(55.5, -90.68) * mm});
            skLineSegment(sketch, "E14.6.12.5", {"start": v(55.5, -90.68) * mm, "end": v(53.93, -93.4) * mm});
            skCircle(sketch, "E14.9.12.5", {"center": v(52.35, -90.68) * mm, "radius": 2.73 * mm, "construction": true});
            skLineSegment(sketch, "E14.11.12.5", {"start": v(53.93, -93.4) * mm, "end": v(50.78, -93.4) * mm});
            skLineSegment(sketch, "E14.14.12.5", {"start": v(50.78, -93.4) * mm, "end": v(49.2, -90.68) * mm});
            skLineSegment(sketch, "E14.17.12.5", {"start": v(49.2, -90.68) * mm, "end": v(50.78, -87.95) * mm});
            skLineSegment(sketch, "E14.0.12.6", {"start": v(50.78, -79.31) * mm, "end": v(53.93, -79.31) * mm});
            skLineSegment(sketch, "E14.3.12.6", {"start": v(53.93, -79.31) * mm, "end": v(55.5, -82.04) * mm});
            skLineSegment(sketch, "E14.6.12.6", {"start": v(55.5, -82.04) * mm, "end": v(53.93, -84.77) * mm});
            skCircle(sketch, "E14.9.12.6", {"center": v(52.35, -82.04) * mm, "radius": 2.73 * mm, "construction": true});
            skLineSegment(sketch, "E14.11.12.6", {"start": v(53.93, -84.77) * mm, "end": v(50.78, -84.77) * mm});
            skLineSegment(sketch, "E14.14.12.6", {"start": v(50.78, -84.77) * mm, "end": v(49.2, -82.04) * mm});
            skLineSegment(sketch, "E14.17.12.6", {"start": v(49.2, -82.04) * mm, "end": v(50.78, -79.31) * mm});
            skLineSegment(sketch, "E14.0.12.7", {"start": v(50.78, -70.68) * mm, "end": v(53.93, -70.68) * mm});
            skLineSegment(sketch, "E14.3.12.7", {"start": v(53.93, -70.68) * mm, "end": v(55.5, -73.4) * mm});
            skLineSegment(sketch, "E14.6.12.7", {"start": v(55.5, -73.4) * mm, "end": v(53.93, -76.14) * mm});
            skCircle(sketch, "E14.9.12.7", {"center": v(52.35, -73.4) * mm, "radius": 2.73 * mm, "construction": true});
            skLineSegment(sketch, "E14.11.12.7", {"start": v(53.93, -76.14) * mm, "end": v(50.78, -76.14) * mm});
            skLineSegment(sketch, "E14.14.12.7", {"start": v(50.78, -76.14) * mm, "end": v(49.2, -73.4) * mm});
            skLineSegment(sketch, "E14.17.12.7", {"start": v(49.2, -73.4) * mm, "end": v(50.78, -70.68) * mm});
            skLineSegment(sketch, "E14.0.12.8", {"start": v(50.78, -62.04) * mm, "end": v(53.93, -62.04) * mm});
            skLineSegment(sketch, "E14.3.12.8", {"start": v(53.93, -62.04) * mm, "end": v(55.5, -64.77) * mm});
            skLineSegment(sketch, "E14.6.12.8", {"start": v(55.5, -64.77) * mm, "end": v(53.93, -67.5) * mm});
            skCircle(sketch, "E14.9.12.8", {"center": v(52.35, -64.77) * mm, "radius": 2.73 * mm, "construction": true});
            skLineSegment(sketch, "E14.11.12.8", {"start": v(53.93, -67.5) * mm, "end": v(50.78, -67.5) * mm});
            skLineSegment(sketch, "E14.14.12.8", {"start": v(50.78, -67.5) * mm, "end": v(49.2, -64.77) * mm});
            skLineSegment(sketch, "E14.17.12.8", {"start": v(49.2, -64.77) * mm, "end": v(50.78, -62.04) * mm});
            skLineSegment(sketch, "E14.0.12.9", {"start": v(50.78, -53.4) * mm, "end": v(53.93, -53.4) * mm});
            skLineSegment(sketch, "E14.3.12.9", {"start": v(53.93, -53.4) * mm, "end": v(55.5, -56.13) * mm});
            skLineSegment(sketch, "E14.6.12.9", {"start": v(55.5, -56.13) * mm, "end": v(53.93, -58.86) * mm});
            skCircle(sketch, "E14.9.12.9", {"center": v(52.35, -56.13) * mm, "radius": 2.73 * mm, "construction": true});
            skLineSegment(sketch, "E14.11.12.9", {"start": v(53.93, -58.86) * mm, "end": v(50.78, -58.86) * mm});
            skLineSegment(sketch, "E14.14.12.9", {"start": v(50.78, -58.86) * mm, "end": v(49.2, -56.13) * mm});
            skLineSegment(sketch, "E14.17.12.9", {"start": v(49.2, -56.13) * mm, "end": v(50.78, -53.4) * mm});
            skLineSegment(sketch, "E14.0.12.10", {"start": v(50.78, -44.77) * mm, "end": v(53.93, -44.77) * mm});
            skLineSegment(sketch, "E14.3.12.10", {"start": v(53.93, -44.77) * mm, "end": v(55.5, -47.5) * mm});
            skLineSegment(sketch, "E14.6.12.10", {"start": v(55.5, -47.5) * mm, "end": v(53.93, -50.23) * mm});
            skCircle(sketch, "E14.9.12.10", {"center": v(52.35, -47.5) * mm, "radius": 2.73 * mm, "construction": true});
            skLineSegment(sketch, "E14.11.12.10", {"start": v(53.93, -50.23) * mm, "end": v(50.78, -50.23) * mm});
            skLineSegment(sketch, "E14.14.12.10", {"start": v(50.78, -50.23) * mm, "end": v(49.2, -47.5) * mm});
            skLineSegment(sketch, "E14.17.12.10", {"start": v(49.2, -47.5) * mm, "end": v(50.78, -44.77) * mm});
            skLineSegment(sketch, "E14.0.12.11", {"start": v(50.78, -36.13) * mm, "end": v(53.93, -36.13) * mm});
            skLineSegment(sketch, "E14.3.12.11", {"start": v(53.93, -36.13) * mm, "end": v(55.5, -38.86) * mm});
            skLineSegment(sketch, "E14.6.12.11", {"start": v(55.5, -38.86) * mm, "end": v(53.93, -41.6) * mm});
            skCircle(sketch, "E14.9.12.11", {"center": v(52.35, -38.86) * mm, "radius": 2.73 * mm, "construction": true});
            skLineSegment(sketch, "E14.11.12.11", {"start": v(53.93, -41.6) * mm, "end": v(50.78, -41.6) * mm});
            skLineSegment(sketch, "E14.14.12.11", {"start": v(50.78, -41.6) * mm, "end": v(49.2, -38.86) * mm});
            skLineSegment(sketch, "E14.17.12.11", {"start": v(49.2, -38.86) * mm, "end": v(50.78, -36.13) * mm});
            skLineSegment(sketch, "E14.0.12.12", {"start": v(50.78, -27.5) * mm, "end": v(53.93, -27.5) * mm});
            skLineSegment(sketch, "E14.3.12.12", {"start": v(53.93, -27.5) * mm, "end": v(55.5, -30.23) * mm});
            skLineSegment(sketch, "E14.6.12.12", {"start": v(55.5, -30.23) * mm, "end": v(53.93, -32.96) * mm});
            skCircle(sketch, "E14.9.12.12", {"center": v(52.35, -30.23) * mm, "radius": 2.73 * mm, "construction": true});
            skLineSegment(sketch, "E14.11.12.12", {"start": v(53.93, -32.96) * mm, "end": v(50.78, -32.96) * mm});
            skLineSegment(sketch, "E14.14.12.12", {"start": v(50.78, -32.96) * mm, "end": v(49.2, -30.23) * mm});
            skLineSegment(sketch, "E14.17.12.12", {"start": v(49.2, -30.23) * mm, "end": v(50.78, -27.5) * mm});
            skLineSegment(sketch, "E14.0.12.13", {"start": v(50.78, -18.86) * mm, "end": v(53.93, -18.86) * mm});
            skLineSegment(sketch, "E14.3.12.13", {"start": v(53.93, -18.86) * mm, "end": v(55.5, -21.6) * mm});
            skLineSegment(sketch, "E14.6.12.13", {"start": v(55.5, -21.6) * mm, "end": v(53.93, -24.32) * mm});
            skCircle(sketch, "E14.9.12.13", {"center": v(52.35, -21.6) * mm, "radius": 2.73 * mm, "construction": true});
            skLineSegment(sketch, "E14.11.12.13", {"start": v(53.93, -24.32) * mm, "end": v(50.78, -24.32) * mm});
            skLineSegment(sketch, "E14.14.12.13", {"start": v(50.78, -24.32) * mm, "end": v(49.2, -21.6) * mm});
            skLineSegment(sketch, "E14.17.12.13", {"start": v(49.2, -21.59) * mm, "end": v(50.78, -18.86) * mm});
            skLineSegment(sketch, "E14.0.12.14", {"start": v(50.78, -10.22) * mm, "end": v(53.93, -10.22) * mm});
            skLineSegment(sketch, "E14.3.12.14", {"start": v(53.93, -10.22) * mm, "end": v(55.5, -12.95) * mm});
            skLineSegment(sketch, "E14.6.12.14", {"start": v(55.5, -12.95) * mm, "end": v(53.93, -15.68) * mm});
            skCircle(sketch, "E14.9.12.14", {"center": v(52.35, -12.95) * mm, "radius": 2.73 * mm, "construction": true});
            skLineSegment(sketch, "E14.11.12.14", {"start": v(53.93, -15.68) * mm, "end": v(50.78, -15.68) * mm});
            skLineSegment(sketch, "E14.14.12.14", {"start": v(50.78, -15.68) * mm, "end": v(49.2, -12.95) * mm});
            skLineSegment(sketch, "E14.17.12.14", {"start": v(49.2, -12.95) * mm, "end": v(50.78, -10.22) * mm});
            skLineSegment(sketch, "E14.0.12.15", {"start": v(50.78, -1.59) * mm, "end": v(53.93, -1.59) * mm});
            skLineSegment(sketch, "E14.3.12.15", {"start": v(53.93, -1.59) * mm, "end": v(55.5, -4.32) * mm});
            skLineSegment(sketch, "E14.6.12.15", {"start": v(55.5, -4.32) * mm, "end": v(53.93, -7.05) * mm});
            skCircle(sketch, "E14.9.12.15", {"center": v(52.35, -4.32) * mm, "radius": 2.73 * mm, "construction": true});
            skLineSegment(sketch, "E14.11.12.15", {"start": v(53.93, -7.05) * mm, "end": v(50.78, -7.05) * mm});
            skLineSegment(sketch, "E14.14.12.15", {"start": v(50.78, -7.05) * mm, "end": v(49.2, -4.32) * mm});
            skLineSegment(sketch, "E14.17.12.15", {"start": v(49.2, -4.32) * mm, "end": v(50.78, -1.59) * mm});
            skLineSegment(sketch, "E14.0.12.16", {"start": v(50.78, 7.05) * mm, "end": v(53.93, 7.05) * mm});
            skLineSegment(sketch, "E14.3.12.16", {"start": v(53.93, 7.05) * mm, "end": v(55.5, 4.32) * mm});
            skLineSegment(sketch, "E14.6.12.16", {"start": v(55.5, 4.32) * mm, "end": v(53.93, 1.59) * mm});
            skCircle(sketch, "E14.9.12.16", {"center": v(52.35, 4.32) * mm, "radius": 2.73 * mm, "construction": true});
            skLineSegment(sketch, "E14.11.12.16", {"start": v(53.93, 1.59) * mm, "end": v(50.78, 1.59) * mm});
            skLineSegment(sketch, "E14.14.12.16", {"start": v(50.78, 1.59) * mm, "end": v(49.2, 4.32) * mm});
            skLineSegment(sketch, "E14.17.12.16", {"start": v(49.2, 4.32) * mm, "end": v(50.78, 7.05) * mm});
            skLineSegment(sketch, "E14.0.12.17", {"start": v(50.78, 15.68) * mm, "end": v(53.93, 15.68) * mm});
            skLineSegment(sketch, "E14.3.12.17", {"start": v(53.93, 15.68) * mm, "end": v(55.5, 12.95) * mm});
            skLineSegment(sketch, "E14.6.12.17", {"start": v(55.5, 12.95) * mm, "end": v(53.93, 10.22) * mm});
            skCircle(sketch, "E14.9.12.17", {"center": v(52.35, 12.95) * mm, "radius": 2.73 * mm, "construction": true});
            skLineSegment(sketch, "E14.11.12.17", {"start": v(53.93, 10.22) * mm, "end": v(50.78, 10.22) * mm});
            skLineSegment(sketch, "E14.14.12.17", {"start": v(50.78, 10.22) * mm, "end": v(49.2, 12.95) * mm});
            skLineSegment(sketch, "E14.17.12.17", {"start": v(49.2, 12.95) * mm, "end": v(50.78, 15.68) * mm});
            skLineSegment(sketch, "E14.0.12.18", {"start": v(50.78, 24.32) * mm, "end": v(53.93, 24.32) * mm});
            skLineSegment(sketch, "E14.3.12.18", {"start": v(53.93, 24.32) * mm, "end": v(55.5, 21.59) * mm});
            skLineSegment(sketch, "E14.6.12.18", {"start": v(55.5, 21.59) * mm, "end": v(53.93, 18.86) * mm});
            skCircle(sketch, "E14.9.12.18", {"center": v(52.35, 21.59) * mm, "radius": 2.73 * mm, "construction": true});
            skLineSegment(sketch, "E14.11.12.18", {"start": v(53.93, 18.86) * mm, "end": v(50.78, 18.86) * mm});
            skLineSegment(sketch, "E14.14.12.18", {"start": v(50.78, 18.86) * mm, "end": v(49.2, 21.59) * mm});
            skLineSegment(sketch, "E14.17.12.18", {"start": v(49.2, 21.6) * mm, "end": v(50.78, 24.32) * mm});
            skLineSegment(sketch, "E14.0.12.19", {"start": v(50.78, 32.96) * mm, "end": v(53.93, 32.96) * mm});
            skLineSegment(sketch, "E14.3.12.19", {"start": v(53.93, 32.96) * mm, "end": v(55.5, 30.23) * mm});
            skLineSegment(sketch, "E14.6.12.19", {"start": v(55.5, 30.23) * mm, "end": v(53.93, 27.5) * mm});
            skCircle(sketch, "E14.9.12.19", {"center": v(52.35, 30.23) * mm, "radius": 2.73 * mm, "construction": true});
            skLineSegment(sketch, "E14.11.12.19", {"start": v(53.93, 27.5) * mm, "end": v(50.78, 27.5) * mm});
            skLineSegment(sketch, "E14.14.12.19", {"start": v(50.78, 27.5) * mm, "end": v(49.2, 30.23) * mm});
            skLineSegment(sketch, "E14.17.12.19", {"start": v(49.2, 30.23) * mm, "end": v(50.78, 32.96) * mm});
            skLineSegment(sketch, "E14.0.13.0", {"start": v(65.73, -131.13) * mm, "end": v(68.89, -131.13) * mm});
            skLineSegment(sketch, "E14.3.13.0", {"start": v(68.89, -131.13) * mm, "end": v(70.46, -133.86) * mm});
            skLineSegment(sketch, "E14.6.13.0", {"start": v(70.46, -133.86) * mm, "end": v(68.89, -136.59) * mm});
            skCircle(sketch, "E14.9.13.0", {"center": v(67.31, -133.86) * mm, "radius": 2.73 * mm, "construction": true});
            skLineSegment(sketch, "E14.11.13.0", {"start": v(68.89, -136.59) * mm, "end": v(65.73, -136.59) * mm});
            skLineSegment(sketch, "E14.14.13.0", {"start": v(65.73, -136.59) * mm, "end": v(64.16, -133.86) * mm});
            skLineSegment(sketch, "E14.17.13.0", {"start": v(64.16, -133.86) * mm, "end": v(65.73, -131.13) * mm});
            skLineSegment(sketch, "E14.0.13.1", {"start": v(65.73, -122.5) * mm, "end": v(68.89, -122.5) * mm});
            skLineSegment(sketch, "E14.3.13.1", {"start": v(68.89, -122.5) * mm, "end": v(70.46, -125.22) * mm});
            skLineSegment(sketch, "E14.6.13.1", {"start": v(70.46, -125.22) * mm, "end": v(68.89, -127.95) * mm});
            skCircle(sketch, "E14.9.13.1", {"center": v(67.31, -125.22) * mm, "radius": 2.73 * mm, "construction": true});
            skLineSegment(sketch, "E14.11.13.1", {"start": v(68.89, -127.95) * mm, "end": v(65.73, -127.95) * mm});
            skLineSegment(sketch, "E14.14.13.1", {"start": v(65.73, -127.95) * mm, "end": v(64.16, -125.22) * mm});
            skLineSegment(sketch, "E14.17.13.1", {"start": v(64.16, -125.22) * mm, "end": v(65.73, -122.5) * mm});
            skLineSegment(sketch, "E14.0.13.2", {"start": v(65.73, -113.86) * mm, "end": v(68.89, -113.86) * mm});
            skLineSegment(sketch, "E14.3.13.2", {"start": v(68.89, -113.86) * mm, "end": v(70.46, -116.59) * mm});
            skLineSegment(sketch, "E14.6.13.2", {"start": v(70.46, -116.59) * mm, "end": v(68.89, -119.32) * mm});
            skCircle(sketch, "E14.9.13.2", {"center": v(67.31, -116.59) * mm, "radius": 2.73 * mm, "construction": true});
            skLineSegment(sketch, "E14.11.13.2", {"start": v(68.89, -119.32) * mm, "end": v(65.73, -119.32) * mm});
            skLineSegment(sketch, "E14.14.13.2", {"start": v(65.73, -119.32) * mm, "end": v(64.16, -116.59) * mm});
            skLineSegment(sketch, "E14.17.13.2", {"start": v(64.16, -116.59) * mm, "end": v(65.73, -113.86) * mm});
            skLineSegment(sketch, "E14.0.13.3", {"start": v(65.73, -105.22) * mm, "end": v(68.89, -105.22) * mm});
            skLineSegment(sketch, "E14.3.13.3", {"start": v(68.89, -105.22) * mm, "end": v(70.46, -107.95) * mm});
            skLineSegment(sketch, "E14.6.13.3", {"start": v(70.46, -107.95) * mm, "end": v(68.89, -110.68) * mm});
            skCircle(sketch, "E14.9.13.3", {"center": v(67.31, -107.95) * mm, "radius": 2.73 * mm, "construction": true});
            skLineSegment(sketch, "E14.11.13.3", {"start": v(68.89, -110.68) * mm, "end": v(65.73, -110.68) * mm});
            skLineSegment(sketch, "E14.14.13.3", {"start": v(65.73, -110.68) * mm, "end": v(64.16, -107.95) * mm});
            skLineSegment(sketch, "E14.17.13.3", {"start": v(64.16, -107.95) * mm, "end": v(65.73, -105.22) * mm});
            skLineSegment(sketch, "E14.0.13.4", {"start": v(65.73, -96.58) * mm, "end": v(68.89, -96.58) * mm});
            skLineSegment(sketch, "E14.3.13.4", {"start": v(68.89, -96.58) * mm, "end": v(70.46, -99.31) * mm});
            skLineSegment(sketch, "E14.6.13.4", {"start": v(70.46, -99.31) * mm, "end": v(68.89, -102.04) * mm});
            skCircle(sketch, "E14.9.13.4", {"center": v(67.31, -99.31) * mm, "radius": 2.73 * mm, "construction": true});
            skLineSegment(sketch, "E14.11.13.4", {"start": v(68.89, -102.04) * mm, "end": v(65.73, -102.04) * mm});
            skLineSegment(sketch, "E14.14.13.4", {"start": v(65.73, -102.04) * mm, "end": v(64.16, -99.31) * mm});
            skLineSegment(sketch, "E14.17.13.4", {"start": v(64.16, -99.31) * mm, "end": v(65.73, -96.58) * mm});
            skLineSegment(sketch, "E14.0.13.5", {"start": v(65.73, -87.95) * mm, "end": v(68.89, -87.95) * mm});
            skLineSegment(sketch, "E14.3.13.5", {"start": v(68.89, -87.95) * mm, "end": v(70.46, -90.68) * mm});
            skLineSegment(sketch, "E14.6.13.5", {"start": v(70.46, -90.68) * mm, "end": v(68.89, -93.4) * mm});
            skCircle(sketch, "E14.9.13.5", {"center": v(67.31, -90.68) * mm, "radius": 2.73 * mm, "construction": true});
            skLineSegment(sketch, "E14.11.13.5", {"start": v(68.89, -93.4) * mm, "end": v(65.73, -93.4) * mm});
            skLineSegment(sketch, "E14.14.13.5", {"start": v(65.73, -93.4) * mm, "end": v(64.16, -90.68) * mm});
            skLineSegment(sketch, "E14.17.13.5", {"start": v(64.16, -90.68) * mm, "end": v(65.73, -87.95) * mm});
            skLineSegment(sketch, "E14.0.13.6", {"start": v(65.73, -79.31) * mm, "end": v(68.89, -79.31) * mm});
            skLineSegment(sketch, "E14.3.13.6", {"start": v(68.89, -79.31) * mm, "end": v(70.46, -82.04) * mm});
            skLineSegment(sketch, "E14.6.13.6", {"start": v(70.46, -82.04) * mm, "end": v(68.89, -84.77) * mm});
            skCircle(sketch, "E14.9.13.6", {"center": v(67.31, -82.04) * mm, "radius": 2.73 * mm, "construction": true});
            skLineSegment(sketch, "E14.11.13.6", {"start": v(68.89, -84.77) * mm, "end": v(65.73, -84.77) * mm});
            skLineSegment(sketch, "E14.14.13.6", {"start": v(65.73, -84.77) * mm, "end": v(64.16, -82.04) * mm});
            skLineSegment(sketch, "E14.17.13.6", {"start": v(64.16, -82.04) * mm, "end": v(65.73, -79.31) * mm});
            skLineSegment(sketch, "E14.0.13.7", {"start": v(65.73, -70.68) * mm, "end": v(68.89, -70.68) * mm});
            skLineSegment(sketch, "E14.3.13.7", {"start": v(68.89, -70.68) * mm, "end": v(70.46, -73.4) * mm});
            skLineSegment(sketch, "E14.6.13.7", {"start": v(70.46, -73.4) * mm, "end": v(68.89, -76.14) * mm});
            skCircle(sketch, "E14.9.13.7", {"center": v(67.31, -73.4) * mm, "radius": 2.73 * mm, "construction": true});
            skLineSegment(sketch, "E14.11.13.7", {"start": v(68.89, -76.14) * mm, "end": v(65.73, -76.14) * mm});
            skLineSegment(sketch, "E14.14.13.7", {"start": v(65.73, -76.14) * mm, "end": v(64.16, -73.4) * mm});
            skLineSegment(sketch, "E14.17.13.7", {"start": v(64.16, -73.4) * mm, "end": v(65.73, -70.68) * mm});
            skLineSegment(sketch, "E14.0.13.8", {"start": v(65.73, -62.04) * mm, "end": v(68.89, -62.04) * mm});
            skLineSegment(sketch, "E14.3.13.8", {"start": v(68.89, -62.04) * mm, "end": v(70.46, -64.77) * mm});
            skLineSegment(sketch, "E14.6.13.8", {"start": v(70.46, -64.77) * mm, "end": v(68.89, -67.5) * mm});
            skCircle(sketch, "E14.9.13.8", {"center": v(67.31, -64.77) * mm, "radius": 2.73 * mm, "construction": true});
            skLineSegment(sketch, "E14.11.13.8", {"start": v(68.89, -67.5) * mm, "end": v(65.73, -67.5) * mm});
            skLineSegment(sketch, "E14.14.13.8", {"start": v(65.73, -67.5) * mm, "end": v(64.16, -64.77) * mm});
            skLineSegment(sketch, "E14.17.13.8", {"start": v(64.16, -64.77) * mm, "end": v(65.73, -62.04) * mm});
            skLineSegment(sketch, "E14.0.13.9", {"start": v(65.73, -53.4) * mm, "end": v(68.89, -53.4) * mm});
            skLineSegment(sketch, "E14.3.13.9", {"start": v(68.89, -53.4) * mm, "end": v(70.46, -56.13) * mm});
            skLineSegment(sketch, "E14.6.13.9", {"start": v(70.46, -56.13) * mm, "end": v(68.89, -58.86) * mm});
            skCircle(sketch, "E14.9.13.9", {"center": v(67.31, -56.13) * mm, "radius": 2.73 * mm, "construction": true});
            skLineSegment(sketch, "E14.11.13.9", {"start": v(68.89, -58.86) * mm, "end": v(65.73, -58.86) * mm});
            skLineSegment(sketch, "E14.14.13.9", {"start": v(65.73, -58.86) * mm, "end": v(64.16, -56.13) * mm});
            skLineSegment(sketch, "E14.17.13.9", {"start": v(64.16, -56.13) * mm, "end": v(65.73, -53.4) * mm});
            skLineSegment(sketch, "E14.0.13.10", {"start": v(65.73, -44.77) * mm, "end": v(68.89, -44.77) * mm});
            skLineSegment(sketch, "E14.3.13.10", {"start": v(68.89, -44.77) * mm, "end": v(70.46, -47.5) * mm});
            skLineSegment(sketch, "E14.6.13.10", {"start": v(70.46, -47.5) * mm, "end": v(68.89, -50.23) * mm});
            skCircle(sketch, "E14.9.13.10", {"center": v(67.31, -47.5) * mm, "radius": 2.73 * mm, "construction": true});
            skLineSegment(sketch, "E14.11.13.10", {"start": v(68.89, -50.23) * mm, "end": v(65.73, -50.23) * mm});
            skLineSegment(sketch, "E14.14.13.10", {"start": v(65.73, -50.23) * mm, "end": v(64.16, -47.5) * mm});
            skLineSegment(sketch, "E14.17.13.10", {"start": v(64.16, -47.5) * mm, "end": v(65.73, -44.77) * mm});
            skLineSegment(sketch, "E14.0.13.11", {"start": v(65.73, -36.13) * mm, "end": v(68.89, -36.13) * mm});
            skLineSegment(sketch, "E14.3.13.11", {"start": v(68.89, -36.13) * mm, "end": v(70.46, -38.86) * mm});
            skLineSegment(sketch, "E14.6.13.11", {"start": v(70.46, -38.86) * mm, "end": v(68.89, -41.6) * mm});
            skCircle(sketch, "E14.9.13.11", {"center": v(67.31, -38.86) * mm, "radius": 2.73 * mm, "construction": true});
            skLineSegment(sketch, "E14.11.13.11", {"start": v(68.89, -41.6) * mm, "end": v(65.73, -41.6) * mm});
            skLineSegment(sketch, "E14.14.13.11", {"start": v(65.73, -41.6) * mm, "end": v(64.16, -38.86) * mm});
            skLineSegment(sketch, "E14.17.13.11", {"start": v(64.16, -38.86) * mm, "end": v(65.73, -36.13) * mm});
            skLineSegment(sketch, "E14.0.13.12", {"start": v(65.73, -27.5) * mm, "end": v(68.89, -27.5) * mm});
            skLineSegment(sketch, "E14.3.13.12", {"start": v(68.89, -27.5) * mm, "end": v(70.46, -30.23) * mm});
            skLineSegment(sketch, "E14.6.13.12", {"start": v(70.46, -30.23) * mm, "end": v(68.89, -32.96) * mm});
            skCircle(sketch, "E14.9.13.12", {"center": v(67.31, -30.23) * mm, "radius": 2.73 * mm, "construction": true});
            skLineSegment(sketch, "E14.11.13.12", {"start": v(68.89, -32.96) * mm, "end": v(65.73, -32.96) * mm});
            skLineSegment(sketch, "E14.14.13.12", {"start": v(65.73, -32.96) * mm, "end": v(64.16, -30.23) * mm});
            skLineSegment(sketch, "E14.17.13.12", {"start": v(64.16, -30.23) * mm, "end": v(65.73, -27.5) * mm});
            skLineSegment(sketch, "E14.0.13.13", {"start": v(65.73, -18.86) * mm, "end": v(68.89, -18.86) * mm});
            skLineSegment(sketch, "E14.3.13.13", {"start": v(68.89, -18.86) * mm, "end": v(70.46, -21.6) * mm});
            skLineSegment(sketch, "E14.6.13.13", {"start": v(70.46, -21.6) * mm, "end": v(68.89, -24.32) * mm});
            skCircle(sketch, "E14.9.13.13", {"center": v(67.31, -21.6) * mm, "radius": 2.73 * mm, "construction": true});
            skLineSegment(sketch, "E14.11.13.13", {"start": v(68.89, -24.32) * mm, "end": v(65.73, -24.32) * mm});
            skLineSegment(sketch, "E14.14.13.13", {"start": v(65.73, -24.32) * mm, "end": v(64.16, -21.6) * mm});
            skLineSegment(sketch, "E14.17.13.13", {"start": v(64.16, -21.59) * mm, "end": v(65.73, -18.86) * mm});
            skLineSegment(sketch, "E14.0.13.14", {"start": v(65.73, -10.22) * mm, "end": v(68.89, -10.22) * mm});
            skLineSegment(sketch, "E14.3.13.14", {"start": v(68.89, -10.22) * mm, "end": v(70.46, -12.95) * mm});
            skLineSegment(sketch, "E14.6.13.14", {"start": v(70.46, -12.95) * mm, "end": v(68.89, -15.68) * mm});
            skCircle(sketch, "E14.9.13.14", {"center": v(67.31, -12.95) * mm, "radius": 2.73 * mm, "construction": true});
            skLineSegment(sketch, "E14.11.13.14", {"start": v(68.89, -15.68) * mm, "end": v(65.73, -15.68) * mm});
            skLineSegment(sketch, "E14.14.13.14", {"start": v(65.73, -15.68) * mm, "end": v(64.16, -12.95) * mm});
            skLineSegment(sketch, "E14.17.13.14", {"start": v(64.16, -12.95) * mm, "end": v(65.73, -10.22) * mm});
            skLineSegment(sketch, "E14.0.13.15", {"start": v(65.73, -1.59) * mm, "end": v(68.89, -1.59) * mm});
            skLineSegment(sketch, "E14.3.13.15", {"start": v(68.89, -1.59) * mm, "end": v(70.46, -4.32) * mm});
            skLineSegment(sketch, "E14.6.13.15", {"start": v(70.46, -4.32) * mm, "end": v(68.89, -7.05) * mm});
            skCircle(sketch, "E14.9.13.15", {"center": v(67.31, -4.32) * mm, "radius": 2.73 * mm, "construction": true});
            skLineSegment(sketch, "E14.11.13.15", {"start": v(68.89, -7.05) * mm, "end": v(65.73, -7.05) * mm});
            skLineSegment(sketch, "E14.14.13.15", {"start": v(65.73, -7.05) * mm, "end": v(64.16, -4.32) * mm});
            skLineSegment(sketch, "E14.17.13.15", {"start": v(64.16, -4.32) * mm, "end": v(65.73, -1.59) * mm});
            skLineSegment(sketch, "E14.0.13.16", {"start": v(65.73, 7.05) * mm, "end": v(68.89, 7.05) * mm});
            skLineSegment(sketch, "E14.3.13.16", {"start": v(68.89, 7.05) * mm, "end": v(70.46, 4.32) * mm});
            skLineSegment(sketch, "E14.6.13.16", {"start": v(70.46, 4.32) * mm, "end": v(68.89, 1.59) * mm});
            skCircle(sketch, "E14.9.13.16", {"center": v(67.31, 4.32) * mm, "radius": 2.73 * mm, "construction": true});
            skLineSegment(sketch, "E14.11.13.16", {"start": v(68.89, 1.59) * mm, "end": v(65.73, 1.59) * mm});
            skLineSegment(sketch, "E14.14.13.16", {"start": v(65.73, 1.59) * mm, "end": v(64.16, 4.32) * mm});
            skLineSegment(sketch, "E14.17.13.16", {"start": v(64.16, 4.32) * mm, "end": v(65.73, 7.05) * mm});
            skLineSegment(sketch, "E14.0.13.17", {"start": v(65.73, 15.68) * mm, "end": v(68.89, 15.68) * mm});
            skLineSegment(sketch, "E14.3.13.17", {"start": v(68.89, 15.68) * mm, "end": v(70.46, 12.95) * mm});
            skLineSegment(sketch, "E14.6.13.17", {"start": v(70.46, 12.95) * mm, "end": v(68.89, 10.22) * mm});
            skCircle(sketch, "E14.9.13.17", {"center": v(67.31, 12.95) * mm, "radius": 2.73 * mm, "construction": true});
            skLineSegment(sketch, "E14.11.13.17", {"start": v(68.89, 10.22) * mm, "end": v(65.73, 10.22) * mm});
            skLineSegment(sketch, "E14.14.13.17", {"start": v(65.73, 10.22) * mm, "end": v(64.16, 12.95) * mm});
            skLineSegment(sketch, "E14.17.13.17", {"start": v(64.16, 12.95) * mm, "end": v(65.73, 15.68) * mm});
            skLineSegment(sketch, "E14.0.13.18", {"start": v(65.73, 24.32) * mm, "end": v(68.89, 24.32) * mm});
            skLineSegment(sketch, "E14.3.13.18", {"start": v(68.89, 24.32) * mm, "end": v(70.46, 21.59) * mm});
            skLineSegment(sketch, "E14.6.13.18", {"start": v(70.46, 21.59) * mm, "end": v(68.89, 18.86) * mm});
            skCircle(sketch, "E14.9.13.18", {"center": v(67.31, 21.59) * mm, "radius": 2.73 * mm, "construction": true});
            skLineSegment(sketch, "E14.11.13.18", {"start": v(68.89, 18.86) * mm, "end": v(65.73, 18.86) * mm});
            skLineSegment(sketch, "E14.14.13.18", {"start": v(65.73, 18.86) * mm, "end": v(64.16, 21.59) * mm});
            skLineSegment(sketch, "E14.17.13.18", {"start": v(64.16, 21.6) * mm, "end": v(65.73, 24.32) * mm});
            skLineSegment(sketch, "E14.0.13.19", {"start": v(65.73, 32.96) * mm, "end": v(68.89, 32.96) * mm});
            skLineSegment(sketch, "E14.3.13.19", {"start": v(68.89, 32.96) * mm, "end": v(70.46, 30.23) * mm});
            skLineSegment(sketch, "E14.6.13.19", {"start": v(70.46, 30.23) * mm, "end": v(68.89, 27.5) * mm});
            skCircle(sketch, "E14.9.13.19", {"center": v(67.31, 30.23) * mm, "radius": 2.73 * mm, "construction": true});
            skLineSegment(sketch, "E14.11.13.19", {"start": v(68.89, 27.5) * mm, "end": v(65.73, 27.5) * mm});
            skLineSegment(sketch, "E14.14.13.19", {"start": v(65.73, 27.5) * mm, "end": v(64.16, 30.23) * mm});
            skLineSegment(sketch, "E14.17.13.19", {"start": v(64.16, 30.23) * mm, "end": v(65.73, 32.96) * mm});
            skLineSegment(sketch, "E14.0.14.0", {"start": v(80.7, -131.13) * mm, "end": v(83.85, -131.13) * mm});
            skLineSegment(sketch, "E14.3.14.0", {"start": v(83.85, -131.13) * mm, "end": v(85.42, -133.86) * mm});
            skLineSegment(sketch, "E14.6.14.0", {"start": v(85.42, -133.86) * mm, "end": v(83.85, -136.59) * mm});
            skCircle(sketch, "E14.9.14.0", {"center": v(82.27, -133.86) * mm, "radius": 2.73 * mm, "construction": true});
            skLineSegment(sketch, "E14.11.14.0", {"start": v(83.85, -136.59) * mm, "end": v(80.7, -136.59) * mm});
            skLineSegment(sketch, "E14.14.14.0", {"start": v(80.7, -136.59) * mm, "end": v(79.12, -133.86) * mm});
            skLineSegment(sketch, "E14.17.14.0", {"start": v(79.12, -133.86) * mm, "end": v(80.7, -131.13) * mm});
            skLineSegment(sketch, "E14.0.14.1", {"start": v(80.7, -122.5) * mm, "end": v(83.85, -122.5) * mm});
            skLineSegment(sketch, "E14.3.14.1", {"start": v(83.85, -122.5) * mm, "end": v(85.42, -125.22) * mm});
            skLineSegment(sketch, "E14.6.14.1", {"start": v(85.42, -125.22) * mm, "end": v(83.85, -127.95) * mm});
            skCircle(sketch, "E14.9.14.1", {"center": v(82.27, -125.22) * mm, "radius": 2.73 * mm, "construction": true});
            skLineSegment(sketch, "E14.11.14.1", {"start": v(83.85, -127.95) * mm, "end": v(80.7, -127.95) * mm});
            skLineSegment(sketch, "E14.14.14.1", {"start": v(80.7, -127.95) * mm, "end": v(79.12, -125.22) * mm});
            skLineSegment(sketch, "E14.17.14.1", {"start": v(79.12, -125.22) * mm, "end": v(80.7, -122.5) * mm});
            skLineSegment(sketch, "E14.0.14.2", {"start": v(80.7, -113.86) * mm, "end": v(83.85, -113.86) * mm});
            skLineSegment(sketch, "E14.3.14.2", {"start": v(83.85, -113.86) * mm, "end": v(85.42, -116.59) * mm});
            skLineSegment(sketch, "E14.6.14.2", {"start": v(85.42, -116.59) * mm, "end": v(83.85, -119.32) * mm});
            skCircle(sketch, "E14.9.14.2", {"center": v(82.27, -116.59) * mm, "radius": 2.73 * mm, "construction": true});
            skLineSegment(sketch, "E14.11.14.2", {"start": v(83.85, -119.32) * mm, "end": v(80.7, -119.32) * mm});
            skLineSegment(sketch, "E14.14.14.2", {"start": v(80.7, -119.32) * mm, "end": v(79.12, -116.59) * mm});
            skLineSegment(sketch, "E14.17.14.2", {"start": v(79.12, -116.59) * mm, "end": v(80.7, -113.86) * mm});
            skLineSegment(sketch, "E14.0.14.3", {"start": v(80.7, -105.22) * mm, "end": v(83.85, -105.22) * mm});
            skLineSegment(sketch, "E14.3.14.3", {"start": v(83.85, -105.22) * mm, "end": v(85.42, -107.95) * mm});
            skLineSegment(sketch, "E14.6.14.3", {"start": v(85.42, -107.95) * mm, "end": v(83.85, -110.68) * mm});
            skCircle(sketch, "E14.9.14.3", {"center": v(82.27, -107.95) * mm, "radius": 2.73 * mm, "construction": true});
            skLineSegment(sketch, "E14.11.14.3", {"start": v(83.85, -110.68) * mm, "end": v(80.7, -110.68) * mm});
            skLineSegment(sketch, "E14.14.14.3", {"start": v(80.7, -110.68) * mm, "end": v(79.12, -107.95) * mm});
            skLineSegment(sketch, "E14.17.14.3", {"start": v(79.12, -107.95) * mm, "end": v(80.7, -105.22) * mm});
            skLineSegment(sketch, "E14.0.14.4", {"start": v(80.7, -96.58) * mm, "end": v(83.85, -96.58) * mm});
            skLineSegment(sketch, "E14.3.14.4", {"start": v(83.85, -96.58) * mm, "end": v(85.42, -99.31) * mm});
            skLineSegment(sketch, "E14.6.14.4", {"start": v(85.42, -99.31) * mm, "end": v(83.85, -102.04) * mm});
            skCircle(sketch, "E14.9.14.4", {"center": v(82.27, -99.31) * mm, "radius": 2.73 * mm, "construction": true});
            skLineSegment(sketch, "E14.11.14.4", {"start": v(83.85, -102.04) * mm, "end": v(80.7, -102.04) * mm});
            skLineSegment(sketch, "E14.14.14.4", {"start": v(80.7, -102.04) * mm, "end": v(79.12, -99.31) * mm});
            skLineSegment(sketch, "E14.17.14.4", {"start": v(79.12, -99.31) * mm, "end": v(80.7, -96.58) * mm});
            skLineSegment(sketch, "E14.0.14.5", {"start": v(80.7, -87.95) * mm, "end": v(83.85, -87.95) * mm});
            skLineSegment(sketch, "E14.3.14.5", {"start": v(83.85, -87.95) * mm, "end": v(85.42, -90.68) * mm});
            skLineSegment(sketch, "E14.6.14.5", {"start": v(85.42, -90.68) * mm, "end": v(83.85, -93.4) * mm});
            skCircle(sketch, "E14.9.14.5", {"center": v(82.27, -90.68) * mm, "radius": 2.73 * mm, "construction": true});
            skLineSegment(sketch, "E14.11.14.5", {"start": v(83.85, -93.4) * mm, "end": v(80.7, -93.4) * mm});
            skLineSegment(sketch, "E14.14.14.5", {"start": v(80.7, -93.4) * mm, "end": v(79.12, -90.68) * mm});
            skLineSegment(sketch, "E14.17.14.5", {"start": v(79.12, -90.68) * mm, "end": v(80.7, -87.95) * mm});
            skLineSegment(sketch, "E14.0.14.6", {"start": v(80.7, -79.31) * mm, "end": v(83.85, -79.31) * mm});
            skLineSegment(sketch, "E14.3.14.6", {"start": v(83.85, -79.31) * mm, "end": v(85.42, -82.04) * mm});
            skLineSegment(sketch, "E14.6.14.6", {"start": v(85.42, -82.04) * mm, "end": v(83.85, -84.77) * mm});
            skCircle(sketch, "E14.9.14.6", {"center": v(82.27, -82.04) * mm, "radius": 2.73 * mm, "construction": true});
            skLineSegment(sketch, "E14.11.14.6", {"start": v(83.85, -84.77) * mm, "end": v(80.7, -84.77) * mm});
            skLineSegment(sketch, "E14.14.14.6", {"start": v(80.7, -84.77) * mm, "end": v(79.12, -82.04) * mm});
            skLineSegment(sketch, "E14.17.14.6", {"start": v(79.12, -82.04) * mm, "end": v(80.7, -79.31) * mm});
            skLineSegment(sketch, "E14.0.14.7", {"start": v(80.7, -70.68) * mm, "end": v(83.85, -70.68) * mm});
            skLineSegment(sketch, "E14.3.14.7", {"start": v(83.85, -70.68) * mm, "end": v(85.42, -73.4) * mm});
            skLineSegment(sketch, "E14.6.14.7", {"start": v(85.42, -73.4) * mm, "end": v(83.85, -76.14) * mm});
            skCircle(sketch, "E14.9.14.7", {"center": v(82.27, -73.4) * mm, "radius": 2.73 * mm, "construction": true});
            skLineSegment(sketch, "E14.11.14.7", {"start": v(83.85, -76.14) * mm, "end": v(80.7, -76.14) * mm});
            skLineSegment(sketch, "E14.14.14.7", {"start": v(80.7, -76.14) * mm, "end": v(79.12, -73.4) * mm});
            skLineSegment(sketch, "E14.17.14.7", {"start": v(79.12, -73.4) * mm, "end": v(80.7, -70.68) * mm});
            skLineSegment(sketch, "E14.0.14.8", {"start": v(80.7, -62.04) * mm, "end": v(83.85, -62.04) * mm});
            skLineSegment(sketch, "E14.3.14.8", {"start": v(83.85, -62.04) * mm, "end": v(85.42, -64.77) * mm});
            skLineSegment(sketch, "E14.6.14.8", {"start": v(85.42, -64.77) * mm, "end": v(83.85, -67.5) * mm});
            skCircle(sketch, "E14.9.14.8", {"center": v(82.27, -64.77) * mm, "radius": 2.73 * mm, "construction": true});
            skLineSegment(sketch, "E14.11.14.8", {"start": v(83.85, -67.5) * mm, "end": v(80.7, -67.5) * mm});
            skLineSegment(sketch, "E14.14.14.8", {"start": v(80.7, -67.5) * mm, "end": v(79.12, -64.77) * mm});
            skLineSegment(sketch, "E14.17.14.8", {"start": v(79.12, -64.77) * mm, "end": v(80.7, -62.04) * mm});
            skLineSegment(sketch, "E14.0.14.9", {"start": v(80.7, -53.4) * mm, "end": v(83.85, -53.4) * mm});
            skLineSegment(sketch, "E14.3.14.9", {"start": v(83.85, -53.4) * mm, "end": v(85.42, -56.13) * mm});
            skLineSegment(sketch, "E14.6.14.9", {"start": v(85.42, -56.13) * mm, "end": v(83.85, -58.86) * mm});
            skCircle(sketch, "E14.9.14.9", {"center": v(82.27, -56.13) * mm, "radius": 2.73 * mm, "construction": true});
            skLineSegment(sketch, "E14.11.14.9", {"start": v(83.85, -58.86) * mm, "end": v(80.7, -58.86) * mm});
            skLineSegment(sketch, "E14.14.14.9", {"start": v(80.7, -58.86) * mm, "end": v(79.12, -56.13) * mm});
            skLineSegment(sketch, "E14.17.14.9", {"start": v(79.12, -56.13) * mm, "end": v(80.7, -53.4) * mm});
            skLineSegment(sketch, "E14.0.14.10", {"start": v(80.7, -44.77) * mm, "end": v(83.85, -44.77) * mm});
            skLineSegment(sketch, "E14.3.14.10", {"start": v(83.85, -44.77) * mm, "end": v(85.42, -47.5) * mm});
            skLineSegment(sketch, "E14.6.14.10", {"start": v(85.42, -47.5) * mm, "end": v(83.85, -50.23) * mm});
            skCircle(sketch, "E14.9.14.10", {"center": v(82.27, -47.5) * mm, "radius": 2.73 * mm, "construction": true});
            skLineSegment(sketch, "E14.11.14.10", {"start": v(83.85, -50.23) * mm, "end": v(80.7, -50.23) * mm});
            skLineSegment(sketch, "E14.14.14.10", {"start": v(80.7, -50.23) * mm, "end": v(79.12, -47.5) * mm});
            skLineSegment(sketch, "E14.17.14.10", {"start": v(79.12, -47.5) * mm, "end": v(80.7, -44.77) * mm});
            skLineSegment(sketch, "E14.0.14.11", {"start": v(80.7, -36.13) * mm, "end": v(83.85, -36.13) * mm});
            skLineSegment(sketch, "E14.3.14.11", {"start": v(83.85, -36.13) * mm, "end": v(85.42, -38.86) * mm});
            skLineSegment(sketch, "E14.6.14.11", {"start": v(85.42, -38.86) * mm, "end": v(83.85, -41.6) * mm});
            skCircle(sketch, "E14.9.14.11", {"center": v(82.27, -38.86) * mm, "radius": 2.73 * mm, "construction": true});
            skLineSegment(sketch, "E14.11.14.11", {"start": v(83.85, -41.6) * mm, "end": v(80.7, -41.6) * mm});
            skLineSegment(sketch, "E14.14.14.11", {"start": v(80.7, -41.6) * mm, "end": v(79.12, -38.86) * mm});
            skLineSegment(sketch, "E14.17.14.11", {"start": v(79.12, -38.86) * mm, "end": v(80.7, -36.13) * mm});
            skLineSegment(sketch, "E14.0.14.12", {"start": v(80.7, -27.5) * mm, "end": v(83.85, -27.5) * mm});
            skLineSegment(sketch, "E14.3.14.12", {"start": v(83.85, -27.5) * mm, "end": v(85.42, -30.23) * mm});
            skLineSegment(sketch, "E14.6.14.12", {"start": v(85.42, -30.23) * mm, "end": v(83.85, -32.96) * mm});
            skCircle(sketch, "E14.9.14.12", {"center": v(82.27, -30.23) * mm, "radius": 2.73 * mm, "construction": true});
            skLineSegment(sketch, "E14.11.14.12", {"start": v(83.85, -32.96) * mm, "end": v(80.7, -32.96) * mm});
            skLineSegment(sketch, "E14.14.14.12", {"start": v(80.7, -32.96) * mm, "end": v(79.12, -30.23) * mm});
            skLineSegment(sketch, "E14.17.14.12", {"start": v(79.12, -30.23) * mm, "end": v(80.7, -27.5) * mm});
            skLineSegment(sketch, "E14.0.14.13", {"start": v(80.7, -18.86) * mm, "end": v(83.85, -18.86) * mm});
            skLineSegment(sketch, "E14.3.14.13", {"start": v(83.85, -18.86) * mm, "end": v(85.42, -21.6) * mm});
            skLineSegment(sketch, "E14.6.14.13", {"start": v(85.42, -21.6) * mm, "end": v(83.85, -24.32) * mm});
            skCircle(sketch, "E14.9.14.13", {"center": v(82.27, -21.6) * mm, "radius": 2.73 * mm, "construction": true});
            skLineSegment(sketch, "E14.11.14.13", {"start": v(83.85, -24.32) * mm, "end": v(80.7, -24.32) * mm});
            skLineSegment(sketch, "E14.14.14.13", {"start": v(80.7, -24.32) * mm, "end": v(79.12, -21.6) * mm});
            skLineSegment(sketch, "E14.17.14.13", {"start": v(79.12, -21.59) * mm, "end": v(80.7, -18.86) * mm});
            skLineSegment(sketch, "E14.0.14.14", {"start": v(80.7, -10.22) * mm, "end": v(83.85, -10.22) * mm});
            skLineSegment(sketch, "E14.3.14.14", {"start": v(83.85, -10.22) * mm, "end": v(85.42, -12.95) * mm});
            skLineSegment(sketch, "E14.6.14.14", {"start": v(85.42, -12.95) * mm, "end": v(83.85, -15.68) * mm});
            skCircle(sketch, "E14.9.14.14", {"center": v(82.27, -12.95) * mm, "radius": 2.73 * mm, "construction": true});
            skLineSegment(sketch, "E14.11.14.14", {"start": v(83.85, -15.68) * mm, "end": v(80.7, -15.68) * mm});
            skLineSegment(sketch, "E14.14.14.14", {"start": v(80.7, -15.68) * mm, "end": v(79.12, -12.95) * mm});
            skLineSegment(sketch, "E14.17.14.14", {"start": v(79.12, -12.95) * mm, "end": v(80.7, -10.22) * mm});
            skLineSegment(sketch, "E14.0.14.15", {"start": v(80.7, -1.59) * mm, "end": v(83.85, -1.59) * mm});
            skLineSegment(sketch, "E14.3.14.15", {"start": v(83.85, -1.59) * mm, "end": v(85.42, -4.32) * mm});
            skLineSegment(sketch, "E14.6.14.15", {"start": v(85.42, -4.32) * mm, "end": v(83.85, -7.05) * mm});
            skCircle(sketch, "E14.9.14.15", {"center": v(82.27, -4.32) * mm, "radius": 2.73 * mm, "construction": true});
            skLineSegment(sketch, "E14.11.14.15", {"start": v(83.85, -7.05) * mm, "end": v(80.7, -7.05) * mm});
            skLineSegment(sketch, "E14.14.14.15", {"start": v(80.7, -7.05) * mm, "end": v(79.12, -4.32) * mm});
            skLineSegment(sketch, "E14.17.14.15", {"start": v(79.12, -4.32) * mm, "end": v(80.7, -1.59) * mm});
            skLineSegment(sketch, "E14.0.14.16", {"start": v(80.7, 7.05) * mm, "end": v(83.85, 7.05) * mm});
            skLineSegment(sketch, "E14.3.14.16", {"start": v(83.85, 7.05) * mm, "end": v(85.42, 4.32) * mm});
            skLineSegment(sketch, "E14.6.14.16", {"start": v(85.42, 4.32) * mm, "end": v(83.85, 1.59) * mm});
            skCircle(sketch, "E14.9.14.16", {"center": v(82.27, 4.32) * mm, "radius": 2.73 * mm, "construction": true});
            skLineSegment(sketch, "E14.11.14.16", {"start": v(83.85, 1.59) * mm, "end": v(80.7, 1.59) * mm});
            skLineSegment(sketch, "E14.14.14.16", {"start": v(80.7, 1.59) * mm, "end": v(79.12, 4.32) * mm});
            skLineSegment(sketch, "E14.17.14.16", {"start": v(79.12, 4.32) * mm, "end": v(80.7, 7.05) * mm});
            skLineSegment(sketch, "E14.0.14.17", {"start": v(80.7, 15.68) * mm, "end": v(83.85, 15.68) * mm});
            skLineSegment(sketch, "E14.3.14.17", {"start": v(83.85, 15.68) * mm, "end": v(85.42, 12.95) * mm});
            skLineSegment(sketch, "E14.6.14.17", {"start": v(85.42, 12.95) * mm, "end": v(83.85, 10.22) * mm});
            skCircle(sketch, "E14.9.14.17", {"center": v(82.27, 12.95) * mm, "radius": 2.73 * mm, "construction": true});
            skLineSegment(sketch, "E14.11.14.17", {"start": v(83.85, 10.22) * mm, "end": v(80.7, 10.22) * mm});
            skLineSegment(sketch, "E14.14.14.17", {"start": v(80.7, 10.22) * mm, "end": v(79.12, 12.95) * mm});
            skLineSegment(sketch, "E14.17.14.17", {"start": v(79.12, 12.95) * mm, "end": v(80.7, 15.68) * mm});
            skLineSegment(sketch, "E14.0.14.18", {"start": v(80.7, 24.32) * mm, "end": v(83.85, 24.32) * mm});
            skLineSegment(sketch, "E14.3.14.18", {"start": v(83.85, 24.32) * mm, "end": v(85.42, 21.59) * mm});
            skLineSegment(sketch, "E14.6.14.18", {"start": v(85.42, 21.59) * mm, "end": v(83.85, 18.86) * mm});
            skCircle(sketch, "E14.9.14.18", {"center": v(82.27, 21.59) * mm, "radius": 2.73 * mm, "construction": true});
            skLineSegment(sketch, "E14.11.14.18", {"start": v(83.85, 18.86) * mm, "end": v(80.7, 18.86) * mm});
            skLineSegment(sketch, "E14.14.14.18", {"start": v(80.7, 18.86) * mm, "end": v(79.12, 21.59) * mm});
            skLineSegment(sketch, "E14.17.14.18", {"start": v(79.12, 21.59) * mm, "end": v(80.7, 24.32) * mm});
            skLineSegment(sketch, "E14.0.14.19", {"start": v(80.7, 32.96) * mm, "end": v(83.85, 32.96) * mm});
            skLineSegment(sketch, "E14.3.14.19", {"start": v(83.85, 32.96) * mm, "end": v(85.42, 30.23) * mm});
            skLineSegment(sketch, "E14.6.14.19", {"start": v(85.42, 30.23) * mm, "end": v(83.85, 27.5) * mm});
            skCircle(sketch, "E14.9.14.19", {"center": v(82.27, 30.23) * mm, "radius": 2.73 * mm, "construction": true});
            skLineSegment(sketch, "E14.11.14.19", {"start": v(83.85, 27.5) * mm, "end": v(80.7, 27.5) * mm});
            skLineSegment(sketch, "E14.14.14.19", {"start": v(80.7, 27.5) * mm, "end": v(79.12, 30.23) * mm});
            skLineSegment(sketch, "E14.17.14.19", {"start": v(79.12, 30.23) * mm, "end": v(80.7, 32.96) * mm});
            skLineSegment(sketch, "E14.0.15.0", {"start": v(95.65, -131.13) * mm, "end": v(98.8, -131.13) * mm});
            skLineSegment(sketch, "E14.3.15.0", {"start": v(98.8, -131.13) * mm, "end": v(100.38, -133.86) * mm});
            skLineSegment(sketch, "E14.6.15.0", {"start": v(100.38, -133.86) * mm, "end": v(98.8, -136.59) * mm});
            skCircle(sketch, "E14.9.15.0", {"center": v(97.23, -133.86) * mm, "radius": 2.73 * mm, "construction": true});
            skLineSegment(sketch, "E14.11.15.0", {"start": v(98.8, -136.59) * mm, "end": v(95.65, -136.59) * mm});
            skLineSegment(sketch, "E14.14.15.0", {"start": v(95.65, -136.59) * mm, "end": v(94.07, -133.86) * mm});
            skLineSegment(sketch, "E14.17.15.0", {"start": v(94.07, -133.86) * mm, "end": v(95.65, -131.13) * mm});
            skLineSegment(sketch, "E14.0.15.1", {"start": v(95.65, -122.5) * mm, "end": v(98.8, -122.5) * mm});
            skLineSegment(sketch, "E14.3.15.1", {"start": v(98.8, -122.5) * mm, "end": v(100.38, -125.22) * mm});
            skLineSegment(sketch, "E14.6.15.1", {"start": v(100.38, -125.22) * mm, "end": v(98.8, -127.95) * mm});
            skCircle(sketch, "E14.9.15.1", {"center": v(97.23, -125.22) * mm, "radius": 2.73 * mm, "construction": true});
            skLineSegment(sketch, "E14.11.15.1", {"start": v(98.8, -127.95) * mm, "end": v(95.65, -127.95) * mm});
            skLineSegment(sketch, "E14.14.15.1", {"start": v(95.65, -127.95) * mm, "end": v(94.07, -125.22) * mm});
            skLineSegment(sketch, "E14.17.15.1", {"start": v(94.07, -125.22) * mm, "end": v(95.65, -122.5) * mm});
            skLineSegment(sketch, "E14.0.15.2", {"start": v(95.65, -113.86) * mm, "end": v(98.8, -113.86) * mm});
            skLineSegment(sketch, "E14.3.15.2", {"start": v(98.8, -113.86) * mm, "end": v(100.38, -116.59) * mm});
            skLineSegment(sketch, "E14.6.15.2", {"start": v(100.38, -116.59) * mm, "end": v(98.8, -119.32) * mm});
            skCircle(sketch, "E14.9.15.2", {"center": v(97.23, -116.59) * mm, "radius": 2.73 * mm, "construction": true});
            skLineSegment(sketch, "E14.11.15.2", {"start": v(98.8, -119.32) * mm, "end": v(95.65, -119.32) * mm});
            skLineSegment(sketch, "E14.14.15.2", {"start": v(95.65, -119.32) * mm, "end": v(94.07, -116.59) * mm});
            skLineSegment(sketch, "E14.17.15.2", {"start": v(94.07, -116.59) * mm, "end": v(95.65, -113.86) * mm});
            skLineSegment(sketch, "E14.0.15.3", {"start": v(95.65, -105.22) * mm, "end": v(98.8, -105.22) * mm});
            skLineSegment(sketch, "E14.3.15.3", {"start": v(98.8, -105.22) * mm, "end": v(100.38, -107.95) * mm});
            skLineSegment(sketch, "E14.6.15.3", {"start": v(100.38, -107.95) * mm, "end": v(98.8, -110.68) * mm});
            skCircle(sketch, "E14.9.15.3", {"center": v(97.23, -107.95) * mm, "radius": 2.73 * mm, "construction": true});
            skLineSegment(sketch, "E14.11.15.3", {"start": v(98.8, -110.68) * mm, "end": v(95.65, -110.68) * mm});
            skLineSegment(sketch, "E14.14.15.3", {"start": v(95.65, -110.68) * mm, "end": v(94.07, -107.95) * mm});
            skLineSegment(sketch, "E14.17.15.3", {"start": v(94.07, -107.95) * mm, "end": v(95.65, -105.22) * mm});
            skLineSegment(sketch, "E14.0.15.4", {"start": v(95.65, -96.58) * mm, "end": v(98.8, -96.58) * mm});
            skLineSegment(sketch, "E14.3.15.4", {"start": v(98.8, -96.58) * mm, "end": v(100.38, -99.31) * mm});
            skLineSegment(sketch, "E14.6.15.4", {"start": v(100.38, -99.31) * mm, "end": v(98.8, -102.04) * mm});
            skCircle(sketch, "E14.9.15.4", {"center": v(97.23, -99.31) * mm, "radius": 2.73 * mm, "construction": true});
            skLineSegment(sketch, "E14.11.15.4", {"start": v(98.8, -102.04) * mm, "end": v(95.65, -102.04) * mm});
            skLineSegment(sketch, "E14.14.15.4", {"start": v(95.65, -102.04) * mm, "end": v(94.07, -99.31) * mm});
            skLineSegment(sketch, "E14.17.15.4", {"start": v(94.07, -99.31) * mm, "end": v(95.65, -96.58) * mm});
            skLineSegment(sketch, "E14.0.15.5", {"start": v(95.65, -87.95) * mm, "end": v(98.8, -87.95) * mm});
            skLineSegment(sketch, "E14.3.15.5", {"start": v(98.8, -87.95) * mm, "end": v(100.38, -90.68) * mm});
            skLineSegment(sketch, "E14.6.15.5", {"start": v(100.38, -90.68) * mm, "end": v(98.8, -93.4) * mm});
            skCircle(sketch, "E14.9.15.5", {"center": v(97.23, -90.68) * mm, "radius": 2.73 * mm, "construction": true});
            skLineSegment(sketch, "E14.11.15.5", {"start": v(98.8, -93.4) * mm, "end": v(95.65, -93.4) * mm});
            skLineSegment(sketch, "E14.14.15.5", {"start": v(95.65, -93.4) * mm, "end": v(94.07, -90.68) * mm});
            skLineSegment(sketch, "E14.17.15.5", {"start": v(94.07, -90.68) * mm, "end": v(95.65, -87.95) * mm});
            skLineSegment(sketch, "E14.0.15.6", {"start": v(95.65, -79.31) * mm, "end": v(98.8, -79.31) * mm});
            skLineSegment(sketch, "E14.3.15.6", {"start": v(98.8, -79.31) * mm, "end": v(100.38, -82.04) * mm});
            skLineSegment(sketch, "E14.6.15.6", {"start": v(100.38, -82.04) * mm, "end": v(98.8, -84.77) * mm});
            skCircle(sketch, "E14.9.15.6", {"center": v(97.23, -82.04) * mm, "radius": 2.73 * mm, "construction": true});
            skLineSegment(sketch, "E14.11.15.6", {"start": v(98.8, -84.77) * mm, "end": v(95.65, -84.77) * mm});
            skLineSegment(sketch, "E14.14.15.6", {"start": v(95.65, -84.77) * mm, "end": v(94.07, -82.04) * mm});
            skLineSegment(sketch, "E14.17.15.6", {"start": v(94.07, -82.04) * mm, "end": v(95.65, -79.31) * mm});
            skLineSegment(sketch, "E14.0.15.7", {"start": v(95.65, -70.68) * mm, "end": v(98.8, -70.68) * mm});
            skLineSegment(sketch, "E14.3.15.7", {"start": v(98.8, -70.68) * mm, "end": v(100.38, -73.4) * mm});
            skLineSegment(sketch, "E14.6.15.7", {"start": v(100.38, -73.4) * mm, "end": v(98.8, -76.14) * mm});
            skCircle(sketch, "E14.9.15.7", {"center": v(97.23, -73.4) * mm, "radius": 2.73 * mm, "construction": true});
            skLineSegment(sketch, "E14.11.15.7", {"start": v(98.8, -76.14) * mm, "end": v(95.65, -76.14) * mm});
            skLineSegment(sketch, "E14.14.15.7", {"start": v(95.65, -76.14) * mm, "end": v(94.07, -73.4) * mm});
            skLineSegment(sketch, "E14.17.15.7", {"start": v(94.07, -73.4) * mm, "end": v(95.65, -70.68) * mm});
            skLineSegment(sketch, "E14.0.15.8", {"start": v(95.65, -62.04) * mm, "end": v(98.8, -62.04) * mm});
            skLineSegment(sketch, "E14.3.15.8", {"start": v(98.8, -62.04) * mm, "end": v(100.38, -64.77) * mm});
            skLineSegment(sketch, "E14.6.15.8", {"start": v(100.38, -64.77) * mm, "end": v(98.8, -67.5) * mm});
            skCircle(sketch, "E14.9.15.8", {"center": v(97.23, -64.77) * mm, "radius": 2.73 * mm, "construction": true});
            skLineSegment(sketch, "E14.11.15.8", {"start": v(98.8, -67.5) * mm, "end": v(95.65, -67.5) * mm});
            skLineSegment(sketch, "E14.14.15.8", {"start": v(95.65, -67.5) * mm, "end": v(94.07, -64.77) * mm});
            skLineSegment(sketch, "E14.17.15.8", {"start": v(94.07, -64.77) * mm, "end": v(95.65, -62.04) * mm});
            skLineSegment(sketch, "E14.0.15.9", {"start": v(95.65, -53.4) * mm, "end": v(98.8, -53.4) * mm});
            skLineSegment(sketch, "E14.3.15.9", {"start": v(98.8, -53.4) * mm, "end": v(100.38, -56.13) * mm});
            skLineSegment(sketch, "E14.6.15.9", {"start": v(100.38, -56.13) * mm, "end": v(98.8, -58.86) * mm});
            skCircle(sketch, "E14.9.15.9", {"center": v(97.23, -56.13) * mm, "radius": 2.73 * mm, "construction": true});
            skLineSegment(sketch, "E14.11.15.9", {"start": v(98.8, -58.86) * mm, "end": v(95.65, -58.86) * mm});
            skLineSegment(sketch, "E14.14.15.9", {"start": v(95.65, -58.86) * mm, "end": v(94.07, -56.13) * mm});
            skLineSegment(sketch, "E14.17.15.9", {"start": v(94.07, -56.13) * mm, "end": v(95.65, -53.4) * mm});
            skLineSegment(sketch, "E14.0.15.10", {"start": v(95.65, -44.77) * mm, "end": v(98.8, -44.77) * mm});
            skLineSegment(sketch, "E14.3.15.10", {"start": v(98.8, -44.77) * mm, "end": v(100.38, -47.5) * mm});
            skLineSegment(sketch, "E14.6.15.10", {"start": v(100.38, -47.5) * mm, "end": v(98.8, -50.23) * mm});
            skCircle(sketch, "E14.9.15.10", {"center": v(97.23, -47.5) * mm, "radius": 2.73 * mm, "construction": true});
            skLineSegment(sketch, "E14.11.15.10", {"start": v(98.8, -50.23) * mm, "end": v(95.65, -50.23) * mm});
            skLineSegment(sketch, "E14.14.15.10", {"start": v(95.65, -50.23) * mm, "end": v(94.07, -47.5) * mm});
            skLineSegment(sketch, "E14.17.15.10", {"start": v(94.07, -47.5) * mm, "end": v(95.65, -44.77) * mm});
            skLineSegment(sketch, "E14.0.15.11", {"start": v(95.65, -36.13) * mm, "end": v(98.8, -36.13) * mm});
            skLineSegment(sketch, "E14.3.15.11", {"start": v(98.8, -36.13) * mm, "end": v(100.38, -38.86) * mm});
            skLineSegment(sketch, "E14.6.15.11", {"start": v(100.38, -38.86) * mm, "end": v(98.8, -41.6) * mm});
            skCircle(sketch, "E14.9.15.11", {"center": v(97.23, -38.86) * mm, "radius": 2.73 * mm, "construction": true});
            skLineSegment(sketch, "E14.11.15.11", {"start": v(98.8, -41.6) * mm, "end": v(95.65, -41.6) * mm});
            skLineSegment(sketch, "E14.14.15.11", {"start": v(95.65, -41.6) * mm, "end": v(94.07, -38.86) * mm});
            skLineSegment(sketch, "E14.17.15.11", {"start": v(94.07, -38.86) * mm, "end": v(95.65, -36.13) * mm});
            skLineSegment(sketch, "E14.0.15.12", {"start": v(95.65, -27.5) * mm, "end": v(98.8, -27.5) * mm});
            skLineSegment(sketch, "E14.3.15.12", {"start": v(98.8, -27.5) * mm, "end": v(100.38, -30.23) * mm});
            skLineSegment(sketch, "E14.6.15.12", {"start": v(100.38, -30.23) * mm, "end": v(98.8, -32.96) * mm});
            skCircle(sketch, "E14.9.15.12", {"center": v(97.23, -30.23) * mm, "radius": 2.73 * mm, "construction": true});
            skLineSegment(sketch, "E14.11.15.12", {"start": v(98.8, -32.96) * mm, "end": v(95.65, -32.96) * mm});
            skLineSegment(sketch, "E14.14.15.12", {"start": v(95.65, -32.96) * mm, "end": v(94.07, -30.23) * mm});
            skLineSegment(sketch, "E14.17.15.12", {"start": v(94.07, -30.23) * mm, "end": v(95.65, -27.5) * mm});
            skLineSegment(sketch, "E14.0.15.13", {"start": v(95.65, -18.86) * mm, "end": v(98.8, -18.86) * mm});
            skLineSegment(sketch, "E14.3.15.13", {"start": v(98.8, -18.86) * mm, "end": v(100.38, -21.6) * mm});
            skLineSegment(sketch, "E14.6.15.13", {"start": v(100.38, -21.6) * mm, "end": v(98.8, -24.32) * mm});
            skCircle(sketch, "E14.9.15.13", {"center": v(97.23, -21.6) * mm, "radius": 2.73 * mm, "construction": true});
            skLineSegment(sketch, "E14.11.15.13", {"start": v(98.8, -24.32) * mm, "end": v(95.65, -24.32) * mm});
            skLineSegment(sketch, "E14.14.15.13", {"start": v(95.65, -24.32) * mm, "end": v(94.07, -21.6) * mm});
            skLineSegment(sketch, "E14.17.15.13", {"start": v(94.07, -21.59) * mm, "end": v(95.65, -18.86) * mm});
            skLineSegment(sketch, "E14.0.15.14", {"start": v(95.65, -10.22) * mm, "end": v(98.8, -10.22) * mm});
            skLineSegment(sketch, "E14.3.15.14", {"start": v(98.8, -10.22) * mm, "end": v(100.38, -12.95) * mm});
            skLineSegment(sketch, "E14.6.15.14", {"start": v(100.38, -12.95) * mm, "end": v(98.8, -15.68) * mm});
            skCircle(sketch, "E14.9.15.14", {"center": v(97.23, -12.95) * mm, "radius": 2.73 * mm, "construction": true});
            skLineSegment(sketch, "E14.11.15.14", {"start": v(98.8, -15.68) * mm, "end": v(95.65, -15.68) * mm});
            skLineSegment(sketch, "E14.14.15.14", {"start": v(95.65, -15.68) * mm, "end": v(94.07, -12.95) * mm});
            skLineSegment(sketch, "E14.17.15.14", {"start": v(94.07, -12.95) * mm, "end": v(95.65, -10.22) * mm});
            skLineSegment(sketch, "E14.0.15.15", {"start": v(95.65, -1.59) * mm, "end": v(98.8, -1.59) * mm});
            skLineSegment(sketch, "E14.3.15.15", {"start": v(98.8, -1.59) * mm, "end": v(100.38, -4.32) * mm});
            skLineSegment(sketch, "E14.6.15.15", {"start": v(100.38, -4.32) * mm, "end": v(98.8, -7.05) * mm});
            skCircle(sketch, "E14.9.15.15", {"center": v(97.23, -4.32) * mm, "radius": 2.73 * mm, "construction": true});
            skLineSegment(sketch, "E14.11.15.15", {"start": v(98.8, -7.05) * mm, "end": v(95.65, -7.05) * mm});
            skLineSegment(sketch, "E14.14.15.15", {"start": v(95.65, -7.05) * mm, "end": v(94.07, -4.32) * mm});
            skLineSegment(sketch, "E14.17.15.15", {"start": v(94.07, -4.32) * mm, "end": v(95.65, -1.59) * mm});
            skLineSegment(sketch, "E14.0.15.16", {"start": v(95.65, 7.05) * mm, "end": v(98.8, 7.05) * mm});
            skLineSegment(sketch, "E14.3.15.16", {"start": v(98.8, 7.05) * mm, "end": v(100.38, 4.32) * mm});
            skLineSegment(sketch, "E14.6.15.16", {"start": v(100.38, 4.32) * mm, "end": v(98.8, 1.59) * mm});
            skCircle(sketch, "E14.9.15.16", {"center": v(97.23, 4.32) * mm, "radius": 2.73 * mm, "construction": true});
            skLineSegment(sketch, "E14.11.15.16", {"start": v(98.8, 1.59) * mm, "end": v(95.65, 1.59) * mm});
            skLineSegment(sketch, "E14.14.15.16", {"start": v(95.65, 1.59) * mm, "end": v(94.07, 4.32) * mm});
            skLineSegment(sketch, "E14.17.15.16", {"start": v(94.07, 4.32) * mm, "end": v(95.65, 7.05) * mm});
            skLineSegment(sketch, "E14.0.15.17", {"start": v(95.65, 15.68) * mm, "end": v(98.8, 15.68) * mm});
            skLineSegment(sketch, "E14.3.15.17", {"start": v(98.8, 15.68) * mm, "end": v(100.38, 12.95) * mm});
            skLineSegment(sketch, "E14.6.15.17", {"start": v(100.38, 12.95) * mm, "end": v(98.8, 10.22) * mm});
            skCircle(sketch, "E14.9.15.17", {"center": v(97.23, 12.95) * mm, "radius": 2.73 * mm, "construction": true});
            skLineSegment(sketch, "E14.11.15.17", {"start": v(98.8, 10.22) * mm, "end": v(95.65, 10.22) * mm});
            skLineSegment(sketch, "E14.14.15.17", {"start": v(95.65, 10.22) * mm, "end": v(94.07, 12.95) * mm});
            skLineSegment(sketch, "E14.17.15.17", {"start": v(94.07, 12.95) * mm, "end": v(95.65, 15.68) * mm});
            skLineSegment(sketch, "E14.0.15.18", {"start": v(95.65, 24.32) * mm, "end": v(98.8, 24.32) * mm});
            skLineSegment(sketch, "E14.3.15.18", {"start": v(98.8, 24.32) * mm, "end": v(100.38, 21.59) * mm});
            skLineSegment(sketch, "E14.6.15.18", {"start": v(100.38, 21.59) * mm, "end": v(98.8, 18.86) * mm});
            skCircle(sketch, "E14.9.15.18", {"center": v(97.23, 21.59) * mm, "radius": 2.73 * mm, "construction": true});
            skLineSegment(sketch, "E14.11.15.18", {"start": v(98.8, 18.86) * mm, "end": v(95.65, 18.86) * mm});
            skLineSegment(sketch, "E14.14.15.18", {"start": v(95.65, 18.86) * mm, "end": v(94.07, 21.59) * mm});
            skLineSegment(sketch, "E14.17.15.18", {"start": v(94.07, 21.59) * mm, "end": v(95.65, 24.32) * mm});
            skLineSegment(sketch, "E14.0.15.19", {"start": v(95.65, 32.96) * mm, "end": v(98.8, 32.96) * mm});
            skLineSegment(sketch, "E14.3.15.19", {"start": v(98.8, 32.96) * mm, "end": v(100.38, 30.23) * mm});
            skLineSegment(sketch, "E14.6.15.19", {"start": v(100.38, 30.23) * mm, "end": v(98.8, 27.5) * mm});
            skCircle(sketch, "E14.9.15.19", {"center": v(97.23, 30.23) * mm, "radius": 2.73 * mm, "construction": true});
            skLineSegment(sketch, "E14.11.15.19", {"start": v(98.8, 27.5) * mm, "end": v(95.65, 27.5) * mm});
            skLineSegment(sketch, "E14.14.15.19", {"start": v(95.65, 27.5) * mm, "end": v(94.07, 30.23) * mm});
            skLineSegment(sketch, "E14.17.15.19", {"start": v(94.07, 30.23) * mm, "end": v(95.65, 32.96) * mm});
            skLineSegment(sketch, "E14.0.16.0", {"start": v(110.6, -131.13) * mm, "end": v(113.76, -131.13) * mm});
            skLineSegment(sketch, "E14.3.16.0", {"start": v(113.76, -131.13) * mm, "end": v(115.34, -133.86) * mm});
            skLineSegment(sketch, "E14.6.16.0", {"start": v(115.34, -133.86) * mm, "end": v(113.76, -136.59) * mm});
            skCircle(sketch, "E14.9.16.0", {"center": v(112.19, -133.86) * mm, "radius": 2.73 * mm, "construction": true});
            skLineSegment(sketch, "E14.11.16.0", {"start": v(113.76, -136.59) * mm, "end": v(110.6, -136.59) * mm});
            skLineSegment(sketch, "E14.14.16.0", {"start": v(110.6, -136.59) * mm, "end": v(109.03, -133.86) * mm});
            skLineSegment(sketch, "E14.17.16.0", {"start": v(109.03, -133.86) * mm, "end": v(110.6, -131.13) * mm});
            skLineSegment(sketch, "E14.0.16.1", {"start": v(110.6, -122.5) * mm, "end": v(113.76, -122.5) * mm});
            skLineSegment(sketch, "E14.3.16.1", {"start": v(113.76, -122.5) * mm, "end": v(115.34, -125.22) * mm});
            skLineSegment(sketch, "E14.6.16.1", {"start": v(115.34, -125.22) * mm, "end": v(113.76, -127.95) * mm});
            skCircle(sketch, "E14.9.16.1", {"center": v(112.19, -125.22) * mm, "radius": 2.73 * mm, "construction": true});
            skLineSegment(sketch, "E14.11.16.1", {"start": v(113.76, -127.95) * mm, "end": v(110.6, -127.95) * mm});
            skLineSegment(sketch, "E14.14.16.1", {"start": v(110.6, -127.95) * mm, "end": v(109.03, -125.22) * mm});
            skLineSegment(sketch, "E14.17.16.1", {"start": v(109.03, -125.22) * mm, "end": v(110.6, -122.5) * mm});
            skLineSegment(sketch, "E14.0.16.2", {"start": v(110.6, -113.86) * mm, "end": v(113.76, -113.86) * mm});
            skLineSegment(sketch, "E14.3.16.2", {"start": v(113.76, -113.86) * mm, "end": v(115.34, -116.59) * mm});
            skLineSegment(sketch, "E14.6.16.2", {"start": v(115.34, -116.59) * mm, "end": v(113.76, -119.32) * mm});
            skCircle(sketch, "E14.9.16.2", {"center": v(112.19, -116.59) * mm, "radius": 2.73 * mm, "construction": true});
            skLineSegment(sketch, "E14.11.16.2", {"start": v(113.76, -119.32) * mm, "end": v(110.6, -119.32) * mm});
            skLineSegment(sketch, "E14.14.16.2", {"start": v(110.6, -119.32) * mm, "end": v(109.03, -116.59) * mm});
            skLineSegment(sketch, "E14.17.16.2", {"start": v(109.03, -116.59) * mm, "end": v(110.6, -113.86) * mm});
            skLineSegment(sketch, "E14.0.16.3", {"start": v(110.6, -105.22) * mm, "end": v(113.76, -105.22) * mm});
            skLineSegment(sketch, "E14.3.16.3", {"start": v(113.76, -105.22) * mm, "end": v(115.34, -107.95) * mm});
            skLineSegment(sketch, "E14.6.16.3", {"start": v(115.34, -107.95) * mm, "end": v(113.76, -110.68) * mm});
            skCircle(sketch, "E14.9.16.3", {"center": v(112.19, -107.95) * mm, "radius": 2.73 * mm, "construction": true});
            skLineSegment(sketch, "E14.11.16.3", {"start": v(113.76, -110.68) * mm, "end": v(110.6, -110.68) * mm});
            skLineSegment(sketch, "E14.14.16.3", {"start": v(110.6, -110.68) * mm, "end": v(109.03, -107.95) * mm});
            skLineSegment(sketch, "E14.17.16.3", {"start": v(109.03, -107.95) * mm, "end": v(110.6, -105.22) * mm});
            skLineSegment(sketch, "E14.0.16.4", {"start": v(110.6, -96.58) * mm, "end": v(113.76, -96.58) * mm});
            skLineSegment(sketch, "E14.3.16.4", {"start": v(113.76, -96.58) * mm, "end": v(115.34, -99.31) * mm});
            skLineSegment(sketch, "E14.6.16.4", {"start": v(115.34, -99.31) * mm, "end": v(113.76, -102.04) * mm});
            skCircle(sketch, "E14.9.16.4", {"center": v(112.19, -99.31) * mm, "radius": 2.73 * mm, "construction": true});
            skLineSegment(sketch, "E14.11.16.4", {"start": v(113.76, -102.04) * mm, "end": v(110.6, -102.04) * mm});
            skLineSegment(sketch, "E14.14.16.4", {"start": v(110.6, -102.04) * mm, "end": v(109.03, -99.31) * mm});
            skLineSegment(sketch, "E14.17.16.4", {"start": v(109.03, -99.31) * mm, "end": v(110.6, -96.58) * mm});
            skLineSegment(sketch, "E14.0.16.5", {"start": v(110.6, -87.95) * mm, "end": v(113.76, -87.95) * mm});
            skLineSegment(sketch, "E14.3.16.5", {"start": v(113.76, -87.95) * mm, "end": v(115.34, -90.68) * mm});
            skLineSegment(sketch, "E14.6.16.5", {"start": v(115.34, -90.68) * mm, "end": v(113.76, -93.4) * mm});
            skCircle(sketch, "E14.9.16.5", {"center": v(112.19, -90.68) * mm, "radius": 2.73 * mm, "construction": true});
            skLineSegment(sketch, "E14.11.16.5", {"start": v(113.76, -93.4) * mm, "end": v(110.6, -93.4) * mm});
            skLineSegment(sketch, "E14.14.16.5", {"start": v(110.6, -93.4) * mm, "end": v(109.03, -90.68) * mm});
            skLineSegment(sketch, "E14.17.16.5", {"start": v(109.03, -90.68) * mm, "end": v(110.6, -87.95) * mm});
            skLineSegment(sketch, "E14.0.16.6", {"start": v(110.6, -79.31) * mm, "end": v(113.76, -79.31) * mm});
            skLineSegment(sketch, "E14.3.16.6", {"start": v(113.76, -79.31) * mm, "end": v(115.34, -82.04) * mm});
            skLineSegment(sketch, "E14.6.16.6", {"start": v(115.34, -82.04) * mm, "end": v(113.76, -84.77) * mm});
            skCircle(sketch, "E14.9.16.6", {"center": v(112.19, -82.04) * mm, "radius": 2.73 * mm, "construction": true});
            skLineSegment(sketch, "E14.11.16.6", {"start": v(113.76, -84.77) * mm, "end": v(110.6, -84.77) * mm});
            skLineSegment(sketch, "E14.14.16.6", {"start": v(110.6, -84.77) * mm, "end": v(109.03, -82.04) * mm});
            skLineSegment(sketch, "E14.17.16.6", {"start": v(109.03, -82.04) * mm, "end": v(110.6, -79.31) * mm});
            skLineSegment(sketch, "E14.0.16.7", {"start": v(110.6, -70.68) * mm, "end": v(113.76, -70.68) * mm});
            skLineSegment(sketch, "E14.3.16.7", {"start": v(113.76, -70.68) * mm, "end": v(115.34, -73.4) * mm});
            skLineSegment(sketch, "E14.6.16.7", {"start": v(115.34, -73.4) * mm, "end": v(113.76, -76.14) * mm});
            skCircle(sketch, "E14.9.16.7", {"center": v(112.19, -73.4) * mm, "radius": 2.73 * mm, "construction": true});
            skLineSegment(sketch, "E14.11.16.7", {"start": v(113.76, -76.14) * mm, "end": v(110.6, -76.14) * mm});
            skLineSegment(sketch, "E14.14.16.7", {"start": v(110.6, -76.14) * mm, "end": v(109.03, -73.4) * mm});
            skLineSegment(sketch, "E14.17.16.7", {"start": v(109.03, -73.4) * mm, "end": v(110.6, -70.68) * mm});
            skLineSegment(sketch, "E14.0.16.8", {"start": v(110.6, -62.04) * mm, "end": v(113.76, -62.04) * mm});
            skLineSegment(sketch, "E14.3.16.8", {"start": v(113.76, -62.04) * mm, "end": v(115.34, -64.77) * mm});
            skLineSegment(sketch, "E14.6.16.8", {"start": v(115.34, -64.77) * mm, "end": v(113.76, -67.5) * mm});
            skCircle(sketch, "E14.9.16.8", {"center": v(112.19, -64.77) * mm, "radius": 2.73 * mm, "construction": true});
            skLineSegment(sketch, "E14.11.16.8", {"start": v(113.76, -67.5) * mm, "end": v(110.6, -67.5) * mm});
            skLineSegment(sketch, "E14.14.16.8", {"start": v(110.6, -67.5) * mm, "end": v(109.03, -64.77) * mm});
            skLineSegment(sketch, "E14.17.16.8", {"start": v(109.03, -64.77) * mm, "end": v(110.6, -62.04) * mm});
            skLineSegment(sketch, "E14.0.16.9", {"start": v(110.6, -53.4) * mm, "end": v(113.76, -53.4) * mm});
            skLineSegment(sketch, "E14.3.16.9", {"start": v(113.76, -53.4) * mm, "end": v(115.34, -56.13) * mm});
            skLineSegment(sketch, "E14.6.16.9", {"start": v(115.34, -56.13) * mm, "end": v(113.76, -58.86) * mm});
            skCircle(sketch, "E14.9.16.9", {"center": v(112.19, -56.13) * mm, "radius": 2.73 * mm, "construction": true});
            skLineSegment(sketch, "E14.11.16.9", {"start": v(113.76, -58.86) * mm, "end": v(110.6, -58.86) * mm});
            skLineSegment(sketch, "E14.14.16.9", {"start": v(110.6, -58.86) * mm, "end": v(109.03, -56.13) * mm});
            skLineSegment(sketch, "E14.17.16.9", {"start": v(109.03, -56.13) * mm, "end": v(110.6, -53.4) * mm});
            skLineSegment(sketch, "E14.0.16.10", {"start": v(110.6, -44.77) * mm, "end": v(113.76, -44.77) * mm});
            skLineSegment(sketch, "E14.3.16.10", {"start": v(113.76, -44.77) * mm, "end": v(115.34, -47.5) * mm});
            skLineSegment(sketch, "E14.6.16.10", {"start": v(115.34, -47.5) * mm, "end": v(113.76, -50.23) * mm});
            skCircle(sketch, "E14.9.16.10", {"center": v(112.19, -47.5) * mm, "radius": 2.73 * mm, "construction": true});
            skLineSegment(sketch, "E14.11.16.10", {"start": v(113.76, -50.23) * mm, "end": v(110.6, -50.23) * mm});
            skLineSegment(sketch, "E14.14.16.10", {"start": v(110.6, -50.23) * mm, "end": v(109.03, -47.5) * mm});
            skLineSegment(sketch, "E14.17.16.10", {"start": v(109.03, -47.5) * mm, "end": v(110.6, -44.77) * mm});
            skLineSegment(sketch, "E14.0.16.11", {"start": v(110.6, -36.13) * mm, "end": v(113.76, -36.13) * mm});
            skLineSegment(sketch, "E14.3.16.11", {"start": v(113.76, -36.13) * mm, "end": v(115.34, -38.86) * mm});
            skLineSegment(sketch, "E14.6.16.11", {"start": v(115.34, -38.86) * mm, "end": v(113.76, -41.6) * mm});
            skCircle(sketch, "E14.9.16.11", {"center": v(112.19, -38.86) * mm, "radius": 2.73 * mm, "construction": true});
            skLineSegment(sketch, "E14.11.16.11", {"start": v(113.76, -41.6) * mm, "end": v(110.6, -41.6) * mm});
            skLineSegment(sketch, "E14.14.16.11", {"start": v(110.6, -41.6) * mm, "end": v(109.03, -38.86) * mm});
            skLineSegment(sketch, "E14.17.16.11", {"start": v(109.03, -38.86) * mm, "end": v(110.6, -36.13) * mm});
            skLineSegment(sketch, "E14.0.16.12", {"start": v(110.6, -27.5) * mm, "end": v(113.76, -27.5) * mm});
            skLineSegment(sketch, "E14.3.16.12", {"start": v(113.76, -27.5) * mm, "end": v(115.34, -30.23) * mm});
            skLineSegment(sketch, "E14.6.16.12", {"start": v(115.34, -30.23) * mm, "end": v(113.76, -32.96) * mm});
            skCircle(sketch, "E14.9.16.12", {"center": v(112.19, -30.23) * mm, "radius": 2.73 * mm, "construction": true});
            skLineSegment(sketch, "E14.11.16.12", {"start": v(113.76, -32.96) * mm, "end": v(110.6, -32.96) * mm});
            skLineSegment(sketch, "E14.14.16.12", {"start": v(110.6, -32.96) * mm, "end": v(109.03, -30.23) * mm});
            skLineSegment(sketch, "E14.17.16.12", {"start": v(109.03, -30.23) * mm, "end": v(110.6, -27.5) * mm});
            skLineSegment(sketch, "E14.0.16.13", {"start": v(110.6, -18.86) * mm, "end": v(113.76, -18.86) * mm});
            skLineSegment(sketch, "E14.3.16.13", {"start": v(113.76, -18.86) * mm, "end": v(115.34, -21.6) * mm});
            skLineSegment(sketch, "E14.6.16.13", {"start": v(115.34, -21.6) * mm, "end": v(113.76, -24.32) * mm});
            skCircle(sketch, "E14.9.16.13", {"center": v(112.19, -21.6) * mm, "radius": 2.73 * mm, "construction": true});
            skLineSegment(sketch, "E14.11.16.13", {"start": v(113.76, -24.32) * mm, "end": v(110.6, -24.32) * mm});
            skLineSegment(sketch, "E14.14.16.13", {"start": v(110.6, -24.32) * mm, "end": v(109.03, -21.6) * mm});
            skLineSegment(sketch, "E14.17.16.13", {"start": v(109.03, -21.59) * mm, "end": v(110.6, -18.86) * mm});
            skLineSegment(sketch, "E14.0.16.14", {"start": v(110.6, -10.22) * mm, "end": v(113.76, -10.22) * mm});
            skLineSegment(sketch, "E14.3.16.14", {"start": v(113.76, -10.22) * mm, "end": v(115.34, -12.95) * mm});
            skLineSegment(sketch, "E14.6.16.14", {"start": v(115.34, -12.95) * mm, "end": v(113.76, -15.68) * mm});
            skCircle(sketch, "E14.9.16.14", {"center": v(112.19, -12.95) * mm, "radius": 2.73 * mm, "construction": true});
            skLineSegment(sketch, "E14.11.16.14", {"start": v(113.76, -15.68) * mm, "end": v(110.6, -15.68) * mm});
            skLineSegment(sketch, "E14.14.16.14", {"start": v(110.6, -15.68) * mm, "end": v(109.03, -12.95) * mm});
            skLineSegment(sketch, "E14.17.16.14", {"start": v(109.03, -12.95) * mm, "end": v(110.6, -10.22) * mm});
            skLineSegment(sketch, "E14.0.16.15", {"start": v(110.6, -1.59) * mm, "end": v(113.76, -1.59) * mm});
            skLineSegment(sketch, "E14.3.16.15", {"start": v(113.76, -1.59) * mm, "end": v(115.34, -4.32) * mm});
            skLineSegment(sketch, "E14.6.16.15", {"start": v(115.34, -4.32) * mm, "end": v(113.76, -7.05) * mm});
            skCircle(sketch, "E14.9.16.15", {"center": v(112.19, -4.32) * mm, "radius": 2.73 * mm, "construction": true});
            skLineSegment(sketch, "E14.11.16.15", {"start": v(113.76, -7.05) * mm, "end": v(110.6, -7.05) * mm});
            skLineSegment(sketch, "E14.14.16.15", {"start": v(110.6, -7.05) * mm, "end": v(109.03, -4.32) * mm});
            skLineSegment(sketch, "E14.17.16.15", {"start": v(109.03, -4.32) * mm, "end": v(110.6, -1.59) * mm});
            skLineSegment(sketch, "E14.0.16.16", {"start": v(110.6, 7.05) * mm, "end": v(113.76, 7.05) * mm});
            skLineSegment(sketch, "E14.3.16.16", {"start": v(113.76, 7.05) * mm, "end": v(115.34, 4.32) * mm});
            skLineSegment(sketch, "E14.6.16.16", {"start": v(115.34, 4.32) * mm, "end": v(113.76, 1.59) * mm});
            skCircle(sketch, "E14.9.16.16", {"center": v(112.19, 4.32) * mm, "radius": 2.73 * mm, "construction": true});
            skLineSegment(sketch, "E14.11.16.16", {"start": v(113.76, 1.59) * mm, "end": v(110.6, 1.59) * mm});
            skLineSegment(sketch, "E14.14.16.16", {"start": v(110.6, 1.59) * mm, "end": v(109.03, 4.32) * mm});
            skLineSegment(sketch, "E14.17.16.16", {"start": v(109.03, 4.32) * mm, "end": v(110.6, 7.05) * mm});
            skLineSegment(sketch, "E14.0.16.17", {"start": v(110.6, 15.68) * mm, "end": v(113.76, 15.68) * mm});
            skLineSegment(sketch, "E14.3.16.17", {"start": v(113.76, 15.68) * mm, "end": v(115.34, 12.95) * mm});
            skLineSegment(sketch, "E14.6.16.17", {"start": v(115.34, 12.95) * mm, "end": v(113.76, 10.22) * mm});
            skCircle(sketch, "E14.9.16.17", {"center": v(112.19, 12.95) * mm, "radius": 2.73 * mm, "construction": true});
            skLineSegment(sketch, "E14.11.16.17", {"start": v(113.76, 10.22) * mm, "end": v(110.6, 10.22) * mm});
            skLineSegment(sketch, "E14.14.16.17", {"start": v(110.6, 10.22) * mm, "end": v(109.03, 12.95) * mm});
            skLineSegment(sketch, "E14.17.16.17", {"start": v(109.03, 12.95) * mm, "end": v(110.6, 15.68) * mm});
            skLineSegment(sketch, "E14.0.16.18", {"start": v(110.6, 24.32) * mm, "end": v(113.76, 24.32) * mm});
            skLineSegment(sketch, "E14.3.16.18", {"start": v(113.76, 24.32) * mm, "end": v(115.34, 21.59) * mm});
            skLineSegment(sketch, "E14.6.16.18", {"start": v(115.34, 21.59) * mm, "end": v(113.76, 18.86) * mm});
            skCircle(sketch, "E14.9.16.18", {"center": v(112.19, 21.59) * mm, "radius": 2.73 * mm, "construction": true});
            skLineSegment(sketch, "E14.11.16.18", {"start": v(113.76, 18.86) * mm, "end": v(110.6, 18.86) * mm});
            skLineSegment(sketch, "E14.14.16.18", {"start": v(110.6, 18.86) * mm, "end": v(109.03, 21.59) * mm});
            skLineSegment(sketch, "E14.17.16.18", {"start": v(109.03, 21.59) * mm, "end": v(110.6, 24.32) * mm});
            skLineSegment(sketch, "E14.0.16.19", {"start": v(110.6, 32.96) * mm, "end": v(113.76, 32.96) * mm});
            skLineSegment(sketch, "E14.3.16.19", {"start": v(113.76, 32.96) * mm, "end": v(115.34, 30.23) * mm});
            skLineSegment(sketch, "E14.6.16.19", {"start": v(115.34, 30.23) * mm, "end": v(113.76, 27.5) * mm});
            skCircle(sketch, "E14.9.16.19", {"center": v(112.19, 30.23) * mm, "radius": 2.73 * mm, "construction": true});
            skLineSegment(sketch, "E14.11.16.19", {"start": v(113.76, 27.5) * mm, "end": v(110.6, 27.5) * mm});
            skLineSegment(sketch, "E14.14.16.19", {"start": v(110.6, 27.5) * mm, "end": v(109.03, 30.23) * mm});
            skLineSegment(sketch, "E14.17.16.19", {"start": v(109.03, 30.23) * mm, "end": v(110.6, 32.96) * mm});
            skLineSegment(sketch, "E14.0.17.0", {"start": v(125.57, -131.13) * mm, "end": v(128.72, -131.13) * mm});
            skLineSegment(sketch, "E14.3.17.0", {"start": v(128.72, -131.13) * mm, "end": v(130.3, -133.86) * mm});
            skLineSegment(sketch, "E14.6.17.0", {"start": v(130.3, -133.86) * mm, "end": v(128.72, -136.59) * mm});
            skCircle(sketch, "E14.9.17.0", {"center": v(127.14, -133.86) * mm, "radius": 2.73 * mm, "construction": true});
            skLineSegment(sketch, "E14.11.17.0", {"start": v(128.72, -136.59) * mm, "end": v(125.57, -136.59) * mm});
            skLineSegment(sketch, "E14.14.17.0", {"start": v(125.57, -136.59) * mm, "end": v(124, -133.86) * mm});
            skLineSegment(sketch, "E14.17.17.0", {"start": v(124, -133.86) * mm, "end": v(125.57, -131.13) * mm});
            skLineSegment(sketch, "E14.0.17.1", {"start": v(125.57, -122.5) * mm, "end": v(128.72, -122.5) * mm});
            skLineSegment(sketch, "E14.3.17.1", {"start": v(128.72, -122.5) * mm, "end": v(130.3, -125.22) * mm});
            skLineSegment(sketch, "E14.6.17.1", {"start": v(130.3, -125.22) * mm, "end": v(128.72, -127.95) * mm});
            skCircle(sketch, "E14.9.17.1", {"center": v(127.14, -125.22) * mm, "radius": 2.73 * mm, "construction": true});
            skLineSegment(sketch, "E14.11.17.1", {"start": v(128.72, -127.95) * mm, "end": v(125.57, -127.95) * mm});
            skLineSegment(sketch, "E14.14.17.1", {"start": v(125.57, -127.95) * mm, "end": v(124, -125.22) * mm});
            skLineSegment(sketch, "E14.17.17.1", {"start": v(124, -125.22) * mm, "end": v(125.57, -122.5) * mm});
            skLineSegment(sketch, "E14.0.17.2", {"start": v(125.57, -113.86) * mm, "end": v(128.72, -113.86) * mm});
            skLineSegment(sketch, "E14.3.17.2", {"start": v(128.72, -113.86) * mm, "end": v(130.3, -116.59) * mm});
            skLineSegment(sketch, "E14.6.17.2", {"start": v(130.3, -116.59) * mm, "end": v(128.72, -119.32) * mm});
            skCircle(sketch, "E14.9.17.2", {"center": v(127.14, -116.59) * mm, "radius": 2.73 * mm, "construction": true});
            skLineSegment(sketch, "E14.11.17.2", {"start": v(128.72, -119.32) * mm, "end": v(125.57, -119.32) * mm});
            skLineSegment(sketch, "E14.14.17.2", {"start": v(125.57, -119.32) * mm, "end": v(124, -116.59) * mm});
            skLineSegment(sketch, "E14.17.17.2", {"start": v(124, -116.59) * mm, "end": v(125.57, -113.86) * mm});
            skLineSegment(sketch, "E14.0.17.3", {"start": v(125.57, -105.22) * mm, "end": v(128.72, -105.22) * mm});
            skLineSegment(sketch, "E14.3.17.3", {"start": v(128.72, -105.22) * mm, "end": v(130.3, -107.95) * mm});
            skLineSegment(sketch, "E14.6.17.3", {"start": v(130.3, -107.95) * mm, "end": v(128.72, -110.68) * mm});
            skCircle(sketch, "E14.9.17.3", {"center": v(127.14, -107.95) * mm, "radius": 2.73 * mm, "construction": true});
            skLineSegment(sketch, "E14.11.17.3", {"start": v(128.72, -110.68) * mm, "end": v(125.57, -110.68) * mm});
            skLineSegment(sketch, "E14.14.17.3", {"start": v(125.57, -110.68) * mm, "end": v(124, -107.95) * mm});
            skLineSegment(sketch, "E14.17.17.3", {"start": v(124, -107.95) * mm, "end": v(125.57, -105.22) * mm});
            skLineSegment(sketch, "E14.0.17.4", {"start": v(125.57, -96.58) * mm, "end": v(128.72, -96.58) * mm});
            skLineSegment(sketch, "E14.3.17.4", {"start": v(128.72, -96.58) * mm, "end": v(130.3, -99.31) * mm});
            skLineSegment(sketch, "E14.6.17.4", {"start": v(130.3, -99.31) * mm, "end": v(128.72, -102.04) * mm});
            skCircle(sketch, "E14.9.17.4", {"center": v(127.14, -99.31) * mm, "radius": 2.73 * mm, "construction": true});
            skLineSegment(sketch, "E14.11.17.4", {"start": v(128.72, -102.04) * mm, "end": v(125.57, -102.04) * mm});
            skLineSegment(sketch, "E14.14.17.4", {"start": v(125.57, -102.04) * mm, "end": v(124, -99.31) * mm});
            skLineSegment(sketch, "E14.17.17.4", {"start": v(124, -99.31) * mm, "end": v(125.57, -96.58) * mm});
            skLineSegment(sketch, "E14.0.17.5", {"start": v(125.57, -87.95) * mm, "end": v(128.72, -87.95) * mm});
            skLineSegment(sketch, "E14.3.17.5", {"start": v(128.72, -87.95) * mm, "end": v(130.3, -90.68) * mm});
            skLineSegment(sketch, "E14.6.17.5", {"start": v(130.3, -90.68) * mm, "end": v(128.72, -93.4) * mm});
            skCircle(sketch, "E14.9.17.5", {"center": v(127.14, -90.68) * mm, "radius": 2.73 * mm, "construction": true});
            skLineSegment(sketch, "E14.11.17.5", {"start": v(128.72, -93.4) * mm, "end": v(125.57, -93.4) * mm});
            skLineSegment(sketch, "E14.14.17.5", {"start": v(125.57, -93.4) * mm, "end": v(124, -90.68) * mm});
            skLineSegment(sketch, "E14.17.17.5", {"start": v(124, -90.68) * mm, "end": v(125.57, -87.95) * mm});
            skLineSegment(sketch, "E14.0.17.6", {"start": v(125.57, -79.31) * mm, "end": v(128.72, -79.31) * mm});
            skLineSegment(sketch, "E14.3.17.6", {"start": v(128.72, -79.31) * mm, "end": v(130.3, -82.04) * mm});
            skLineSegment(sketch, "E14.6.17.6", {"start": v(130.3, -82.04) * mm, "end": v(128.72, -84.77) * mm});
            skCircle(sketch, "E14.9.17.6", {"center": v(127.14, -82.04) * mm, "radius": 2.73 * mm, "construction": true});
            skLineSegment(sketch, "E14.11.17.6", {"start": v(128.72, -84.77) * mm, "end": v(125.57, -84.77) * mm});
            skLineSegment(sketch, "E14.14.17.6", {"start": v(125.57, -84.77) * mm, "end": v(124, -82.04) * mm});
            skLineSegment(sketch, "E14.17.17.6", {"start": v(124, -82.04) * mm, "end": v(125.57, -79.31) * mm});
            skLineSegment(sketch, "E14.0.17.7", {"start": v(125.57, -70.68) * mm, "end": v(128.72, -70.68) * mm});
            skLineSegment(sketch, "E14.3.17.7", {"start": v(128.72, -70.68) * mm, "end": v(130.3, -73.4) * mm});
            skLineSegment(sketch, "E14.6.17.7", {"start": v(130.3, -73.4) * mm, "end": v(128.72, -76.14) * mm});
            skCircle(sketch, "E14.9.17.7", {"center": v(127.14, -73.4) * mm, "radius": 2.73 * mm, "construction": true});
            skLineSegment(sketch, "E14.11.17.7", {"start": v(128.72, -76.14) * mm, "end": v(125.57, -76.14) * mm});
            skLineSegment(sketch, "E14.14.17.7", {"start": v(125.57, -76.14) * mm, "end": v(124, -73.4) * mm});
            skLineSegment(sketch, "E14.17.17.7", {"start": v(124, -73.4) * mm, "end": v(125.57, -70.68) * mm});
            skLineSegment(sketch, "E14.0.17.8", {"start": v(125.57, -62.04) * mm, "end": v(128.72, -62.04) * mm});
            skLineSegment(sketch, "E14.3.17.8", {"start": v(128.72, -62.04) * mm, "end": v(130.3, -64.77) * mm});
            skLineSegment(sketch, "E14.6.17.8", {"start": v(130.3, -64.77) * mm, "end": v(128.72, -67.5) * mm});
            skCircle(sketch, "E14.9.17.8", {"center": v(127.14, -64.77) * mm, "radius": 2.73 * mm, "construction": true});
            skLineSegment(sketch, "E14.11.17.8", {"start": v(128.72, -67.5) * mm, "end": v(125.57, -67.5) * mm});
            skLineSegment(sketch, "E14.14.17.8", {"start": v(125.57, -67.5) * mm, "end": v(124, -64.77) * mm});
            skLineSegment(sketch, "E14.17.17.8", {"start": v(124, -64.77) * mm, "end": v(125.57, -62.04) * mm});
            skLineSegment(sketch, "E14.0.17.9", {"start": v(125.57, -53.4) * mm, "end": v(128.72, -53.4) * mm});
            skLineSegment(sketch, "E14.3.17.9", {"start": v(128.72, -53.4) * mm, "end": v(130.3, -56.13) * mm});
            skLineSegment(sketch, "E14.6.17.9", {"start": v(130.3, -56.13) * mm, "end": v(128.72, -58.86) * mm});
            skCircle(sketch, "E14.9.17.9", {"center": v(127.14, -56.13) * mm, "radius": 2.73 * mm, "construction": true});
            skLineSegment(sketch, "E14.11.17.9", {"start": v(128.72, -58.86) * mm, "end": v(125.57, -58.86) * mm});
            skLineSegment(sketch, "E14.14.17.9", {"start": v(125.57, -58.86) * mm, "end": v(124, -56.13) * mm});
            skLineSegment(sketch, "E14.17.17.9", {"start": v(124, -56.13) * mm, "end": v(125.57, -53.4) * mm});
            skLineSegment(sketch, "E14.0.17.10", {"start": v(125.57, -44.77) * mm, "end": v(128.72, -44.77) * mm});
            skLineSegment(sketch, "E14.3.17.10", {"start": v(128.72, -44.77) * mm, "end": v(130.3, -47.5) * mm});
            skLineSegment(sketch, "E14.6.17.10", {"start": v(130.3, -47.5) * mm, "end": v(128.72, -50.23) * mm});
            skCircle(sketch, "E14.9.17.10", {"center": v(127.14, -47.5) * mm, "radius": 2.73 * mm, "construction": true});
            skLineSegment(sketch, "E14.11.17.10", {"start": v(128.72, -50.23) * mm, "end": v(125.57, -50.23) * mm});
            skLineSegment(sketch, "E14.14.17.10", {"start": v(125.57, -50.23) * mm, "end": v(124, -47.5) * mm});
            skLineSegment(sketch, "E14.17.17.10", {"start": v(124, -47.5) * mm, "end": v(125.57, -44.77) * mm});
            skLineSegment(sketch, "E14.0.17.11", {"start": v(125.57, -36.13) * mm, "end": v(128.72, -36.13) * mm});
            skLineSegment(sketch, "E14.3.17.11", {"start": v(128.72, -36.13) * mm, "end": v(130.3, -38.86) * mm});
            skLineSegment(sketch, "E14.6.17.11", {"start": v(130.3, -38.86) * mm, "end": v(128.72, -41.6) * mm});
            skCircle(sketch, "E14.9.17.11", {"center": v(127.14, -38.86) * mm, "radius": 2.73 * mm, "construction": true});
            skLineSegment(sketch, "E14.11.17.11", {"start": v(128.72, -41.6) * mm, "end": v(125.57, -41.6) * mm});
            skLineSegment(sketch, "E14.14.17.11", {"start": v(125.57, -41.6) * mm, "end": v(124, -38.86) * mm});
            skLineSegment(sketch, "E14.17.17.11", {"start": v(124, -38.86) * mm, "end": v(125.57, -36.13) * mm});
            skLineSegment(sketch, "E14.0.17.12", {"start": v(125.57, -27.5) * mm, "end": v(128.72, -27.5) * mm});
            skLineSegment(sketch, "E14.3.17.12", {"start": v(128.72, -27.5) * mm, "end": v(130.3, -30.23) * mm});
            skLineSegment(sketch, "E14.6.17.12", {"start": v(130.3, -30.23) * mm, "end": v(128.72, -32.96) * mm});
            skCircle(sketch, "E14.9.17.12", {"center": v(127.14, -30.23) * mm, "radius": 2.73 * mm, "construction": true});
            skLineSegment(sketch, "E14.11.17.12", {"start": v(128.72, -32.96) * mm, "end": v(125.57, -32.96) * mm});
            skLineSegment(sketch, "E14.14.17.12", {"start": v(125.57, -32.96) * mm, "end": v(124, -30.23) * mm});
            skLineSegment(sketch, "E14.17.17.12", {"start": v(124, -30.23) * mm, "end": v(125.57, -27.5) * mm});
            skLineSegment(sketch, "E14.0.17.13", {"start": v(125.57, -18.86) * mm, "end": v(128.72, -18.86) * mm});
            skLineSegment(sketch, "E14.3.17.13", {"start": v(128.72, -18.86) * mm, "end": v(130.3, -21.6) * mm});
            skLineSegment(sketch, "E14.6.17.13", {"start": v(130.3, -21.6) * mm, "end": v(128.72, -24.32) * mm});
            skCircle(sketch, "E14.9.17.13", {"center": v(127.14, -21.6) * mm, "radius": 2.73 * mm, "construction": true});
            skLineSegment(sketch, "E14.11.17.13", {"start": v(128.72, -24.32) * mm, "end": v(125.57, -24.32) * mm});
            skLineSegment(sketch, "E14.14.17.13", {"start": v(125.57, -24.32) * mm, "end": v(124, -21.6) * mm});
            skLineSegment(sketch, "E14.17.17.13", {"start": v(124, -21.59) * mm, "end": v(125.57, -18.86) * mm});
            skLineSegment(sketch, "E14.0.17.14", {"start": v(125.57, -10.22) * mm, "end": v(128.72, -10.22) * mm});
            skLineSegment(sketch, "E14.3.17.14", {"start": v(128.72, -10.22) * mm, "end": v(130.3, -12.95) * mm});
            skLineSegment(sketch, "E14.6.17.14", {"start": v(130.3, -12.95) * mm, "end": v(128.72, -15.68) * mm});
            skCircle(sketch, "E14.9.17.14", {"center": v(127.14, -12.95) * mm, "radius": 2.73 * mm, "construction": true});
            skLineSegment(sketch, "E14.11.17.14", {"start": v(128.72, -15.68) * mm, "end": v(125.57, -15.68) * mm});
            skLineSegment(sketch, "E14.14.17.14", {"start": v(125.57, -15.68) * mm, "end": v(124, -12.95) * mm});
            skLineSegment(sketch, "E14.17.17.14", {"start": v(124, -12.95) * mm, "end": v(125.57, -10.22) * mm});
            skLineSegment(sketch, "E14.0.17.15", {"start": v(125.57, -1.59) * mm, "end": v(128.72, -1.59) * mm});
            skLineSegment(sketch, "E14.3.17.15", {"start": v(128.72, -1.59) * mm, "end": v(130.3, -4.32) * mm});
            skLineSegment(sketch, "E14.6.17.15", {"start": v(130.3, -4.32) * mm, "end": v(128.72, -7.05) * mm});
            skCircle(sketch, "E14.9.17.15", {"center": v(127.14, -4.32) * mm, "radius": 2.73 * mm, "construction": true});
            skLineSegment(sketch, "E14.11.17.15", {"start": v(128.72, -7.05) * mm, "end": v(125.57, -7.05) * mm});
            skLineSegment(sketch, "E14.14.17.15", {"start": v(125.57, -7.05) * mm, "end": v(124, -4.32) * mm});
            skLineSegment(sketch, "E14.17.17.15", {"start": v(124, -4.32) * mm, "end": v(125.57, -1.59) * mm});
            skLineSegment(sketch, "E14.0.17.16", {"start": v(125.57, 7.05) * mm, "end": v(128.72, 7.05) * mm});
            skLineSegment(sketch, "E14.3.17.16", {"start": v(128.72, 7.05) * mm, "end": v(130.3, 4.32) * mm});
            skLineSegment(sketch, "E14.6.17.16", {"start": v(130.3, 4.32) * mm, "end": v(128.72, 1.59) * mm});
            skCircle(sketch, "E14.9.17.16", {"center": v(127.14, 4.32) * mm, "radius": 2.73 * mm, "construction": true});
            skLineSegment(sketch, "E14.11.17.16", {"start": v(128.72, 1.59) * mm, "end": v(125.57, 1.59) * mm});
            skLineSegment(sketch, "E14.14.17.16", {"start": v(125.57, 1.59) * mm, "end": v(124, 4.32) * mm});
            skLineSegment(sketch, "E14.17.17.16", {"start": v(124, 4.32) * mm, "end": v(125.57, 7.05) * mm});
            skLineSegment(sketch, "E14.0.17.17", {"start": v(125.57, 15.68) * mm, "end": v(128.72, 15.68) * mm});
            skLineSegment(sketch, "E14.3.17.17", {"start": v(128.72, 15.68) * mm, "end": v(130.3, 12.95) * mm});
            skLineSegment(sketch, "E14.6.17.17", {"start": v(130.3, 12.95) * mm, "end": v(128.72, 10.22) * mm});
            skCircle(sketch, "E14.9.17.17", {"center": v(127.14, 12.95) * mm, "radius": 2.73 * mm, "construction": true});
            skLineSegment(sketch, "E14.11.17.17", {"start": v(128.72, 10.22) * mm, "end": v(125.57, 10.22) * mm});
            skLineSegment(sketch, "E14.14.17.17", {"start": v(125.57, 10.22) * mm, "end": v(124, 12.95) * mm});
            skLineSegment(sketch, "E14.17.17.17", {"start": v(124, 12.95) * mm, "end": v(125.57, 15.68) * mm});
            skLineSegment(sketch, "E14.0.17.18", {"start": v(125.57, 24.32) * mm, "end": v(128.72, 24.32) * mm});
            skLineSegment(sketch, "E14.3.17.18", {"start": v(128.72, 24.32) * mm, "end": v(130.3, 21.59) * mm});
            skLineSegment(sketch, "E14.6.17.18", {"start": v(130.3, 21.59) * mm, "end": v(128.72, 18.86) * mm});
            skCircle(sketch, "E14.9.17.18", {"center": v(127.14, 21.59) * mm, "radius": 2.73 * mm, "construction": true});
            skLineSegment(sketch, "E14.11.17.18", {"start": v(128.72, 18.86) * mm, "end": v(125.57, 18.86) * mm});
            skLineSegment(sketch, "E14.14.17.18", {"start": v(125.57, 18.86) * mm, "end": v(124, 21.59) * mm});
            skLineSegment(sketch, "E14.17.17.18", {"start": v(124, 21.59) * mm, "end": v(125.57, 24.32) * mm});
            skLineSegment(sketch, "E14.0.17.19", {"start": v(125.57, 32.96) * mm, "end": v(128.72, 32.96) * mm});
            skLineSegment(sketch, "E14.3.17.19", {"start": v(128.72, 32.96) * mm, "end": v(130.3, 30.23) * mm});
            skLineSegment(sketch, "E14.6.17.19", {"start": v(130.3, 30.23) * mm, "end": v(128.72, 27.5) * mm});
            skCircle(sketch, "E14.9.17.19", {"center": v(127.14, 30.23) * mm, "radius": 2.73 * mm, "construction": true});
            skLineSegment(sketch, "E14.11.17.19", {"start": v(128.72, 27.5) * mm, "end": v(125.57, 27.5) * mm});
            skLineSegment(sketch, "E14.14.17.19", {"start": v(125.57, 27.5) * mm, "end": v(124, 30.23) * mm});
            skLineSegment(sketch, "E14.17.17.19", {"start": v(124, 30.23) * mm, "end": v(125.57, 32.96) * mm});
            skLineSegment(sketch, "E14.0.18.0", {"start": v(140.53, -131.13) * mm, "end": v(143.68, -131.13) * mm});
            skLineSegment(sketch, "E14.3.18.0", {"start": v(143.68, -131.13) * mm, "end": v(145.25, -133.86) * mm});
            skLineSegment(sketch, "E14.6.18.0", {"start": v(145.25, -133.86) * mm, "end": v(143.68, -136.59) * mm});
            skCircle(sketch, "E14.9.18.0", {"center": v(142.1, -133.86) * mm, "radius": 2.73 * mm, "construction": true});
            skLineSegment(sketch, "E14.11.18.0", {"start": v(143.68, -136.59) * mm, "end": v(140.53, -136.59) * mm});
            skLineSegment(sketch, "E14.14.18.0", {"start": v(140.53, -136.59) * mm, "end": v(138.95, -133.86) * mm});
            skLineSegment(sketch, "E14.17.18.0", {"start": v(138.95, -133.86) * mm, "end": v(140.53, -131.13) * mm});
            skLineSegment(sketch, "E14.0.18.1", {"start": v(140.53, -122.5) * mm, "end": v(143.68, -122.5) * mm});
            skLineSegment(sketch, "E14.3.18.1", {"start": v(143.68, -122.5) * mm, "end": v(145.25, -125.22) * mm});
            skLineSegment(sketch, "E14.6.18.1", {"start": v(145.25, -125.22) * mm, "end": v(143.68, -127.95) * mm});
            skCircle(sketch, "E14.9.18.1", {"center": v(142.1, -125.22) * mm, "radius": 2.73 * mm, "construction": true});
            skLineSegment(sketch, "E14.11.18.1", {"start": v(143.68, -127.95) * mm, "end": v(140.53, -127.95) * mm});
            skLineSegment(sketch, "E14.14.18.1", {"start": v(140.53, -127.95) * mm, "end": v(138.95, -125.22) * mm});
            skLineSegment(sketch, "E14.17.18.1", {"start": v(138.95, -125.22) * mm, "end": v(140.53, -122.5) * mm});
            skLineSegment(sketch, "E14.0.18.2", {"start": v(140.53, -113.86) * mm, "end": v(143.68, -113.86) * mm});
            skLineSegment(sketch, "E14.3.18.2", {"start": v(143.68, -113.86) * mm, "end": v(145.25, -116.59) * mm});
            skLineSegment(sketch, "E14.6.18.2", {"start": v(145.25, -116.59) * mm, "end": v(143.68, -119.32) * mm});
            skCircle(sketch, "E14.9.18.2", {"center": v(142.1, -116.59) * mm, "radius": 2.73 * mm, "construction": true});
            skLineSegment(sketch, "E14.11.18.2", {"start": v(143.68, -119.32) * mm, "end": v(140.53, -119.32) * mm});
            skLineSegment(sketch, "E14.14.18.2", {"start": v(140.53, -119.32) * mm, "end": v(138.95, -116.59) * mm});
            skLineSegment(sketch, "E14.17.18.2", {"start": v(138.95, -116.59) * mm, "end": v(140.53, -113.86) * mm});
            skLineSegment(sketch, "E14.0.18.3", {"start": v(140.53, -105.22) * mm, "end": v(143.68, -105.22) * mm});
            skLineSegment(sketch, "E14.3.18.3", {"start": v(143.68, -105.22) * mm, "end": v(145.25, -107.95) * mm});
            skLineSegment(sketch, "E14.6.18.3", {"start": v(145.25, -107.95) * mm, "end": v(143.68, -110.68) * mm});
            skCircle(sketch, "E14.9.18.3", {"center": v(142.1, -107.95) * mm, "radius": 2.73 * mm, "construction": true});
            skLineSegment(sketch, "E14.11.18.3", {"start": v(143.68, -110.68) * mm, "end": v(140.53, -110.68) * mm});
            skLineSegment(sketch, "E14.14.18.3", {"start": v(140.53, -110.68) * mm, "end": v(138.95, -107.95) * mm});
            skLineSegment(sketch, "E14.17.18.3", {"start": v(138.95, -107.95) * mm, "end": v(140.53, -105.22) * mm});
            skLineSegment(sketch, "E14.0.18.4", {"start": v(140.53, -96.58) * mm, "end": v(143.68, -96.58) * mm});
            skLineSegment(sketch, "E14.3.18.4", {"start": v(143.68, -96.58) * mm, "end": v(145.25, -99.31) * mm});
            skLineSegment(sketch, "E14.6.18.4", {"start": v(145.25, -99.31) * mm, "end": v(143.68, -102.04) * mm});
            skCircle(sketch, "E14.9.18.4", {"center": v(142.1, -99.31) * mm, "radius": 2.73 * mm, "construction": true});
            skLineSegment(sketch, "E14.11.18.4", {"start": v(143.68, -102.04) * mm, "end": v(140.53, -102.04) * mm});
            skLineSegment(sketch, "E14.14.18.4", {"start": v(140.53, -102.04) * mm, "end": v(138.95, -99.31) * mm});
            skLineSegment(sketch, "E14.17.18.4", {"start": v(138.95, -99.31) * mm, "end": v(140.53, -96.58) * mm});
            skLineSegment(sketch, "E14.0.18.5", {"start": v(140.53, -87.95) * mm, "end": v(143.68, -87.95) * mm});
            skLineSegment(sketch, "E14.3.18.5", {"start": v(143.68, -87.95) * mm, "end": v(145.25, -90.68) * mm});
            skLineSegment(sketch, "E14.6.18.5", {"start": v(145.25, -90.68) * mm, "end": v(143.68, -93.4) * mm});
            skCircle(sketch, "E14.9.18.5", {"center": v(142.1, -90.68) * mm, "radius": 2.73 * mm, "construction": true});
            skLineSegment(sketch, "E14.11.18.5", {"start": v(143.68, -93.4) * mm, "end": v(140.53, -93.4) * mm});
            skLineSegment(sketch, "E14.14.18.5", {"start": v(140.53, -93.4) * mm, "end": v(138.95, -90.68) * mm});
            skLineSegment(sketch, "E14.17.18.5", {"start": v(138.95, -90.68) * mm, "end": v(140.53, -87.95) * mm});
            skLineSegment(sketch, "E14.0.18.6", {"start": v(140.53, -79.31) * mm, "end": v(143.68, -79.31) * mm});
            skLineSegment(sketch, "E14.3.18.6", {"start": v(143.68, -79.31) * mm, "end": v(145.25, -82.04) * mm});
            skLineSegment(sketch, "E14.6.18.6", {"start": v(145.25, -82.04) * mm, "end": v(143.68, -84.77) * mm});
            skCircle(sketch, "E14.9.18.6", {"center": v(142.1, -82.04) * mm, "radius": 2.73 * mm, "construction": true});
            skLineSegment(sketch, "E14.11.18.6", {"start": v(143.68, -84.77) * mm, "end": v(140.53, -84.77) * mm});
            skLineSegment(sketch, "E14.14.18.6", {"start": v(140.53, -84.77) * mm, "end": v(138.95, -82.04) * mm});
            skLineSegment(sketch, "E14.17.18.6", {"start": v(138.95, -82.04) * mm, "end": v(140.53, -79.31) * mm});
            skLineSegment(sketch, "E14.0.18.7", {"start": v(140.53, -70.68) * mm, "end": v(143.68, -70.68) * mm});
            skLineSegment(sketch, "E14.3.18.7", {"start": v(143.68, -70.68) * mm, "end": v(145.25, -73.4) * mm});
            skLineSegment(sketch, "E14.6.18.7", {"start": v(145.25, -73.4) * mm, "end": v(143.68, -76.14) * mm});
            skCircle(sketch, "E14.9.18.7", {"center": v(142.1, -73.4) * mm, "radius": 2.73 * mm, "construction": true});
            skLineSegment(sketch, "E14.11.18.7", {"start": v(143.68, -76.14) * mm, "end": v(140.53, -76.14) * mm});
            skLineSegment(sketch, "E14.14.18.7", {"start": v(140.53, -76.14) * mm, "end": v(138.95, -73.4) * mm});
            skLineSegment(sketch, "E14.17.18.7", {"start": v(138.95, -73.4) * mm, "end": v(140.53, -70.68) * mm});
            skLineSegment(sketch, "E14.0.18.8", {"start": v(140.53, -62.04) * mm, "end": v(143.68, -62.04) * mm});
            skLineSegment(sketch, "E14.3.18.8", {"start": v(143.68, -62.04) * mm, "end": v(145.25, -64.77) * mm});
            skLineSegment(sketch, "E14.6.18.8", {"start": v(145.25, -64.77) * mm, "end": v(143.68, -67.5) * mm});
            skCircle(sketch, "E14.9.18.8", {"center": v(142.1, -64.77) * mm, "radius": 2.73 * mm, "construction": true});
            skLineSegment(sketch, "E14.11.18.8", {"start": v(143.68, -67.5) * mm, "end": v(140.53, -67.5) * mm});
            skLineSegment(sketch, "E14.14.18.8", {"start": v(140.53, -67.5) * mm, "end": v(138.95, -64.77) * mm});
            skLineSegment(sketch, "E14.17.18.8", {"start": v(138.95, -64.77) * mm, "end": v(140.53, -62.04) * mm});
            skLineSegment(sketch, "E14.0.18.9", {"start": v(140.53, -53.4) * mm, "end": v(143.68, -53.4) * mm});
            skLineSegment(sketch, "E14.3.18.9", {"start": v(143.68, -53.4) * mm, "end": v(145.25, -56.13) * mm});
            skLineSegment(sketch, "E14.6.18.9", {"start": v(145.25, -56.13) * mm, "end": v(143.68, -58.86) * mm});
            skCircle(sketch, "E14.9.18.9", {"center": v(142.1, -56.13) * mm, "radius": 2.73 * mm, "construction": true});
            skLineSegment(sketch, "E14.11.18.9", {"start": v(143.68, -58.86) * mm, "end": v(140.53, -58.86) * mm});
            skLineSegment(sketch, "E14.14.18.9", {"start": v(140.53, -58.86) * mm, "end": v(138.95, -56.13) * mm});
            skLineSegment(sketch, "E14.17.18.9", {"start": v(138.95, -56.13) * mm, "end": v(140.53, -53.4) * mm});
            skLineSegment(sketch, "E14.0.18.10", {"start": v(140.53, -44.77) * mm, "end": v(143.68, -44.77) * mm});
            skLineSegment(sketch, "E14.3.18.10", {"start": v(143.68, -44.77) * mm, "end": v(145.25, -47.5) * mm});
            skLineSegment(sketch, "E14.6.18.10", {"start": v(145.25, -47.5) * mm, "end": v(143.68, -50.23) * mm});
            skCircle(sketch, "E14.9.18.10", {"center": v(142.1, -47.5) * mm, "radius": 2.73 * mm, "construction": true});
            skLineSegment(sketch, "E14.11.18.10", {"start": v(143.68, -50.23) * mm, "end": v(140.53, -50.23) * mm});
            skLineSegment(sketch, "E14.14.18.10", {"start": v(140.53, -50.23) * mm, "end": v(138.95, -47.5) * mm});
            skLineSegment(sketch, "E14.17.18.10", {"start": v(138.95, -47.5) * mm, "end": v(140.53, -44.77) * mm});
            skLineSegment(sketch, "E14.0.18.11", {"start": v(140.53, -36.13) * mm, "end": v(143.68, -36.13) * mm});
            skLineSegment(sketch, "E14.3.18.11", {"start": v(143.68, -36.13) * mm, "end": v(145.25, -38.86) * mm});
            skLineSegment(sketch, "E14.6.18.11", {"start": v(145.25, -38.86) * mm, "end": v(143.68, -41.6) * mm});
            skCircle(sketch, "E14.9.18.11", {"center": v(142.1, -38.86) * mm, "radius": 2.73 * mm, "construction": true});
            skLineSegment(sketch, "E14.11.18.11", {"start": v(143.68, -41.6) * mm, "end": v(140.53, -41.6) * mm});
            skLineSegment(sketch, "E14.14.18.11", {"start": v(140.53, -41.6) * mm, "end": v(138.95, -38.86) * mm});
            skLineSegment(sketch, "E14.17.18.11", {"start": v(138.95, -38.86) * mm, "end": v(140.53, -36.13) * mm});
            skLineSegment(sketch, "E14.0.18.12", {"start": v(140.53, -27.5) * mm, "end": v(143.68, -27.5) * mm});
            skLineSegment(sketch, "E14.3.18.12", {"start": v(143.68, -27.5) * mm, "end": v(145.25, -30.23) * mm});
            skLineSegment(sketch, "E14.6.18.12", {"start": v(145.25, -30.23) * mm, "end": v(143.68, -32.96) * mm});
            skCircle(sketch, "E14.9.18.12", {"center": v(142.1, -30.23) * mm, "radius": 2.73 * mm, "construction": true});
            skLineSegment(sketch, "E14.11.18.12", {"start": v(143.68, -32.96) * mm, "end": v(140.53, -32.96) * mm});
            skLineSegment(sketch, "E14.14.18.12", {"start": v(140.53, -32.96) * mm, "end": v(138.95, -30.23) * mm});
            skLineSegment(sketch, "E14.17.18.12", {"start": v(138.95, -30.23) * mm, "end": v(140.53, -27.5) * mm});
            skLineSegment(sketch, "E14.0.18.13", {"start": v(140.53, -18.86) * mm, "end": v(143.68, -18.86) * mm});
            skLineSegment(sketch, "E14.3.18.13", {"start": v(143.68, -18.86) * mm, "end": v(145.25, -21.6) * mm});
            skLineSegment(sketch, "E14.6.18.13", {"start": v(145.25, -21.6) * mm, "end": v(143.68, -24.32) * mm});
            skCircle(sketch, "E14.9.18.13", {"center": v(142.1, -21.6) * mm, "radius": 2.73 * mm, "construction": true});
            skLineSegment(sketch, "E14.11.18.13", {"start": v(143.68, -24.32) * mm, "end": v(140.53, -24.32) * mm});
            skLineSegment(sketch, "E14.14.18.13", {"start": v(140.53, -24.32) * mm, "end": v(138.95, -21.6) * mm});
            skLineSegment(sketch, "E14.17.18.13", {"start": v(138.95, -21.59) * mm, "end": v(140.53, -18.86) * mm});
            skLineSegment(sketch, "E14.0.18.14", {"start": v(140.53, -10.22) * mm, "end": v(143.68, -10.22) * mm});
            skLineSegment(sketch, "E14.3.18.14", {"start": v(143.68, -10.22) * mm, "end": v(145.25, -12.95) * mm});
            skLineSegment(sketch, "E14.6.18.14", {"start": v(145.25, -12.95) * mm, "end": v(143.68, -15.68) * mm});
            skCircle(sketch, "E14.9.18.14", {"center": v(142.1, -12.95) * mm, "radius": 2.73 * mm, "construction": true});
            skLineSegment(sketch, "E14.11.18.14", {"start": v(143.68, -15.68) * mm, "end": v(140.53, -15.68) * mm});
            skLineSegment(sketch, "E14.14.18.14", {"start": v(140.53, -15.68) * mm, "end": v(138.95, -12.95) * mm});
            skLineSegment(sketch, "E14.17.18.14", {"start": v(138.95, -12.95) * mm, "end": v(140.53, -10.22) * mm});
            skLineSegment(sketch, "E14.0.18.15", {"start": v(140.53, -1.59) * mm, "end": v(143.68, -1.59) * mm});
            skLineSegment(sketch, "E14.3.18.15", {"start": v(143.68, -1.59) * mm, "end": v(145.25, -4.32) * mm});
            skLineSegment(sketch, "E14.6.18.15", {"start": v(145.25, -4.32) * mm, "end": v(143.68, -7.05) * mm});
            skCircle(sketch, "E14.9.18.15", {"center": v(142.1, -4.32) * mm, "radius": 2.73 * mm, "construction": true});
            skLineSegment(sketch, "E14.11.18.15", {"start": v(143.68, -7.05) * mm, "end": v(140.53, -7.05) * mm});
            skLineSegment(sketch, "E14.14.18.15", {"start": v(140.53, -7.05) * mm, "end": v(138.95, -4.32) * mm});
            skLineSegment(sketch, "E14.17.18.15", {"start": v(138.95, -4.32) * mm, "end": v(140.53, -1.59) * mm});
            skLineSegment(sketch, "E14.0.18.16", {"start": v(140.53, 7.05) * mm, "end": v(143.68, 7.05) * mm});
            skLineSegment(sketch, "E14.3.18.16", {"start": v(143.68, 7.05) * mm, "end": v(145.25, 4.32) * mm});
            skLineSegment(sketch, "E14.6.18.16", {"start": v(145.25, 4.32) * mm, "end": v(143.68, 1.59) * mm});
            skCircle(sketch, "E14.9.18.16", {"center": v(142.1, 4.32) * mm, "radius": 2.73 * mm, "construction": true});
            skLineSegment(sketch, "E14.11.18.16", {"start": v(143.68, 1.59) * mm, "end": v(140.53, 1.59) * mm});
            skLineSegment(sketch, "E14.14.18.16", {"start": v(140.53, 1.59) * mm, "end": v(138.95, 4.32) * mm});
            skLineSegment(sketch, "E14.17.18.16", {"start": v(138.95, 4.32) * mm, "end": v(140.53, 7.05) * mm});
            skLineSegment(sketch, "E14.0.18.17", {"start": v(140.53, 15.68) * mm, "end": v(143.68, 15.68) * mm});
            skLineSegment(sketch, "E14.3.18.17", {"start": v(143.68, 15.68) * mm, "end": v(145.25, 12.95) * mm});
            skLineSegment(sketch, "E14.6.18.17", {"start": v(145.25, 12.95) * mm, "end": v(143.68, 10.22) * mm});
            skCircle(sketch, "E14.9.18.17", {"center": v(142.1, 12.95) * mm, "radius": 2.73 * mm, "construction": true});
            skLineSegment(sketch, "E14.11.18.17", {"start": v(143.68, 10.22) * mm, "end": v(140.53, 10.22) * mm});
            skLineSegment(sketch, "E14.14.18.17", {"start": v(140.53, 10.22) * mm, "end": v(138.95, 12.95) * mm});
            skLineSegment(sketch, "E14.17.18.17", {"start": v(138.95, 12.95) * mm, "end": v(140.53, 15.68) * mm});
            skLineSegment(sketch, "E14.0.18.18", {"start": v(140.53, 24.32) * mm, "end": v(143.68, 24.32) * mm});
            skLineSegment(sketch, "E14.3.18.18", {"start": v(143.68, 24.32) * mm, "end": v(145.25, 21.59) * mm});
            skLineSegment(sketch, "E14.6.18.18", {"start": v(145.25, 21.59) * mm, "end": v(143.68, 18.86) * mm});
            skCircle(sketch, "E14.9.18.18", {"center": v(142.1, 21.59) * mm, "radius": 2.73 * mm, "construction": true});
            skLineSegment(sketch, "E14.11.18.18", {"start": v(143.68, 18.86) * mm, "end": v(140.53, 18.86) * mm});
            skLineSegment(sketch, "E14.14.18.18", {"start": v(140.53, 18.86) * mm, "end": v(138.95, 21.59) * mm});
            skLineSegment(sketch, "E14.17.18.18", {"start": v(138.95, 21.59) * mm, "end": v(140.53, 24.32) * mm});
            skLineSegment(sketch, "E14.0.18.19", {"start": v(140.53, 32.96) * mm, "end": v(143.68, 32.96) * mm});
            skLineSegment(sketch, "E14.3.18.19", {"start": v(143.68, 32.96) * mm, "end": v(145.25, 30.23) * mm});
            skLineSegment(sketch, "E14.6.18.19", {"start": v(145.25, 30.23) * mm, "end": v(143.68, 27.5) * mm});
            skCircle(sketch, "E14.9.18.19", {"center": v(142.1, 30.23) * mm, "radius": 2.73 * mm, "construction": true});
            skLineSegment(sketch, "E14.11.18.19", {"start": v(143.68, 27.5) * mm, "end": v(140.53, 27.5) * mm});
            skLineSegment(sketch, "E14.14.18.19", {"start": v(140.53, 27.5) * mm, "end": v(138.95, 30.23) * mm});
            skLineSegment(sketch, "E14.17.18.19", {"start": v(138.95, 30.23) * mm, "end": v(140.53, 32.96) * mm});
            skLineSegment(sketch, "E14.0.19.0", {"start": v(155.48, -131.13) * mm, "end": v(158.64, -131.13) * mm});
            skLineSegment(sketch, "E14.3.19.0", {"start": v(158.64, -131.13) * mm, "end": v(160.21, -133.86) * mm});
            skLineSegment(sketch, "E14.6.19.0", {"start": v(160.21, -133.86) * mm, "end": v(158.64, -136.59) * mm});
            skCircle(sketch, "E14.9.19.0", {"center": v(157.06, -133.86) * mm, "radius": 2.73 * mm, "construction": true});
            skLineSegment(sketch, "E14.11.19.0", {"start": v(158.64, -136.59) * mm, "end": v(155.48, -136.59) * mm});
            skLineSegment(sketch, "E14.14.19.0", {"start": v(155.48, -136.59) * mm, "end": v(153.9, -133.86) * mm});
            skLineSegment(sketch, "E14.17.19.0", {"start": v(153.9, -133.86) * mm, "end": v(155.48, -131.13) * mm});
            skLineSegment(sketch, "E14.0.19.1", {"start": v(155.48, -122.5) * mm, "end": v(158.64, -122.5) * mm});
            skLineSegment(sketch, "E14.3.19.1", {"start": v(158.64, -122.5) * mm, "end": v(160.21, -125.22) * mm});
            skLineSegment(sketch, "E14.6.19.1", {"start": v(160.21, -125.22) * mm, "end": v(158.64, -127.95) * mm});
            skCircle(sketch, "E14.9.19.1", {"center": v(157.06, -125.22) * mm, "radius": 2.73 * mm, "construction": true});
            skLineSegment(sketch, "E14.11.19.1", {"start": v(158.64, -127.95) * mm, "end": v(155.48, -127.95) * mm});
            skLineSegment(sketch, "E14.14.19.1", {"start": v(155.48, -127.95) * mm, "end": v(153.9, -125.22) * mm});
            skLineSegment(sketch, "E14.17.19.1", {"start": v(153.9, -125.22) * mm, "end": v(155.48, -122.5) * mm});
            skLineSegment(sketch, "E14.0.19.2", {"start": v(155.48, -113.86) * mm, "end": v(158.64, -113.86) * mm});
            skLineSegment(sketch, "E14.3.19.2", {"start": v(158.64, -113.86) * mm, "end": v(160.21, -116.59) * mm});
            skLineSegment(sketch, "E14.6.19.2", {"start": v(160.21, -116.59) * mm, "end": v(158.64, -119.32) * mm});
            skCircle(sketch, "E14.9.19.2", {"center": v(157.06, -116.59) * mm, "radius": 2.73 * mm, "construction": true});
            skLineSegment(sketch, "E14.11.19.2", {"start": v(158.64, -119.32) * mm, "end": v(155.48, -119.32) * mm});
            skLineSegment(sketch, "E14.14.19.2", {"start": v(155.48, -119.32) * mm, "end": v(153.9, -116.59) * mm});
            skLineSegment(sketch, "E14.17.19.2", {"start": v(153.9, -116.59) * mm, "end": v(155.48, -113.86) * mm});
            skLineSegment(sketch, "E14.0.19.3", {"start": v(155.48, -105.22) * mm, "end": v(158.64, -105.22) * mm});
            skLineSegment(sketch, "E14.3.19.3", {"start": v(158.64, -105.22) * mm, "end": v(160.21, -107.95) * mm});
            skLineSegment(sketch, "E14.6.19.3", {"start": v(160.21, -107.95) * mm, "end": v(158.64, -110.68) * mm});
            skCircle(sketch, "E14.9.19.3", {"center": v(157.06, -107.95) * mm, "radius": 2.73 * mm, "construction": true});
            skLineSegment(sketch, "E14.11.19.3", {"start": v(158.64, -110.68) * mm, "end": v(155.48, -110.68) * mm});
            skLineSegment(sketch, "E14.14.19.3", {"start": v(155.48, -110.68) * mm, "end": v(153.9, -107.95) * mm});
            skLineSegment(sketch, "E14.17.19.3", {"start": v(153.9, -107.95) * mm, "end": v(155.48, -105.22) * mm});
            skLineSegment(sketch, "E14.0.19.4", {"start": v(155.48, -96.58) * mm, "end": v(158.64, -96.58) * mm});
            skLineSegment(sketch, "E14.3.19.4", {"start": v(158.64, -96.58) * mm, "end": v(160.21, -99.31) * mm});
            skLineSegment(sketch, "E14.6.19.4", {"start": v(160.21, -99.31) * mm, "end": v(158.64, -102.04) * mm});
            skCircle(sketch, "E14.9.19.4", {"center": v(157.06, -99.31) * mm, "radius": 2.73 * mm, "construction": true});
            skLineSegment(sketch, "E14.11.19.4", {"start": v(158.64, -102.04) * mm, "end": v(155.48, -102.04) * mm});
            skLineSegment(sketch, "E14.14.19.4", {"start": v(155.48, -102.04) * mm, "end": v(153.9, -99.31) * mm});
            skLineSegment(sketch, "E14.17.19.4", {"start": v(153.9, -99.31) * mm, "end": v(155.48, -96.58) * mm});
            skLineSegment(sketch, "E14.0.19.5", {"start": v(155.48, -87.95) * mm, "end": v(158.64, -87.95) * mm});
            skLineSegment(sketch, "E14.3.19.5", {"start": v(158.64, -87.95) * mm, "end": v(160.21, -90.68) * mm});
            skLineSegment(sketch, "E14.6.19.5", {"start": v(160.21, -90.68) * mm, "end": v(158.64, -93.4) * mm});
            skCircle(sketch, "E14.9.19.5", {"center": v(157.06, -90.68) * mm, "radius": 2.73 * mm, "construction": true});
            skLineSegment(sketch, "E14.11.19.5", {"start": v(158.64, -93.4) * mm, "end": v(155.48, -93.4) * mm});
            skLineSegment(sketch, "E14.14.19.5", {"start": v(155.48, -93.4) * mm, "end": v(153.9, -90.68) * mm});
            skLineSegment(sketch, "E14.17.19.5", {"start": v(153.9, -90.68) * mm, "end": v(155.48, -87.95) * mm});
            skLineSegment(sketch, "E14.0.19.6", {"start": v(155.48, -79.31) * mm, "end": v(158.64, -79.31) * mm});
            skLineSegment(sketch, "E14.3.19.6", {"start": v(158.64, -79.31) * mm, "end": v(160.21, -82.04) * mm});
            skLineSegment(sketch, "E14.6.19.6", {"start": v(160.21, -82.04) * mm, "end": v(158.64, -84.77) * mm});
            skCircle(sketch, "E14.9.19.6", {"center": v(157.06, -82.04) * mm, "radius": 2.73 * mm, "construction": true});
            skLineSegment(sketch, "E14.11.19.6", {"start": v(158.64, -84.77) * mm, "end": v(155.48, -84.77) * mm});
            skLineSegment(sketch, "E14.14.19.6", {"start": v(155.48, -84.77) * mm, "end": v(153.9, -82.04) * mm});
            skLineSegment(sketch, "E14.17.19.6", {"start": v(153.9, -82.04) * mm, "end": v(155.48, -79.31) * mm});
            skLineSegment(sketch, "E14.0.19.7", {"start": v(155.48, -70.68) * mm, "end": v(158.64, -70.68) * mm});
            skLineSegment(sketch, "E14.3.19.7", {"start": v(158.64, -70.68) * mm, "end": v(160.21, -73.4) * mm});
            skLineSegment(sketch, "E14.6.19.7", {"start": v(160.21, -73.4) * mm, "end": v(158.64, -76.14) * mm});
            skCircle(sketch, "E14.9.19.7", {"center": v(157.06, -73.4) * mm, "radius": 2.73 * mm, "construction": true});
            skLineSegment(sketch, "E14.11.19.7", {"start": v(158.64, -76.14) * mm, "end": v(155.48, -76.14) * mm});
            skLineSegment(sketch, "E14.14.19.7", {"start": v(155.48, -76.14) * mm, "end": v(153.9, -73.4) * mm});
            skLineSegment(sketch, "E14.17.19.7", {"start": v(153.9, -73.4) * mm, "end": v(155.48, -70.68) * mm});
            skLineSegment(sketch, "E14.0.19.8", {"start": v(155.48, -62.04) * mm, "end": v(158.64, -62.04) * mm});
            skLineSegment(sketch, "E14.3.19.8", {"start": v(158.64, -62.04) * mm, "end": v(160.21, -64.77) * mm});
            skLineSegment(sketch, "E14.6.19.8", {"start": v(160.21, -64.77) * mm, "end": v(158.64, -67.5) * mm});
            skCircle(sketch, "E14.9.19.8", {"center": v(157.06, -64.77) * mm, "radius": 2.73 * mm, "construction": true});
            skLineSegment(sketch, "E14.11.19.8", {"start": v(158.64, -67.5) * mm, "end": v(155.48, -67.5) * mm});
            skLineSegment(sketch, "E14.14.19.8", {"start": v(155.48, -67.5) * mm, "end": v(153.9, -64.77) * mm});
            skLineSegment(sketch, "E14.17.19.8", {"start": v(153.9, -64.77) * mm, "end": v(155.48, -62.04) * mm});
            skLineSegment(sketch, "E14.0.19.9", {"start": v(155.48, -53.4) * mm, "end": v(158.64, -53.4) * mm});
            skLineSegment(sketch, "E14.3.19.9", {"start": v(158.64, -53.4) * mm, "end": v(160.21, -56.13) * mm});
            skLineSegment(sketch, "E14.6.19.9", {"start": v(160.21, -56.13) * mm, "end": v(158.64, -58.86) * mm});
            skCircle(sketch, "E14.9.19.9", {"center": v(157.06, -56.13) * mm, "radius": 2.73 * mm, "construction": true});
            skLineSegment(sketch, "E14.11.19.9", {"start": v(158.64, -58.86) * mm, "end": v(155.48, -58.86) * mm});
            skLineSegment(sketch, "E14.14.19.9", {"start": v(155.48, -58.86) * mm, "end": v(153.9, -56.13) * mm});
            skLineSegment(sketch, "E14.17.19.9", {"start": v(153.9, -56.13) * mm, "end": v(155.48, -53.4) * mm});
            skLineSegment(sketch, "E14.0.19.10", {"start": v(155.48, -44.77) * mm, "end": v(158.64, -44.77) * mm});
            skLineSegment(sketch, "E14.3.19.10", {"start": v(158.64, -44.77) * mm, "end": v(160.21, -47.5) * mm});
            skLineSegment(sketch, "E14.6.19.10", {"start": v(160.21, -47.5) * mm, "end": v(158.64, -50.23) * mm});
            skCircle(sketch, "E14.9.19.10", {"center": v(157.06, -47.5) * mm, "radius": 2.73 * mm, "construction": true});
            skLineSegment(sketch, "E14.11.19.10", {"start": v(158.64, -50.23) * mm, "end": v(155.48, -50.23) * mm});
            skLineSegment(sketch, "E14.14.19.10", {"start": v(155.48, -50.23) * mm, "end": v(153.9, -47.5) * mm});
            skLineSegment(sketch, "E14.17.19.10", {"start": v(153.9, -47.5) * mm, "end": v(155.48, -44.77) * mm});
            skLineSegment(sketch, "E14.0.19.11", {"start": v(155.48, -36.13) * mm, "end": v(158.64, -36.13) * mm});
            skLineSegment(sketch, "E14.3.19.11", {"start": v(158.64, -36.13) * mm, "end": v(160.21, -38.86) * mm});
            skLineSegment(sketch, "E14.6.19.11", {"start": v(160.21, -38.86) * mm, "end": v(158.64, -41.6) * mm});
            skCircle(sketch, "E14.9.19.11", {"center": v(157.06, -38.86) * mm, "radius": 2.73 * mm, "construction": true});
            skLineSegment(sketch, "E14.11.19.11", {"start": v(158.64, -41.6) * mm, "end": v(155.48, -41.6) * mm});
            skLineSegment(sketch, "E14.14.19.11", {"start": v(155.48, -41.6) * mm, "end": v(153.9, -38.86) * mm});
            skLineSegment(sketch, "E14.17.19.11", {"start": v(153.9, -38.86) * mm, "end": v(155.48, -36.13) * mm});
            skLineSegment(sketch, "E14.0.19.12", {"start": v(155.48, -27.5) * mm, "end": v(158.64, -27.5) * mm});
            skLineSegment(sketch, "E14.3.19.12", {"start": v(158.64, -27.5) * mm, "end": v(160.21, -30.23) * mm});
            skLineSegment(sketch, "E14.6.19.12", {"start": v(160.21, -30.23) * mm, "end": v(158.64, -32.96) * mm});
            skCircle(sketch, "E14.9.19.12", {"center": v(157.06, -30.23) * mm, "radius": 2.73 * mm, "construction": true});
            skLineSegment(sketch, "E14.11.19.12", {"start": v(158.64, -32.96) * mm, "end": v(155.48, -32.96) * mm});
            skLineSegment(sketch, "E14.14.19.12", {"start": v(155.48, -32.96) * mm, "end": v(153.9, -30.23) * mm});
            skLineSegment(sketch, "E14.17.19.12", {"start": v(153.9, -30.23) * mm, "end": v(155.48, -27.5) * mm});
            skLineSegment(sketch, "E14.0.19.13", {"start": v(155.48, -18.86) * mm, "end": v(158.64, -18.86) * mm});
            skLineSegment(sketch, "E14.3.19.13", {"start": v(158.64, -18.86) * mm, "end": v(160.21, -21.6) * mm});
            skLineSegment(sketch, "E14.6.19.13", {"start": v(160.21, -21.6) * mm, "end": v(158.64, -24.32) * mm});
            skCircle(sketch, "E14.9.19.13", {"center": v(157.06, -21.6) * mm, "radius": 2.73 * mm, "construction": true});
            skLineSegment(sketch, "E14.11.19.13", {"start": v(158.64, -24.32) * mm, "end": v(155.48, -24.32) * mm});
            skLineSegment(sketch, "E14.14.19.13", {"start": v(155.48, -24.32) * mm, "end": v(153.9, -21.6) * mm});
            skLineSegment(sketch, "E14.17.19.13", {"start": v(153.9, -21.59) * mm, "end": v(155.48, -18.86) * mm});
            skLineSegment(sketch, "E14.0.19.14", {"start": v(155.48, -10.22) * mm, "end": v(158.64, -10.22) * mm});
            skLineSegment(sketch, "E14.3.19.14", {"start": v(158.64, -10.22) * mm, "end": v(160.21, -12.95) * mm});
            skLineSegment(sketch, "E14.6.19.14", {"start": v(160.21, -12.95) * mm, "end": v(158.64, -15.68) * mm});
            skCircle(sketch, "E14.9.19.14", {"center": v(157.06, -12.95) * mm, "radius": 2.73 * mm, "construction": true});
            skLineSegment(sketch, "E14.11.19.14", {"start": v(158.64, -15.68) * mm, "end": v(155.48, -15.68) * mm});
            skLineSegment(sketch, "E14.14.19.14", {"start": v(155.48, -15.68) * mm, "end": v(153.9, -12.95) * mm});
            skLineSegment(sketch, "E14.17.19.14", {"start": v(153.9, -12.95) * mm, "end": v(155.48, -10.22) * mm});
            skLineSegment(sketch, "E14.0.19.15", {"start": v(155.48, -1.59) * mm, "end": v(158.64, -1.59) * mm});
            skLineSegment(sketch, "E14.3.19.15", {"start": v(158.64, -1.59) * mm, "end": v(160.21, -4.32) * mm});
            skLineSegment(sketch, "E14.6.19.15", {"start": v(160.21, -4.32) * mm, "end": v(158.64, -7.05) * mm});
            skCircle(sketch, "E14.9.19.15", {"center": v(157.06, -4.32) * mm, "radius": 2.73 * mm, "construction": true});
            skLineSegment(sketch, "E14.11.19.15", {"start": v(158.64, -7.05) * mm, "end": v(155.48, -7.05) * mm});
            skLineSegment(sketch, "E14.14.19.15", {"start": v(155.48, -7.05) * mm, "end": v(153.9, -4.32) * mm});
            skLineSegment(sketch, "E14.17.19.15", {"start": v(153.9, -4.32) * mm, "end": v(155.48, -1.59) * mm});
            skLineSegment(sketch, "E14.0.19.16", {"start": v(155.48, 7.05) * mm, "end": v(158.64, 7.05) * mm});
            skLineSegment(sketch, "E14.3.19.16", {"start": v(158.64, 7.05) * mm, "end": v(160.21, 4.32) * mm});
            skLineSegment(sketch, "E14.6.19.16", {"start": v(160.21, 4.32) * mm, "end": v(158.64, 1.59) * mm});
            skCircle(sketch, "E14.9.19.16", {"center": v(157.06, 4.32) * mm, "radius": 2.73 * mm, "construction": true});
            skLineSegment(sketch, "E14.11.19.16", {"start": v(158.64, 1.59) * mm, "end": v(155.48, 1.59) * mm});
            skLineSegment(sketch, "E14.14.19.16", {"start": v(155.48, 1.59) * mm, "end": v(153.9, 4.32) * mm});
            skLineSegment(sketch, "E14.17.19.16", {"start": v(153.9, 4.32) * mm, "end": v(155.48, 7.05) * mm});
            skLineSegment(sketch, "E14.0.19.17", {"start": v(155.48, 15.68) * mm, "end": v(158.64, 15.68) * mm});
            skLineSegment(sketch, "E14.3.19.17", {"start": v(158.64, 15.68) * mm, "end": v(160.21, 12.95) * mm});
            skLineSegment(sketch, "E14.6.19.17", {"start": v(160.21, 12.95) * mm, "end": v(158.64, 10.22) * mm});
            skCircle(sketch, "E14.9.19.17", {"center": v(157.06, 12.95) * mm, "radius": 2.73 * mm, "construction": true});
            skLineSegment(sketch, "E14.11.19.17", {"start": v(158.64, 10.22) * mm, "end": v(155.48, 10.22) * mm});
            skLineSegment(sketch, "E14.14.19.17", {"start": v(155.48, 10.22) * mm, "end": v(153.9, 12.95) * mm});
            skLineSegment(sketch, "E14.17.19.17", {"start": v(153.9, 12.95) * mm, "end": v(155.48, 15.68) * mm});
            skLineSegment(sketch, "E14.0.19.18", {"start": v(155.48, 24.32) * mm, "end": v(158.64, 24.32) * mm});
            skLineSegment(sketch, "E14.3.19.18", {"start": v(158.64, 24.32) * mm, "end": v(160.21, 21.59) * mm});
            skLineSegment(sketch, "E14.6.19.18", {"start": v(160.21, 21.59) * mm, "end": v(158.64, 18.86) * mm});
            skCircle(sketch, "E14.9.19.18", {"center": v(157.06, 21.59) * mm, "radius": 2.73 * mm, "construction": true});
            skLineSegment(sketch, "E14.11.19.18", {"start": v(158.64, 18.86) * mm, "end": v(155.48, 18.86) * mm});
            skLineSegment(sketch, "E14.14.19.18", {"start": v(155.48, 18.86) * mm, "end": v(153.9, 21.59) * mm});
            skLineSegment(sketch, "E14.17.19.18", {"start": v(153.9, 21.6) * mm, "end": v(155.48, 24.32) * mm});
            skLineSegment(sketch, "E14.0.19.19", {"start": v(155.48, 32.96) * mm, "end": v(158.64, 32.96) * mm});
            skLineSegment(sketch, "E14.3.19.19", {"start": v(158.64, 32.96) * mm, "end": v(160.21, 30.23) * mm});
            skLineSegment(sketch, "E14.6.19.19", {"start": v(160.21, 30.23) * mm, "end": v(158.64, 27.5) * mm});
            skCircle(sketch, "E14.9.19.19", {"center": v(157.06, 30.23) * mm, "radius": 2.73 * mm, "construction": true});
            skLineSegment(sketch, "E14.11.19.19", {"start": v(158.64, 27.5) * mm, "end": v(155.48, 27.5) * mm});
            skLineSegment(sketch, "E14.14.19.19", {"start": v(155.48, 27.5) * mm, "end": v(153.9, 30.23) * mm});
            skLineSegment(sketch, "E14.17.19.19", {"start": v(153.9, 30.23) * mm, "end": v(155.48, 32.96) * mm});
            skCircle(sketch, "E15.0.0.20", {"center": v(-119.66, 43.18) * mm, "radius": 2.73 * mm, "construction": true});
            skLineSegment(sketch, "E15.2.0.20", {"start": v(-122.82, 43.18) * mm, "end": v(-121.24, 45.91) * mm});
            skLineSegment(sketch, "E15.5.0.20", {"start": v(-121.24, 45.91) * mm, "end": v(-118.09, 45.91) * mm});
            skLineSegment(sketch, "E15.8.0.20", {"start": v(-118.09, 45.91) * mm, "end": v(-116.51, 43.18) * mm});
            skLineSegment(sketch, "E15.11.0.20", {"start": v(-116.51, 43.18) * mm, "end": v(-118.09, 40.45) * mm});
            skLineSegment(sketch, "E15.14.0.20", {"start": v(-118.09, 40.45) * mm, "end": v(-121.24, 40.45) * mm});
            skLineSegment(sketch, "E15.17.0.20", {"start": v(-121.24, 40.45) * mm, "end": v(-122.82, 43.18) * mm});
            skCircle(sketch, "E15.0.0.21", {"center": v(-119.66, 51.82) * mm, "radius": 2.73 * mm, "construction": true});
            skLineSegment(sketch, "E15.2.0.21", {"start": v(-122.82, 51.82) * mm, "end": v(-121.24, 54.55) * mm});
            skLineSegment(sketch, "E15.5.0.21", {"start": v(-121.24, 54.55) * mm, "end": v(-118.09, 54.55) * mm});
            skLineSegment(sketch, "E15.8.0.21", {"start": v(-118.09, 54.55) * mm, "end": v(-116.51, 51.82) * mm});
            skLineSegment(sketch, "E15.11.0.21", {"start": v(-116.51, 51.82) * mm, "end": v(-118.09, 49.09) * mm});
            skLineSegment(sketch, "E15.14.0.21", {"start": v(-118.09, 49.09) * mm, "end": v(-121.24, 49.09) * mm});
            skLineSegment(sketch, "E15.17.0.21", {"start": v(-121.24, 49.09) * mm, "end": v(-122.82, 51.82) * mm});
            skCircle(sketch, "E15.0.0.22", {"center": v(-119.66, 60.45) * mm, "radius": 2.73 * mm, "construction": true});
            skLineSegment(sketch, "E15.2.0.22", {"start": v(-122.82, 60.45) * mm, "end": v(-121.24, 63.18) * mm});
            skLineSegment(sketch, "E15.5.0.22", {"start": v(-121.24, 63.18) * mm, "end": v(-118.09, 63.18) * mm});
            skLineSegment(sketch, "E15.8.0.22", {"start": v(-118.09, 63.18) * mm, "end": v(-116.51, 60.45) * mm});
            skLineSegment(sketch, "E15.11.0.22", {"start": v(-116.51, 60.45) * mm, "end": v(-118.09, 57.72) * mm});
            skLineSegment(sketch, "E15.14.0.22", {"start": v(-118.09, 57.72) * mm, "end": v(-121.24, 57.72) * mm});
            skLineSegment(sketch, "E15.17.0.22", {"start": v(-121.24, 57.72) * mm, "end": v(-122.82, 60.45) * mm});
            skCircle(sketch, "E15.0.0.23", {"center": v(-119.66, 69.09) * mm, "radius": 2.73 * mm, "construction": true});
            skLineSegment(sketch, "E15.2.0.23", {"start": v(-122.82, 69.09) * mm, "end": v(-121.24, 71.82) * mm});
            skLineSegment(sketch, "E15.5.0.23", {"start": v(-121.24, 71.82) * mm, "end": v(-118.09, 71.82) * mm});
            skLineSegment(sketch, "E15.8.0.23", {"start": v(-118.09, 71.82) * mm, "end": v(-116.51, 69.09) * mm});
            skLineSegment(sketch, "E15.11.0.23", {"start": v(-116.51, 69.09) * mm, "end": v(-118.09, 66.36) * mm});
            skLineSegment(sketch, "E15.14.0.23", {"start": v(-118.09, 66.36) * mm, "end": v(-121.24, 66.36) * mm});
            skLineSegment(sketch, "E15.17.0.23", {"start": v(-121.24, 66.36) * mm, "end": v(-122.82, 69.09) * mm});
            skCircle(sketch, "E15.0.0.24", {"center": v(-119.66, 77.72) * mm, "radius": 2.73 * mm, "construction": true});
            skLineSegment(sketch, "E15.2.0.24", {"start": v(-122.82, 77.72) * mm, "end": v(-121.24, 80.45) * mm});
            skLineSegment(sketch, "E15.5.0.24", {"start": v(-121.24, 80.45) * mm, "end": v(-118.09, 80.45) * mm});
            skLineSegment(sketch, "E15.8.0.24", {"start": v(-118.09, 80.45) * mm, "end": v(-116.51, 77.72) * mm});
            skLineSegment(sketch, "E15.11.0.24", {"start": v(-116.51, 77.72) * mm, "end": v(-118.09, 75) * mm});
            skLineSegment(sketch, "E15.14.0.24", {"start": v(-118.09, 75) * mm, "end": v(-121.24, 75) * mm});
            skLineSegment(sketch, "E15.17.0.24", {"start": v(-121.24, 75) * mm, "end": v(-122.82, 77.72) * mm});
            skCircle(sketch, "E15.0.1.20", {"center": v(-104.7, 43.18) * mm, "radius": 2.73 * mm, "construction": true});
            skLineSegment(sketch, "E15.2.1.20", {"start": v(-107.86, 43.18) * mm, "end": v(-106.28, 45.91) * mm});
            skLineSegment(sketch, "E15.5.1.20", {"start": v(-106.28, 45.91) * mm, "end": v(-103.13, 45.91) * mm});
            skLineSegment(sketch, "E15.8.1.20", {"start": v(-103.13, 45.91) * mm, "end": v(-101.55, 43.18) * mm});
            skLineSegment(sketch, "E15.11.1.20", {"start": v(-101.55, 43.18) * mm, "end": v(-103.13, 40.45) * mm});
            skLineSegment(sketch, "E15.14.1.20", {"start": v(-103.13, 40.45) * mm, "end": v(-106.28, 40.45) * mm});
            skLineSegment(sketch, "E15.17.1.20", {"start": v(-106.28, 40.45) * mm, "end": v(-107.86, 43.18) * mm});
            skCircle(sketch, "E15.0.1.21", {"center": v(-104.7, 51.82) * mm, "radius": 2.73 * mm, "construction": true});
            skLineSegment(sketch, "E15.2.1.21", {"start": v(-107.86, 51.82) * mm, "end": v(-106.28, 54.55) * mm});
            skLineSegment(sketch, "E15.5.1.21", {"start": v(-106.28, 54.55) * mm, "end": v(-103.13, 54.55) * mm});
            skLineSegment(sketch, "E15.8.1.21", {"start": v(-103.13, 54.55) * mm, "end": v(-101.55, 51.82) * mm});
            skLineSegment(sketch, "E15.11.1.21", {"start": v(-101.55, 51.82) * mm, "end": v(-103.13, 49.09) * mm});
            skLineSegment(sketch, "E15.14.1.21", {"start": v(-103.13, 49.09) * mm, "end": v(-106.28, 49.09) * mm});
            skLineSegment(sketch, "E15.17.1.21", {"start": v(-106.28, 49.09) * mm, "end": v(-107.86, 51.82) * mm});
            skCircle(sketch, "E15.0.1.22", {"center": v(-104.7, 60.45) * mm, "radius": 2.73 * mm, "construction": true});
            skLineSegment(sketch, "E15.2.1.22", {"start": v(-107.86, 60.45) * mm, "end": v(-106.28, 63.18) * mm});
            skLineSegment(sketch, "E15.5.1.22", {"start": v(-106.28, 63.18) * mm, "end": v(-103.13, 63.18) * mm});
            skLineSegment(sketch, "E15.8.1.22", {"start": v(-103.13, 63.18) * mm, "end": v(-101.55, 60.45) * mm});
            skLineSegment(sketch, "E15.11.1.22", {"start": v(-101.55, 60.45) * mm, "end": v(-103.13, 57.72) * mm});
            skLineSegment(sketch, "E15.14.1.22", {"start": v(-103.13, 57.72) * mm, "end": v(-106.28, 57.72) * mm});
            skLineSegment(sketch, "E15.17.1.22", {"start": v(-106.28, 57.72) * mm, "end": v(-107.86, 60.45) * mm});
            skCircle(sketch, "E15.0.1.23", {"center": v(-104.7, 69.09) * mm, "radius": 2.73 * mm, "construction": true});
            skLineSegment(sketch, "E15.2.1.23", {"start": v(-107.86, 69.09) * mm, "end": v(-106.28, 71.82) * mm});
            skLineSegment(sketch, "E15.5.1.23", {"start": v(-106.28, 71.82) * mm, "end": v(-103.13, 71.82) * mm});
            skLineSegment(sketch, "E15.8.1.23", {"start": v(-103.13, 71.82) * mm, "end": v(-101.55, 69.09) * mm});
            skLineSegment(sketch, "E15.11.1.23", {"start": v(-101.55, 69.09) * mm, "end": v(-103.13, 66.36) * mm});
            skLineSegment(sketch, "E15.14.1.23", {"start": v(-103.13, 66.36) * mm, "end": v(-106.28, 66.36) * mm});
            skLineSegment(sketch, "E15.17.1.23", {"start": v(-106.28, 66.36) * mm, "end": v(-107.86, 69.09) * mm});
            skCircle(sketch, "E15.0.1.24", {"center": v(-104.7, 77.72) * mm, "radius": 2.73 * mm, "construction": true});
            skLineSegment(sketch, "E15.2.1.24", {"start": v(-107.86, 77.72) * mm, "end": v(-106.28, 80.45) * mm});
            skLineSegment(sketch, "E15.5.1.24", {"start": v(-106.28, 80.45) * mm, "end": v(-103.13, 80.45) * mm});
            skLineSegment(sketch, "E15.8.1.24", {"start": v(-103.13, 80.45) * mm, "end": v(-101.55, 77.72) * mm});
            skLineSegment(sketch, "E15.11.1.24", {"start": v(-101.55, 77.72) * mm, "end": v(-103.13, 75) * mm});
            skLineSegment(sketch, "E15.14.1.24", {"start": v(-103.13, 75) * mm, "end": v(-106.28, 75) * mm});
            skLineSegment(sketch, "E15.17.1.24", {"start": v(-106.28, 75) * mm, "end": v(-107.86, 77.72) * mm});
            skCircle(sketch, "E15.0.2.20", {"center": v(-89.75, 43.18) * mm, "radius": 2.73 * mm, "construction": true});
            skLineSegment(sketch, "E15.2.2.20", {"start": v(-92.9, 43.18) * mm, "end": v(-91.32, 45.91) * mm});
            skLineSegment(sketch, "E15.5.2.20", {"start": v(-91.32, 45.91) * mm, "end": v(-88.17, 45.91) * mm});
            skLineSegment(sketch, "E15.8.2.20", {"start": v(-88.17, 45.91) * mm, "end": v(-86.6, 43.18) * mm});
            skLineSegment(sketch, "E15.11.2.20", {"start": v(-86.6, 43.18) * mm, "end": v(-88.17, 40.45) * mm});
            skLineSegment(sketch, "E15.14.2.20", {"start": v(-88.17, 40.45) * mm, "end": v(-91.32, 40.45) * mm});
            skLineSegment(sketch, "E15.17.2.20", {"start": v(-91.32, 40.45) * mm, "end": v(-92.9, 43.18) * mm});
            skCircle(sketch, "E15.0.2.21", {"center": v(-89.75, 51.82) * mm, "radius": 2.73 * mm, "construction": true});
            skLineSegment(sketch, "E15.2.2.21", {"start": v(-92.9, 51.82) * mm, "end": v(-91.32, 54.55) * mm});
            skLineSegment(sketch, "E15.5.2.21", {"start": v(-91.32, 54.55) * mm, "end": v(-88.17, 54.55) * mm});
            skLineSegment(sketch, "E15.8.2.21", {"start": v(-88.17, 54.55) * mm, "end": v(-86.6, 51.82) * mm});
            skLineSegment(sketch, "E15.11.2.21", {"start": v(-86.6, 51.82) * mm, "end": v(-88.17, 49.09) * mm});
            skLineSegment(sketch, "E15.14.2.21", {"start": v(-88.17, 49.09) * mm, "end": v(-91.32, 49.09) * mm});
            skLineSegment(sketch, "E15.17.2.21", {"start": v(-91.32, 49.09) * mm, "end": v(-92.9, 51.82) * mm});
            skCircle(sketch, "E15.0.2.22", {"center": v(-89.75, 60.45) * mm, "radius": 2.73 * mm, "construction": true});
            skLineSegment(sketch, "E15.2.2.22", {"start": v(-92.9, 60.45) * mm, "end": v(-91.32, 63.18) * mm});
            skLineSegment(sketch, "E15.5.2.22", {"start": v(-91.32, 63.18) * mm, "end": v(-88.17, 63.18) * mm});
            skLineSegment(sketch, "E15.8.2.22", {"start": v(-88.17, 63.18) * mm, "end": v(-86.6, 60.45) * mm});
            skLineSegment(sketch, "E15.11.2.22", {"start": v(-86.6, 60.45) * mm, "end": v(-88.17, 57.72) * mm});
            skLineSegment(sketch, "E15.14.2.22", {"start": v(-88.17, 57.72) * mm, "end": v(-91.32, 57.72) * mm});
            skLineSegment(sketch, "E15.17.2.22", {"start": v(-91.32, 57.72) * mm, "end": v(-92.9, 60.45) * mm});
            skCircle(sketch, "E15.0.2.23", {"center": v(-89.75, 69.09) * mm, "radius": 2.73 * mm, "construction": true});
            skLineSegment(sketch, "E15.2.2.23", {"start": v(-92.9, 69.09) * mm, "end": v(-91.32, 71.82) * mm});
            skLineSegment(sketch, "E15.5.2.23", {"start": v(-91.32, 71.82) * mm, "end": v(-88.17, 71.82) * mm});
            skLineSegment(sketch, "E15.8.2.23", {"start": v(-88.17, 71.82) * mm, "end": v(-86.6, 69.09) * mm});
            skLineSegment(sketch, "E15.11.2.23", {"start": v(-86.6, 69.09) * mm, "end": v(-88.17, 66.36) * mm});
            skLineSegment(sketch, "E15.14.2.23", {"start": v(-88.17, 66.36) * mm, "end": v(-91.32, 66.36) * mm});
            skLineSegment(sketch, "E15.17.2.23", {"start": v(-91.32, 66.36) * mm, "end": v(-92.9, 69.09) * mm});
            skCircle(sketch, "E15.0.2.24", {"center": v(-89.75, 77.72) * mm, "radius": 2.73 * mm, "construction": true});
            skLineSegment(sketch, "E15.2.2.24", {"start": v(-92.9, 77.72) * mm, "end": v(-91.32, 80.45) * mm});
            skLineSegment(sketch, "E15.5.2.24", {"start": v(-91.32, 80.45) * mm, "end": v(-88.17, 80.45) * mm});
            skLineSegment(sketch, "E15.8.2.24", {"start": v(-88.17, 80.45) * mm, "end": v(-86.6, 77.72) * mm});
            skLineSegment(sketch, "E15.11.2.24", {"start": v(-86.6, 77.72) * mm, "end": v(-88.17, 75) * mm});
            skLineSegment(sketch, "E15.14.2.24", {"start": v(-88.17, 75) * mm, "end": v(-91.32, 75) * mm});
            skLineSegment(sketch, "E15.17.2.24", {"start": v(-91.32, 75) * mm, "end": v(-92.9, 77.72) * mm});
            skLineSegment(sketch, "E16.0.0.20", {"start": v(-128.72, 41.6) * mm, "end": v(-125.57, 41.6) * mm});
            skLineSegment(sketch, "E16.3.0.20", {"start": v(-125.57, 41.6) * mm, "end": v(-124, 38.86) * mm});
            skLineSegment(sketch, "E16.6.0.20", {"start": v(-124, 38.86) * mm, "end": v(-125.57, 36.13) * mm});
            skCircle(sketch, "E16.9.0.20", {"center": v(-127.14, 38.86) * mm, "radius": 2.73 * mm, "construction": true});
            skLineSegment(sketch, "E16.11.0.20", {"start": v(-125.57, 36.13) * mm, "end": v(-128.72, 36.13) * mm});
            skLineSegment(sketch, "E16.14.0.20", {"start": v(-128.72, 36.13) * mm, "end": v(-130.3, 38.86) * mm});
            skLineSegment(sketch, "E16.17.0.20", {"start": v(-130.3, 38.86) * mm, "end": v(-128.72, 41.6) * mm});
            skLineSegment(sketch, "E16.0.0.21", {"start": v(-128.72, 50.23) * mm, "end": v(-125.57, 50.23) * mm});
            skLineSegment(sketch, "E16.3.0.21", {"start": v(-125.57, 50.23) * mm, "end": v(-124, 47.5) * mm});
            skLineSegment(sketch, "E16.6.0.21", {"start": v(-124, 47.5) * mm, "end": v(-125.57, 44.77) * mm});
            skCircle(sketch, "E16.9.0.21", {"center": v(-127.14, 47.5) * mm, "radius": 2.73 * mm, "construction": true});
            skLineSegment(sketch, "E16.11.0.21", {"start": v(-125.57, 44.77) * mm, "end": v(-128.72, 44.77) * mm});
            skLineSegment(sketch, "E16.14.0.21", {"start": v(-128.72, 44.77) * mm, "end": v(-130.3, 47.5) * mm});
            skLineSegment(sketch, "E16.17.0.21", {"start": v(-130.3, 47.5) * mm, "end": v(-128.72, 50.23) * mm});
            skLineSegment(sketch, "E16.0.0.22", {"start": v(-128.72, 58.86) * mm, "end": v(-125.57, 58.86) * mm});
            skLineSegment(sketch, "E16.3.0.22", {"start": v(-125.57, 58.86) * mm, "end": v(-124, 56.13) * mm});
            skLineSegment(sketch, "E16.6.0.22", {"start": v(-124, 56.13) * mm, "end": v(-125.57, 53.4) * mm});
            skCircle(sketch, "E16.9.0.22", {"center": v(-127.14, 56.13) * mm, "radius": 2.73 * mm, "construction": true});
            skLineSegment(sketch, "E16.11.0.22", {"start": v(-125.57, 53.4) * mm, "end": v(-128.72, 53.4) * mm});
            skLineSegment(sketch, "E16.14.0.22", {"start": v(-128.72, 53.4) * mm, "end": v(-130.3, 56.13) * mm});
            skLineSegment(sketch, "E16.17.0.22", {"start": v(-130.3, 56.13) * mm, "end": v(-128.72, 58.86) * mm});
            skLineSegment(sketch, "E16.0.0.23", {"start": v(-128.72, 67.5) * mm, "end": v(-125.57, 67.5) * mm});
            skLineSegment(sketch, "E16.3.0.23", {"start": v(-125.57, 67.5) * mm, "end": v(-124, 64.77) * mm});
            skLineSegment(sketch, "E16.6.0.23", {"start": v(-124, 64.77) * mm, "end": v(-125.57, 62.04) * mm});
            skCircle(sketch, "E16.9.0.23", {"center": v(-127.14, 64.77) * mm, "radius": 2.73 * mm, "construction": true});
            skLineSegment(sketch, "E16.11.0.23", {"start": v(-125.57, 62.04) * mm, "end": v(-128.72, 62.04) * mm});
            skLineSegment(sketch, "E16.14.0.23", {"start": v(-128.72, 62.04) * mm, "end": v(-130.3, 64.77) * mm});
            skLineSegment(sketch, "E16.17.0.23", {"start": v(-130.3, 64.77) * mm, "end": v(-128.72, 67.5) * mm});
            skLineSegment(sketch, "E16.0.0.24", {"start": v(-128.72, 76.14) * mm, "end": v(-125.57, 76.14) * mm});
            skLineSegment(sketch, "E16.3.0.24", {"start": v(-125.57, 76.14) * mm, "end": v(-124, 73.4) * mm});
            skLineSegment(sketch, "E16.6.0.24", {"start": v(-124, 73.4) * mm, "end": v(-125.57, 70.68) * mm});
            skCircle(sketch, "E16.9.0.24", {"center": v(-127.14, 73.4) * mm, "radius": 2.73 * mm, "construction": true});
            skLineSegment(sketch, "E16.11.0.24", {"start": v(-125.57, 70.68) * mm, "end": v(-128.72, 70.68) * mm});
            skLineSegment(sketch, "E16.14.0.24", {"start": v(-128.72, 70.68) * mm, "end": v(-130.3, 73.4) * mm});
            skLineSegment(sketch, "E16.17.0.24", {"start": v(-130.3, 73.4) * mm, "end": v(-128.72, 76.14) * mm});
            skLineSegment(sketch, "E16.0.1.20", {"start": v(-113.76, 41.6) * mm, "end": v(-110.6, 41.6) * mm});
            skLineSegment(sketch, "E16.3.1.20", {"start": v(-110.6, 41.6) * mm, "end": v(-109.03, 38.86) * mm});
            skLineSegment(sketch, "E16.6.1.20", {"start": v(-109.03, 38.86) * mm, "end": v(-110.6, 36.13) * mm});
            skCircle(sketch, "E16.9.1.20", {"center": v(-112.19, 38.86) * mm, "radius": 2.73 * mm, "construction": true});
            skLineSegment(sketch, "E16.11.1.20", {"start": v(-110.6, 36.13) * mm, "end": v(-113.76, 36.13) * mm});
            skLineSegment(sketch, "E16.14.1.20", {"start": v(-113.76, 36.13) * mm, "end": v(-115.34, 38.86) * mm});
            skLineSegment(sketch, "E16.17.1.20", {"start": v(-115.34, 38.86) * mm, "end": v(-113.76, 41.6) * mm});
            skLineSegment(sketch, "E16.0.1.21", {"start": v(-113.76, 50.23) * mm, "end": v(-110.6, 50.23) * mm});
            skLineSegment(sketch, "E16.3.1.21", {"start": v(-110.6, 50.23) * mm, "end": v(-109.03, 47.5) * mm});
            skLineSegment(sketch, "E16.6.1.21", {"start": v(-109.03, 47.5) * mm, "end": v(-110.6, 44.77) * mm});
            skCircle(sketch, "E16.9.1.21", {"center": v(-112.19, 47.5) * mm, "radius": 2.73 * mm, "construction": true});
            skLineSegment(sketch, "E16.11.1.21", {"start": v(-110.6, 44.77) * mm, "end": v(-113.76, 44.77) * mm});
            skLineSegment(sketch, "E16.14.1.21", {"start": v(-113.76, 44.77) * mm, "end": v(-115.34, 47.5) * mm});
            skLineSegment(sketch, "E16.17.1.21", {"start": v(-115.34, 47.5) * mm, "end": v(-113.76, 50.23) * mm});
            skLineSegment(sketch, "E16.0.1.22", {"start": v(-113.76, 58.86) * mm, "end": v(-110.6, 58.86) * mm});
            skLineSegment(sketch, "E16.3.1.22", {"start": v(-110.6, 58.86) * mm, "end": v(-109.03, 56.13) * mm});
            skLineSegment(sketch, "E16.6.1.22", {"start": v(-109.03, 56.13) * mm, "end": v(-110.6, 53.4) * mm});
            skCircle(sketch, "E16.9.1.22", {"center": v(-112.19, 56.13) * mm, "radius": 2.73 * mm, "construction": true});
            skLineSegment(sketch, "E16.11.1.22", {"start": v(-110.6, 53.4) * mm, "end": v(-113.76, 53.4) * mm});
            skLineSegment(sketch, "E16.14.1.22", {"start": v(-113.76, 53.4) * mm, "end": v(-115.34, 56.13) * mm});
            skLineSegment(sketch, "E16.17.1.22", {"start": v(-115.34, 56.13) * mm, "end": v(-113.76, 58.86) * mm});
            skLineSegment(sketch, "E16.0.1.23", {"start": v(-113.76, 67.5) * mm, "end": v(-110.6, 67.5) * mm});
            skLineSegment(sketch, "E16.3.1.23", {"start": v(-110.6, 67.5) * mm, "end": v(-109.03, 64.77) * mm});
            skLineSegment(sketch, "E16.6.1.23", {"start": v(-109.03, 64.77) * mm, "end": v(-110.6, 62.04) * mm});
            skCircle(sketch, "E16.9.1.23", {"center": v(-112.19, 64.77) * mm, "radius": 2.73 * mm, "construction": true});
            skLineSegment(sketch, "E16.11.1.23", {"start": v(-110.6, 62.04) * mm, "end": v(-113.76, 62.04) * mm});
            skLineSegment(sketch, "E16.14.1.23", {"start": v(-113.76, 62.04) * mm, "end": v(-115.34, 64.77) * mm});
            skLineSegment(sketch, "E16.17.1.23", {"start": v(-115.34, 64.77) * mm, "end": v(-113.76, 67.5) * mm});
            skLineSegment(sketch, "E16.0.1.24", {"start": v(-113.76, 76.14) * mm, "end": v(-110.6, 76.14) * mm});
            skLineSegment(sketch, "E16.3.1.24", {"start": v(-110.6, 76.14) * mm, "end": v(-109.03, 73.4) * mm});
            skLineSegment(sketch, "E16.6.1.24", {"start": v(-109.03, 73.4) * mm, "end": v(-110.6, 70.68) * mm});
            skCircle(sketch, "E16.9.1.24", {"center": v(-112.19, 73.4) * mm, "radius": 2.73 * mm, "construction": true});
            skLineSegment(sketch, "E16.11.1.24", {"start": v(-110.6, 70.68) * mm, "end": v(-113.76, 70.68) * mm});
            skLineSegment(sketch, "E16.14.1.24", {"start": v(-113.76, 70.68) * mm, "end": v(-115.34, 73.4) * mm});
            skLineSegment(sketch, "E16.17.1.24", {"start": v(-115.34, 73.4) * mm, "end": v(-113.76, 76.14) * mm});
            skLineSegment(sketch, "E16.0.2.20", {"start": v(-98.8, 41.6) * mm, "end": v(-95.65, 41.6) * mm});
            skLineSegment(sketch, "E16.3.2.20", {"start": v(-95.65, 41.6) * mm, "end": v(-94.07, 38.86) * mm});
            skLineSegment(sketch, "E16.6.2.20", {"start": v(-94.07, 38.86) * mm, "end": v(-95.65, 36.13) * mm});
            skCircle(sketch, "E16.9.2.20", {"center": v(-97.23, 38.86) * mm, "radius": 2.73 * mm, "construction": true});
            skLineSegment(sketch, "E16.11.2.20", {"start": v(-95.65, 36.13) * mm, "end": v(-98.8, 36.13) * mm});
            skLineSegment(sketch, "E16.14.2.20", {"start": v(-98.8, 36.13) * mm, "end": v(-100.38, 38.86) * mm});
            skLineSegment(sketch, "E16.17.2.20", {"start": v(-100.38, 38.86) * mm, "end": v(-98.8, 41.6) * mm});
            skLineSegment(sketch, "E16.0.2.21", {"start": v(-98.8, 50.23) * mm, "end": v(-95.65, 50.23) * mm});
            skLineSegment(sketch, "E16.3.2.21", {"start": v(-95.65, 50.23) * mm, "end": v(-94.07, 47.5) * mm});
            skLineSegment(sketch, "E16.6.2.21", {"start": v(-94.07, 47.5) * mm, "end": v(-95.65, 44.77) * mm});
            skCircle(sketch, "E16.9.2.21", {"center": v(-97.23, 47.5) * mm, "radius": 2.73 * mm, "construction": true});
            skLineSegment(sketch, "E16.11.2.21", {"start": v(-95.65, 44.77) * mm, "end": v(-98.8, 44.77) * mm});
            skLineSegment(sketch, "E16.14.2.21", {"start": v(-98.8, 44.77) * mm, "end": v(-100.38, 47.5) * mm});
            skLineSegment(sketch, "E16.17.2.21", {"start": v(-100.38, 47.5) * mm, "end": v(-98.8, 50.23) * mm});
            skLineSegment(sketch, "E16.0.2.22", {"start": v(-98.8, 58.86) * mm, "end": v(-95.65, 58.86) * mm});
            skLineSegment(sketch, "E16.3.2.22", {"start": v(-95.65, 58.86) * mm, "end": v(-94.07, 56.13) * mm});
            skLineSegment(sketch, "E16.6.2.22", {"start": v(-94.07, 56.13) * mm, "end": v(-95.65, 53.4) * mm});
            skCircle(sketch, "E16.9.2.22", {"center": v(-97.23, 56.13) * mm, "radius": 2.73 * mm, "construction": true});
            skLineSegment(sketch, "E16.11.2.22", {"start": v(-95.65, 53.4) * mm, "end": v(-98.8, 53.4) * mm});
            skLineSegment(sketch, "E16.14.2.22", {"start": v(-98.8, 53.4) * mm, "end": v(-100.38, 56.13) * mm});
            skLineSegment(sketch, "E16.17.2.22", {"start": v(-100.38, 56.13) * mm, "end": v(-98.8, 58.86) * mm});
            skLineSegment(sketch, "E16.0.2.23", {"start": v(-98.8, 67.5) * mm, "end": v(-95.65, 67.5) * mm});
            skLineSegment(sketch, "E16.3.2.23", {"start": v(-95.65, 67.5) * mm, "end": v(-94.07, 64.77) * mm});
            skLineSegment(sketch, "E16.6.2.23", {"start": v(-94.07, 64.77) * mm, "end": v(-95.65, 62.04) * mm});
            skCircle(sketch, "E16.9.2.23", {"center": v(-97.23, 64.77) * mm, "radius": 2.73 * mm, "construction": true});
            skLineSegment(sketch, "E16.11.2.23", {"start": v(-95.65, 62.04) * mm, "end": v(-98.8, 62.04) * mm});
            skLineSegment(sketch, "E16.14.2.23", {"start": v(-98.8, 62.04) * mm, "end": v(-100.38, 64.77) * mm});
            skLineSegment(sketch, "E16.17.2.23", {"start": v(-100.38, 64.77) * mm, "end": v(-98.8, 67.5) * mm});
            skLineSegment(sketch, "E16.0.2.24", {"start": v(-98.8, 76.14) * mm, "end": v(-95.65, 76.14) * mm});
            skLineSegment(sketch, "E16.3.2.24", {"start": v(-95.65, 76.14) * mm, "end": v(-94.07, 73.4) * mm});
            skLineSegment(sketch, "E16.6.2.24", {"start": v(-94.07, 73.4) * mm, "end": v(-95.65, 70.68) * mm});
            skCircle(sketch, "E16.9.2.24", {"center": v(-97.23, 73.4) * mm, "radius": 2.73 * mm, "construction": true});
            skLineSegment(sketch, "E16.11.2.24", {"start": v(-95.65, 70.68) * mm, "end": v(-98.8, 70.68) * mm});
            skLineSegment(sketch, "E16.14.2.24", {"start": v(-98.8, 70.68) * mm, "end": v(-100.38, 73.4) * mm});
            skLineSegment(sketch, "E16.17.2.24", {"start": v(-100.38, 73.4) * mm, "end": v(-98.8, 76.14) * mm});
            skLineSegment(sketch, "E16.0.3.20", {"start": v(-83.85, 41.6) * mm, "end": v(-80.7, 41.6) * mm});
            skLineSegment(sketch, "E16.3.3.20", {"start": v(-80.7, 41.6) * mm, "end": v(-79.12, 38.86) * mm});
            skLineSegment(sketch, "E16.6.3.20", {"start": v(-79.12, 38.86) * mm, "end": v(-80.7, 36.13) * mm});
            skCircle(sketch, "E16.9.3.20", {"center": v(-82.27, 38.86) * mm, "radius": 2.73 * mm, "construction": true});
            skLineSegment(sketch, "E16.11.3.20", {"start": v(-80.7, 36.13) * mm, "end": v(-83.85, 36.13) * mm});
            skLineSegment(sketch, "E16.14.3.20", {"start": v(-83.85, 36.13) * mm, "end": v(-85.42, 38.86) * mm});
            skLineSegment(sketch, "E16.17.3.20", {"start": v(-85.42, 38.86) * mm, "end": v(-83.85, 41.6) * mm});
            skLineSegment(sketch, "E16.0.3.21", {"start": v(-83.85, 50.23) * mm, "end": v(-80.7, 50.23) * mm});
            skLineSegment(sketch, "E16.3.3.21", {"start": v(-80.7, 50.23) * mm, "end": v(-79.12, 47.5) * mm});
            skLineSegment(sketch, "E16.6.3.21", {"start": v(-79.12, 47.5) * mm, "end": v(-80.7, 44.77) * mm});
            skCircle(sketch, "E16.9.3.21", {"center": v(-82.27, 47.5) * mm, "radius": 2.73 * mm, "construction": true});
            skLineSegment(sketch, "E16.11.3.21", {"start": v(-80.7, 44.77) * mm, "end": v(-83.85, 44.77) * mm});
            skLineSegment(sketch, "E16.14.3.21", {"start": v(-83.85, 44.77) * mm, "end": v(-85.42, 47.5) * mm});
            skLineSegment(sketch, "E16.17.3.21", {"start": v(-85.42, 47.5) * mm, "end": v(-83.85, 50.23) * mm});
            skLineSegment(sketch, "E16.0.3.22", {"start": v(-83.85, 58.86) * mm, "end": v(-80.7, 58.86) * mm});
            skLineSegment(sketch, "E16.3.3.22", {"start": v(-80.7, 58.86) * mm, "end": v(-79.12, 56.13) * mm});
            skLineSegment(sketch, "E16.6.3.22", {"start": v(-79.12, 56.13) * mm, "end": v(-80.7, 53.4) * mm});
            skCircle(sketch, "E16.9.3.22", {"center": v(-82.27, 56.13) * mm, "radius": 2.73 * mm, "construction": true});
            skLineSegment(sketch, "E16.11.3.22", {"start": v(-80.7, 53.4) * mm, "end": v(-83.85, 53.4) * mm});
            skLineSegment(sketch, "E16.14.3.22", {"start": v(-83.85, 53.4) * mm, "end": v(-85.42, 56.13) * mm});
            skLineSegment(sketch, "E16.17.3.22", {"start": v(-85.42, 56.13) * mm, "end": v(-83.85, 58.86) * mm});
            skLineSegment(sketch, "E16.0.3.23", {"start": v(-83.85, 67.5) * mm, "end": v(-80.7, 67.5) * mm});
            skLineSegment(sketch, "E16.3.3.23", {"start": v(-80.7, 67.5) * mm, "end": v(-79.12, 64.77) * mm});
            skLineSegment(sketch, "E16.6.3.23", {"start": v(-79.12, 64.77) * mm, "end": v(-80.7, 62.04) * mm});
            skCircle(sketch, "E16.9.3.23", {"center": v(-82.27, 64.77) * mm, "radius": 2.73 * mm, "construction": true});
            skLineSegment(sketch, "E16.11.3.23", {"start": v(-80.7, 62.04) * mm, "end": v(-83.85, 62.04) * mm});
            skLineSegment(sketch, "E16.14.3.23", {"start": v(-83.85, 62.04) * mm, "end": v(-85.42, 64.77) * mm});
            skLineSegment(sketch, "E16.17.3.23", {"start": v(-85.42, 64.77) * mm, "end": v(-83.85, 67.5) * mm});
            skLineSegment(sketch, "E16.0.3.24", {"start": v(-83.85, 76.14) * mm, "end": v(-80.7, 76.14) * mm});
            skLineSegment(sketch, "E16.3.3.24", {"start": v(-80.7, 76.14) * mm, "end": v(-79.12, 73.4) * mm});
            skLineSegment(sketch, "E16.6.3.24", {"start": v(-79.12, 73.4) * mm, "end": v(-80.7, 70.68) * mm});
            skCircle(sketch, "E16.9.3.24", {"center": v(-82.27, 73.4) * mm, "radius": 2.73 * mm, "construction": true});
            skLineSegment(sketch, "E16.11.3.24", {"start": v(-80.7, 70.68) * mm, "end": v(-83.85, 70.68) * mm});
            skLineSegment(sketch, "E16.14.3.24", {"start": v(-83.85, 70.68) * mm, "end": v(-85.42, 73.4) * mm});
            skLineSegment(sketch, "E16.17.3.24", {"start": v(-85.42, 73.4) * mm, "end": v(-83.85, 76.14) * mm});
            skLineSegment(sketch, "E16.0.4.20", {"start": v(-68.89, 41.6) * mm, "end": v(-65.73, 41.6) * mm});
            skLineSegment(sketch, "E16.3.4.20", {"start": v(-65.73, 41.6) * mm, "end": v(-64.16, 38.86) * mm});
            skLineSegment(sketch, "E16.6.4.20", {"start": v(-64.16, 38.86) * mm, "end": v(-65.73, 36.13) * mm});
            skCircle(sketch, "E16.9.4.20", {"center": v(-67.31, 38.86) * mm, "radius": 2.73 * mm, "construction": true});
            skLineSegment(sketch, "E16.11.4.20", {"start": v(-65.73, 36.13) * mm, "end": v(-68.89, 36.13) * mm});
            skLineSegment(sketch, "E16.14.4.20", {"start": v(-68.89, 36.13) * mm, "end": v(-70.46, 38.86) * mm});
            skLineSegment(sketch, "E16.17.4.20", {"start": v(-70.46, 38.86) * mm, "end": v(-68.89, 41.6) * mm});
            skLineSegment(sketch, "E16.0.4.21", {"start": v(-68.89, 50.23) * mm, "end": v(-65.73, 50.23) * mm});
            skLineSegment(sketch, "E16.3.4.21", {"start": v(-65.73, 50.23) * mm, "end": v(-64.16, 47.5) * mm});
            skLineSegment(sketch, "E16.6.4.21", {"start": v(-64.16, 47.5) * mm, "end": v(-65.73, 44.77) * mm});
            skCircle(sketch, "E16.9.4.21", {"center": v(-67.31, 47.5) * mm, "radius": 2.73 * mm, "construction": true});
            skLineSegment(sketch, "E16.11.4.21", {"start": v(-65.73, 44.77) * mm, "end": v(-68.89, 44.77) * mm});
            skLineSegment(sketch, "E16.14.4.21", {"start": v(-68.89, 44.77) * mm, "end": v(-70.46, 47.5) * mm});
            skLineSegment(sketch, "E16.17.4.21", {"start": v(-70.46, 47.5) * mm, "end": v(-68.89, 50.23) * mm});
            skLineSegment(sketch, "E16.0.4.22", {"start": v(-68.89, 58.86) * mm, "end": v(-65.73, 58.86) * mm});
            skLineSegment(sketch, "E16.3.4.22", {"start": v(-65.73, 58.86) * mm, "end": v(-64.16, 56.13) * mm});
            skLineSegment(sketch, "E16.6.4.22", {"start": v(-64.16, 56.13) * mm, "end": v(-65.73, 53.4) * mm});
            skCircle(sketch, "E16.9.4.22", {"center": v(-67.31, 56.13) * mm, "radius": 2.73 * mm, "construction": true});
            skLineSegment(sketch, "E16.11.4.22", {"start": v(-65.73, 53.4) * mm, "end": v(-68.89, 53.4) * mm});
            skLineSegment(sketch, "E16.14.4.22", {"start": v(-68.89, 53.4) * mm, "end": v(-70.46, 56.13) * mm});
            skLineSegment(sketch, "E16.17.4.22", {"start": v(-70.46, 56.13) * mm, "end": v(-68.89, 58.86) * mm});
            skLineSegment(sketch, "E16.0.4.23", {"start": v(-68.89, 67.5) * mm, "end": v(-65.73, 67.5) * mm});
            skLineSegment(sketch, "E16.3.4.23", {"start": v(-65.73, 67.5) * mm, "end": v(-64.16, 64.77) * mm});
            skLineSegment(sketch, "E16.6.4.23", {"start": v(-64.16, 64.77) * mm, "end": v(-65.73, 62.04) * mm});
            skCircle(sketch, "E16.9.4.23", {"center": v(-67.31, 64.77) * mm, "radius": 2.73 * mm, "construction": true});
            skLineSegment(sketch, "E16.11.4.23", {"start": v(-65.73, 62.04) * mm, "end": v(-68.89, 62.04) * mm});
            skLineSegment(sketch, "E16.14.4.23", {"start": v(-68.89, 62.04) * mm, "end": v(-70.46, 64.77) * mm});
            skLineSegment(sketch, "E16.17.4.23", {"start": v(-70.46, 64.77) * mm, "end": v(-68.89, 67.5) * mm});
            skLineSegment(sketch, "E16.0.4.24", {"start": v(-68.89, 76.14) * mm, "end": v(-65.73, 76.14) * mm});
            skLineSegment(sketch, "E16.3.4.24", {"start": v(-65.73, 76.14) * mm, "end": v(-64.16, 73.4) * mm});
            skLineSegment(sketch, "E16.6.4.24", {"start": v(-64.16, 73.4) * mm, "end": v(-65.73, 70.68) * mm});
            skCircle(sketch, "E16.9.4.24", {"center": v(-67.31, 73.4) * mm, "radius": 2.73 * mm, "construction": true});
            skLineSegment(sketch, "E16.11.4.24", {"start": v(-65.73, 70.68) * mm, "end": v(-68.89, 70.68) * mm});
            skLineSegment(sketch, "E16.14.4.24", {"start": v(-68.89, 70.68) * mm, "end": v(-70.46, 73.4) * mm});
            skLineSegment(sketch, "E16.17.4.24", {"start": v(-70.46, 73.4) * mm, "end": v(-68.89, 76.14) * mm});
            skLineSegment(sketch, "E16.0.5.20", {"start": v(-53.93, 41.6) * mm, "end": v(-50.78, 41.6) * mm});
            skLineSegment(sketch, "E16.3.5.20", {"start": v(-50.78, 41.6) * mm, "end": v(-49.2, 38.86) * mm});
            skLineSegment(sketch, "E16.6.5.20", {"start": v(-49.2, 38.86) * mm, "end": v(-50.78, 36.13) * mm});
            skCircle(sketch, "E16.9.5.20", {"center": v(-52.35, 38.86) * mm, "radius": 2.73 * mm, "construction": true});
            skLineSegment(sketch, "E16.11.5.20", {"start": v(-50.78, 36.13) * mm, "end": v(-53.93, 36.13) * mm});
            skLineSegment(sketch, "E16.14.5.20", {"start": v(-53.93, 36.13) * mm, "end": v(-55.5, 38.86) * mm});
            skLineSegment(sketch, "E16.17.5.20", {"start": v(-55.5, 38.86) * mm, "end": v(-53.93, 41.6) * mm});
            skLineSegment(sketch, "E16.0.5.21", {"start": v(-53.93, 50.23) * mm, "end": v(-50.78, 50.23) * mm});
            skLineSegment(sketch, "E16.3.5.21", {"start": v(-50.78, 50.23) * mm, "end": v(-49.2, 47.5) * mm});
            skLineSegment(sketch, "E16.6.5.21", {"start": v(-49.2, 47.5) * mm, "end": v(-50.78, 44.77) * mm});
            skCircle(sketch, "E16.9.5.21", {"center": v(-52.35, 47.5) * mm, "radius": 2.73 * mm, "construction": true});
            skLineSegment(sketch, "E16.11.5.21", {"start": v(-50.78, 44.77) * mm, "end": v(-53.93, 44.77) * mm});
            skLineSegment(sketch, "E16.14.5.21", {"start": v(-53.93, 44.77) * mm, "end": v(-55.5, 47.5) * mm});
            skLineSegment(sketch, "E16.17.5.21", {"start": v(-55.5, 47.5) * mm, "end": v(-53.93, 50.23) * mm});
            skLineSegment(sketch, "E16.0.5.22", {"start": v(-53.93, 58.86) * mm, "end": v(-50.78, 58.86) * mm});
            skLineSegment(sketch, "E16.3.5.22", {"start": v(-50.78, 58.86) * mm, "end": v(-49.2, 56.13) * mm});
            skLineSegment(sketch, "E16.6.5.22", {"start": v(-49.2, 56.13) * mm, "end": v(-50.78, 53.4) * mm});
            skCircle(sketch, "E16.9.5.22", {"center": v(-52.35, 56.13) * mm, "radius": 2.73 * mm, "construction": true});
            skLineSegment(sketch, "E16.11.5.22", {"start": v(-50.78, 53.4) * mm, "end": v(-53.93, 53.4) * mm});
            skLineSegment(sketch, "E16.14.5.22", {"start": v(-53.93, 53.4) * mm, "end": v(-55.5, 56.13) * mm});
            skLineSegment(sketch, "E16.17.5.22", {"start": v(-55.5, 56.13) * mm, "end": v(-53.93, 58.86) * mm});
            skLineSegment(sketch, "E16.0.5.23", {"start": v(-53.93, 67.5) * mm, "end": v(-50.78, 67.5) * mm});
            skLineSegment(sketch, "E16.3.5.23", {"start": v(-50.78, 67.5) * mm, "end": v(-49.2, 64.77) * mm});
            skLineSegment(sketch, "E16.6.5.23", {"start": v(-49.2, 64.77) * mm, "end": v(-50.78, 62.04) * mm});
            skCircle(sketch, "E16.9.5.23", {"center": v(-52.35, 64.77) * mm, "radius": 2.73 * mm, "construction": true});
            skLineSegment(sketch, "E16.11.5.23", {"start": v(-50.78, 62.04) * mm, "end": v(-53.93, 62.04) * mm});
            skLineSegment(sketch, "E16.14.5.23", {"start": v(-53.93, 62.04) * mm, "end": v(-55.5, 64.77) * mm});
            skLineSegment(sketch, "E16.17.5.23", {"start": v(-55.5, 64.77) * mm, "end": v(-53.93, 67.5) * mm});
            skLineSegment(sketch, "E16.0.5.24", {"start": v(-53.93, 76.14) * mm, "end": v(-50.78, 76.14) * mm});
            skLineSegment(sketch, "E16.3.5.24", {"start": v(-50.78, 76.14) * mm, "end": v(-49.2, 73.4) * mm});
            skLineSegment(sketch, "E16.6.5.24", {"start": v(-49.2, 73.4) * mm, "end": v(-50.78, 70.68) * mm});
            skCircle(sketch, "E16.9.5.24", {"center": v(-52.35, 73.4) * mm, "radius": 2.73 * mm, "construction": true});
            skLineSegment(sketch, "E16.11.5.24", {"start": v(-50.78, 70.68) * mm, "end": v(-53.93, 70.68) * mm});
            skLineSegment(sketch, "E16.14.5.24", {"start": v(-53.93, 70.68) * mm, "end": v(-55.5, 73.4) * mm});
            skLineSegment(sketch, "E16.17.5.24", {"start": v(-55.5, 73.4) * mm, "end": v(-53.93, 76.14) * mm});
            skLineSegment(sketch, "E16.0.6.20", {"start": v(-38.97, 41.6) * mm, "end": v(-35.82, 41.6) * mm});
            skLineSegment(sketch, "E16.3.6.20", {"start": v(-35.82, 41.6) * mm, "end": v(-34.24, 38.86) * mm});
            skLineSegment(sketch, "E16.6.6.20", {"start": v(-34.24, 38.86) * mm, "end": v(-35.82, 36.13) * mm});
            skCircle(sketch, "E16.9.6.20", {"center": v(-37.4, 38.86) * mm, "radius": 2.73 * mm, "construction": true});
            skLineSegment(sketch, "E16.11.6.20", {"start": v(-35.82, 36.13) * mm, "end": v(-38.97, 36.13) * mm});
            skLineSegment(sketch, "E16.14.6.20", {"start": v(-38.97, 36.13) * mm, "end": v(-40.55, 38.86) * mm});
            skLineSegment(sketch, "E16.17.6.20", {"start": v(-40.55, 38.86) * mm, "end": v(-38.97, 41.6) * mm});
            skLineSegment(sketch, "E16.0.6.21", {"start": v(-38.97, 50.23) * mm, "end": v(-35.82, 50.23) * mm});
            skLineSegment(sketch, "E16.3.6.21", {"start": v(-35.82, 50.23) * mm, "end": v(-34.24, 47.5) * mm});
            skLineSegment(sketch, "E16.6.6.21", {"start": v(-34.24, 47.5) * mm, "end": v(-35.82, 44.77) * mm});
            skCircle(sketch, "E16.9.6.21", {"center": v(-37.4, 47.5) * mm, "radius": 2.73 * mm, "construction": true});
            skLineSegment(sketch, "E16.11.6.21", {"start": v(-35.82, 44.77) * mm, "end": v(-38.97, 44.77) * mm});
            skLineSegment(sketch, "E16.14.6.21", {"start": v(-38.97, 44.77) * mm, "end": v(-40.55, 47.5) * mm});
            skLineSegment(sketch, "E16.17.6.21", {"start": v(-40.55, 47.5) * mm, "end": v(-38.97, 50.23) * mm});
            skLineSegment(sketch, "E16.0.6.22", {"start": v(-38.97, 58.86) * mm, "end": v(-35.82, 58.86) * mm});
            skLineSegment(sketch, "E16.3.6.22", {"start": v(-35.82, 58.86) * mm, "end": v(-34.24, 56.13) * mm});
            skLineSegment(sketch, "E16.6.6.22", {"start": v(-34.24, 56.13) * mm, "end": v(-35.82, 53.4) * mm});
            skCircle(sketch, "E16.9.6.22", {"center": v(-37.4, 56.13) * mm, "radius": 2.73 * mm, "construction": true});
            skLineSegment(sketch, "E16.11.6.22", {"start": v(-35.82, 53.4) * mm, "end": v(-38.97, 53.4) * mm});
            skLineSegment(sketch, "E16.14.6.22", {"start": v(-38.97, 53.4) * mm, "end": v(-40.55, 56.13) * mm});
            skLineSegment(sketch, "E16.17.6.22", {"start": v(-40.55, 56.13) * mm, "end": v(-38.97, 58.86) * mm});
            skLineSegment(sketch, "E16.0.6.23", {"start": v(-38.97, 67.5) * mm, "end": v(-35.82, 67.5) * mm});
            skLineSegment(sketch, "E16.3.6.23", {"start": v(-35.82, 67.5) * mm, "end": v(-34.24, 64.77) * mm});
            skLineSegment(sketch, "E16.6.6.23", {"start": v(-34.24, 64.77) * mm, "end": v(-35.82, 62.04) * mm});
            skCircle(sketch, "E16.9.6.23", {"center": v(-37.4, 64.77) * mm, "radius": 2.73 * mm, "construction": true});
            skLineSegment(sketch, "E16.11.6.23", {"start": v(-35.82, 62.04) * mm, "end": v(-38.97, 62.04) * mm});
            skLineSegment(sketch, "E16.14.6.23", {"start": v(-38.97, 62.04) * mm, "end": v(-40.55, 64.77) * mm});
            skLineSegment(sketch, "E16.17.6.23", {"start": v(-40.55, 64.77) * mm, "end": v(-38.97, 67.5) * mm});
            skLineSegment(sketch, "E16.0.6.24", {"start": v(-38.97, 76.14) * mm, "end": v(-35.82, 76.14) * mm});
            skLineSegment(sketch, "E16.3.6.24", {"start": v(-35.82, 76.14) * mm, "end": v(-34.24, 73.4) * mm});
            skLineSegment(sketch, "E16.6.6.24", {"start": v(-34.24, 73.4) * mm, "end": v(-35.82, 70.68) * mm});
            skCircle(sketch, "E16.9.6.24", {"center": v(-37.4, 73.4) * mm, "radius": 2.73 * mm, "construction": true});
            skLineSegment(sketch, "E16.11.6.24", {"start": v(-35.82, 70.68) * mm, "end": v(-38.97, 70.68) * mm});
            skLineSegment(sketch, "E16.14.6.24", {"start": v(-38.97, 70.68) * mm, "end": v(-40.55, 73.4) * mm});
            skLineSegment(sketch, "E16.17.6.24", {"start": v(-40.55, 73.4) * mm, "end": v(-38.97, 76.14) * mm});
            skLineSegment(sketch, "E16.0.7.20", {"start": v(-24.01, 41.6) * mm, "end": v(-20.86, 41.6) * mm});
            skLineSegment(sketch, "E16.3.7.20", {"start": v(-20.86, 41.6) * mm, "end": v(-19.28, 38.86) * mm});
            skLineSegment(sketch, "E16.6.7.20", {"start": v(-19.28, 38.86) * mm, "end": v(-20.86, 36.13) * mm});
            skCircle(sketch, "E16.9.7.20", {"center": v(-22.44, 38.86) * mm, "radius": 2.73 * mm, "construction": true});
            skLineSegment(sketch, "E16.11.7.20", {"start": v(-20.86, 36.13) * mm, "end": v(-24.01, 36.13) * mm});
            skLineSegment(sketch, "E16.14.7.20", {"start": v(-24.01, 36.13) * mm, "end": v(-25.59, 38.86) * mm});
            skLineSegment(sketch, "E16.17.7.20", {"start": v(-25.59, 38.86) * mm, "end": v(-24.01, 41.6) * mm});
            skLineSegment(sketch, "E16.0.7.21", {"start": v(-24.01, 50.23) * mm, "end": v(-20.86, 50.23) * mm});
            skLineSegment(sketch, "E16.3.7.21", {"start": v(-20.86, 50.23) * mm, "end": v(-19.28, 47.5) * mm});
            skLineSegment(sketch, "E16.6.7.21", {"start": v(-19.28, 47.5) * mm, "end": v(-20.86, 44.77) * mm});
            skCircle(sketch, "E16.9.7.21", {"center": v(-22.44, 47.5) * mm, "radius": 2.73 * mm, "construction": true});
            skLineSegment(sketch, "E16.11.7.21", {"start": v(-20.86, 44.77) * mm, "end": v(-24.01, 44.77) * mm});
            skLineSegment(sketch, "E16.14.7.21", {"start": v(-24.01, 44.77) * mm, "end": v(-25.59, 47.5) * mm});
            skLineSegment(sketch, "E16.17.7.21", {"start": v(-25.59, 47.5) * mm, "end": v(-24.01, 50.23) * mm});
            skLineSegment(sketch, "E16.0.7.22", {"start": v(-24.01, 58.86) * mm, "end": v(-20.86, 58.86) * mm});
            skLineSegment(sketch, "E16.3.7.22", {"start": v(-20.86, 58.86) * mm, "end": v(-19.28, 56.13) * mm});
            skLineSegment(sketch, "E16.6.7.22", {"start": v(-19.28, 56.13) * mm, "end": v(-20.86, 53.4) * mm});
            skCircle(sketch, "E16.9.7.22", {"center": v(-22.44, 56.13) * mm, "radius": 2.73 * mm, "construction": true});
            skLineSegment(sketch, "E16.11.7.22", {"start": v(-20.86, 53.4) * mm, "end": v(-24.01, 53.4) * mm});
            skLineSegment(sketch, "E16.14.7.22", {"start": v(-24.01, 53.4) * mm, "end": v(-25.59, 56.13) * mm});
            skLineSegment(sketch, "E16.17.7.22", {"start": v(-25.59, 56.13) * mm, "end": v(-24.01, 58.86) * mm});
            skLineSegment(sketch, "E16.0.7.23", {"start": v(-24.01, 67.5) * mm, "end": v(-20.86, 67.5) * mm});
            skLineSegment(sketch, "E16.3.7.23", {"start": v(-20.86, 67.5) * mm, "end": v(-19.28, 64.77) * mm});
            skLineSegment(sketch, "E16.6.7.23", {"start": v(-19.28, 64.77) * mm, "end": v(-20.86, 62.04) * mm});
            skCircle(sketch, "E16.9.7.23", {"center": v(-22.44, 64.77) * mm, "radius": 2.73 * mm, "construction": true});
            skLineSegment(sketch, "E16.11.7.23", {"start": v(-20.86, 62.04) * mm, "end": v(-24.01, 62.04) * mm});
            skLineSegment(sketch, "E16.14.7.23", {"start": v(-24.01, 62.04) * mm, "end": v(-25.59, 64.77) * mm});
            skLineSegment(sketch, "E16.17.7.23", {"start": v(-25.59, 64.77) * mm, "end": v(-24.01, 67.5) * mm});
            skLineSegment(sketch, "E16.0.7.24", {"start": v(-24.01, 76.14) * mm, "end": v(-20.86, 76.14) * mm});
            skLineSegment(sketch, "E16.3.7.24", {"start": v(-20.86, 76.14) * mm, "end": v(-19.28, 73.4) * mm});
            skLineSegment(sketch, "E16.6.7.24", {"start": v(-19.28, 73.4) * mm, "end": v(-20.86, 70.68) * mm});
            skCircle(sketch, "E16.9.7.24", {"center": v(-22.44, 73.4) * mm, "radius": 2.73 * mm, "construction": true});
            skLineSegment(sketch, "E16.11.7.24", {"start": v(-20.86, 70.68) * mm, "end": v(-24.01, 70.68) * mm});
            skLineSegment(sketch, "E16.14.7.24", {"start": v(-24.01, 70.68) * mm, "end": v(-25.59, 73.4) * mm});
            skLineSegment(sketch, "E16.17.7.24", {"start": v(-25.59, 73.4) * mm, "end": v(-24.01, 76.14) * mm});
            skLineSegment(sketch, "E16.0.8.20", {"start": v(-9.06, 41.6) * mm, "end": v(-5.9, 41.6) * mm});
            skLineSegment(sketch, "E16.3.8.20", {"start": v(-5.9, 41.6) * mm, "end": v(-4.33, 38.86) * mm});
            skLineSegment(sketch, "E16.6.8.20", {"start": v(-4.33, 38.86) * mm, "end": v(-5.9, 36.13) * mm});
            skCircle(sketch, "E16.9.8.20", {"center": v(-7.48, 38.86) * mm, "radius": 2.73 * mm, "construction": true});
            skLineSegment(sketch, "E16.11.8.20", {"start": v(-5.9, 36.13) * mm, "end": v(-9.06, 36.13) * mm});
            skLineSegment(sketch, "E16.14.8.20", {"start": v(-9.06, 36.13) * mm, "end": v(-10.63, 38.86) * mm});
            skLineSegment(sketch, "E16.17.8.20", {"start": v(-10.63, 38.86) * mm, "end": v(-9.06, 41.6) * mm});
            skLineSegment(sketch, "E16.0.8.21", {"start": v(-9.06, 50.23) * mm, "end": v(-5.9, 50.23) * mm});
            skLineSegment(sketch, "E16.3.8.21", {"start": v(-5.9, 50.23) * mm, "end": v(-4.33, 47.5) * mm});
            skLineSegment(sketch, "E16.6.8.21", {"start": v(-4.33, 47.5) * mm, "end": v(-5.9, 44.77) * mm});
            skCircle(sketch, "E16.9.8.21", {"center": v(-7.48, 47.5) * mm, "radius": 2.73 * mm, "construction": true});
            skLineSegment(sketch, "E16.11.8.21", {"start": v(-5.9, 44.77) * mm, "end": v(-9.06, 44.77) * mm});
            skLineSegment(sketch, "E16.14.8.21", {"start": v(-9.06, 44.77) * mm, "end": v(-10.63, 47.5) * mm});
            skLineSegment(sketch, "E16.17.8.21", {"start": v(-10.63, 47.5) * mm, "end": v(-9.06, 50.23) * mm});
            skLineSegment(sketch, "E16.0.8.22", {"start": v(-9.06, 58.86) * mm, "end": v(-5.9, 58.86) * mm});
            skLineSegment(sketch, "E16.3.8.22", {"start": v(-5.9, 58.86) * mm, "end": v(-4.33, 56.13) * mm});
            skLineSegment(sketch, "E16.6.8.22", {"start": v(-4.33, 56.13) * mm, "end": v(-5.9, 53.4) * mm});
            skCircle(sketch, "E16.9.8.22", {"center": v(-7.48, 56.13) * mm, "radius": 2.73 * mm, "construction": true});
            skLineSegment(sketch, "E16.11.8.22", {"start": v(-5.9, 53.4) * mm, "end": v(-9.06, 53.4) * mm});
            skLineSegment(sketch, "E16.14.8.22", {"start": v(-9.06, 53.4) * mm, "end": v(-10.63, 56.13) * mm});
            skLineSegment(sketch, "E16.17.8.22", {"start": v(-10.63, 56.13) * mm, "end": v(-9.06, 58.86) * mm});
            skLineSegment(sketch, "E16.0.8.23", {"start": v(-9.06, 67.5) * mm, "end": v(-5.9, 67.5) * mm});
            skLineSegment(sketch, "E16.3.8.23", {"start": v(-5.9, 67.5) * mm, "end": v(-4.33, 64.77) * mm});
            skLineSegment(sketch, "E16.6.8.23", {"start": v(-4.33, 64.77) * mm, "end": v(-5.9, 62.04) * mm});
            skCircle(sketch, "E16.9.8.23", {"center": v(-7.48, 64.77) * mm, "radius": 2.73 * mm, "construction": true});
            skLineSegment(sketch, "E16.11.8.23", {"start": v(-5.9, 62.04) * mm, "end": v(-9.06, 62.04) * mm});
            skLineSegment(sketch, "E16.14.8.23", {"start": v(-9.06, 62.04) * mm, "end": v(-10.63, 64.77) * mm});
            skLineSegment(sketch, "E16.17.8.23", {"start": v(-10.63, 64.77) * mm, "end": v(-9.06, 67.5) * mm});
            skLineSegment(sketch, "E16.0.8.24", {"start": v(-9.06, 76.14) * mm, "end": v(-5.9, 76.14) * mm});
            skLineSegment(sketch, "E16.3.8.24", {"start": v(-5.9, 76.14) * mm, "end": v(-4.33, 73.4) * mm});
            skLineSegment(sketch, "E16.6.8.24", {"start": v(-4.33, 73.4) * mm, "end": v(-5.9, 70.68) * mm});
            skCircle(sketch, "E16.9.8.24", {"center": v(-7.48, 73.4) * mm, "radius": 2.73 * mm, "construction": true});
            skLineSegment(sketch, "E16.11.8.24", {"start": v(-5.9, 70.68) * mm, "end": v(-9.06, 70.68) * mm});
            skLineSegment(sketch, "E16.14.8.24", {"start": v(-9.06, 70.68) * mm, "end": v(-10.63, 73.4) * mm});
            skLineSegment(sketch, "E16.17.8.24", {"start": v(-10.63, 73.4) * mm, "end": v(-9.06, 76.14) * mm});
            skLineSegment(sketch, "E16.0.9.20", {"start": v(5.9, 41.6) * mm, "end": v(9.06, 41.6) * mm});
            skLineSegment(sketch, "E16.3.9.20", {"start": v(9.06, 41.6) * mm, "end": v(10.63, 38.86) * mm});
            skLineSegment(sketch, "E16.6.9.20", {"start": v(10.63, 38.86) * mm, "end": v(9.06, 36.13) * mm});
            skCircle(sketch, "E16.9.9.20", {"center": v(7.48, 38.86) * mm, "radius": 2.73 * mm, "construction": true});
            skLineSegment(sketch, "E16.11.9.20", {"start": v(9.06, 36.13) * mm, "end": v(5.9, 36.13) * mm});
            skLineSegment(sketch, "E16.14.9.20", {"start": v(5.9, 36.13) * mm, "end": v(4.33, 38.86) * mm});
            skLineSegment(sketch, "E16.17.9.20", {"start": v(4.33, 38.86) * mm, "end": v(5.9, 41.6) * mm});
            skLineSegment(sketch, "E16.0.9.21", {"start": v(5.9, 50.23) * mm, "end": v(9.06, 50.23) * mm});
            skLineSegment(sketch, "E16.3.9.21", {"start": v(9.06, 50.23) * mm, "end": v(10.63, 47.5) * mm});
            skLineSegment(sketch, "E16.6.9.21", {"start": v(10.63, 47.5) * mm, "end": v(9.06, 44.77) * mm});
            skCircle(sketch, "E16.9.9.21", {"center": v(7.48, 47.5) * mm, "radius": 2.73 * mm, "construction": true});
            skLineSegment(sketch, "E16.11.9.21", {"start": v(9.06, 44.77) * mm, "end": v(5.9, 44.77) * mm});
            skLineSegment(sketch, "E16.14.9.21", {"start": v(5.9, 44.77) * mm, "end": v(4.33, 47.5) * mm});
            skLineSegment(sketch, "E16.17.9.21", {"start": v(4.33, 47.5) * mm, "end": v(5.9, 50.23) * mm});
            skLineSegment(sketch, "E16.0.9.22", {"start": v(5.9, 58.86) * mm, "end": v(9.06, 58.86) * mm});
            skLineSegment(sketch, "E16.3.9.22", {"start": v(9.06, 58.86) * mm, "end": v(10.63, 56.13) * mm});
            skLineSegment(sketch, "E16.6.9.22", {"start": v(10.63, 56.13) * mm, "end": v(9.06, 53.4) * mm});
            skCircle(sketch, "E16.9.9.22", {"center": v(7.48, 56.13) * mm, "radius": 2.73 * mm, "construction": true});
            skLineSegment(sketch, "E16.11.9.22", {"start": v(9.06, 53.4) * mm, "end": v(5.9, 53.4) * mm});
            skLineSegment(sketch, "E16.14.9.22", {"start": v(5.9, 53.4) * mm, "end": v(4.33, 56.13) * mm});
            skLineSegment(sketch, "E16.17.9.22", {"start": v(4.33, 56.13) * mm, "end": v(5.9, 58.86) * mm});
            skLineSegment(sketch, "E16.0.9.23", {"start": v(5.9, 67.5) * mm, "end": v(9.06, 67.5) * mm});
            skLineSegment(sketch, "E16.3.9.23", {"start": v(9.06, 67.5) * mm, "end": v(10.63, 64.77) * mm});
            skLineSegment(sketch, "E16.6.9.23", {"start": v(10.63, 64.77) * mm, "end": v(9.06, 62.04) * mm});
            skCircle(sketch, "E16.9.9.23", {"center": v(7.48, 64.77) * mm, "radius": 2.73 * mm, "construction": true});
            skLineSegment(sketch, "E16.11.9.23", {"start": v(9.06, 62.04) * mm, "end": v(5.9, 62.04) * mm});
            skLineSegment(sketch, "E16.14.9.23", {"start": v(5.9, 62.04) * mm, "end": v(4.33, 64.77) * mm});
            skLineSegment(sketch, "E16.17.9.23", {"start": v(4.33, 64.77) * mm, "end": v(5.9, 67.5) * mm});
            skLineSegment(sketch, "E16.0.9.24", {"start": v(5.9, 76.14) * mm, "end": v(9.06, 76.14) * mm});
            skLineSegment(sketch, "E16.3.9.24", {"start": v(9.06, 76.14) * mm, "end": v(10.63, 73.4) * mm});
            skLineSegment(sketch, "E16.6.9.24", {"start": v(10.63, 73.4) * mm, "end": v(9.06, 70.68) * mm});
            skCircle(sketch, "E16.9.9.24", {"center": v(7.48, 73.4) * mm, "radius": 2.73 * mm, "construction": true});
            skLineSegment(sketch, "E16.11.9.24", {"start": v(9.06, 70.68) * mm, "end": v(5.9, 70.68) * mm});
            skLineSegment(sketch, "E16.14.9.24", {"start": v(5.9, 70.68) * mm, "end": v(4.33, 73.4) * mm});
            skLineSegment(sketch, "E16.17.9.24", {"start": v(4.33, 73.4) * mm, "end": v(5.9, 76.14) * mm});
            skLineSegment(sketch, "E16.0.10.20", {"start": v(20.86, 41.6) * mm, "end": v(24.01, 41.6) * mm});
            skLineSegment(sketch, "E16.3.10.20", {"start": v(24.01, 41.6) * mm, "end": v(25.6, 38.86) * mm});
            skLineSegment(sketch, "E16.6.10.20", {"start": v(25.6, 38.86) * mm, "end": v(24.01, 36.13) * mm});
            skCircle(sketch, "E16.9.10.20", {"center": v(22.44, 38.86) * mm, "radius": 2.73 * mm, "construction": true});
            skLineSegment(sketch, "E16.11.10.20", {"start": v(24.01, 36.13) * mm, "end": v(20.86, 36.13) * mm});
            skLineSegment(sketch, "E16.14.10.20", {"start": v(20.86, 36.13) * mm, "end": v(19.28, 38.86) * mm});
            skLineSegment(sketch, "E16.17.10.20", {"start": v(19.28, 38.86) * mm, "end": v(20.86, 41.6) * mm});
            skLineSegment(sketch, "E16.0.10.21", {"start": v(20.86, 50.23) * mm, "end": v(24.01, 50.23) * mm});
            skLineSegment(sketch, "E16.3.10.21", {"start": v(24.01, 50.23) * mm, "end": v(25.6, 47.5) * mm});
            skLineSegment(sketch, "E16.6.10.21", {"start": v(25.6, 47.5) * mm, "end": v(24.01, 44.77) * mm});
            skCircle(sketch, "E16.9.10.21", {"center": v(22.44, 47.5) * mm, "radius": 2.73 * mm, "construction": true});
            skLineSegment(sketch, "E16.11.10.21", {"start": v(24.01, 44.77) * mm, "end": v(20.86, 44.77) * mm});
            skLineSegment(sketch, "E16.14.10.21", {"start": v(20.86, 44.77) * mm, "end": v(19.28, 47.5) * mm});
            skLineSegment(sketch, "E16.17.10.21", {"start": v(19.28, 47.5) * mm, "end": v(20.86, 50.23) * mm});
            skLineSegment(sketch, "E16.0.10.22", {"start": v(20.86, 58.86) * mm, "end": v(24.01, 58.86) * mm});
            skLineSegment(sketch, "E16.3.10.22", {"start": v(24.01, 58.86) * mm, "end": v(25.6, 56.13) * mm});
            skLineSegment(sketch, "E16.6.10.22", {"start": v(25.6, 56.13) * mm, "end": v(24.01, 53.4) * mm});
            skCircle(sketch, "E16.9.10.22", {"center": v(22.44, 56.13) * mm, "radius": 2.73 * mm, "construction": true});
            skLineSegment(sketch, "E16.11.10.22", {"start": v(24.01, 53.4) * mm, "end": v(20.86, 53.4) * mm});
            skLineSegment(sketch, "E16.14.10.22", {"start": v(20.86, 53.4) * mm, "end": v(19.28, 56.13) * mm});
            skLineSegment(sketch, "E16.17.10.22", {"start": v(19.28, 56.13) * mm, "end": v(20.86, 58.86) * mm});
            skLineSegment(sketch, "E16.0.10.23", {"start": v(20.86, 67.5) * mm, "end": v(24.01, 67.5) * mm});
            skLineSegment(sketch, "E16.3.10.23", {"start": v(24.01, 67.5) * mm, "end": v(25.6, 64.77) * mm});
            skLineSegment(sketch, "E16.6.10.23", {"start": v(25.6, 64.77) * mm, "end": v(24.01, 62.04) * mm});
            skCircle(sketch, "E16.9.10.23", {"center": v(22.44, 64.77) * mm, "radius": 2.73 * mm, "construction": true});
            skLineSegment(sketch, "E16.11.10.23", {"start": v(24.01, 62.04) * mm, "end": v(20.86, 62.04) * mm});
            skLineSegment(sketch, "E16.14.10.23", {"start": v(20.86, 62.04) * mm, "end": v(19.28, 64.77) * mm});
            skLineSegment(sketch, "E16.17.10.23", {"start": v(19.28, 64.77) * mm, "end": v(20.86, 67.5) * mm});
            skLineSegment(sketch, "E16.0.10.24", {"start": v(20.86, 76.14) * mm, "end": v(24.01, 76.14) * mm});
            skLineSegment(sketch, "E16.3.10.24", {"start": v(24.01, 76.14) * mm, "end": v(25.6, 73.4) * mm});
            skLineSegment(sketch, "E16.6.10.24", {"start": v(25.6, 73.4) * mm, "end": v(24.01, 70.68) * mm});
            skCircle(sketch, "E16.9.10.24", {"center": v(22.44, 73.4) * mm, "radius": 2.73 * mm, "construction": true});
            skLineSegment(sketch, "E16.11.10.24", {"start": v(24.01, 70.68) * mm, "end": v(20.86, 70.68) * mm});
            skLineSegment(sketch, "E16.14.10.24", {"start": v(20.86, 70.68) * mm, "end": v(19.28, 73.4) * mm});
            skLineSegment(sketch, "E16.17.10.24", {"start": v(19.28, 73.4) * mm, "end": v(20.86, 76.14) * mm});
            skLineSegment(sketch, "E16.0.11.20", {"start": v(35.82, 41.6) * mm, "end": v(38.97, 41.6) * mm});
            skLineSegment(sketch, "E16.3.11.20", {"start": v(38.97, 41.6) * mm, "end": v(40.55, 38.86) * mm});
            skLineSegment(sketch, "E16.6.11.20", {"start": v(40.55, 38.86) * mm, "end": v(38.97, 36.13) * mm});
            skCircle(sketch, "E16.9.11.20", {"center": v(37.4, 38.86) * mm, "radius": 2.73 * mm, "construction": true});
            skLineSegment(sketch, "E16.11.11.20", {"start": v(38.97, 36.13) * mm, "end": v(35.82, 36.13) * mm});
            skLineSegment(sketch, "E16.14.11.20", {"start": v(35.82, 36.13) * mm, "end": v(34.24, 38.86) * mm});
            skLineSegment(sketch, "E16.17.11.20", {"start": v(34.24, 38.86) * mm, "end": v(35.82, 41.6) * mm});
            skLineSegment(sketch, "E16.0.11.21", {"start": v(35.82, 50.23) * mm, "end": v(38.97, 50.23) * mm});
            skLineSegment(sketch, "E16.3.11.21", {"start": v(38.97, 50.23) * mm, "end": v(40.55, 47.5) * mm});
            skLineSegment(sketch, "E16.6.11.21", {"start": v(40.55, 47.5) * mm, "end": v(38.97, 44.77) * mm});
            skCircle(sketch, "E16.9.11.21", {"center": v(37.4, 47.5) * mm, "radius": 2.73 * mm, "construction": true});
            skLineSegment(sketch, "E16.11.11.21", {"start": v(38.97, 44.77) * mm, "end": v(35.82, 44.77) * mm});
            skLineSegment(sketch, "E16.14.11.21", {"start": v(35.82, 44.77) * mm, "end": v(34.24, 47.5) * mm});
            skLineSegment(sketch, "E16.17.11.21", {"start": v(34.24, 47.5) * mm, "end": v(35.82, 50.23) * mm});
            skLineSegment(sketch, "E16.0.11.22", {"start": v(35.82, 58.86) * mm, "end": v(38.97, 58.86) * mm});
            skLineSegment(sketch, "E16.3.11.22", {"start": v(38.97, 58.86) * mm, "end": v(40.55, 56.13) * mm});
            skLineSegment(sketch, "E16.6.11.22", {"start": v(40.55, 56.13) * mm, "end": v(38.97, 53.4) * mm});
            skCircle(sketch, "E16.9.11.22", {"center": v(37.4, 56.13) * mm, "radius": 2.73 * mm, "construction": true});
            skLineSegment(sketch, "E16.11.11.22", {"start": v(38.97, 53.4) * mm, "end": v(35.82, 53.4) * mm});
            skLineSegment(sketch, "E16.14.11.22", {"start": v(35.82, 53.4) * mm, "end": v(34.24, 56.13) * mm});
            skLineSegment(sketch, "E16.17.11.22", {"start": v(34.24, 56.13) * mm, "end": v(35.82, 58.86) * mm});
            skLineSegment(sketch, "E16.0.11.23", {"start": v(35.82, 67.5) * mm, "end": v(38.97, 67.5) * mm});
            skLineSegment(sketch, "E16.3.11.23", {"start": v(38.97, 67.5) * mm, "end": v(40.55, 64.77) * mm});
            skLineSegment(sketch, "E16.6.11.23", {"start": v(40.55, 64.77) * mm, "end": v(38.97, 62.04) * mm});
            skCircle(sketch, "E16.9.11.23", {"center": v(37.4, 64.77) * mm, "radius": 2.73 * mm, "construction": true});
            skLineSegment(sketch, "E16.11.11.23", {"start": v(38.97, 62.04) * mm, "end": v(35.82, 62.04) * mm});
            skLineSegment(sketch, "E16.14.11.23", {"start": v(35.82, 62.04) * mm, "end": v(34.24, 64.77) * mm});
            skLineSegment(sketch, "E16.17.11.23", {"start": v(34.24, 64.77) * mm, "end": v(35.82, 67.5) * mm});
            skLineSegment(sketch, "E16.0.11.24", {"start": v(35.82, 76.14) * mm, "end": v(38.97, 76.14) * mm});
            skLineSegment(sketch, "E16.3.11.24", {"start": v(38.97, 76.14) * mm, "end": v(40.55, 73.4) * mm});
            skLineSegment(sketch, "E16.6.11.24", {"start": v(40.55, 73.4) * mm, "end": v(38.97, 70.68) * mm});
            skCircle(sketch, "E16.9.11.24", {"center": v(37.4, 73.4) * mm, "radius": 2.73 * mm, "construction": true});
            skLineSegment(sketch, "E16.11.11.24", {"start": v(38.97, 70.68) * mm, "end": v(35.82, 70.68) * mm});
            skLineSegment(sketch, "E16.14.11.24", {"start": v(35.82, 70.68) * mm, "end": v(34.24, 73.4) * mm});
            skLineSegment(sketch, "E16.17.11.24", {"start": v(34.24, 73.4) * mm, "end": v(35.82, 76.14) * mm});
            skLineSegment(sketch, "E16.0.12.20", {"start": v(50.78, 41.6) * mm, "end": v(53.93, 41.6) * mm});
            skLineSegment(sketch, "E16.3.12.20", {"start": v(53.93, 41.6) * mm, "end": v(55.5, 38.86) * mm});
            skLineSegment(sketch, "E16.6.12.20", {"start": v(55.5, 38.86) * mm, "end": v(53.93, 36.13) * mm});
            skCircle(sketch, "E16.9.12.20", {"center": v(52.35, 38.86) * mm, "radius": 2.73 * mm, "construction": true});
            skLineSegment(sketch, "E16.11.12.20", {"start": v(53.93, 36.13) * mm, "end": v(50.78, 36.13) * mm});
            skLineSegment(sketch, "E16.14.12.20", {"start": v(50.78, 36.13) * mm, "end": v(49.2, 38.86) * mm});
            skLineSegment(sketch, "E16.17.12.20", {"start": v(49.2, 38.86) * mm, "end": v(50.78, 41.6) * mm});
            skLineSegment(sketch, "E16.0.12.21", {"start": v(50.78, 50.23) * mm, "end": v(53.93, 50.23) * mm});
            skLineSegment(sketch, "E16.3.12.21", {"start": v(53.93, 50.23) * mm, "end": v(55.5, 47.5) * mm});
            skLineSegment(sketch, "E16.6.12.21", {"start": v(55.5, 47.5) * mm, "end": v(53.93, 44.77) * mm});
            skCircle(sketch, "E16.9.12.21", {"center": v(52.35, 47.5) * mm, "radius": 2.73 * mm, "construction": true});
            skLineSegment(sketch, "E16.11.12.21", {"start": v(53.93, 44.77) * mm, "end": v(50.78, 44.77) * mm});
            skLineSegment(sketch, "E16.14.12.21", {"start": v(50.78, 44.77) * mm, "end": v(49.2, 47.5) * mm});
            skLineSegment(sketch, "E16.17.12.21", {"start": v(49.2, 47.5) * mm, "end": v(50.78, 50.23) * mm});
            skLineSegment(sketch, "E16.0.12.22", {"start": v(50.78, 58.86) * mm, "end": v(53.93, 58.86) * mm});
            skLineSegment(sketch, "E16.3.12.22", {"start": v(53.93, 58.86) * mm, "end": v(55.5, 56.13) * mm});
            skLineSegment(sketch, "E16.6.12.22", {"start": v(55.5, 56.13) * mm, "end": v(53.93, 53.4) * mm});
            skCircle(sketch, "E16.9.12.22", {"center": v(52.35, 56.13) * mm, "radius": 2.73 * mm, "construction": true});
            skLineSegment(sketch, "E16.11.12.22", {"start": v(53.93, 53.4) * mm, "end": v(50.78, 53.4) * mm});
            skLineSegment(sketch, "E16.14.12.22", {"start": v(50.78, 53.4) * mm, "end": v(49.2, 56.13) * mm});
            skLineSegment(sketch, "E16.17.12.22", {"start": v(49.2, 56.13) * mm, "end": v(50.78, 58.86) * mm});
            skLineSegment(sketch, "E16.0.12.23", {"start": v(50.78, 67.5) * mm, "end": v(53.93, 67.5) * mm});
            skLineSegment(sketch, "E16.3.12.23", {"start": v(53.93, 67.5) * mm, "end": v(55.5, 64.77) * mm});
            skLineSegment(sketch, "E16.6.12.23", {"start": v(55.5, 64.77) * mm, "end": v(53.93, 62.04) * mm});
            skCircle(sketch, "E16.9.12.23", {"center": v(52.35, 64.77) * mm, "radius": 2.73 * mm, "construction": true});
            skLineSegment(sketch, "E16.11.12.23", {"start": v(53.93, 62.04) * mm, "end": v(50.78, 62.04) * mm});
            skLineSegment(sketch, "E16.14.12.23", {"start": v(50.78, 62.04) * mm, "end": v(49.2, 64.77) * mm});
            skLineSegment(sketch, "E16.17.12.23", {"start": v(49.2, 64.77) * mm, "end": v(50.78, 67.5) * mm});
            skLineSegment(sketch, "E16.0.12.24", {"start": v(50.78, 76.14) * mm, "end": v(53.93, 76.14) * mm});
            skLineSegment(sketch, "E16.3.12.24", {"start": v(53.93, 76.14) * mm, "end": v(55.5, 73.4) * mm});
            skLineSegment(sketch, "E16.6.12.24", {"start": v(55.5, 73.4) * mm, "end": v(53.93, 70.68) * mm});
            skCircle(sketch, "E16.9.12.24", {"center": v(52.35, 73.4) * mm, "radius": 2.73 * mm, "construction": true});
            skLineSegment(sketch, "E16.11.12.24", {"start": v(53.93, 70.68) * mm, "end": v(50.78, 70.68) * mm});
            skLineSegment(sketch, "E16.14.12.24", {"start": v(50.78, 70.68) * mm, "end": v(49.2, 73.4) * mm});
            skLineSegment(sketch, "E16.17.12.24", {"start": v(49.2, 73.4) * mm, "end": v(50.78, 76.14) * mm});
            skLineSegment(sketch, "E16.0.13.20", {"start": v(65.73, 41.6) * mm, "end": v(68.89, 41.6) * mm});
            skLineSegment(sketch, "E16.3.13.20", {"start": v(68.89, 41.6) * mm, "end": v(70.46, 38.86) * mm});
            skLineSegment(sketch, "E16.6.13.20", {"start": v(70.46, 38.86) * mm, "end": v(68.89, 36.13) * mm});
            skCircle(sketch, "E16.9.13.20", {"center": v(67.31, 38.86) * mm, "radius": 2.73 * mm, "construction": true});
            skLineSegment(sketch, "E16.11.13.20", {"start": v(68.89, 36.13) * mm, "end": v(65.73, 36.13) * mm});
            skLineSegment(sketch, "E16.14.13.20", {"start": v(65.73, 36.13) * mm, "end": v(64.16, 38.86) * mm});
            skLineSegment(sketch, "E16.17.13.20", {"start": v(64.16, 38.86) * mm, "end": v(65.73, 41.6) * mm});
            skLineSegment(sketch, "E16.0.13.21", {"start": v(65.73, 50.23) * mm, "end": v(68.89, 50.23) * mm});
            skLineSegment(sketch, "E16.3.13.21", {"start": v(68.89, 50.23) * mm, "end": v(70.46, 47.5) * mm});
            skLineSegment(sketch, "E16.6.13.21", {"start": v(70.46, 47.5) * mm, "end": v(68.89, 44.77) * mm});
            skCircle(sketch, "E16.9.13.21", {"center": v(67.31, 47.5) * mm, "radius": 2.73 * mm, "construction": true});
            skLineSegment(sketch, "E16.11.13.21", {"start": v(68.89, 44.77) * mm, "end": v(65.73, 44.77) * mm});
            skLineSegment(sketch, "E16.14.13.21", {"start": v(65.73, 44.77) * mm, "end": v(64.16, 47.5) * mm});
            skLineSegment(sketch, "E16.17.13.21", {"start": v(64.16, 47.5) * mm, "end": v(65.73, 50.23) * mm});
            skLineSegment(sketch, "E16.0.13.22", {"start": v(65.73, 58.86) * mm, "end": v(68.89, 58.86) * mm});
            skLineSegment(sketch, "E16.3.13.22", {"start": v(68.89, 58.86) * mm, "end": v(70.46, 56.13) * mm});
            skLineSegment(sketch, "E16.6.13.22", {"start": v(70.46, 56.13) * mm, "end": v(68.89, 53.4) * mm});
            skCircle(sketch, "E16.9.13.22", {"center": v(67.31, 56.13) * mm, "radius": 2.73 * mm, "construction": true});
            skLineSegment(sketch, "E16.11.13.22", {"start": v(68.89, 53.4) * mm, "end": v(65.73, 53.4) * mm});
            skLineSegment(sketch, "E16.14.13.22", {"start": v(65.73, 53.4) * mm, "end": v(64.16, 56.13) * mm});
            skLineSegment(sketch, "E16.17.13.22", {"start": v(64.16, 56.13) * mm, "end": v(65.73, 58.86) * mm});
            skLineSegment(sketch, "E16.0.13.23", {"start": v(65.73, 67.5) * mm, "end": v(68.89, 67.5) * mm});
            skLineSegment(sketch, "E16.3.13.23", {"start": v(68.89, 67.5) * mm, "end": v(70.46, 64.77) * mm});
            skLineSegment(sketch, "E16.6.13.23", {"start": v(70.46, 64.77) * mm, "end": v(68.89, 62.04) * mm});
            skCircle(sketch, "E16.9.13.23", {"center": v(67.31, 64.77) * mm, "radius": 2.73 * mm, "construction": true});
            skLineSegment(sketch, "E16.11.13.23", {"start": v(68.89, 62.04) * mm, "end": v(65.73, 62.04) * mm});
            skLineSegment(sketch, "E16.14.13.23", {"start": v(65.73, 62.04) * mm, "end": v(64.16, 64.77) * mm});
            skLineSegment(sketch, "E16.17.13.23", {"start": v(64.16, 64.77) * mm, "end": v(65.73, 67.5) * mm});
            skLineSegment(sketch, "E16.0.13.24", {"start": v(65.73, 76.14) * mm, "end": v(68.89, 76.14) * mm});
            skLineSegment(sketch, "E16.3.13.24", {"start": v(68.89, 76.14) * mm, "end": v(70.46, 73.4) * mm});
            skLineSegment(sketch, "E16.6.13.24", {"start": v(70.46, 73.4) * mm, "end": v(68.89, 70.68) * mm});
            skCircle(sketch, "E16.9.13.24", {"center": v(67.31, 73.4) * mm, "radius": 2.73 * mm, "construction": true});
            skLineSegment(sketch, "E16.11.13.24", {"start": v(68.89, 70.68) * mm, "end": v(65.73, 70.68) * mm});
            skLineSegment(sketch, "E16.14.13.24", {"start": v(65.73, 70.68) * mm, "end": v(64.16, 73.4) * mm});
            skLineSegment(sketch, "E16.17.13.24", {"start": v(64.16, 73.4) * mm, "end": v(65.73, 76.14) * mm});
            skLineSegment(sketch, "E16.0.14.20", {"start": v(80.7, 41.6) * mm, "end": v(83.85, 41.6) * mm});
            skLineSegment(sketch, "E16.3.14.20", {"start": v(83.85, 41.6) * mm, "end": v(85.42, 38.86) * mm});
            skLineSegment(sketch, "E16.6.14.20", {"start": v(85.42, 38.86) * mm, "end": v(83.85, 36.13) * mm});
            skCircle(sketch, "E16.9.14.20", {"center": v(82.27, 38.86) * mm, "radius": 2.73 * mm, "construction": true});
            skLineSegment(sketch, "E16.11.14.20", {"start": v(83.85, 36.13) * mm, "end": v(80.7, 36.13) * mm});
            skLineSegment(sketch, "E16.14.14.20", {"start": v(80.7, 36.13) * mm, "end": v(79.12, 38.86) * mm});
            skLineSegment(sketch, "E16.17.14.20", {"start": v(79.12, 38.86) * mm, "end": v(80.7, 41.6) * mm});
            skLineSegment(sketch, "E16.0.14.21", {"start": v(80.7, 50.23) * mm, "end": v(83.85, 50.23) * mm});
            skLineSegment(sketch, "E16.3.14.21", {"start": v(83.85, 50.23) * mm, "end": v(85.42, 47.5) * mm});
            skLineSegment(sketch, "E16.6.14.21", {"start": v(85.42, 47.5) * mm, "end": v(83.85, 44.77) * mm});
            skCircle(sketch, "E16.9.14.21", {"center": v(82.27, 47.5) * mm, "radius": 2.73 * mm, "construction": true});
            skLineSegment(sketch, "E16.11.14.21", {"start": v(83.85, 44.77) * mm, "end": v(80.7, 44.77) * mm});
            skLineSegment(sketch, "E16.14.14.21", {"start": v(80.7, 44.77) * mm, "end": v(79.12, 47.5) * mm});
            skLineSegment(sketch, "E16.17.14.21", {"start": v(79.12, 47.5) * mm, "end": v(80.7, 50.23) * mm});
            skLineSegment(sketch, "E16.0.14.22", {"start": v(80.7, 58.86) * mm, "end": v(83.85, 58.86) * mm});
            skLineSegment(sketch, "E16.3.14.22", {"start": v(83.85, 58.86) * mm, "end": v(85.42, 56.13) * mm});
            skLineSegment(sketch, "E16.6.14.22", {"start": v(85.42, 56.13) * mm, "end": v(83.85, 53.4) * mm});
            skCircle(sketch, "E16.9.14.22", {"center": v(82.27, 56.13) * mm, "radius": 2.73 * mm, "construction": true});
            skLineSegment(sketch, "E16.11.14.22", {"start": v(83.85, 53.4) * mm, "end": v(80.7, 53.4) * mm});
            skLineSegment(sketch, "E16.14.14.22", {"start": v(80.7, 53.4) * mm, "end": v(79.12, 56.13) * mm});
            skLineSegment(sketch, "E16.17.14.22", {"start": v(79.12, 56.13) * mm, "end": v(80.7, 58.86) * mm});
            skLineSegment(sketch, "E16.0.14.23", {"start": v(80.7, 67.5) * mm, "end": v(83.85, 67.5) * mm});
            skLineSegment(sketch, "E16.3.14.23", {"start": v(83.85, 67.5) * mm, "end": v(85.42, 64.77) * mm});
            skLineSegment(sketch, "E16.6.14.23", {"start": v(85.42, 64.77) * mm, "end": v(83.85, 62.04) * mm});
            skCircle(sketch, "E16.9.14.23", {"center": v(82.27, 64.77) * mm, "radius": 2.73 * mm, "construction": true});
            skLineSegment(sketch, "E16.11.14.23", {"start": v(83.85, 62.04) * mm, "end": v(80.7, 62.04) * mm});
            skLineSegment(sketch, "E16.14.14.23", {"start": v(80.7, 62.04) * mm, "end": v(79.12, 64.77) * mm});
            skLineSegment(sketch, "E16.17.14.23", {"start": v(79.12, 64.77) * mm, "end": v(80.7, 67.5) * mm});
            skLineSegment(sketch, "E16.0.14.24", {"start": v(80.7, 76.14) * mm, "end": v(83.85, 76.14) * mm});
            skLineSegment(sketch, "E16.3.14.24", {"start": v(83.85, 76.14) * mm, "end": v(85.42, 73.4) * mm});
            skLineSegment(sketch, "E16.6.14.24", {"start": v(85.42, 73.4) * mm, "end": v(83.85, 70.68) * mm});
            skCircle(sketch, "E16.9.14.24", {"center": v(82.27, 73.4) * mm, "radius": 2.73 * mm, "construction": true});
            skLineSegment(sketch, "E16.11.14.24", {"start": v(83.85, 70.68) * mm, "end": v(80.7, 70.68) * mm});
            skLineSegment(sketch, "E16.14.14.24", {"start": v(80.7, 70.68) * mm, "end": v(79.12, 73.4) * mm});
            skLineSegment(sketch, "E16.17.14.24", {"start": v(79.12, 73.4) * mm, "end": v(80.7, 76.14) * mm});
            skLineSegment(sketch, "E16.0.15.20", {"start": v(95.65, 41.6) * mm, "end": v(98.8, 41.6) * mm});
            skLineSegment(sketch, "E16.3.15.20", {"start": v(98.8, 41.6) * mm, "end": v(100.38, 38.86) * mm});
            skLineSegment(sketch, "E16.6.15.20", {"start": v(100.38, 38.86) * mm, "end": v(98.8, 36.13) * mm});
            skCircle(sketch, "E16.9.15.20", {"center": v(97.23, 38.86) * mm, "radius": 2.73 * mm, "construction": true});
            skLineSegment(sketch, "E16.11.15.20", {"start": v(98.8, 36.13) * mm, "end": v(95.65, 36.13) * mm});
            skLineSegment(sketch, "E16.14.15.20", {"start": v(95.65, 36.13) * mm, "end": v(94.07, 38.86) * mm});
            skLineSegment(sketch, "E16.17.15.20", {"start": v(94.07, 38.86) * mm, "end": v(95.65, 41.6) * mm});
            skLineSegment(sketch, "E16.0.15.21", {"start": v(95.65, 50.23) * mm, "end": v(98.8, 50.23) * mm});
            skLineSegment(sketch, "E16.3.15.21", {"start": v(98.8, 50.23) * mm, "end": v(100.38, 47.5) * mm});
            skLineSegment(sketch, "E16.6.15.21", {"start": v(100.38, 47.5) * mm, "end": v(98.8, 44.77) * mm});
            skCircle(sketch, "E16.9.15.21", {"center": v(97.23, 47.5) * mm, "radius": 2.73 * mm, "construction": true});
            skLineSegment(sketch, "E16.11.15.21", {"start": v(98.8, 44.77) * mm, "end": v(95.65, 44.77) * mm});
            skLineSegment(sketch, "E16.14.15.21", {"start": v(95.65, 44.77) * mm, "end": v(94.07, 47.5) * mm});
            skLineSegment(sketch, "E16.17.15.21", {"start": v(94.07, 47.5) * mm, "end": v(95.65, 50.23) * mm});
            skLineSegment(sketch, "E16.0.15.22", {"start": v(95.65, 58.86) * mm, "end": v(98.8, 58.86) * mm});
            skLineSegment(sketch, "E16.3.15.22", {"start": v(98.8, 58.86) * mm, "end": v(100.38, 56.13) * mm});
            skLineSegment(sketch, "E16.6.15.22", {"start": v(100.38, 56.13) * mm, "end": v(98.8, 53.4) * mm});
            skCircle(sketch, "E16.9.15.22", {"center": v(97.23, 56.13) * mm, "radius": 2.73 * mm, "construction": true});
            skLineSegment(sketch, "E16.11.15.22", {"start": v(98.8, 53.4) * mm, "end": v(95.65, 53.4) * mm});
            skLineSegment(sketch, "E16.14.15.22", {"start": v(95.65, 53.4) * mm, "end": v(94.07, 56.13) * mm});
            skLineSegment(sketch, "E16.17.15.22", {"start": v(94.07, 56.13) * mm, "end": v(95.65, 58.86) * mm});
            skLineSegment(sketch, "E16.0.15.23", {"start": v(95.65, 67.5) * mm, "end": v(98.8, 67.5) * mm});
            skLineSegment(sketch, "E16.3.15.23", {"start": v(98.8, 67.5) * mm, "end": v(100.38, 64.77) * mm});
            skLineSegment(sketch, "E16.6.15.23", {"start": v(100.38, 64.77) * mm, "end": v(98.8, 62.04) * mm});
            skCircle(sketch, "E16.9.15.23", {"center": v(97.23, 64.77) * mm, "radius": 2.73 * mm, "construction": true});
            skLineSegment(sketch, "E16.11.15.23", {"start": v(98.8, 62.04) * mm, "end": v(95.65, 62.04) * mm});
            skLineSegment(sketch, "E16.14.15.23", {"start": v(95.65, 62.04) * mm, "end": v(94.07, 64.77) * mm});
            skLineSegment(sketch, "E16.17.15.23", {"start": v(94.07, 64.77) * mm, "end": v(95.65, 67.5) * mm});
            skLineSegment(sketch, "E16.0.15.24", {"start": v(95.65, 76.14) * mm, "end": v(98.8, 76.14) * mm});
            skLineSegment(sketch, "E16.3.15.24", {"start": v(98.8, 76.14) * mm, "end": v(100.38, 73.4) * mm});
            skLineSegment(sketch, "E16.6.15.24", {"start": v(100.38, 73.4) * mm, "end": v(98.8, 70.68) * mm});
            skCircle(sketch, "E16.9.15.24", {"center": v(97.23, 73.4) * mm, "radius": 2.73 * mm, "construction": true});
            skLineSegment(sketch, "E16.11.15.24", {"start": v(98.8, 70.68) * mm, "end": v(95.65, 70.68) * mm});
            skLineSegment(sketch, "E16.14.15.24", {"start": v(95.65, 70.68) * mm, "end": v(94.07, 73.4) * mm});
            skLineSegment(sketch, "E16.17.15.24", {"start": v(94.07, 73.4) * mm, "end": v(95.65, 76.14) * mm});
            skLineSegment(sketch, "E16.0.16.20", {"start": v(110.6, 41.6) * mm, "end": v(113.76, 41.6) * mm});
            skLineSegment(sketch, "E16.3.16.20", {"start": v(113.76, 41.6) * mm, "end": v(115.34, 38.86) * mm});
            skLineSegment(sketch, "E16.6.16.20", {"start": v(115.34, 38.86) * mm, "end": v(113.76, 36.13) * mm});
            skCircle(sketch, "E16.9.16.20", {"center": v(112.19, 38.86) * mm, "radius": 2.73 * mm, "construction": true});
            skLineSegment(sketch, "E16.11.16.20", {"start": v(113.76, 36.13) * mm, "end": v(110.6, 36.13) * mm});
            skLineSegment(sketch, "E16.14.16.20", {"start": v(110.6, 36.13) * mm, "end": v(109.03, 38.86) * mm});
            skLineSegment(sketch, "E16.17.16.20", {"start": v(109.03, 38.86) * mm, "end": v(110.6, 41.6) * mm});
            skLineSegment(sketch, "E16.0.16.21", {"start": v(110.6, 50.23) * mm, "end": v(113.76, 50.23) * mm});
            skLineSegment(sketch, "E16.3.16.21", {"start": v(113.76, 50.23) * mm, "end": v(115.34, 47.5) * mm});
            skLineSegment(sketch, "E16.6.16.21", {"start": v(115.34, 47.5) * mm, "end": v(113.76, 44.77) * mm});
            skCircle(sketch, "E16.9.16.21", {"center": v(112.19, 47.5) * mm, "radius": 2.73 * mm, "construction": true});
            skLineSegment(sketch, "E16.11.16.21", {"start": v(113.76, 44.77) * mm, "end": v(110.6, 44.77) * mm});
            skLineSegment(sketch, "E16.14.16.21", {"start": v(110.6, 44.77) * mm, "end": v(109.03, 47.5) * mm});
            skLineSegment(sketch, "E16.17.16.21", {"start": v(109.03, 47.5) * mm, "end": v(110.6, 50.23) * mm});
            skLineSegment(sketch, "E16.0.16.22", {"start": v(110.6, 58.86) * mm, "end": v(113.76, 58.86) * mm});
            skLineSegment(sketch, "E16.3.16.22", {"start": v(113.76, 58.86) * mm, "end": v(115.34, 56.13) * mm});
            skLineSegment(sketch, "E16.6.16.22", {"start": v(115.34, 56.13) * mm, "end": v(113.76, 53.4) * mm});
            skCircle(sketch, "E16.9.16.22", {"center": v(112.19, 56.13) * mm, "radius": 2.73 * mm, "construction": true});
            skLineSegment(sketch, "E16.11.16.22", {"start": v(113.76, 53.4) * mm, "end": v(110.6, 53.4) * mm});
            skLineSegment(sketch, "E16.14.16.22", {"start": v(110.6, 53.4) * mm, "end": v(109.03, 56.13) * mm});
            skLineSegment(sketch, "E16.17.16.22", {"start": v(109.03, 56.13) * mm, "end": v(110.6, 58.86) * mm});
            skLineSegment(sketch, "E16.0.16.23", {"start": v(110.6, 67.5) * mm, "end": v(113.76, 67.5) * mm});
            skLineSegment(sketch, "E16.3.16.23", {"start": v(113.76, 67.5) * mm, "end": v(115.34, 64.77) * mm});
            skLineSegment(sketch, "E16.6.16.23", {"start": v(115.34, 64.77) * mm, "end": v(113.76, 62.04) * mm});
            skCircle(sketch, "E16.9.16.23", {"center": v(112.19, 64.77) * mm, "radius": 2.73 * mm, "construction": true});
            skLineSegment(sketch, "E16.11.16.23", {"start": v(113.76, 62.04) * mm, "end": v(110.6, 62.04) * mm});
            skLineSegment(sketch, "E16.14.16.23", {"start": v(110.6, 62.04) * mm, "end": v(109.03, 64.77) * mm});
            skLineSegment(sketch, "E16.17.16.23", {"start": v(109.03, 64.77) * mm, "end": v(110.6, 67.5) * mm});
            skLineSegment(sketch, "E16.0.16.24", {"start": v(110.6, 76.14) * mm, "end": v(113.76, 76.14) * mm});
            skLineSegment(sketch, "E16.3.16.24", {"start": v(113.76, 76.14) * mm, "end": v(115.34, 73.4) * mm});
            skLineSegment(sketch, "E16.6.16.24", {"start": v(115.34, 73.4) * mm, "end": v(113.76, 70.68) * mm});
            skCircle(sketch, "E16.9.16.24", {"center": v(112.19, 73.4) * mm, "radius": 2.73 * mm, "construction": true});
            skLineSegment(sketch, "E16.11.16.24", {"start": v(113.76, 70.68) * mm, "end": v(110.6, 70.68) * mm});
            skLineSegment(sketch, "E16.14.16.24", {"start": v(110.6, 70.68) * mm, "end": v(109.03, 73.4) * mm});
            skLineSegment(sketch, "E16.17.16.24", {"start": v(109.03, 73.4) * mm, "end": v(110.6, 76.14) * mm});
            skLineSegment(sketch, "E16.0.17.20", {"start": v(125.57, 41.6) * mm, "end": v(128.72, 41.6) * mm});
            skLineSegment(sketch, "E16.3.17.20", {"start": v(128.72, 41.6) * mm, "end": v(130.3, 38.86) * mm});
            skLineSegment(sketch, "E16.6.17.20", {"start": v(130.3, 38.86) * mm, "end": v(128.72, 36.13) * mm});
            skCircle(sketch, "E16.9.17.20", {"center": v(127.14, 38.86) * mm, "radius": 2.73 * mm, "construction": true});
            skLineSegment(sketch, "E16.11.17.20", {"start": v(128.72, 36.13) * mm, "end": v(125.57, 36.13) * mm});
            skLineSegment(sketch, "E16.14.17.20", {"start": v(125.57, 36.13) * mm, "end": v(124, 38.86) * mm});
            skLineSegment(sketch, "E16.17.17.20", {"start": v(124, 38.86) * mm, "end": v(125.57, 41.6) * mm});
            skLineSegment(sketch, "E16.0.17.21", {"start": v(125.57, 50.23) * mm, "end": v(128.72, 50.23) * mm});
            skLineSegment(sketch, "E16.3.17.21", {"start": v(128.72, 50.23) * mm, "end": v(130.3, 47.5) * mm});
            skLineSegment(sketch, "E16.6.17.21", {"start": v(130.3, 47.5) * mm, "end": v(128.72, 44.77) * mm});
            skCircle(sketch, "E16.9.17.21", {"center": v(127.14, 47.5) * mm, "radius": 2.73 * mm, "construction": true});
            skLineSegment(sketch, "E16.11.17.21", {"start": v(128.72, 44.77) * mm, "end": v(125.57, 44.77) * mm});
            skLineSegment(sketch, "E16.14.17.21", {"start": v(125.57, 44.77) * mm, "end": v(124, 47.5) * mm});
            skLineSegment(sketch, "E16.17.17.21", {"start": v(124, 47.5) * mm, "end": v(125.57, 50.23) * mm});
            skLineSegment(sketch, "E16.0.17.22", {"start": v(125.57, 58.86) * mm, "end": v(128.72, 58.86) * mm});
            skLineSegment(sketch, "E16.3.17.22", {"start": v(128.72, 58.86) * mm, "end": v(130.3, 56.13) * mm});
            skLineSegment(sketch, "E16.6.17.22", {"start": v(130.3, 56.13) * mm, "end": v(128.72, 53.4) * mm});
            skCircle(sketch, "E16.9.17.22", {"center": v(127.14, 56.13) * mm, "radius": 2.73 * mm, "construction": true});
            skLineSegment(sketch, "E16.11.17.22", {"start": v(128.72, 53.4) * mm, "end": v(125.57, 53.4) * mm});
            skLineSegment(sketch, "E16.14.17.22", {"start": v(125.57, 53.4) * mm, "end": v(124, 56.13) * mm});
            skLineSegment(sketch, "E16.17.17.22", {"start": v(124, 56.13) * mm, "end": v(125.57, 58.86) * mm});
            skLineSegment(sketch, "E16.0.17.23", {"start": v(125.57, 67.5) * mm, "end": v(128.72, 67.5) * mm});
            skLineSegment(sketch, "E16.3.17.23", {"start": v(128.72, 67.5) * mm, "end": v(130.3, 64.77) * mm});
            skLineSegment(sketch, "E16.6.17.23", {"start": v(130.3, 64.77) * mm, "end": v(128.72, 62.04) * mm});
            skCircle(sketch, "E16.9.17.23", {"center": v(127.14, 64.77) * mm, "radius": 2.73 * mm, "construction": true});
            skLineSegment(sketch, "E16.11.17.23", {"start": v(128.72, 62.04) * mm, "end": v(125.57, 62.04) * mm});
            skLineSegment(sketch, "E16.14.17.23", {"start": v(125.57, 62.04) * mm, "end": v(124, 64.77) * mm});
            skLineSegment(sketch, "E16.17.17.23", {"start": v(124, 64.77) * mm, "end": v(125.57, 67.5) * mm});
            skLineSegment(sketch, "E16.0.17.24", {"start": v(125.57, 76.14) * mm, "end": v(128.72, 76.14) * mm});
            skLineSegment(sketch, "E16.3.17.24", {"start": v(128.72, 76.14) * mm, "end": v(130.3, 73.4) * mm});
            skLineSegment(sketch, "E16.6.17.24", {"start": v(130.3, 73.4) * mm, "end": v(128.72, 70.68) * mm});
            skCircle(sketch, "E16.9.17.24", {"center": v(127.14, 73.4) * mm, "radius": 2.73 * mm, "construction": true});
            skLineSegment(sketch, "E16.11.17.24", {"start": v(128.72, 70.68) * mm, "end": v(125.57, 70.68) * mm});
            skLineSegment(sketch, "E16.14.17.24", {"start": v(125.57, 70.68) * mm, "end": v(124, 73.4) * mm});
            skLineSegment(sketch, "E16.17.17.24", {"start": v(124, 73.4) * mm, "end": v(125.57, 76.14) * mm});
            skLineSegment(sketch, "E16.0.18.20", {"start": v(140.53, 41.6) * mm, "end": v(143.68, 41.6) * mm});
            skLineSegment(sketch, "E16.3.18.20", {"start": v(143.68, 41.6) * mm, "end": v(145.25, 38.86) * mm});
            skLineSegment(sketch, "E16.6.18.20", {"start": v(145.25, 38.86) * mm, "end": v(143.68, 36.13) * mm});
            skCircle(sketch, "E16.9.18.20", {"center": v(142.1, 38.86) * mm, "radius": 2.73 * mm, "construction": true});
            skLineSegment(sketch, "E16.11.18.20", {"start": v(143.68, 36.13) * mm, "end": v(140.53, 36.13) * mm});
            skLineSegment(sketch, "E16.14.18.20", {"start": v(140.53, 36.13) * mm, "end": v(138.95, 38.86) * mm});
            skLineSegment(sketch, "E16.17.18.20", {"start": v(138.95, 38.86) * mm, "end": v(140.53, 41.6) * mm});
            skLineSegment(sketch, "E16.0.18.21", {"start": v(140.53, 50.23) * mm, "end": v(143.68, 50.23) * mm});
            skLineSegment(sketch, "E16.3.18.21", {"start": v(143.68, 50.23) * mm, "end": v(145.25, 47.5) * mm});
            skLineSegment(sketch, "E16.6.18.21", {"start": v(145.25, 47.5) * mm, "end": v(143.68, 44.77) * mm});
            skCircle(sketch, "E16.9.18.21", {"center": v(142.1, 47.5) * mm, "radius": 2.73 * mm, "construction": true});
            skLineSegment(sketch, "E16.11.18.21", {"start": v(143.68, 44.77) * mm, "end": v(140.53, 44.77) * mm});
            skLineSegment(sketch, "E16.14.18.21", {"start": v(140.53, 44.77) * mm, "end": v(138.95, 47.5) * mm});
            skLineSegment(sketch, "E16.17.18.21", {"start": v(138.95, 47.5) * mm, "end": v(140.53, 50.23) * mm});
            skLineSegment(sketch, "E16.0.18.22", {"start": v(140.53, 58.86) * mm, "end": v(143.68, 58.86) * mm});
            skLineSegment(sketch, "E16.3.18.22", {"start": v(143.68, 58.86) * mm, "end": v(145.25, 56.13) * mm});
            skLineSegment(sketch, "E16.6.18.22", {"start": v(145.25, 56.13) * mm, "end": v(143.68, 53.4) * mm});
            skCircle(sketch, "E16.9.18.22", {"center": v(142.1, 56.13) * mm, "radius": 2.73 * mm, "construction": true});
            skLineSegment(sketch, "E16.11.18.22", {"start": v(143.68, 53.4) * mm, "end": v(140.53, 53.4) * mm});
            skLineSegment(sketch, "E16.14.18.22", {"start": v(140.53, 53.4) * mm, "end": v(138.95, 56.13) * mm});
            skLineSegment(sketch, "E16.17.18.22", {"start": v(138.95, 56.13) * mm, "end": v(140.53, 58.86) * mm});
            skLineSegment(sketch, "E16.0.18.23", {"start": v(140.53, 67.5) * mm, "end": v(143.68, 67.5) * mm});
            skLineSegment(sketch, "E16.3.18.23", {"start": v(143.68, 67.5) * mm, "end": v(145.25, 64.77) * mm});
            skLineSegment(sketch, "E16.6.18.23", {"start": v(145.25, 64.77) * mm, "end": v(143.68, 62.04) * mm});
            skCircle(sketch, "E16.9.18.23", {"center": v(142.1, 64.77) * mm, "radius": 2.73 * mm, "construction": true});
            skLineSegment(sketch, "E16.11.18.23", {"start": v(143.68, 62.04) * mm, "end": v(140.53, 62.04) * mm});
            skLineSegment(sketch, "E16.14.18.23", {"start": v(140.53, 62.04) * mm, "end": v(138.95, 64.77) * mm});
            skLineSegment(sketch, "E16.17.18.23", {"start": v(138.95, 64.77) * mm, "end": v(140.53, 67.5) * mm});
            skLineSegment(sketch, "E16.0.18.24", {"start": v(140.53, 76.14) * mm, "end": v(143.68, 76.14) * mm});
            skLineSegment(sketch, "E16.3.18.24", {"start": v(143.68, 76.14) * mm, "end": v(145.25, 73.4) * mm});
            skLineSegment(sketch, "E16.6.18.24", {"start": v(145.25, 73.4) * mm, "end": v(143.68, 70.68) * mm});
            skCircle(sketch, "E16.9.18.24", {"center": v(142.1, 73.4) * mm, "radius": 2.73 * mm, "construction": true});
            skLineSegment(sketch, "E16.11.18.24", {"start": v(143.68, 70.68) * mm, "end": v(140.53, 70.68) * mm});
            skLineSegment(sketch, "E16.14.18.24", {"start": v(140.53, 70.68) * mm, "end": v(138.95, 73.4) * mm});
            skLineSegment(sketch, "E16.17.18.24", {"start": v(138.95, 73.4) * mm, "end": v(140.53, 76.14) * mm});
            skLineSegment(sketch, "E16.0.19.20", {"start": v(155.48, 41.6) * mm, "end": v(158.64, 41.6) * mm});
            skLineSegment(sketch, "E16.3.19.20", {"start": v(158.64, 41.6) * mm, "end": v(160.21, 38.86) * mm});
            skLineSegment(sketch, "E16.6.19.20", {"start": v(160.21, 38.86) * mm, "end": v(158.64, 36.13) * mm});
            skCircle(sketch, "E16.9.19.20", {"center": v(157.06, 38.86) * mm, "radius": 2.73 * mm, "construction": true});
            skLineSegment(sketch, "E16.11.19.20", {"start": v(158.64, 36.13) * mm, "end": v(155.48, 36.13) * mm});
            skLineSegment(sketch, "E16.14.19.20", {"start": v(155.48, 36.13) * mm, "end": v(153.9, 38.86) * mm});
            skLineSegment(sketch, "E16.17.19.20", {"start": v(153.9, 38.86) * mm, "end": v(155.48, 41.6) * mm});
            skLineSegment(sketch, "E16.0.19.21", {"start": v(155.48, 50.23) * mm, "end": v(158.64, 50.23) * mm});
            skLineSegment(sketch, "E16.3.19.21", {"start": v(158.64, 50.23) * mm, "end": v(160.21, 47.5) * mm});
            skLineSegment(sketch, "E16.6.19.21", {"start": v(160.21, 47.5) * mm, "end": v(158.64, 44.77) * mm});
            skCircle(sketch, "E16.9.19.21", {"center": v(157.06, 47.5) * mm, "radius": 2.73 * mm, "construction": true});
            skLineSegment(sketch, "E16.11.19.21", {"start": v(158.64, 44.77) * mm, "end": v(155.48, 44.77) * mm});
            skLineSegment(sketch, "E16.14.19.21", {"start": v(155.48, 44.77) * mm, "end": v(153.9, 47.5) * mm});
            skLineSegment(sketch, "E16.17.19.21", {"start": v(153.9, 47.5) * mm, "end": v(155.48, 50.23) * mm});
            skLineSegment(sketch, "E16.0.19.22", {"start": v(155.48, 58.86) * mm, "end": v(158.64, 58.86) * mm});
            skLineSegment(sketch, "E16.3.19.22", {"start": v(158.64, 58.86) * mm, "end": v(160.21, 56.13) * mm});
            skLineSegment(sketch, "E16.6.19.22", {"start": v(160.21, 56.13) * mm, "end": v(158.64, 53.4) * mm});
            skCircle(sketch, "E16.9.19.22", {"center": v(157.06, 56.13) * mm, "radius": 2.73 * mm, "construction": true});
            skLineSegment(sketch, "E16.11.19.22", {"start": v(158.64, 53.4) * mm, "end": v(155.48, 53.4) * mm});
            skLineSegment(sketch, "E16.14.19.22", {"start": v(155.48, 53.4) * mm, "end": v(153.9, 56.13) * mm});
            skLineSegment(sketch, "E16.17.19.22", {"start": v(153.9, 56.13) * mm, "end": v(155.48, 58.86) * mm});
            skLineSegment(sketch, "E16.0.19.23", {"start": v(155.48, 67.5) * mm, "end": v(158.64, 67.5) * mm});
            skLineSegment(sketch, "E16.3.19.23", {"start": v(158.64, 67.5) * mm, "end": v(160.21, 64.77) * mm});
            skLineSegment(sketch, "E16.6.19.23", {"start": v(160.21, 64.77) * mm, "end": v(158.64, 62.04) * mm});
            skCircle(sketch, "E16.9.19.23", {"center": v(157.06, 64.77) * mm, "radius": 2.73 * mm, "construction": true});
            skLineSegment(sketch, "E16.11.19.23", {"start": v(158.64, 62.04) * mm, "end": v(155.48, 62.04) * mm});
            skLineSegment(sketch, "E16.14.19.23", {"start": v(155.48, 62.04) * mm, "end": v(153.9, 64.77) * mm});
            skLineSegment(sketch, "E16.17.19.23", {"start": v(153.9, 64.77) * mm, "end": v(155.48, 67.5) * mm});
            skLineSegment(sketch, "E16.0.19.24", {"start": v(155.48, 76.14) * mm, "end": v(158.64, 76.14) * mm});
            skLineSegment(sketch, "E16.3.19.24", {"start": v(158.64, 76.14) * mm, "end": v(160.21, 73.4) * mm});
            skLineSegment(sketch, "E16.6.19.24", {"start": v(160.21, 73.4) * mm, "end": v(158.64, 70.68) * mm});
            skCircle(sketch, "E16.9.19.24", {"center": v(157.06, 73.4) * mm, "radius": 2.73 * mm, "construction": true});
            skLineSegment(sketch, "E16.11.19.24", {"start": v(158.64, 70.68) * mm, "end": v(155.48, 70.68) * mm});
            skLineSegment(sketch, "E16.14.19.24", {"start": v(155.48, 70.68) * mm, "end": v(153.9, 73.4) * mm});
            skLineSegment(sketch, "E16.17.19.24", {"start": v(153.9, 73.4) * mm, "end": v(155.48, 76.14) * mm});
            skCircle(sketch, "E17", {"center": v(-127.14, -133.86) * mm, "radius": 1.27 * mm});
            skCircle(sketch, "E18", {"center": v(-119.66, -129.54) * mm, "radius": 1 * mm});
            skSolve(sketch);
        }
        {
            var Q0;
            Q0=qSketchRegion(id+"F2",true);
            extrude(context, id + "F3", {"entities" : qUnion([Q0]), "operationType" : NewBodyOperationType.REMOVE, "oppositeDirection" : true, "depth" : 25.4 * mm, "offsetDistance" : 25.4 * mm});
        }
        {
            var Q0;
            Q0=makeQuery(id+"F1.opExtrude","CAP_FACE",FACE,{"disambiguationData":[OSD([sQuery(id+"F0.wireOp",EDGE,"E0")])],"isStart":false});
            var sketch = newSketch(context, id + "F4", { "sketchPlane" : qUnion([Q0])});
            skCircle(sketch, "E19", {"center": v(0, 0) * mm, "radius": 115.89 * mm});
            skCircle(sketch, "E20", {"center": v(0, 0) * mm, "radius": 123.02 * mm});
            skSolve(sketch);
        }
        {
            var Q0;
            Q0=qSketchRegion(id+"F4",true);
            var Q1;
            Q1=makeQuery(id+"F1.opExtrude","CAP_FACE",FACE,{"disambiguationData":[OSD([sQuery(id+"F0.wireOp",EDGE,"E0")])],"isStart":true});
            extrude(context, id + "F5", {"entities" : qUnion([Q0]), "operationType" : NewBodyOperationType.ADD, "endBound" : BoundingType.UP_TO_SURFACE, "oppositeDirection" : true, "depth" : 25.4 * mm, "endBoundEntityFace" : qUnion([Q1]), "offsetDistance" : 25.4 * mm});
        }
        {
            var Q0;
            Q0=makeQuery(id+"F5.boolean.opBoolean","MERGE",FACE,{"derivedFrom":[makeQuery(id+"F1.opExtrude","CAP_FACE",FACE,{"disambiguationData":[OSD([sQuery(id+"F0.wireOp",EDGE,"E0")])],"isStart":false}),makeQuery(id+"F5.opExtrude","CAP_FACE",FACE,{"disambiguationData":[OSD([sQuery(id+"F4.wireOp",EDGE,"gzat5XN6-aFc3-cK17-7gGf-ptE3Ki8R4cpB"),sQuery(id+"F4.wireOp",EDGE,"E19")])],"isStart":true})]});
            var sketch = newSketch(context, id + "F6", { "sketchPlane" : qUnion([Q0])});
            skLineSegment(sketch, "E21.bottom", {"start": v(-111.14, -36.87) * mm, "end": v(-108.38, -36.87) * mm});
            skLineSegment(sketch, "E21.top", {"start": v(-111.14, -39.87) * mm, "end": v(-108.38, -39.87) * mm});
            skLineSegment(sketch, "E21.left", {"start": v(-111.14, -36.87) * mm, "end": v(-111.14, -39.87) * mm});
            skLineSegment(sketch, "E21.right", {"start": v(-108.38, -36.87) * mm, "end": v(-108.38, -39.87) * mm});
            skLineSegment(sketch, "E22.bottom", {"start": v(-89.68, -74.2) * mm, "end": v(-86.66, -74.2) * mm});
            skLineSegment(sketch, "E22.top", {"start": v(-89.68, -76.77) * mm, "end": v(-86.66, -76.77) * mm});
            skLineSegment(sketch, "E22.left", {"start": v(-89.68, -74.2) * mm, "end": v(-89.68, -76.77) * mm});
            skLineSegment(sketch, "E22.right", {"start": v(-86.66, -74.2) * mm, "end": v(-86.66, -76.77) * mm});
            skLineSegment(sketch, "E23.bottom", {"start": v(-22.86, -113.02) * mm, "end": v(-19.56, -113.02) * mm});
            skLineSegment(sketch, "E23.top", {"start": v(-22.86, -115.1) * mm, "end": v(-19.56, -115.1) * mm});
            skLineSegment(sketch, "E23.left", {"start": v(-22.86, -113.02) * mm, "end": v(-22.86, -115.1) * mm});
            skLineSegment(sketch, "E23.right", {"start": v(-19.56, -113.02) * mm, "end": v(-19.56, -115.1) * mm});
            skLineSegment(sketch, "E24.bottom", {"start": v(23.22, -112.84) * mm, "end": v(19.66, -112.84) * mm});
            skLineSegment(sketch, "E24.top", {"start": v(23.22, -115.45) * mm, "end": v(19.66, -115.45) * mm});
            skLineSegment(sketch, "E24.left", {"start": v(23.22, -112.84) * mm, "end": v(23.22, -115.45) * mm});
            skLineSegment(sketch, "E24.right", {"start": v(19.66, -112.84) * mm, "end": v(19.66, -115.45) * mm});
            skLineSegment(sketch, "E25.bottom", {"start": v(89.64, -73.9) * mm, "end": v(86.67, -73.9) * mm});
            skLineSegment(sketch, "E25.top", {"start": v(89.64, -77.36) * mm, "end": v(86.67, -77.36) * mm});
            skLineSegment(sketch, "E25.left", {"start": v(89.64, -73.9) * mm, "end": v(89.64, -77.36) * mm});
            skLineSegment(sketch, "E25.right", {"start": v(86.67, -73.9) * mm, "end": v(86.67, -77.36) * mm});
            skLineSegment(sketch, "E26.bottom", {"start": v(110.54, -36.67) * mm, "end": v(107.96, -36.67) * mm});
            skLineSegment(sketch, "E26.top", {"start": v(110.54, -40.43) * mm, "end": v(107.96, -40.43) * mm});
            skLineSegment(sketch, "E26.left", {"start": v(110.54, -36.67) * mm, "end": v(110.54, -40.43) * mm});
            skLineSegment(sketch, "E26.right", {"start": v(107.96, -36.67) * mm, "end": v(107.96, -40.43) * mm});
            skSolve(sketch);
        }
        {
            var Q0;
            Q0=qSketchRegion(id+"F6",true);
            var Q1;
            Q1=makeQuery(id+"F5.boolean.opBoolean","MERGE",FACE,{"derivedFrom":[makeQuery(id+"F1.opExtrude","CAP_FACE",FACE,{"disambiguationData":[OSD([sQuery(id+"F0.wireOp",EDGE,"E0")])],"isStart":true}),makeQuery(id+"F5.opExtrude","CAP_FACE",FACE,{"disambiguationData":[OSD([sQuery(id+"F4.wireOp",EDGE,"gzat5XN6-aFc3-cK17-7gGf-ptE3Ki8R4cpB"),sQuery(id+"F4.wireOp",EDGE,"E19")])],"isStart":false})]});
            extrude(context, id + "F7", {"entities" : qUnion([Q0]), "operationType" : NewBodyOperationType.ADD, "endBound" : BoundingType.UP_TO_SURFACE, "oppositeDirection" : true, "depth" : 25.4 * mm, "endBoundEntityFace" : qUnion([Q1]), "offsetDistance" : 25.4 * mm});
        }
        {
            var Q0;
            Q0=makeQuery(id+"F7.boolean.opBoolean","MERGE",FACE,{"derivedFrom":[makeQuery(id+"F5.boolean.opBoolean","MERGE",FACE,{"derivedFrom":[makeQuery(id+"F1.opExtrude","CAP_FACE",FACE,{"disambiguationData":[OSD([sQuery(id+"F0.wireOp",EDGE,"E0")])],"isStart":false}),makeQuery(id+"F5.opExtrude","CAP_FACE",FACE,{"disambiguationData":[OSD([sQuery(id+"F4.wireOp",EDGE,"E19"),sQuery(id+"F4.wireOp",EDGE,"E20")])],"isStart":true})]}),makeQuery(id+"F7.opExtrude","CAP_FACE",FACE,{"disambiguationData":[OSD([sQuery(id+"F6.wireOp",EDGE,"E21.bottom"),sQuery(id+"F6.wireOp",EDGE,"E21.top"),sQuery(id+"F6.wireOp",EDGE,"E21.left"),sQuery(id+"F6.wireOp",EDGE,"E21.right")])],"isStart":true}),makeQuery(id+"F7.opExtrude","CAP_FACE",FACE,{"disambiguationData":[OSD([sQuery(id+"F6.wireOp",EDGE,"E22.bottom"),sQuery(id+"F6.wireOp",EDGE,"E22.top"),sQuery(id+"F6.wireOp",EDGE,"E22.left"),sQuery(id+"F6.wireOp",EDGE,"E22.right")])],"isStart":true}),makeQuery(id+"F7.opExtrude","CAP_FACE",FACE,{"disambiguationData":[OSD([sQuery(id+"F6.wireOp",EDGE,"E23.bottom"),sQuery(id+"F6.wireOp",EDGE,"E23.top"),sQuery(id+"F6.wireOp",EDGE,"E23.left"),sQuery(id+"F6.wireOp",EDGE,"E23.right")])],"isStart":true}),makeQuery(id+"F7.opExtrude","CAP_FACE",FACE,{"disambiguationData":[OSD([sQuery(id+"F6.wireOp",EDGE,"E24.bottom"),sQuery(id+"F6.wireOp",EDGE,"E24.top"),sQuery(id+"F6.wireOp",EDGE,"E24.left"),sQuery(id+"F6.wireOp",EDGE,"E24.right")])],"isStart":true}),makeQuery(id+"F7.opExtrude","CAP_FACE",FACE,{"disambiguationData":[OSD([sQuery(id+"F6.wireOp",EDGE,"E25.bottom"),sQuery(id+"F6.wireOp",EDGE,"E25.top"),sQuery(id+"F6.wireOp",EDGE,"E25.left"),sQuery(id+"F6.wireOp",EDGE,"E25.right")])],"isStart":true}),makeQuery(id+"F7.opExtrude","CAP_FACE",FACE,{"disambiguationData":[OSD([sQuery(id+"F6.wireOp",EDGE,"E26.bottom"),sQuery(id+"F6.wireOp",EDGE,"E26.top"),sQuery(id+"F6.wireOp",EDGE,"E26.left"),sQuery(id+"F6.wireOp",EDGE,"E26.right")])],"isStart":true})]});
            var sketch = newSketch(context, id + "F8", { "sketchPlane" : qUnion([Q0])});
            skLineSegment(sketch, "E27.bottom", {"start": v(-152.36, 126.72) * mm, "end": v(169.88, 126.72) * mm});
            skLineSegment(sketch, "E27.top", {"start": v(-152.36, 0) * mm, "end": v(169.88, 0) * mm});
            skLineSegment(sketch, "E27.left", {"start": v(-152.36, 126.72) * mm, "end": v(-152.36, 0) * mm});
            skLineSegment(sketch, "E27.right", {"start": v(169.88, 126.72) * mm, "end": v(169.88, 0) * mm});
            skSolve(sketch);
        }
        {
            var Q0;
            Q0=qSketchRegion(id+"F8",true);
            extrude(context, id + "F9", {"entities" : qUnion([Q0]), "operationType" : NewBodyOperationType.REMOVE, "oppositeDirection" : true, "depth" : 25.4 * mm, "offsetDistance" : 25.4 * mm});
        }
        {
            var Q0;
            Q0=makeQuery(id+"F1.opExtrude","SWEPT_BODY",BODY,{"disambiguationData":[OSD([sQuery(id+"F0.wireOp",EDGE,"E0")])]});
            var Q1;
            Q1=qCreatedBy(makeId("Front.planeOp"),FACE);
            mirror(context, id + "F10", {"operationType" : NewBodyOperationType.ADD, "entities" : qUnion([Q0]), "mirrorPlane" : qUnion([Q1])});
        }
    });
